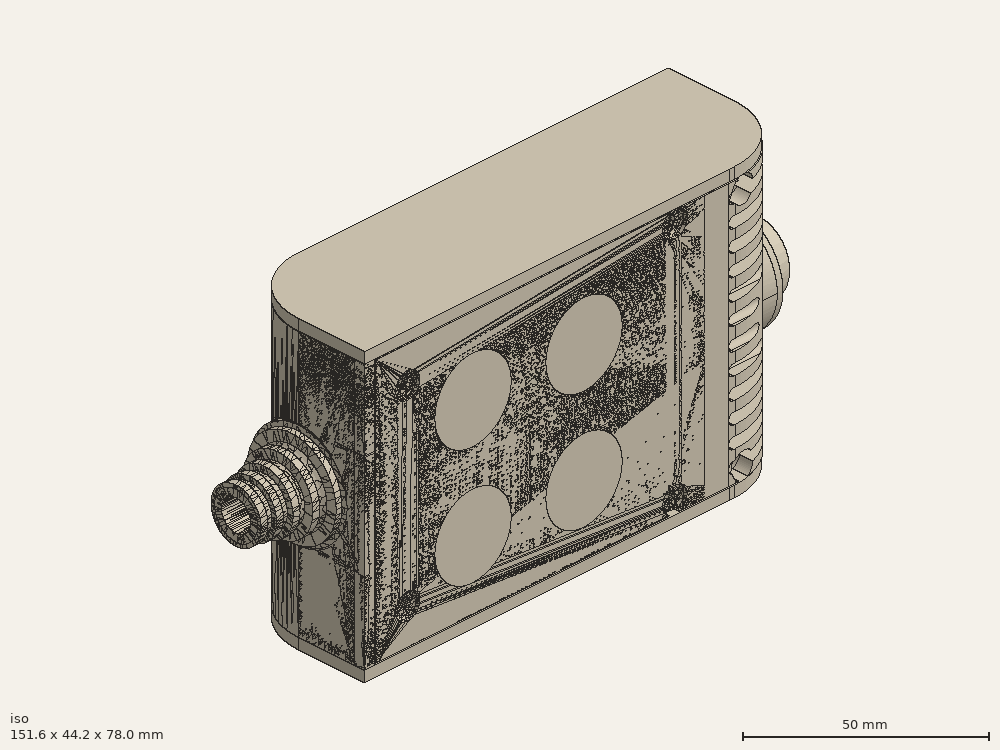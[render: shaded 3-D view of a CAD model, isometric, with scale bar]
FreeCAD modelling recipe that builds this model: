
FCSTD DOCUMENT  (FreeCAD 0.19R0.19.2)
Label: enclosure_181FCStd
License: All rights reserved
LicenseURL: http://en.wikipedia.org/wiki/All_rights_reserved
objects: Part::Revolution×152, Part::MultiFuse×146, Part::Feature×146, Sketcher::SketchObject×84, Part::Cut×70, Part::Cylinder×70, Part::Extrusion×67, Part::Fillet×58, Part::Box×36, App::MeasureDistance×4, PartDesign::Body×2, Image::ImagePlane×1
note: 831 computed .brp shape members not serialized (recipe doc carries the construction recipe); baked Part::Feature solids carry a one-line shape summary decoded from their .brp

FEATURE [Sketcher::SketchObject] Sketch  label="topSketch"
  FullyConstrained = true
  sketch-geometry (20):
    g0: LineSegment StartX=5.21097e-06 StartY=3 StartZ=0 EndX=5.21097e-06 EndY=19 EndZ=0
    g1: ArcOfCircle CenterX=19 CenterY=19 CenterZ=0 NormalX=0 NormalY=0 NormalZ=1 AngleXU=0 Radius=19 StartAngle=1.5708 EndAngle=3.14159
    g2: ArcOfCircle CenterX=19 CenterY=19 CenterZ=0 NormalX=0 NormalY=0 NormalZ=1 AngleXU=0 Radius=16 StartAngle=1.5708 EndAngle=3.14159
    g3: LineSegment StartX=114 StartY=35 StartZ=0 EndX=19 EndY=35 EndZ=0
    g4: LineSegment StartX=5.21097e-06 StartY=3 StartZ=0 EndX=5.21097e-06 EndY=0 EndZ=0
    g5: LineSegment StartX=3 StartY=0 StartZ=0 EndX=5.21097e-06 EndY=0 EndZ=0
    g6: LineSegment StartX=3 StartY=19 StartZ=0 EndX=3 EndY=0 EndZ=0
    g7: LineSegment StartX=19 StartY=38 StartZ=0 EndX=124 EndY=38 EndZ=0
    g8: Circle CenterX=119 CenterY=35 CenterZ=0 NormalX=0 NormalY=0 NormalZ=1 AngleXU=0 Radius=1
    g9: Circle CenterX=121 CenterY=35 CenterZ=0 NormalX=0 NormalY=0 NormalZ=1 AngleXU=0 Radius=1
    g10: Circle CenterX=121 CenterY=33 CenterZ=0 NormalX=0 NormalY=0 NormalZ=1 AngleXU=0 Radius=1
    g11: BSplineCurve PolesCount=3 KnotsCount=2 Degree=2 IsPeriodic=0
    g12: GeomPoint X=119 Y=35 Z=0
    g13: GeomPoint X=121 Y=33 Z=0
    g14: LineSegment StartX=119 StartY=35 StartZ=0 EndX=114 EndY=35 EndZ=0
    g15: ArcOfCircle CenterX=105 CenterY=19 CenterZ=0 NormalX=0 NormalY=0 NormalZ=1 AngleXU=0 Radius=19 StartAngle=5.7297 EndAngle=6.28319
    g16: ArcOfCircle CenterX=105 CenterY=19 CenterZ=0 NormalX=0 NormalY=0 NormalZ=1 AngleXU=0 Radius=16 StartAngle=5.60905 EndAngle=6.28319
    g17: LineSegment StartX=121 StartY=33 StartZ=0 EndX=121 EndY=19 EndZ=0
    g18: LineSegment StartX=124 StartY=38 StartZ=0 EndX=124 EndY=19 EndZ=0
    g19: LineSegment StartX=117.5 StartY=9.01251 StartZ=0 EndX=121.163 EndY=9.0125 EndZ=0
  constraints (46):
    c: Vertical(g0)
    c: Block(g0)
    c: Coincident(g1,g0)
    c: Block(g1)
    c: Coincident(g2,g1)
    c: Block(g2)
    c: Coincident(g3,g2)
    c: Horizontal(g3)
    c: Tangent(g3,g2)
    c: Coincident(g4,g0)
    c: Distance(g4) = 3
    c: Vertical(g4)
    c: Coincident(g5,g4)
    c: Horizontal(g5)
    c: Coincident(g6,g2)
    c: Coincident(g6,g5)
    c: Vertical(g6)
    c: Horizontal(g7)
    c: Distance(g7) = 105
    c: Coincident(g7,g1)
    c: Block(g3)
    c: Weight(g8) = 1
    c: Equal(g8,g9)
    c: Equal(g8,g10)
    c: InternalAlignment(g8,g11)
    c: InternalAlignment(g9,g11)
    c: InternalAlignment(g10,g11)
    c: InternalAlignment(g12,g11)
    c: InternalAlignment(g13,g11)
    c: Block(g11)
    c: Coincident(g14,g11)
    c: Coincident(g14,g3)
    c: Horizontal(g14)
    c: Block(g15)
    c: Coincident(g16,g15)
    c: Block(g16)
    c: Coincident(g17,g11)
    c: Coincident(g17,g16)
    c: Vertical(g17)
    c: Distance(g17) = 14
    c: Coincident(g18,g7)
    c: Coincident(g18,g15)
    c: Vertical(g18)
    c: Distance(g18) = 19
    c: Coincident(g19,g16)
    c: Coincident(g19,g15)
FEATURE [Sketcher::SketchObject] Sketch001  label="bottomSketch"
  FullyConstrained = true
  sketch-geometry (32):
    g0: LineSegment StartX=3.3 StartY=-6.03275e-07 StartZ=0 EndX=98 EndY=-6.03275e-07 EndZ=0
    g1: ArcOfCircle CenterX=98 CenterY=19 CenterZ=0 NormalX=0 NormalY=0 NormalZ=1 AngleXU=0 Radius=19 StartAngle=4.71239 EndAngle=5.71103
    g2: LineSegment StartX=6.3 StartY=8 StartZ=0 EndX=3.3 EndY=8 EndZ=0
    g3: LineSegment StartX=3.3 StartY=8 StartZ=0 EndX=3.3 EndY=-6.03275e-07 EndZ=0
    g4: ArcOfCircle CenterX=8.3 CenterY=5 CenterZ=0 NormalX=0 NormalY=0 NormalZ=1 AngleXU=0 Radius=2 StartAngle=3.14159 EndAngle=4.71239
    g5: LineSegment StartX=6.3 StartY=8 StartZ=0 EndX=6.3 EndY=5 EndZ=0
    g6: ArcOfCircle CenterX=98 CenterY=19 CenterZ=0 NormalX=0 NormalY=0 NormalZ=1 AngleXU=0 Radius=12.7 StartAngle=4.71239 EndAngle=6.28319
    g7: LineSegment StartX=94.7 StartY=3 StartZ=0 EndX=8.3 EndY=3 EndZ=0
    g8-g12: Circle x5 (B-spline internal-alignment scaffolding for g13; pole/knot coordinates omitted)
    g13: BSplineCurve PolesCount=5 KnotsCount=3 Degree=3 IsPeriodic=0
    g14: GeomPoint X=98 Y=6.3 Z=0
    g15: GeomPoint X=96.3938 Y=4.71946 Z=0
    g16: GeomPoint X=94.7 Y=3 Z=0
    g17-g23: Circle x7 (B-spline internal-alignment scaffolding for g24; pole/knot coordinates omitted)
    g24: BSplineCurve PolesCount=7 KnotsCount=5 Degree=3 IsPeriodic=0
    g25-g29: GeomPoint x5 (B-spline internal-alignment scaffolding for g24; pole/knot coordinates omitted)
    g30: ArcOfCircle CenterX=98 CenterY=19 CenterZ=0 NormalX=0 NormalY=0 NormalZ=1 AngleXU=0 Radius=15.7 StartAngle=5.81226 EndAngle=6.28319
    g31: LineSegment StartX=110.7 StartY=19 StartZ=0 EndX=113.7 EndY=19 EndZ=0
  constraints (41):
    c: Horizontal(g0)
    c: Coincident(g1,g0)
    c: Block(g1)
    c: Horizontal(g2)
    c: Distance(g2) = 3
    c: Coincident(g3,g2)
    c: Vertical(g3)
    c: Coincident(g3,g0)
    c: Block(g4)
    c: Block(g2)
    c: Coincident(g5,g2)
    c: Coincident(g5,g4)
    c: Vertical(g5)
    c: Coincident(g6,g1)
    c: Block(g6)
    c: Coincident(g7,g4)
    c: Horizontal(g7)
    c: Block(g0)
    c: Block(g7)
    c: Block(g3)
    c: Coincident(g13,g6)
    c: Weight(g8) = 1
    c: Equal(g8, g9-g12) x4
    c: Coincident(g13,g7)
    c: InternalAlignment(g8-g12 -> g13) x5
    c: InternalAlignment(g14,g13)
    c: InternalAlignment(g15,g13)
    c: InternalAlignment(g16,g13)
    c: Block(g13)
    c: Weight(g17) = 1
    c: Equal(g17, g18-g23) x6
    c: Coincident(g24,g1)
    c: InternalAlignment(g17-g23 -> g24) x7
    c: InternalAlignment(g25-g29 -> g24) x5
    c: Block(g24)
    c: Coincident(g30,g24)
    c: Coincident(g31,g6)
    c: Coincident(g31,g30)
    c: Horizontal(g31)
    c: Block(g31)
    c: Block(g30)
FEATURE [Part::Extrusion] Extrude  label="top"
  Base = -> Sketch
  Dir = (0,0,1)
  DirMode = 2
  FaceMakerClass = Part::FaceMakerBullseye
  LengthFwd = 72
  LengthRev = 0
  Solid = true
  Symmetric = false
FEATURE [Part::Extrusion] Extrude001  label="bottom"
  Base = -> Sketch001
  Dir = (0,0,1)
  DirMode = 2
  FaceMakerClass = Part::FaceMakerBullseye
  LengthFwd = 71.4
  LengthRev = 0
  Placement = pos=(0,0,0.3) rot=(0,0,1;0rad)
  Solid = true
  Symmetric = false
FEATURE [Sketcher::SketchObject] Sketch002  label="topSketch001"
  FullyConstrained = true
  sketch-geometry (8):
    g0: ArcOfCircle CenterX=19 CenterY=19.0975 CenterZ=0 NormalX=0 NormalY=0 NormalZ=1 AngleXU=0 Radius=18.9025 StartAngle=1.5708 EndAngle=3.14674
    g1: LineSegment StartX=0.0977805 StartY=19.0003 StartZ=0 EndX=0.0977805 EndY=0.000251602 EndZ=0
    g2: LineSegment StartX=19 StartY=38 StartZ=0 EndX=124 EndY=38 EndZ=0
    g3: LineSegment StartX=0.0977805 StartY=0.000251602 StartZ=0 EndX=105.098 EndY=0.000251602 EndZ=0
    g4: LineSegment StartX=124 StartY=38 StartZ=0 EndX=125.616 EndY=38 EndZ=0
    g5: LineSegment StartX=105.098 StartY=0.000251602 StartZ=0 EndX=106.713 EndY=0.000251602 EndZ=0
    g6: ArcOfCircle CenterX=106.616 CenterY=19 CenterZ=0 NormalX=0 NormalY=0 NormalZ=1 AngleXU=0 Radius=19 StartAngle=4.71754 EndAngle=6.28319
    g7: LineSegment StartX=125.616 StartY=38 StartZ=0 EndX=125.616 EndY=19 EndZ=0
  constraints (21):
    c: Block(g0)
    c: Coincident(g1,g0)
    c: Vertical(g1)
    c: Horizontal(g2)
    c: Distance(g2) = 105
    c: Coincident(g2,g0)
    c: Distance(g1) = 19
    c: Coincident(g3,g1)
    c: Horizontal(g3)
    c: Distance(g3) = 105
    c: Coincident(g4,g2)
    c: Horizontal(g4)
    c: Distance(g4) = 1.61553
    c: Horizontal(g5)
    c: Equal(g4,g5) = 1.61553
    c: Coincident(g5,g3)
    c: Block(g6)
    c: Coincident(g6,g5)
    c: Coincident(g7,g4)
    c: Coincident(g7,g6)
    c: Vertical(g7)
FEATURE [Part::Extrusion] Extrude002  label="sideA"
  Base = -> Sketch002
  Dir = (0,0,1)
  DirMode = 2
  FaceMakerClass = Part::FaceMakerBullseye
  LengthFwd = 3
  LengthRev = 0
  Placement = pos=(0,0,-3) rot=(0,0,1;0rad)
  Solid = true
  Symmetric = false
FEATURE [Sketcher::SketchObject] Sketch003  label="topSketch002"
  FullyConstrained = true
  sketch-geometry (6):
    g0: LineSegment StartX=19 StartY=38 StartZ=0 EndX=117 EndY=38 EndZ=0
    g1: ArcOfCircle CenterX=19 CenterY=19 CenterZ=0 NormalX=0 NormalY=0 NormalZ=1 AngleXU=0 Radius=19 StartAngle=1.5708 EndAngle=3.14159
    g2: LineSegment StartX=117 StartY=38 StartZ=0 EndX=117 EndY=19 EndZ=0
    g3: LineSegment StartX=98 StartY=1.0161e-12 StartZ=0 EndX=5.22862e-06 EndY=1.0161e-12 EndZ=0
    g4: LineSegment StartX=5.22862e-06 StartY=19 StartZ=0 EndX=5.22862e-06 EndY=1.0161e-12 EndZ=0
    g5: ArcOfCircle CenterX=98 CenterY=19 CenterZ=0 NormalX=0 NormalY=0 NormalZ=1 AngleXU=0 Radius=19 StartAngle=4.71239 EndAngle=6.28319
  constraints (16):
    c: Horizontal(g0)
    c: Distance(g0) = 98
    c: Coincident(g1,g0)
    c: Block(g1)
    c: Coincident(g2,g0)
    c: Vertical(g2)
    c: Distance(g2) = 19
    c: Horizontal(g3)
    c: Coincident(g4,g1)
    c: Vertical(g4)
    c: Coincident(g3,g4)
    c: Block(g3)
    c: Coincident(g5,g2)
    c: Coincident(g5,g3)
    c: Block(g0)
    c: Block(g5)
FEATURE [Sketcher::SketchObject] Sketch004
  FullyConstrained = true
  MapMode = 3
  Placement = pos=(0,0,0) rot=(1,0,0;1.5708rad)
  Support = -> [Extrude]
  sketch-geometry (8):
    g0: Circle CenterX=80.351 CenterY=-67.6202 CenterZ=0 NormalX=0 NormalY=0 NormalZ=1 AngleXU=0 Radius=2
    g1: Circle CenterX=80.351 CenterY=-67.6202 CenterZ=0 NormalX=0 NormalY=0 NormalZ=1 AngleXU=0 Radius=3
    g2: Circle CenterX=80.351 CenterY=-4.92017 CenterZ=0 NormalX=0 NormalY=0 NormalZ=1 AngleXU=0 Radius=2
    g3: Circle CenterX=80.351 CenterY=-4.92017 CenterZ=0 NormalX=0 NormalY=0 NormalZ=1 AngleXU=0 Radius=3
    g4: Circle CenterX=23.851 CenterY=-4.92017 CenterZ=0 NormalX=0 NormalY=0 NormalZ=1 AngleXU=0 Radius=2
    g5: Circle CenterX=23.851 CenterY=-4.92017 CenterZ=0 NormalX=0 NormalY=0 NormalZ=1 AngleXU=0 Radius=3
    g6: Circle CenterX=23.851 CenterY=-67.6202 CenterZ=0 NormalX=0 NormalY=0 NormalZ=1 AngleXU=0 Radius=2
    g7: Circle CenterX=23.851 CenterY=-67.6202 CenterZ=0 NormalX=0 NormalY=0 NormalZ=1 AngleXU=0 Radius=3
  constraints (8):
    c: Block(g3)
    c: Block(g2)
    c: Block(g1)
    c: Block(g0)
    c: Block(g6)
    c: Block(g7)
    c: Block(g4)
    c: Block(g5)
FEATURE [Part::Extrusion] Extrude004
  Base = -> Sketch004
  Dir = (0,-1,2e-16)
  DirMode = 2
  FaceMakerClass = Part::FaceMakerBullseye
  LengthFwd = 6
  LengthRev = 0
  Placement = pos=(0,9,0) rot=(0,0,1;0rad)
  Solid = true
  Symmetric = false
FEATURE [Sketcher::SketchObject] Sketch005
  FullyConstrained = true
  MapMode = 3
  Placement = pos=(0,0,0) rot=(1,0,0;1.5708rad)
  Support = -> [Extrude]
  sketch-geometry (8):
    g0: Circle CenterX=80.351 CenterY=-67.6202 CenterZ=0 NormalX=0 NormalY=0 NormalZ=1 AngleXU=0 Radius=3
    g1: Circle CenterX=80.351 CenterY=-4.92017 CenterZ=0 NormalX=0 NormalY=0 NormalZ=1 AngleXU=0 Radius=3
    g2: Circle CenterX=23.851 CenterY=-4.92017 CenterZ=0 NormalX=0 NormalY=0 NormalZ=1 AngleXU=0 Radius=3
    g3: Circle CenterX=23.851 CenterY=-67.6202 CenterZ=0 NormalX=0 NormalY=0 NormalZ=1 AngleXU=0 Radius=3
    g4: Circle CenterX=23.851 CenterY=-67.6202 CenterZ=0 NormalX=0 NormalY=0 NormalZ=1 AngleXU=0 Radius=5
    g5: Circle CenterX=80.351 CenterY=-67.6202 CenterZ=0 NormalX=0 NormalY=0 NormalZ=1 AngleXU=0 Radius=5
    g6: Circle CenterX=23.851 CenterY=-4.92017 CenterZ=0 NormalX=0 NormalY=0 NormalZ=1 AngleXU=0 Radius=5
    g7: Circle CenterX=80.351 CenterY=-4.92017 CenterZ=0 NormalX=0 NormalY=0 NormalZ=1 AngleXU=0 Radius=5
  constraints (8):
    c: Block(g1)
    c: Block(g0)
    c: Block(g3)
    c: Block(g2)
    c: Block(g5)
    c: Block(g4)
    c: Block(g6)
    c: Block(g7)
FEATURE [Part::Extrusion] Extrude005
  Base = -> Sketch005
  Dir = (0,-1,2e-16)
  DirMode = 2
  FaceMakerClass = Part::FaceMakerBullseye
  LengthFwd = 2
  LengthRev = 0
  Solid = true
  Symmetric = false
FEATURE [Sketcher::SketchObject] Sketch006
  FullyConstrained = true
  MapMode = 3
  Placement = pos=(0,0,0) rot=(1,0,0;1.5708rad)
  sketch-geometry (8):
    g0: Circle CenterX=80.351 CenterY=-67.6202 CenterZ=0 NormalX=0 NormalY=0 NormalZ=1 AngleXU=0 Radius=3
    g1: Circle CenterX=80.351 CenterY=-4.92017 CenterZ=0 NormalX=0 NormalY=0 NormalZ=1 AngleXU=0 Radius=3
    g2: Circle CenterX=23.851 CenterY=-4.92017 CenterZ=0 NormalX=0 NormalY=0 NormalZ=1 AngleXU=0 Radius=3
    g3: Circle CenterX=23.851 CenterY=-67.6202 CenterZ=0 NormalX=0 NormalY=0 NormalZ=1 AngleXU=0 Radius=3
    g4: Circle CenterX=23.851 CenterY=-67.6202 CenterZ=0 NormalX=0 NormalY=0 NormalZ=1 AngleXU=0 Radius=5
    g5: Circle CenterX=80.351 CenterY=-67.6202 CenterZ=0 NormalX=0 NormalY=0 NormalZ=1 AngleXU=0 Radius=5
    g6: Circle CenterX=23.851 CenterY=-4.92017 CenterZ=0 NormalX=0 NormalY=0 NormalZ=1 AngleXU=0 Radius=5
    g7: Circle CenterX=80.351 CenterY=-4.92017 CenterZ=0 NormalX=0 NormalY=0 NormalZ=1 AngleXU=0 Radius=5
  constraints (8):
    c: Block(g1)
    c: Block(g0)
    c: Block(g3)
    c: Block(g2)
    c: Block(g5)
    c: Block(g4)
    c: Block(g6)
    c: Block(g7)
FEATURE [Part::Extrusion] Extrude007
  Base = -> Sketch006
  Dir = (0,-1,2e-16)
  DirMode = 2
  FaceMakerClass = Part::FaceMakerBullseye
  LengthFwd = 2
  LengthRev = 0
  Solid = true
  Symmetric = false
FEATURE [Part::Fillet] Fillet
  Base = -> Extrude007
  Edges = 4 edges r=1.99: [Edge6,Edge12,Edge18,Edge24]
FEATURE [Part::Cut] Cut
  Base = -> Extrude005
  Placement = pos=(0,5,0) rot=(0,0,1;0rad)
  Tool = -> Fillet
FEATURE [Part::MultiFuse] Fusion  label="pCBScrews"
  Placement = pos=(-2.5,0,72.3) rot=(0,0,1;0rad)
  Shapes = -> [Extrude004,Cut]
FEATURE [App::MeasureDistance] Distance  label="Distance: 0.69 mm"
  Distance = 0.685967
  P1 = (24.0138,2.9647,0.3)
  P2 = (23.8901,3,-0.373787)
FEATURE [App::MeasureDistance] Distance001  label="Distance: 0.53 mm"
  Distance = 0.533607
  P1 = (80.2939,3,72.2334)
  P2 = (80.281,2.99661,71.7)
FEATURE [Part::Fillet] Fillet001
  Base = -> Extrude001
  Edges = 1 edges r=2.4: [Edge17]
FEATURE [Part::Fillet] Fillet002  label="bottom001"
  Base = -> Fillet001
  Edges = 1 edges r=2.4: [Edge36]
FEATURE [Part::Fillet] Fillet003  label="top001"
  Base = -> Extrude
  Edges = 1 edges r=2: [Edge1]
FEATURE [Sketcher::SketchObject] Sketch007
  FullyConstrained = true
  sketch-geometry (16):
    g0: LineSegment StartX=4 StartY=0 StartZ=0 EndX=4 EndY=2.4 EndZ=0
    g1: LineSegment StartX=4 StartY=2.4 StartZ=0 EndX=7 EndY=2.4 EndZ=0
    g2: LineSegment StartX=4 StartY=0 StartZ=0 EndX=5.7 EndY=0 EndZ=0
    g3: LineSegment StartX=5.7 StartY=0 StartZ=0 EndX=5.7 EndY=-5.6 EndZ=0
    g4-g8: Circle x5 (B-spline internal-alignment scaffolding for g9; pole/knot coordinates omitted)
    g9: BSplineCurve PolesCount=5 KnotsCount=3 Degree=3 IsPeriodic=0
    g10: GeomPoint X=7 Y=2.4 Z=0
    g11: GeomPoint X=10.4582 Y=-1.55472 Z=0
    g12: GeomPoint X=14 Y=-5.6 Z=0
    g13: LineSegment StartX=14 StartY=-5.6 StartZ=0 EndX=14 EndY=-14.1 EndZ=0
    g14: LineSegment StartX=14 StartY=-14.1 StartZ=0 EndX=6.5 EndY=-14.1 EndZ=0
    g15: LineSegment StartX=5.7 StartY=-5.6 StartZ=0 EndX=6.5 EndY=-14.1 EndZ=0
  constraints (28):
    c: Distance(g0) = 2.4
    c: Vertical(g0)
    c: Block(g0)
    c: Coincident(g1,g0)
    c: Horizontal(g1)
    c: Distance(g1) = 3
    c: Coincident(g2,g0)
    c: Horizontal(g2)
    c: Distance(g2) = 1.7
    c: Coincident(g3,g2)
    c: Vertical(g3)
    c: Distance(g3) = 5.6
    c: Coincident(g9,g1)
    c: Weight(g4) = 1
    c: Equal(g4, g5-g8) x4
    c: InternalAlignment(g4-g8 -> g9) x5
    c: InternalAlignment(g10,g9)
    c: InternalAlignment(g11,g9)
    c: InternalAlignment(g12,g9)
    c: Block(g9)
    c: Coincident(g13,g9)
    c: Vertical(g13)
    c: Distance(g13) = 8.5
    c: Coincident(g14,g13)
    c: Horizontal(g14)
    c: Distance(g14) = 7.5
    c: Coincident(g15,g3)
    c: Coincident(g15,g14)
FEATURE [Part::Feature] Face
  shape: bbox 10 x 16.5 x 2e-07 mm, 1 faces, 0 solids (baked)
FEATURE [Part::Revolution] Revolve  label="plugHousing"
  Angle = 360
  Axis = (0,1,0)
  Base = (0,0,0)
  FaceMakerClass = Part::FaceMakerBullseye
  Placement = pos=(0,0,36.15) rot=(0,0,1;0rad)
  Solid = false
  Source = -> Face
  Symmetric = false
FEATURE [Part::Feature] Face001
  shape: bbox 10 x 16.5 x 2e-07 mm, 1 faces, 0 solids (baked)
FEATURE [Part::Revolution] Revolve001  label="plugHousing001"
  Angle = 360
  Axis = (0,1,0)
  Base = (0,0,0)
  FaceMakerClass = Part::FaceMakerBullseye
  Placement = pos=(0,0,36.15) rot=(0,0,1;0rad)
  Solid = false
  Source = -> Face001
  Symmetric = false
FEATURE [Part::MultiFuse] Fusion001  label="plugHousing002"
  Placement = pos=(0,0,0) rot=(0,0,1;1.5708rad)
  Shapes = -> [Revolve001,Revolve]
FEATURE [Part::Feature] Face002
  shape: bbox 10 x 16.5 x 2e-07 mm, 1 faces, 0 solids (baked)
FEATURE [Part::Revolution] Revolve003  label="plugHousing005"
  Angle = 360
  Axis = (0,1,0)
  Base = (0,0,0)
  FaceMakerClass = Part::FaceMakerBullseye
  Placement = pos=(0,0,36.15) rot=(0,0,1;0rad)
  Solid = false
  Source = -> Face002
  Symmetric = false
FEATURE [Part::Feature] Face003
  shape: bbox 10 x 16.5 x 2e-07 mm, 1 faces, 0 solids (baked)
FEATURE [Part::Revolution] Revolve002  label="plugHousing003"
  Angle = 360
  Axis = (0,1,0)
  Base = (0,0,0)
  FaceMakerClass = Part::FaceMakerBullseye
  Placement = pos=(0,0,36.15) rot=(0,0,1;0rad)
  Solid = false
  Source = -> Face003
  Symmetric = false
FEATURE [Part::MultiFuse] Fusion002  label="plugHousing004"
  Placement = pos=(0,0,0) rot=(0,0,1;1.5708rad)
  Shapes = -> [Revolve002,Revolve003]
FEATURE [Part::MultiFuse] Fusion003  label="plugHousing006"
  Placement = pos=(0,19,0) rot=(0,0,1;3.14159rad)
  Shapes = -> [Fusion002,Fusion001]
FEATURE [Part::Feature] Face004
  shape: bbox 10 x 16.5 x 2e-07 mm, 1 faces, 0 solids (baked)
FEATURE [Part::Revolution] Revolve006  label="plugHousing010"
  Angle = 360
  Axis = (0,1,0)
  Base = (0,0,0)
  FaceMakerClass = Part::FaceMakerBullseye
  Placement = pos=(0,0,36.15) rot=(0,0,1;0rad)
  Solid = false
  Source = -> Face004
  Symmetric = false
FEATURE [Part::Feature] Face005
  shape: bbox 10 x 16.5 x 2e-07 mm, 1 faces, 0 solids (baked)
FEATURE [Part::Revolution] Revolve007  label="plugHousing011"
  Angle = 360
  Axis = (0,1,0)
  Base = (0,0,0)
  FaceMakerClass = Part::FaceMakerBullseye
  Placement = pos=(0,0,36.15) rot=(0,0,1;0rad)
  Solid = false
  Source = -> Face005
  Symmetric = false
FEATURE [Part::Feature] Face006
  shape: bbox 10 x 16.5 x 2e-07 mm, 1 faces, 0 solids (baked)
FEATURE [Part::Revolution] Revolve004  label="plugHousing007"
  Angle = 360
  Axis = (0,1,0)
  Base = (0,0,0)
  FaceMakerClass = Part::FaceMakerBullseye
  Placement = pos=(0,0,36.15) rot=(0,0,1;0rad)
  Solid = false
  Source = -> Face006
  Symmetric = false
FEATURE [Part::MultiFuse] Fusion004  label="plugHousing009"
  Placement = pos=(0,0,0) rot=(0,0,1;1.5708rad)
  Shapes = -> [Revolve004,Revolve007]
FEATURE [Part::Feature] Face007
  shape: bbox 10 x 16.5 x 2e-07 mm, 1 faces, 0 solids (baked)
FEATURE [Part::Revolution] Revolve005  label="plugHousing008"
  Angle = 360
  Axis = (0,1,0)
  Base = (0,0,0)
  FaceMakerClass = Part::FaceMakerBullseye
  Placement = pos=(0,0,36.15) rot=(0,0,1;0rad)
  Solid = false
  Source = -> Face007
  Symmetric = false
FEATURE [Part::MultiFuse] Fusion005  label="plugHousing012"
  Placement = pos=(0,0,0) rot=(0,0,1;1.5708rad)
  Shapes = -> [Revolve006,Revolve005]
FEATURE [Part::MultiFuse] Fusion006  label="plugHousing013"
  Placement = pos=(0,19,0) rot=(0,0,1;3.14159rad)
  Shapes = -> [Fusion005,Fusion004]
FEATURE [Part::MultiFuse] Fusion007  label="plugHousing014"
  Placement = pos=(122.621,0,-0.15) rot=(0,0,1;0rad)
  Shapes = -> [Fusion003,Fusion006]
FEATURE [Part::Cylinder] Cylinder002
  Angle = 360
  AttacherType = Attacher::AttachEngine3D
  Height = 20
  Placement = pos=(0,0,36.15) rot=(0,0,1;0rad)
  Radius = 4
FEATURE [Part::Cylinder] Cylinder003
  Angle = 360
  AttacherType = Attacher::AttachEngine3D
  Height = 10
  Placement = pos=(0,0,36.15) rot=(0,0,1;0rad)
  Radius = 4
FEATURE [Part::MultiFuse] Fusion009  label="removeToCreateHoleForPlugHousing"
  Placement = pos=(70,19,36.15) rot=(0,1,0;1.5708rad)
  Shapes = -> [Cylinder002,Cylinder003]
FEATURE [Part::Cylinder] Cylinder004
  Angle = 360
  AttacherType = Attacher::AttachEngine3D
  Height = 20
  Placement = pos=(0,0,36.15) rot=(0,0,1;0rad)
  Radius = 4
FEATURE [Part::Cylinder] Cylinder005
  Angle = 360
  AttacherType = Attacher::AttachEngine3D
  Height = 10
  Placement = pos=(0,0,36.15) rot=(0,0,1;0rad)
  Radius = 4
FEATURE [Part::MultiFuse] Fusion010  label="removeToCreateHoleForPlugHousing001"
  Placement = pos=(70,19,36.15) rot=(0,1,0;1.5708rad)
  Shapes = -> [Cylinder004,Cylinder005]
FEATURE [Part::Cut] Cut001
  Base = -> Fillet003
  Tool = -> Fusion010
FEATURE [Part::Cut] Cut002  label="Bottom"
  Base = -> Fillet002
  Tool = -> Fusion009
FEATURE [Part::Feature] Face008
  shape: bbox 10 x 16.5 x 2e-07 mm, 1 faces, 0 solids (baked)
FEATURE [Part::Revolution] Revolve011  label="plugHousing021"
  Angle = 360
  Axis = (0,1,0)
  Base = (0,0,0)
  FaceMakerClass = Part::FaceMakerBullseye
  Placement = pos=(0,0,36.15) rot=(0,0,1;0rad)
  Solid = false
  Source = -> Face008
  Symmetric = false
FEATURE [Part::Feature] Face009
  shape: bbox 10 x 16.5 x 2e-07 mm, 1 faces, 0 solids (baked)
FEATURE [Part::Revolution] Revolve012  label="plugHousing022"
  Angle = 360
  Axis = (0,1,0)
  Base = (0,0,0)
  FaceMakerClass = Part::FaceMakerBullseye
  Placement = pos=(0,0,36.15) rot=(0,0,1;0rad)
  Solid = false
  Source = -> Face009
  Symmetric = false
FEATURE [Part::Feature] Face010 .. Face013  x4 (patterned run collapsed; names and placements below)
  shape: bbox 10 x 16.5 x 2e-07 mm, 1 faces, 0 solids (baked)
FEATURE [Part::Revolution] Revolve015  label="plugHousing027"
  Angle = 360
  Axis = (0,1,0)
  Base = (0,0,0)
  FaceMakerClass = Part::FaceMakerBullseye
  Placement = pos=(0,0,36.15) rot=(0,0,1;0rad)
  Solid = false
  Source = -> Face013
  Symmetric = false
FEATURE [Part::Feature] Face014
  shape: bbox 10 x 16.5 x 2e-07 mm, 1 faces, 0 solids (baked)
FEATURE [Part::Feature] Face015
  shape: bbox 10 x 16.5 x 2e-07 mm, 1 faces, 0 solids (baked)
FEATURE [Part::Feature] Face016
  shape: bbox 10 x 16.5 x 2e-07 mm, 1 faces, 0 solids (baked)
FEATURE [Part::Revolution] Revolve019  label="plugHousing033"
  Angle = 360
  Axis = (0,1,0)
  Base = (0,0,0)
  FaceMakerClass = Part::FaceMakerBullseye
  Placement = pos=(0,0,36.15) rot=(0,0,1;0rad)
  Solid = false
  Source = -> Face016
  Symmetric = false
FEATURE [Part::Feature] Face017
  shape: bbox 10 x 16.5 x 2e-07 mm, 1 faces, 0 solids (baked)
FEATURE [Part::Revolution] Revolve020  label="plugHousing034"
  Angle = 360
  Axis = (0,1,0)
  Base = (0,0,0)
  FaceMakerClass = Part::FaceMakerBullseye
  Placement = pos=(0,0,36.15) rot=(0,0,1;0rad)
  Solid = false
  Source = -> Face017
  Symmetric = false
FEATURE [Part::Feature] Face018
  shape: bbox 10 x 16.5 x 2e-07 mm, 1 faces, 0 solids (baked)
FEATURE [Part::Revolution] Revolve016  label="plugHousing030"
  Angle = 360
  Axis = (0,1,0)
  Base = (0,0,0)
  FaceMakerClass = Part::FaceMakerBullseye
  Placement = pos=(0,0,36.15) rot=(0,0,1;0rad)
  Solid = false
  Source = -> Face018
  Symmetric = false
FEATURE [Part::MultiFuse] Fusion020  label="plugHousing038"
  Placement = pos=(0,0,0) rot=(0,0,1;1.5708rad)
  Shapes = -> [Revolve016,Revolve020]
FEATURE [Part::Feature] Face019
  shape: bbox 10 x 16.5 x 2e-07 mm, 1 faces, 0 solids (baked)
FEATURE [Part::Feature] Face020
  shape: bbox 10 x 16.5 x 2e-07 mm, 1 faces, 0 solids (baked)
FEATURE [Part::Revolution] Revolve017  label="plugHousing031"
  Angle = 360
  Axis = (0,1,0)
  Base = (0,0,0)
  FaceMakerClass = Part::FaceMakerBullseye
  Placement = pos=(0,0,36.15) rot=(0,0,1;0rad)
  Solid = false
  Source = -> Face020
  Symmetric = false
FEATURE [Part::MultiFuse] Fusion021  label="plugHousing039"
  Placement = pos=(0,0,0) rot=(0,0,1;1.5708rad)
  Shapes = -> [Revolve019,Revolve017]
FEATURE [Part::MultiFuse] Fusion023  label="plugHousing041"
  Placement = pos=(0,19,0) rot=(0,0,1;3.14159rad)
  Shapes = -> [Fusion021,Fusion020]
FEATURE [Part::Revolution] Revolve022  label="plugHousing043"
  Angle = 360
  Axis = (0,1,0)
  Base = (0,0,0)
  FaceMakerClass = Part::FaceMakerBullseye
  Placement = pos=(0,0,36.15) rot=(0,0,1;0rad)
  Solid = false
  Source = -> Face019
  Symmetric = false
FEATURE [Part::Feature] Face021
  shape: bbox 10 x 16.5 x 2e-07 mm, 1 faces, 0 solids (baked)
FEATURE [Part::Revolution] Revolve023  label="plugHousing044"
  Angle = 360
  Axis = (0,1,0)
  Base = (0,0,0)
  FaceMakerClass = Part::FaceMakerBullseye
  Placement = pos=(0,0,36.15) rot=(0,0,1;0rad)
  Solid = false
  Source = -> Face021
  Symmetric = false
FEATURE [Part::Feature] Face022
  shape: bbox 10 x 16.5 x 2e-07 mm, 1 faces, 0 solids (baked)
FEATURE [Part::Revolution] Revolve018  label="plugHousing032"
  Angle = 360
  Axis = (0,1,0)
  Base = (0,0,0)
  FaceMakerClass = Part::FaceMakerBullseye
  Placement = pos=(0,0,36.15) rot=(0,0,1;0rad)
  Solid = false
  Source = -> Face022
  Symmetric = false
FEATURE [Part::MultiFuse] Fusion022  label="plugHousing040"
  Placement = pos=(0,0,0) rot=(0,0,1;1.5708rad)
  Shapes = -> [Revolve018,Revolve023]
FEATURE [Part::Feature] Face023
  shape: bbox 10 x 16.5 x 2e-07 mm, 1 faces, 0 solids (baked)
FEATURE [Part::Revolution] Revolve021  label="plugHousing035"
  Angle = 360
  Axis = (0,1,0)
  Base = (0,0,0)
  FaceMakerClass = Part::FaceMakerBullseye
  Placement = pos=(0,0,36.15) rot=(0,0,1;0rad)
  Solid = false
  Source = -> Face023
  Symmetric = false
FEATURE [Part::MultiFuse] Fusion018  label="plugHousing036"
  Placement = pos=(0,0,0) rot=(0,0,1;1.5708rad)
  Shapes = -> [Revolve022,Revolve021]
FEATURE [Part::MultiFuse] Fusion019  label="plugHousing037"
  Placement = pos=(0,19,0) rot=(0,0,1;3.14159rad)
  Shapes = -> [Fusion018,Fusion022]
FEATURE [Part::MultiFuse] Fusion024  label="plugHousing042"
  Placement = pos=(122.621,0,-0.15) rot=(0,0,1;0rad)
  Shapes = -> [Fusion023,Fusion019]
FEATURE [Part::Cylinder] Cylinder006
  Angle = 360
  AttacherType = Attacher::AttachEngine3D
  Height = 20
  Placement = pos=(0,0,36.15) rot=(0,0,1;0rad)
  Radius = 14.3
FEATURE [Part::Cylinder] Cylinder007
  Angle = 360
  AttacherType = Attacher::AttachEngine3D
  Height = 10
  Placement = pos=(0,0,36.15) rot=(0,0,1;0rad)
  Radius = 4
FEATURE [Part::MultiFuse] Fusion026  label="removeToCreteHoleForPlugHousing"
  Placement = pos=(70,19,36) rot=(0,1,0;1.5708rad)
  Shapes = -> [Cylinder006,Cylinder007]
FEATURE [Part::Box] Box001  label="Cube001"
  AttacherType = Attacher::AttachEngine3D
  Height = 28
  Length = 3
  Placement = pos=(110.7,19,22) rot=(0,0,1;0rad)
  Width = 15.7
FEATURE [Part::Cut] Cut003  label="top002"
  Base = -> Cut001
  Tool = -> Fusion007
FEATURE [Part::Revolution] Revolve008  label="plugHousing015"
  Angle = 360
  Axis = (0,1,0)
  Base = (0,0,0)
  FaceMakerClass = Part::FaceMakerBullseye
  Placement = pos=(0,0,36.15) rot=(0,0,1;0rad)
  Solid = false
  Source = -> Face010
  Symmetric = false
FEATURE [Part::MultiFuse] Fusion013  label="plugHousing020"
  Placement = pos=(0,0,0) rot=(0,0,1;1.5708rad)
  Shapes = -> [Revolve008,Revolve012]
FEATURE [Part::Cut] Cut004  label="top003"
  Base = -> Cut003
  Placement = pos=(1,0,0) rot=(0,0,1;0rad)
  Tool = -> Fusion026
FEATURE [Part::Cylinder] Cylinder008
  Angle = 360
  AttacherType = Attacher::AttachEngine3D
  Height = 20
  Placement = pos=(0,0,36.15) rot=(0,0,1;0rad)
  Radius = 10.3
FEATURE [Part::Cylinder] Cylinder009
  Angle = 360
  AttacherType = Attacher::AttachEngine3D
  Height = 10
  Placement = pos=(0,0,36.15) rot=(0,0,1;0rad)
  Radius = 4
FEATURE [Part::MultiFuse] Fusion027  label="removeToCreteHoleForPlugHousing001"
  Placement = pos=(70,19,36) rot=(0,1,0;1.5708rad)
  Shapes = -> [Cylinder008,Cylinder009]
FEATURE [Part::Cut] Cut005  label="plugHousingTab"
  Base = -> Box001
  Tool = -> Fusion027
FEATURE [Part::MultiFuse] Fusion028  label="plugHousing045"
  Shapes = -> [Fusion024,Cut005]
FEATURE [Part::Box] Box002  label="Cube002"
  AttacherType = Attacher::AttachEngine3D
  Height = 28.8
  Length = 3
  Placement = pos=(107.3,28,21.6) rot=(0,0,1;0rad)
  Width = 7
FEATURE [Part::Box] Box003  label="Cube003"
  AttacherType = Attacher::AttachEngine3D
  Height = 3
  Length = 6.4
  Placement = pos=(107.3,28,18.6) rot=(0,0,1;0rad)
  Width = 7
FEATURE [Part::Box] Box004  label="Cube004"
  AttacherType = Attacher::AttachEngine3D
  Height = 3
  Length = 6.4
  Placement = pos=(107.3,28,50.4) rot=(0,0,1;0rad)
  Width = 7
FEATURE [Part::MultiFuse] Fusion029  label="plugHousingBracketHolder"
  Shapes = -> [Box004,Box002,Box003]
FEATURE [Part::Cylinder] Cylinder010
  Angle = 360
  AttacherType = Attacher::AttachEngine3D
  Height = 20
  Placement = pos=(0,0,36.15) rot=(0,0,1;0rad)
  Radius = 14.3
FEATURE [Part::Cylinder] Cylinder011
  Angle = 360
  AttacherType = Attacher::AttachEngine3D
  Height = 10
  Placement = pos=(0,0,36.15) rot=(0,0,1;0rad)
  Radius = 4
FEATURE [Part::MultiFuse] Fusion030  label="removeToCreteHoleForPlugHousing002"
  Placement = pos=(70,19,36) rot=(0,1,0;1.5708rad)
  Shapes = -> [Cylinder010,Cylinder011]
FEATURE [Part::Cut] Cut006  label="plugHousingBracketHolder001"
  Base = -> Fusion029
  Tool = -> Fusion030
FEATURE [Part::Cylinder] Cylinder012
  Angle = 360
  AttacherType = Attacher::AttachEngine3D
  Height = 20
  Placement = pos=(0,0,36.15) rot=(0,0,1;0rad)
  Radius = 7
FEATURE [Part::Cylinder] Cylinder013
  Angle = 360
  AttacherType = Attacher::AttachEngine3D
  Height = 10
  Placement = pos=(0,0,36.15) rot=(0,0,1;0rad)
  Radius = 4
FEATURE [Part::MultiFuse] Fusion032  label="removeToCreteHoleForPlugHousing003"
  Placement = pos=(70,19,36) rot=(0,1,0;1.5708rad)
  Shapes = -> [Cylinder012,Cylinder013]
FEATURE [Part::Cut] Cut007  label="bottom002"
  Base = -> Cut002
  Tool = -> Fusion032
FEATURE [Sketcher::SketchObject] Sketch008
  FullyConstrained = true
  sketch-geometry (54):
    g0: LineSegment StartX=-4.2 StartY=0 StartZ=0 EndX=-6.2 EndY=0 EndZ=0
    g1: LineSegment StartX=-14 StartY=-18 StartZ=0 EndX=-14 EndY=-26.5 EndZ=0
    g2: LineSegment StartX=-4.2 StartY=0 StartZ=0 EndX=-4.2 EndY=-13.4877 EndZ=0
    g3: Circle CenterX=-4.2 CenterY=-13.4877 CenterZ=0 NormalX=0 NormalY=0 NormalZ=1 AngleXU=0 Radius=1
    g4: Circle CenterX=-4.2 CenterY=-26.5 CenterZ=0 NormalX=0 NormalY=0 NormalZ=1 AngleXU=0 Radius=1
    g5: Circle CenterX=-8.2 CenterY=-26.5 CenterZ=0 NormalX=0 NormalY=0 NormalZ=1 AngleXU=0 Radius=1
    g6: BSplineCurve PolesCount=3 KnotsCount=2 Degree=2 IsPeriodic=0
    g7: GeomPoint X=-4.2 Y=-13.4877 Z=0
    g8: GeomPoint X=-8.2 Y=-26.5 Z=0
    g9: LineSegment StartX=-14 StartY=-26.5 StartZ=0 EndX=-8.2 EndY=-26.5 EndZ=0
    g10: LineSegment StartX=-10.15 StartY=-12 StartZ=0 EndX=-10.15 EndY=-14 EndZ=0
    g11: LineSegment StartX=-12.8401 StartY=-16 StartZ=0 EndX=-10.1571 EndY=-16 EndZ=0
    g12: LineSegment StartX=-10.15 StartY=-14 StartZ=0 EndX=-8.70761 EndY=-14 EndZ=0
    g13: LineSegment StartX=-12.8401 StartY=-16 StartZ=0 EndX=-12.8401 EndY=-17.6958 EndZ=0
    g14: LineSegment StartX=-10.15 StartY=-12 StartZ=0 EndX=-7.79258 EndY=-12 EndZ=0
    g15: Circle CenterX=-6.2215 CenterY=-2 CenterZ=0 NormalX=0 NormalY=0 NormalZ=1 AngleXU=0 Radius=1
    g16: Circle CenterX=-6.22762 CenterY=-2.58724 CenterZ=0 NormalX=0 NormalY=0 NormalZ=1 AngleXU=0 Radius=1
    g17: Circle CenterX=-6.32538 CenterY=-4 CenterZ=0 NormalX=0 NormalY=0 NormalZ=1 AngleXU=0 Radius=1
    g18: BSplineCurve PolesCount=3 KnotsCount=2 Degree=2 IsPeriodic=0
    g19: GeomPoint X=-6.2215 Y=-2 Z=0
    g20: GeomPoint X=-6.32538 Y=-4 Z=0
    g21: Circle CenterX=-6.48644 CenterY=-5.99526 CenterZ=0 NormalX=0 NormalY=0 NormalZ=1 AngleXU=0 Radius=1
    g22: Circle CenterX=-6.58486 CenterY=-6.99526 CenterZ=0 NormalX=0 NormalY=0 NormalZ=1 AngleXU=0 Radius=1
    g23: Circle CenterX=-6.77343 CenterY=-8 CenterZ=0 NormalX=0 NormalY=0 NormalZ=1 AngleXU=0 Radius=1
    g24: BSplineCurve PolesCount=3 KnotsCount=2 Degree=2 IsPeriodic=0
    g25: GeomPoint X=-6.48644 Y=-5.99526 Z=0
    g26: GeomPoint X=-6.77343 Y=-8 Z=0
    g27: Circle CenterX=-7.19003 CenterY=-10 CenterZ=0 NormalX=0 NormalY=0 NormalZ=1 AngleXU=0 Radius=1
    g28: Circle CenterX=-7.44407 CenterY=-11.0915 CenterZ=0 NormalX=0 NormalY=0 NormalZ=1 AngleXU=0 Radius=1
    g29: Circle CenterX=-7.79258 CenterY=-12 CenterZ=0 NormalX=0 NormalY=0 NormalZ=1 AngleXU=0 Radius=1
    g30: BSplineCurve PolesCount=3 KnotsCount=2 Degree=2 IsPeriodic=0
    g31: GeomPoint X=-7.19003 Y=-10 Z=0
    g32: GeomPoint X=-7.79258 Y=-12 Z=0
    g33: Circle CenterX=-8.70761 CenterY=-14 CenterZ=0 NormalX=0 NormalY=0 NormalZ=1 AngleXU=0 Radius=1
    g34: Circle CenterX=-9.33087 CenterY=-15.1837 CenterZ=0 NormalX=0 NormalY=0 NormalZ=1 AngleXU=0 Radius=1
    g35: Circle CenterX=-10.1571 CenterY=-16 CenterZ=0 NormalX=0 NormalY=0 NormalZ=1 AngleXU=0 Radius=1
    g36: BSplineCurve PolesCount=3 KnotsCount=2 Degree=2 IsPeriodic=0
    g37: GeomPoint X=-8.70761 Y=-14 Z=0
    g38: GeomPoint X=-10.1571 Y=-16 Z=0
    g39: Circle CenterX=-12.8401 CenterY=-17.6958 CenterZ=0 NormalX=0 NormalY=0 NormalZ=1 AngleXU=0 Radius=1
    g40: Circle CenterX=-13.3521 CenterY=-17.9027 CenterZ=0 NormalX=0 NormalY=0 NormalZ=1 AngleXU=0 Radius=1
    g41: Circle CenterX=-14 CenterY=-18 CenterZ=0 NormalX=0 NormalY=0 NormalZ=1 AngleXU=0 Radius=1
    g42: BSplineCurve PolesCount=3 KnotsCount=2 Degree=2 IsPeriodic=0
    g43: GeomPoint X=-12.8401 Y=-17.6958 Z=0
    g44: GeomPoint X=-14 Y=-18 Z=0
    g45: LineSegment StartX=-6.2 StartY=0 StartZ=0 EndX=-7.2 EndY=0 EndZ=0
    g46: LineSegment StartX=-7.2 StartY=0 StartZ=0 EndX=-7.2 EndY=-2 EndZ=0
    g47: LineSegment StartX=-7.2 StartY=-2 StartZ=0 EndX=-6.2215 EndY=-2 EndZ=0
    g48: LineSegment StartX=-6.32538 StartY=-4 StartZ=0 EndX=-7.65538 EndY=-4 EndZ=0
    g49: LineSegment StartX=-7.65538 StartY=-4 StartZ=0 EndX=-7.65538 EndY=-5.99526 EndZ=0
    g50: LineSegment StartX=-7.65538 StartY=-5.99526 StartZ=0 EndX=-6.48644 EndY=-5.99526 EndZ=0
    g51: LineSegment StartX=-6.77343 StartY=-8 StartZ=0 EndX=-8.43343 EndY=-8 EndZ=0
    g52: LineSegment StartX=-8.43343 StartY=-8 StartZ=0 EndX=-8.43343 EndY=-10 EndZ=0
    g53: LineSegment StartX=-8.43343 StartY=-10 StartZ=0 EndX=-7.19003 EndY=-10 EndZ=0
  constraints (112):
    c: Horizontal(g0)
    c: Distance(g0) = 2
    c: Block(g0)
    c: Vertical(g1)
    c: Coincident(g2,g0)
    c: Vertical(g2)
    c: Block(g2)
    c: Coincident(g6,g2)
    c: Weight(g3) = 1
    c: Equal(g3,g4)
    c: Equal(g3,g5)
    c: InternalAlignment(g3,g6)
    c: InternalAlignment(g4,g6)
    c: InternalAlignment(g5,g6)
    c: InternalAlignment(g7,g6)
    c: InternalAlignment(g8,g6)
    c: Block(g6)
    c: Coincident(g9,g1)
    c: Coincident(g9,g6)
    c: Horizontal(g9)
    c: Vertical(g10)
    c: Block(g10)
    c: Horizontal(g11)
    c: Block(g11)
    c: Coincident(g12,g10)
    c: Horizontal(g12)
    c: Block(g12)
    c: Coincident(g13,g11)
    c: Vertical(g13)
    c: Block(g13)
    c: Coincident(g14,g10)
    c: Horizontal(g14)
    c: Block(g14)
    c: Block(g9)
    c: Block(g1)
    c: Weight(g15) = 1
    c: Equal(g15,g16)
    c: Equal(g15,g17)
    c: InternalAlignment(g15,g18)
    c: InternalAlignment(g16,g18)
    c: InternalAlignment(g17,g18)
    c: InternalAlignment(g19,g18)
    c: InternalAlignment(g20,g18)
    c: Weight(g21) = 1
    c: Equal(g21,g22)
    c: Equal(g21,g23)
    c: InternalAlignment(g21,g24)
    c: InternalAlignment(g22,g24)
    c: InternalAlignment(g23,g24)
    c: InternalAlignment(g25,g24)
    c: InternalAlignment(g26,g24)
    c: Weight(g27) = 1
    c: Equal(g27,g28)
    c: Equal(g27,g29)
    c: Coincident(g30,g14)
    c: InternalAlignment(g27,g30)
    c: InternalAlignment(g28,g30)
    c: InternalAlignment(g29,g30)
    c: InternalAlignment(g31,g30)
    c: InternalAlignment(g32,g30)
    c: Coincident(g36,g12)
    c: Weight(g33) = 1
    c: Equal(g33,g34)
    c: Equal(g33,g35)
    c: Coincident(g36,g11)
    c: InternalAlignment(g33,g36)
    c: InternalAlignment(g34,g36)
    c: InternalAlignment(g35,g36)
    c: InternalAlignment(g37,g36)
    c: InternalAlignment(g38,g36)
    c: Coincident(g42,g13)
    c: Weight(g39) = 1
    c: Equal(g39,g40)
    c: Equal(g39,g41)
    c: Coincident(g42,g1)
    c: InternalAlignment(g39,g42)
    c: InternalAlignment(g40,g42)
    c: InternalAlignment(g41,g42)
    c: InternalAlignment(g43,g42)
    c: InternalAlignment(g44,g42)
    c: Block(g18)
    c: Block(g24)
    c: Block(g30)
    c: Block(g36)
    c: Block(g42)
    c: Horizontal(g45)
    c: Coincident(g45,g0)
    c: Vertical(g46)
    c: Coincident(g46,g45)
    c: Coincident(g47,g46)
    c: Coincident(g47,g18)
    c: Horizontal(g47)
    c: Block(g46)
    c: Coincident(g48,g18)
    c: Horizontal(g48)
    c: Distance(g48) = 1.33
    c: Vertical(g49)
    c: Coincident(g49,g48)
    c: Coincident(g50,g49)
    c: Coincident(g50,g24)
    c: Horizontal(g50)
    c: Tangent(g50,g22)
    c: Horizontal(g51)
    c: Coincident(g51,g24)
    c: Block(g51)
    c: Vertical(g52)
    c: Block(g52)
    c: Coincident(g52,g51)
    c: Coincident(g53,g52)
    c: Coincident(g53,g30)
    c: Horizontal(g53)
    c: Distance(g1) = 8.5
FEATURE [Part::Feature] Face024
  shape: bbox 9.8 x 26.5 x 2e-07 mm, 1 faces, 0 solids (baked)
FEATURE [Part::Revolution] Revolve024
  Angle = 360
  Axis = (0,1,0)
  Base = (0,0,0)
  FaceMakerClass = Part::FaceMakerBullseye
  Placement = pos=(0,0,0) rot=(0,0,1;1.5708rad)
  Solid = false
  Source = -> Face024
  Symmetric = false
FEATURE [Part::Feature] Face025
  shape: bbox 9.8 x 26.5 x 2e-07 mm, 1 faces, 0 solids (baked)
FEATURE [Part::Revolution] Revolve025
  Angle = 360
  Axis = (0,1,0)
  Base = (0,0,0)
  FaceMakerClass = Part::FaceMakerBullseye
  Placement = pos=(0,0,0) rot=(0,0,1;1.5708rad)
  Solid = false
  Source = -> Face025
  Symmetric = false
FEATURE [Part::MultiFuse] Fusion033
  Placement = pos=(-18,19,36) rot=(0,0,1;0rad)
  Shapes = -> [Revolve025,Revolve024]
FEATURE [Part::Cylinder] Cylinder014
  Angle = 360
  AttacherType = Attacher::AttachEngine3D
  Height = 20
  Placement = pos=(0,0,36.15) rot=(0,0,1;0rad)
  Radius = 14.3
FEATURE [Part::Cylinder] Cylinder015
  Angle = 360
  AttacherType = Attacher::AttachEngine3D
  Height = 10
  Placement = pos=(0,0,36.15) rot=(0,0,1;0rad)
  Radius = 4
FEATURE [Part::MultiFuse] Fusion034  label="removeToCreteHoleForPlugHousing004"
  Placement = pos=(-42,19,36) rot=(0,1,0;1.5708rad)
  Shapes = -> [Cylinder014,Cylinder015]
FEATURE [Part::Cut] Cut008  label="top004"
  Base = -> Cut004
  Placement = pos=(-1,0,0) rot=(0,0,1;0rad)
  Tool = -> Fusion034
FEATURE [Part::Box] Box005  label="Cube005"
  AttacherType = Attacher::AttachEngine3D
  Height = 28
  Length = 3
  Placement = pos=(110.7,19,22) rot=(0,0,1;0rad)
  Width = 15.7
FEATURE [Part::Cylinder] Cylinder016
  Angle = 360
  AttacherType = Attacher::AttachEngine3D
  Height = 10
  Placement = pos=(0,0,36.15) rot=(0,0,1;0rad)
  Radius = 4
FEATURE [Part::Cylinder] Cylinder017
  Angle = 360
  AttacherType = Attacher::AttachEngine3D
  Height = 20
  Placement = pos=(0,0,36.15) rot=(0,0,1;0rad)
  Radius = 10.3
FEATURE [Part::MultiFuse] Fusion035  label="removeToCreteHoleForPlugHousing005"
  Placement = pos=(70,19,36) rot=(0,1,0;1.5708rad)
  Shapes = -> [Cylinder017,Cylinder016]
FEATURE [Part::Cut] Cut009  label="plugHousingTab001"
  Base = -> Box005
  Placement = pos=(-107.4,-14,0) rot=(0,0,1;0rad)
  Tool = -> Fusion035
FEATURE [Part::Box] Box006  label="Cube006"
  AttacherType = Attacher::AttachEngine3D
  Height = 28
  Length = 3
  Placement = pos=(110.7,19,22) rot=(0,0,1;0rad)
  Width = 15.7
FEATURE [Part::Cylinder] Cylinder018
  Angle = 360
  AttacherType = Attacher::AttachEngine3D
  Height = 10
  Placement = pos=(0,0,36.15) rot=(0,0,1;0rad)
  Radius = 4
FEATURE [Part::Cylinder] Cylinder019
  Angle = 360
  AttacherType = Attacher::AttachEngine3D
  Height = 20
  Placement = pos=(0,0,36.15) rot=(0,0,1;0rad)
  Radius = 10.3
FEATURE [Part::MultiFuse] Fusion036  label="removeToCreteHoleForPlugHousing006"
  Placement = pos=(70,19,36) rot=(0,1,0;1.5708rad)
  Shapes = -> [Cylinder019,Cylinder018]
FEATURE [Part::Cut] Cut010  label="plugHousingTab002"
  Base = -> Box006
  Placement = pos=(-107.4,-14,0) rot=(0,0,1;0rad)
  Tool = -> Fusion036
FEATURE [Part::MultiFuse] Fusion037
  Placement = pos=(9.6,23,0) rot=(0,0,1;3.14159rad)
  Shapes = -> [Cut009,Cut010]
FEATURE [Part::Box] Box  label="Cube"
  AttacherType = Attacher::AttachEngine3D
  Height = 10
  Length = 3
  Placement = pos=(3.3,4,12) rot=(0,0,1;0rad)
  Width = 10
FEATURE [Part::Fillet] Fillet004
  Base = -> Fusion028
  Edges = 1 edges r=2: [Edge25]
FEATURE [Part::Fillet] Fillet005  label="plugHousing046"
  Base = -> Fillet004
  Edges = 1 edges r=2: [Edge8]
FEATURE [Part::Fillet] Fillet006
  Base = -> Box
  Edges = 1 edges r=2: [Edge11]
FEATURE [Part::Box] Box007  label="Cube007"
  AttacherType = Attacher::AttachEngine3D
  Height = 10
  Length = 3
  Placement = pos=(3.3,4,50) rot=(0,0,1;0rad)
  Width = 10
FEATURE [Part::Fillet] Fillet007
  Base = -> Box007
  Edges = 1 edges r=2: [Edge12]
FEATURE [Part::Box] Box008  label="Cube008"
  AttacherType = Attacher::AttachEngine3D
  Height = 28
  Length = 4
  Placement = pos=(5,0,22) rot=(0,0,1;0rad)
  Width = 10
FEATURE [Part::Fillet] Fillet008
  Base = -> Box008
  Edges = 1 edges r=1: [Edge7]
FEATURE [Part::Fillet] Fillet009
  Base = -> Fillet008
  Edges = 1 edges r=2: [Edge5]
FEATURE [Part::Fillet] Fillet010
  Base = -> Fillet009
  Edges = 1 edges r=2: [Edge2]
FEATURE [Sketcher::SketchObject] Sketch009  label="topSketch003"
  FullyConstrained = true
  sketch-geometry (4):
    g0: LineSegment StartX=16.8446 StartY=31.512 StartZ=0 EndX=16.3251 EndY=34.4666 EndZ=0
    g1: ArcOfCircle CenterX=19 CenterY=19.2524 CenterZ=0 NormalX=0 NormalY=0 NormalZ=1 AngleXU=0 Radius=15.4476 StartAngle=1.74483 EndAngle=2.72717
    g2: ArcOfCircle CenterX=19 CenterY=19.2524 CenterZ=0 NormalX=0 NormalY=0 NormalZ=1 AngleXU=0 Radius=12.4476 StartAngle=1.74483 EndAngle=2.73189
    g3: LineSegment StartX=4.86004 StartY=25.4725 StartZ=0 EndX=7.58253 EndY=24.2107 EndZ=0
  constraints (7):
    c: Block(g0)
    c: Coincident(g1,g0)
    c: Coincident(g2,g0)
    c: Coincident(g3,g1)
    c: Coincident(g3,g2)
    c: Block(g1)
    c: Block(g2)
FEATURE [Part::Extrusion] Extrude008
  Base = -> Sketch009
  Dir = (0,0,1)
  DirMode = 2
  FaceMakerClass = Part::FaceMakerBullseye
  LengthFwd = 10
  LengthRev = 0
  Placement = pos=(0,0,31) rot=(0,0,1;0rad)
  Solid = true
  Symmetric = false
FEATURE [Part::Cylinder] Cylinder020
  Angle = 360
  AttacherType = Attacher::AttachEngine3D
  Height = 20
  Placement = pos=(0,0,36.15) rot=(0,0,1;0rad)
  Radius = 8.2
FEATURE [Part::Cylinder] Cylinder021
  Angle = 360
  AttacherType = Attacher::AttachEngine3D
  Height = 10
  Placement = pos=(0,0,36.15) rot=(0,0,1;0rad)
  Radius = 4
FEATURE [Part::MultiFuse] Fusion038  label="removeToCreteHoleForPlugHousing007"
  Placement = pos=(-42,19,36) rot=(0,1,0;1.5708rad)
  Shapes = -> [Cylinder020,Cylinder021]
FEATURE [Part::Cut] Cut011
  Base = -> Extrude008
  Tool = -> Fusion038
FEATURE [Part::Fillet] Fillet011
  Base = -> Cut011
  Edges = 1 edges r=2: [Edge1]
FEATURE [Part::Fillet] Fillet012
  Base = -> Fillet011
  Edges = 1 edges r=2.5: [Edge1]
FEATURE [Part::Fillet] Fillet013
  Base = -> Fillet012
  Edges = 1 edges r=2.5: [Edge2]
FEATURE [Part::Box] Box010  label="Cube010"
  AttacherType = Attacher::AttachEngine3D
  Height = 16
  Length = 8
  Placement = pos=(12.7,31.52,28) rot=(0,0,1;0rad)
  Width = 4
FEATURE [Sketcher::SketchObject] Sketch010  label="topSketch004"
  FullyConstrained = true
  sketch-geometry (4):
    g0: LineSegment StartX=16.8446 StartY=31.512 StartZ=0 EndX=16.3251 EndY=34.4666 EndZ=0
    g1: ArcOfCircle CenterX=19 CenterY=19.2524 CenterZ=0 NormalX=0 NormalY=0 NormalZ=1 AngleXU=0 Radius=15.4476 StartAngle=1.74483 EndAngle=2.72717
    g2: ArcOfCircle CenterX=19 CenterY=19.2524 CenterZ=0 NormalX=0 NormalY=0 NormalZ=1 AngleXU=0 Radius=12.4476 StartAngle=1.74483 EndAngle=2.73189
    g3: LineSegment StartX=4.86004 StartY=25.4725 StartZ=0 EndX=7.58253 EndY=24.2107 EndZ=0
  constraints (7):
    c: Block(g0)
    c: Coincident(g1,g0)
    c: Coincident(g2,g0)
    c: Coincident(g3,g1)
    c: Coincident(g3,g2)
    c: Block(g1)
    c: Block(g2)
FEATURE [Part::Cylinder] Cylinder022
  Angle = 360
  AttacherType = Attacher::AttachEngine3D
  Height = 10
  Placement = pos=(0,0,36.15) rot=(0,0,1;0rad)
  Radius = 4
FEATURE [Sketcher::SketchObject] Sketch011  label="topSketch005"
  FullyConstrained = true
  sketch-geometry (4):
    g0: LineSegment StartX=16.8446 StartY=31.512 StartZ=0 EndX=16.3251 EndY=34.4666 EndZ=0
    g1: ArcOfCircle CenterX=19 CenterY=19.2524 CenterZ=0 NormalX=0 NormalY=0 NormalZ=1 AngleXU=0 Radius=15.4476 StartAngle=1.74483 EndAngle=2.72717
    g2: ArcOfCircle CenterX=19 CenterY=19.2524 CenterZ=0 NormalX=0 NormalY=0 NormalZ=1 AngleXU=0 Radius=12.4476 StartAngle=1.74483 EndAngle=2.73189
    g3: LineSegment StartX=4.86004 StartY=25.4725 StartZ=0 EndX=7.58253 EndY=24.2107 EndZ=0
  constraints (7):
    c: Block(g0)
    c: Coincident(g1,g0)
    c: Coincident(g2,g0)
    c: Coincident(g3,g1)
    c: Coincident(g3,g2)
    c: Block(g1)
    c: Block(g2)
FEATURE [Part::Extrusion] Extrude010
  Base = -> Sketch011
  Dir = (0,0,1)
  DirMode = 2
  FaceMakerClass = Part::FaceMakerBullseye
  LengthFwd = 10.6
  LengthRev = 0
  Placement = pos=(0,0,31) rot=(0,0,1;0rad)
  Solid = true
  Symmetric = false
FEATURE [Part::Cylinder] Cylinder023
  Angle = 360
  AttacherType = Attacher::AttachEngine3D
  Height = 20
  Placement = pos=(0,0,36.15) rot=(0,0,1;0rad)
  Radius = 8.2
FEATURE [Part::MultiFuse] Fusion039  label="removeToCreteHoleForPlugHousing008"
  Placement = pos=(-42,19,36) rot=(0,1,0;1.5708rad)
  Shapes = -> [Cylinder023,Cylinder022]
FEATURE [Part::Cut] Cut012
  Base = -> Extrude010
  Placement = pos=(0,0,-0.3) rot=(0,0,1;0rad)
  Tool = -> Fusion039
FEATURE [Part::Cut] Cut013
  Base = -> Box010
  Tool = -> Cut012
FEATURE [Part::Fillet] Fillet014
  Base = -> Cut013
  Edges = 1 edges r=0.7: [Edge13]
FEATURE [Part::Fillet] Fillet015
  Base = -> Fillet014
  Edges = 1 edges r=0.7: [Edge13]
FEATURE [Part::Fillet] Fillet016
  Base = -> Fillet015
  Edges = 1 edges r=0.7: [Edge16]
FEATURE [Part::Fillet] Fillet017
  Base = -> Fillet016
  Edges = 1 edges r=0.7: [Edge11]
FEATURE [Part::Fillet] Fillet018
  Base = -> Fillet017
  Edges = 1 edges r=0.7: [Edge10]
FEATURE [Part::Fillet] Fillet019
  Base = -> Fillet018
  Edges = 1 edges r=1.2: [Edge5]
FEATURE [Part::Fillet] Fillet020
  Base = -> Fillet019
  Edges = 1 edges r=1.2: [Edge12]
FEATURE [Part::Fillet] Fillet021
  Base = -> Fillet020
  Edges = 1 edges r=2: [Edge1]
  Placement = pos=(0.3,0,0) rot=(0,0,1;0rad)
FEATURE [Part::MultiFuse] Fusion040  label="top005"
  Shapes = -> [Cut008,Fillet021]
FEATURE [Part::MultiFuse] Fusion041  label="wireHolder"
  Shapes = -> [Fusion033,Fillet013]
FEATURE [Part::MultiFuse] Fusion042
  Shapes = -> [Fillet007,Fusion041]
FEATURE [Part::MultiFuse] Fusion043  label="wireHolder001"
  Shapes = -> [Fusion042,Fillet010]
FEATURE [Part::MultiFuse] Fusion044  label="wireHolder002"
  Shapes = -> [Fillet006,Fusion037,Fusion043]
FEATURE [Part::Feature] Face026
  shape: bbox 11 x 6 x 2e-07 mm, 1 faces, 0 solids (baked)
FEATURE [Part::Revolution] Revolve026
  Angle = 360
  Axis = (0,1,0)
  Base = (0,0,0)
  FaceMakerClass = Part::FaceMakerBullseye
  Placement = pos=(30.3,-1,19.7) rot=(0,0,1;0rad)
  Solid = false
  Source = -> Face026
  Symmetric = false
FEATURE [Sketcher::SketchObject] Sketch013  label="topSketch006"
  FullyConstrained = true
  sketch-geometry (13):
    g0: LineSegment StartX=117 StartY=19 StartZ=0 EndX=117 EndY=38 EndZ=0
    g1: ArcOfCircle CenterX=98 CenterY=19 CenterZ=0 NormalX=0 NormalY=0 NormalZ=1 AngleXU=0 Radius=19 StartAngle=5.7297 EndAngle=6.28319
    g2: LineSegment StartX=0 StartY=3 StartZ=0 EndX=0 EndY=19 EndZ=0
    g3: LineSegment StartX=19 StartY=38 StartZ=0 EndX=117 EndY=38 EndZ=0
    g4: ArcOfCircle CenterX=19 CenterY=19 CenterZ=0 NormalX=0 NormalY=0 NormalZ=1 AngleXU=0 Radius=19 StartAngle=1.5708 EndAngle=3.14159
    g5: ArcOfCircle CenterX=19 CenterY=19 CenterZ=0 NormalX=0 NormalY=0 NormalZ=1 AngleXU=0 Radius=16 StartAngle=1.5708 EndAngle=3.14159
    g6: ArcOfCircle CenterX=98 CenterY=19 CenterZ=0 NormalX=0 NormalY=0 NormalZ=1 AngleXU=0 Radius=16 StartAngle=5.60905 EndAngle=6.28319
    g7: LineSegment StartX=114 StartY=19 StartZ=0 EndX=114 EndY=35 EndZ=0
    g8: LineSegment StartX=110.5 StartY=9.01251 StartZ=0 EndX=114.163 EndY=9.01251 EndZ=0
    g9: LineSegment StartX=114 StartY=35 StartZ=0 EndX=19 EndY=35 EndZ=0
    g10: LineSegment StartX=0 StartY=3 StartZ=0 EndX=0 EndY=0 EndZ=0
    g11: LineSegment StartX=3 StartY=0 StartZ=0 EndX=0 EndY=0 EndZ=0
    g12: LineSegment StartX=3 StartY=19 StartZ=0 EndX=3 EndY=0 EndZ=0
  constraints (33):
    c: Vertical(g0)
    c: Distance(g0) = 19
    c: Block(g0)
    c: Coincident(g1,g0)
    c: Block(g1)
    c: Vertical(g2)
    c: Block(g2)
    c: Coincident(g3,g0)
    c: Horizontal(g3)
    c: Distance(g3) = 98
    c: Coincident(g4,g3)
    c: Coincident(g4,g2)
    c: Block(g4)
    c: Coincident(g5,g4)
    c: Coincident(g6,g1)
    c: Block(g6)
    c: Block(g5)
    c: Coincident(g7,g6)
    c: Vertical(g7)
    c: Coincident(g8,g6)
    c: Coincident(g8,g1)
    c: Coincident(g9,g7)
    c: Coincident(g9,g5)
    c: Horizontal(g9)
    c: Tangent(g9,g5)
    c: Coincident(g10,g2)
    c: Distance(g10) = 3
    c: Vertical(g10)
    c: Coincident(g11,g10)
    c: Horizontal(g11)
    c: Coincident(g12,g5)
    c: Coincident(g12,g11)
    c: Vertical(g12)
FEATURE [Part::Extrusion] Extrude011  label="top006"
  Base = -> Sketch013
  Dir = (0,0,1)
  DirMode = 2
  FaceMakerClass = Part::FaceMakerBullseye
  LengthFwd = 72
  LengthRev = 0
  Solid = true
  Symmetric = false
FEATURE [Sketcher::SketchObject] Sketch014
  FullyConstrained = true
  MapMode = 3
  Placement = pos=(0,0,0) rot=(1,0,0;1.5708rad)
  Support = -> [Extrude011]
  sketch-geometry (8):
    g0: Circle CenterX=80.351 CenterY=-67.6202 CenterZ=0 NormalX=0 NormalY=0 NormalZ=1 AngleXU=0 Radius=2
    g1: Circle CenterX=80.351 CenterY=-67.6202 CenterZ=0 NormalX=0 NormalY=0 NormalZ=1 AngleXU=0 Radius=3
    g2: Circle CenterX=80.351 CenterY=-4.92017 CenterZ=0 NormalX=0 NormalY=0 NormalZ=1 AngleXU=0 Radius=2
    g3: Circle CenterX=80.351 CenterY=-4.92017 CenterZ=0 NormalX=0 NormalY=0 NormalZ=1 AngleXU=0 Radius=3
    g4: Circle CenterX=23.851 CenterY=-4.92017 CenterZ=0 NormalX=0 NormalY=0 NormalZ=1 AngleXU=0 Radius=2
    g5: Circle CenterX=23.851 CenterY=-4.92017 CenterZ=0 NormalX=0 NormalY=0 NormalZ=1 AngleXU=0 Radius=3
    g6: Circle CenterX=23.851 CenterY=-67.6202 CenterZ=0 NormalX=0 NormalY=0 NormalZ=1 AngleXU=0 Radius=2
    g7: Circle CenterX=23.851 CenterY=-67.6202 CenterZ=0 NormalX=0 NormalY=0 NormalZ=1 AngleXU=0 Radius=3
  constraints (8):
    c: Block(g3)
    c: Block(g2)
    c: Block(g1)
    c: Block(g0)
    c: Block(g6)
    c: Block(g7)
    c: Block(g4)
    c: Block(g5)
FEATURE [Part::Feature] Face027
  shape: bbox 11 x 6 x 2e-07 mm, 1 faces, 0 solids (baked)
FEATURE [Part::Revolution] Revolve027
  Angle = 360
  Axis = (0,1,0)
  Base = (0,0,0)
  FaceMakerClass = Part::FaceMakerBullseye
  Placement = pos=(30.3,-1,51.7) rot=(0,0,1;0rad)
  Solid = false
  Source = -> Face027
  Symmetric = false
FEATURE [Part::Feature] Face028
  shape: bbox 11 x 6 x 2e-07 mm, 1 faces, 0 solids (baked)
FEATURE [Part::Revolution] Revolve028
  Angle = 360
  Axis = (0,1,0)
  Base = (0,0,0)
  FaceMakerClass = Part::FaceMakerBullseye
  Placement = pos=(62.3,-1,19.7) rot=(0,0,1;0rad)
  Solid = false
  Source = -> Face028
  Symmetric = false
FEATURE [Part::Feature] Face029
  shape: bbox 11 x 6 x 2e-07 mm, 1 faces, 0 solids (baked)
FEATURE [Part::Revolution] Revolve029
  Angle = 360
  Axis = (0,1,0)
  Base = (0,0,0)
  FaceMakerClass = Part::FaceMakerBullseye
  Placement = pos=(62.3,-1,51.7) rot=(0,0,1;0rad)
  Solid = false
  Source = -> Face029
  Symmetric = false
FEATURE [Part::Feature] Wire
  shape: bbox 11 x 5.2 x 2e-07 mm, 0 faces, 0 solids (baked)
FEATURE [Part::Revolution] Revolve030
  Angle = 360
  Axis = (0,1,0)
  Base = (0,0,0)
  FaceMakerClass = Part::FaceMakerBullseye
  Placement = pos=(30.3,38,19.7) rot=(0,0,1;0rad)
  Solid = true
  Source = -> Wire
  Symmetric = false
FEATURE [Part::Feature] Wire001
  shape: bbox 11 x 5.2 x 2e-07 mm, 0 faces, 0 solids (baked)
FEATURE [Part::Revolution] Revolve031
  Angle = 360
  Axis = (0,1,0)
  Base = (0,0,0)
  FaceMakerClass = Part::FaceMakerBullseye
  Placement = pos=(30.3,38,51.7) rot=(0,0,1;0rad)
  Solid = true
  Source = -> Wire001
  Symmetric = false
FEATURE [Part::Feature] Wire002
  shape: bbox 11 x 5.2 x 2e-07 mm, 0 faces, 0 solids (baked)
FEATURE [Part::Revolution] Revolve032
  Angle = 360
  Axis = (0,1,0)
  Base = (0,0,0)
  FaceMakerClass = Part::FaceMakerBullseye
  Placement = pos=(62.3,38,51.7) rot=(0,0,1;0rad)
  Solid = true
  Source = -> Wire002
  Symmetric = false
FEATURE [Part::Feature] Wire003
  shape: bbox 11 x 5.2 x 2e-07 mm, 0 faces, 0 solids (baked)
FEATURE [Part::Revolution] Revolve033
  Angle = 360
  Axis = (0,1,0)
  Base = (0,0,0)
  FaceMakerClass = Part::FaceMakerBullseye
  Placement = pos=(62.3,38,19.7) rot=(0,0,1;0rad)
  Solid = true
  Source = -> Wire003
  Symmetric = false
FEATURE [Part::MultiFuse] Fusion045  label="altRandScrewHousing"
  Shapes = -> [Revolve029,Revolve027,Revolve028,Revolve026]
FEATURE [Part::MultiFuse] Fusion046  label="fanScrewHousing"
  Shapes = -> [Revolve033,Revolve032,Revolve031,Revolve030]
FEATURE [Sketcher::SketchObject] Sketch015
  FullyConstrained = true
  sketch-geometry (17):
    g0: Circle CenterX=-3.5 CenterY=23.5 CenterZ=0 NormalX=0 NormalY=0 NormalZ=1 AngleXU=0 Radius=1
    g1: Circle CenterX=-1 CenterY=15.25 CenterZ=0 NormalX=0 NormalY=0 NormalZ=1 AngleXU=0 Radius=1
    g2: Circle CenterX=-3.5 CenterY=7 CenterZ=0 NormalX=0 NormalY=0 NormalZ=1 AngleXU=0 Radius=1
    g3: BSplineCurve PolesCount=3 KnotsCount=2 Degree=2 IsPeriodic=0
    g4: GeomPoint X=-3.5 Y=23.5 Z=0
    g5: GeomPoint X=-3.5 Y=7 Z=0
    g6: Circle CenterX=-4.8 CenterY=30.5 CenterZ=0 NormalX=0 NormalY=0 NormalZ=1 AngleXU=0 Radius=1
    g7: Circle CenterX=-3.5 CenterY=30.5 CenterZ=0 NormalX=0 NormalY=0 NormalZ=1 AngleXU=0 Radius=1
    g8: Circle CenterX=-3.5 CenterY=29.2 CenterZ=0 NormalX=0 NormalY=0 NormalZ=1 AngleXU=0 Radius=1
    g9: BSplineCurve PolesCount=3 KnotsCount=2 Degree=2 IsPeriodic=0
    g10: GeomPoint X=-4.8 Y=30.5 Z=0
    g11: GeomPoint X=-3.5 Y=29.2 Z=0
    g12: LineSegment StartX=-3.5 StartY=29.2 StartZ=0 EndX=-3.5 EndY=23.5 EndZ=0
    g13: LineSegment StartX=-4.8 StartY=30.5 StartZ=0 EndX=0 EndY=30.5 EndZ=0
    g14: LineSegment StartX=-3.5 StartY=0.3 StartZ=0 EndX=0 EndY=0.3 EndZ=0
    g15: LineSegment StartX=-3.5 StartY=0.3 StartZ=0 EndX=-3.5 EndY=7 EndZ=0
    g16: LineSegment StartX=0 StartY=0.3 StartZ=0 EndX=0 EndY=30.5 EndZ=0
  constraints (33):
    c: Weight(g0) = 1
    c: Equal(g0,g1)
    c: Equal(g0,g2)
    c: InternalAlignment(g0,g3)
    c: InternalAlignment(g1,g3)
    c: InternalAlignment(g2,g3)
    c: InternalAlignment(g4,g3)
    c: InternalAlignment(g5,g3)
    c: Block(g3)
    c: Weight(g6) = 1
    c: Equal(g6,g7)
    c: Equal(g6,g8)
    c: InternalAlignment(g6,g9)
    c: InternalAlignment(g7,g9)
    c: InternalAlignment(g8,g9)
    c: InternalAlignment(g10,g9)
    c: InternalAlignment(g11,g9)
    c: Block(g9)
    c: Coincident(g12,g9)
    c: Coincident(g12,g3)
    c: Vertical(g12)
    c: Coincident(g13,g9)
    c: Horizontal(g13)
    c: Distance(g13) = 4.8
    c: Horizontal(g14)
    c: Block(g14)
    c: Coincident(g15,g14)
    c: Coincident(g15,g3)
    c: Vertical(g15)
    c: Coincident(g16,g14)
    c: Coincident(g16,g13)
    c: Vertical(g16)
    c: Tangent(g16,g1)
FEATURE [Sketcher::SketchObject] Sketch016
  FullyConstrained = true
  sketch-geometry (16):
    g0: Circle CenterX=-3.5 CenterY=23.5 CenterZ=0 NormalX=0 NormalY=0 NormalZ=1 AngleXU=0 Radius=1
    g1: Circle CenterX=-1 CenterY=15.25 CenterZ=0 NormalX=0 NormalY=0 NormalZ=1 AngleXU=0 Radius=1
    g2: Circle CenterX=-3.5 CenterY=7 CenterZ=0 NormalX=0 NormalY=0 NormalZ=1 AngleXU=0 Radius=1
    g3: BSplineCurve PolesCount=3 KnotsCount=2 Degree=2 IsPeriodic=0
    g4: GeomPoint X=-3.5 Y=23.5 Z=0
    g5: GeomPoint X=-3.5 Y=7 Z=0
    g6: LineSegment StartX=-3.5 StartY=28.2 StartZ=0 EndX=-3.5 EndY=23.5 EndZ=0
    g7: LineSegment StartX=0 StartY=29.5 StartZ=0 EndX=0 EndY=30 EndZ=0
    g8: LineSegment StartX=-3.5 StartY=28.2 StartZ=0 EndX=-3.5 EndY=30 EndZ=0
    g9: LineSegment StartX=0 StartY=30 StartZ=0 EndX=0 EndY=30.5 EndZ=0
    g10: LineSegment StartX=0 StartY=30.5 StartZ=0 EndX=-3.5 EndY=30.5 EndZ=0
    g11: LineSegment StartX=-3.5 StartY=30.5 StartZ=0 EndX=-3.5 EndY=30 EndZ=0
    g12: LineSegment StartX=0 StartY=29.5 StartZ=0 EndX=0 EndY=5 EndZ=0
    g13: LineSegment StartX=-3.5 StartY=0.3 StartZ=0 EndX=-3.5 EndY=7 EndZ=0
    g14: LineSegment StartX=-3.5 StartY=0.3 StartZ=0 EndX=0 EndY=0.3 EndZ=0
    g15: LineSegment StartX=0 StartY=5 StartZ=0 EndX=0 EndY=0.3 EndZ=0
  constraints (39):
    c: Weight(g0) = 1
    c: Equal(g0,g1)
    c: Equal(g0,g2)
    c: InternalAlignment(g0,g3)
    c: InternalAlignment(g1,g3)
    c: InternalAlignment(g2,g3)
    c: InternalAlignment(g4,g3)
    c: InternalAlignment(g5,g3)
    c: Block(g3)
    c: Coincident(g6,g3)
    c: Vertical(g6)
    c: Vertical(g7)
    c: Distance(g7) = 0.5
    c: Coincident(g8,g6)
    c: Vertical(g8)
    c: Block(g6)
    c: Block(g7)
    c: Vertical(g9)
    c: Equal(g7,g9) = 0.5
    c: Block(g9)
    c: Coincident(g9,g7)
    c: Horizontal(g10)
    c: Coincident(g10,g9)
    c: Coincident(g11,g10)
    c: Coincident(g11,g8)
    c: Vertical(g11)
    c: Block(g11)
    c: Coincident(g12,g7)
    c: Vertical(g12)
    c: Coincident(g13,g3)
    c: Vertical(g13)
    c: Distance(g13) = 6.7
    c: Coincident(g14,g13)
    c: Horizontal(g14)
    c: Block(g14)
    c: Coincident(g15,g12)
    c: Coincident(g15,g14)
    c: Vertical(g15)
    c: Block(g15)
FEATURE [Sketcher::SketchObject] Sketch017
  FullyConstrained = true
  sketch-geometry (11):
    g0: LineSegment StartX=-3.5 StartY=1e-16 StartZ=0 EndX=-1.6 EndY=1e-16 EndZ=0
    g1: LineSegment StartX=-1.6 StartY=1e-16 StartZ=0 EndX=-1.6 EndY=1.5 EndZ=0
    g2: LineSegment StartX=-3.5 StartY=1.5 StartZ=0 EndX=-1.6 EndY=1.5 EndZ=0
    g3: LineSegment StartX=-3.5 StartY=1e-16 StartZ=0 EndX=-4.8 EndY=1e-16 EndZ=0
    g4: Circle CenterX=-3.5 CenterY=1.3 CenterZ=0 NormalX=0 NormalY=0 NormalZ=1 AngleXU=0 Radius=1
    g5: Circle CenterX=-3.5 CenterY=1e-16 CenterZ=0 NormalX=0 NormalY=0 NormalZ=1 AngleXU=0 Radius=1
    g6: Circle CenterX=-4.8 CenterY=1e-16 CenterZ=0 NormalX=0 NormalY=0 NormalZ=1 AngleXU=0 Radius=1
    g7: BSplineCurve PolesCount=3 KnotsCount=2 Degree=2 IsPeriodic=0
    g8: GeomPoint X=-3.5 Y=1.3 Z=0
    g9: GeomPoint X=-4.8 Y=1e-16 Z=0
    g10: LineSegment StartX=-3.5 StartY=1.3 StartZ=0 EndX=-3.5 EndY=1.5 EndZ=0
  constraints (24):
    c: Horizontal(g0)
    c: Distance(g0) = 1.9
    c: Block(g0)
    c: Coincident(g1,g0)
    c: Vertical(g1)
    c: Coincident(g2,g1)
    c: Horizontal(g2)
    c: Coincident(g3,g0)
    c: Horizontal(g3)
    c: Distance(g3) = 1.3
    c: Weight(g4) = 1
    c: Equal(g4,g5)
    c: Coincident(g5,g0)
    c: Equal(g4,g6)
    c: Coincident(g7,g3)
    c: InternalAlignment(g4,g7)
    c: InternalAlignment(g5,g7)
    c: InternalAlignment(g6,g7)
    c: InternalAlignment(g8,g7)
    c: InternalAlignment(g9,g7)
    c: Coincident(g10,g7)
    c: Coincident(g10,g2)
    c: Vertical(g10)
    c: Block(g10)
FEATURE [Part::Feature] Face035
  shape: bbox 3.2 x 1.5 x 2e-07 mm, 1 faces, 0 solids (baked)
FEATURE [Part::Revolution] Revolve039  label="backCaseScrewRetainer"
  Angle = 360
  Axis = (0,1,0)
  Base = (0,0,0)
  FaceMakerClass = Part::FaceMakerBullseye
  Placement = pos=(12.5,3,62) rot=(0,0,1;0rad)
  Solid = false
  Source = -> Face035
  Symmetric = false
FEATURE [Part::Feature] Face036
  shape: bbox 3.2 x 1.5 x 2e-07 mm, 1 faces, 0 solids (baked)
FEATURE [Part::Feature] Face039
  shape: bbox 4.8 x 30.2 x 2e-07 mm, 1 faces, 0 solids (baked)
FEATURE [Part::Revolution] Revolve043  label="frontCaseScrewPost002"
  Angle = 360
  Axis = (0,1,0)
  Base = (0,0,0)
  FaceMakerClass = Part::FaceMakerBullseye
  Placement = pos=(89.5,4.5,3.5) rot=(0,0,1;0rad)
  Solid = false
  Source = -> Face039
  Symmetric = false
FEATURE [Part::Feature] Face042
  shape: bbox 4.8 x 30.2 x 2e-07 mm, 1 faces, 0 solids (baked)
FEATURE [Part::Revolution] Revolve046  label="frontCaseScrewPost003"
  Angle = 360
  Axis = (0,1,0)
  Base = (0,0,0)
  FaceMakerClass = Part::FaceMakerBullseye
  Placement = pos=(89.5,4.5,68.5) rot=(0,0,1;0rad)
  Solid = false
  Source = -> Face042
  Symmetric = false
FEATURE [Part::Feature] Face043
  shape: bbox 3.2 x 1.5 x 2e-07 mm, 1 faces, 0 solids (baked)
FEATURE [Part::Revolution] Revolve047  label="frontCaseScrewRetainer002"
  Angle = 360
  Axis = (0,1,0)
  Base = (0,0,0)
  FaceMakerClass = Part::FaceMakerBullseye
  Placement = pos=(89.5,3,68.5) rot=(0,0,1;0rad)
  Solid = false
  Source = -> Face043
  Symmetric = false
FEATURE [Part::Feature] Face044
  shape: bbox 3.2 x 1.5 x 2e-07 mm, 1 faces, 0 solids (baked)
FEATURE [Part::Revolution] Revolve048  label="frontCaseScrewRetainer003"
  Angle = 360
  Axis = (0,1,0)
  Base = (0,0,0)
  FaceMakerClass = Part::FaceMakerBullseye
  Placement = pos=(89.5,3,3.5) rot=(0,0,1;0rad)
  Solid = false
  Source = -> Face044
  Symmetric = false
FEATURE [App::MeasureDistance] Distance002  label="Distance: 1.67 mm"
  Distance = 1.66921
  P1 = (99.2361,4.7524,71.7)
  P2 = (99.2347,6.42161,71.7)
FEATURE [Sketcher::SketchObject] Sketch018
  FullyConstrained = true
  sketch-geometry (7):
    g0: LineSegment StartX=0 StartY=0 StartZ=0 EndX=0 EndY=6 EndZ=0
    g1: Circle CenterX=0 CenterY=0 CenterZ=0 NormalX=0 NormalY=0 NormalZ=1 AngleXU=0 Radius=1
    g2: Circle CenterX=8 CenterY=6 CenterZ=0 NormalX=0 NormalY=0 NormalZ=1 AngleXU=0 Radius=1
    g3: BSplineCurve PolesCount=3 KnotsCount=2 Degree=2 IsPeriodic=0
    g4: GeomPoint X=0 Y=0 Z=0
    g5: GeomPoint X=8 Y=6 Z=0
    g6: LineSegment StartX=0 StartY=6 StartZ=0 EndX=8 EndY=6 EndZ=0
  constraints (14):
    c: Coincident(g0,g-1)
    c: Distance(g0) = 6
    c: Vertical(g0)
    c: Coincident(g3,g0)
    c: Weight(g1) = 1
    c: Equal(g1,g2)
    c: InternalAlignment(g1,g3)
    c: InternalAlignment(g2,g3)
    c: InternalAlignment(g4,g3)
    c: InternalAlignment(g5,g3)
    c: Block(g3)
    c: Coincident(g6,g0)
    c: Coincident(g6,g3)
    c: Horizontal(g6)
FEATURE [Part::Extrusion] Extrude012  label="caseScrewPillarBracket"
  Base = -> Sketch018
  Dir = (0,0,1)
  DirMode = 2
  FaceMakerClass = Part::FaceMakerBullseye
  LengthFwd = 2.4
  LengthRev = 0
  Placement = pos=(15.76,29,8.8) rot=(0,1,0;0rad)
  Solid = true
  Symmetric = false
FEATURE [Sketcher::SketchObject] Sketch019
  FullyConstrained = true
  sketch-geometry (7):
    g0: LineSegment StartX=0 StartY=0 StartZ=0 EndX=0 EndY=6 EndZ=0
    g1: Circle CenterX=0 CenterY=0 CenterZ=0 NormalX=0 NormalY=0 NormalZ=1 AngleXU=0 Radius=1
    g2: Circle CenterX=8 CenterY=6 CenterZ=0 NormalX=0 NormalY=0 NormalZ=1 AngleXU=0 Radius=1
    g3: BSplineCurve PolesCount=3 KnotsCount=2 Degree=2 IsPeriodic=0
    g4: GeomPoint X=0 Y=0 Z=0
    g5: GeomPoint X=8 Y=6 Z=0
    g6: LineSegment StartX=0 StartY=6 StartZ=0 EndX=8 EndY=6 EndZ=0
  constraints (14):
    c: Coincident(g0,g-1)
    c: Distance(g0) = 6
    c: Vertical(g0)
    c: Coincident(g3,g0)
    c: Weight(g1) = 1
    c: Equal(g1,g2)
    c: InternalAlignment(g1,g3)
    c: InternalAlignment(g2,g3)
    c: InternalAlignment(g4,g3)
    c: InternalAlignment(g5,g3)
    c: Block(g3)
    c: Coincident(g6,g0)
    c: Coincident(g6,g3)
    c: Horizontal(g6)
FEATURE [Part::Extrusion] Extrude013  label="caseScrewPillarBracket001"
  Base = -> Sketch019
  Dir = (0,0,1)
  DirMode = 2
  FaceMakerClass = Part::FaceMakerBullseye
  LengthFwd = 2.4
  LengthRev = 0
  Placement = pos=(15.76,29,60.8) rot=(0,0,1;0rad)
  Solid = true
  Symmetric = false
FEATURE [Sketcher::SketchObject] Sketch020
  FullyConstrained = true
  sketch-geometry (7):
    g0: LineSegment StartX=0 StartY=0 StartZ=0 EndX=0 EndY=6 EndZ=0
    g1: Circle CenterX=0 CenterY=0 CenterZ=0 NormalX=0 NormalY=0 NormalZ=1 AngleXU=0 Radius=1
    g2: Circle CenterX=8 CenterY=6 CenterZ=0 NormalX=0 NormalY=0 NormalZ=1 AngleXU=0 Radius=1
    g3: BSplineCurve PolesCount=3 KnotsCount=2 Degree=2 IsPeriodic=0
    g4: GeomPoint X=0 Y=0 Z=0
    g5: GeomPoint X=8 Y=6 Z=0
    g6: LineSegment StartX=0 StartY=6 StartZ=0 EndX=8 EndY=6 EndZ=0
  constraints (14):
    c: Coincident(g0,g-1)
    c: Distance(g0) = 6
    c: Vertical(g0)
    c: Coincident(g3,g0)
    c: Weight(g1) = 1
    c: Equal(g1,g2)
    c: InternalAlignment(g1,g3)
    c: InternalAlignment(g2,g3)
    c: InternalAlignment(g4,g3)
    c: InternalAlignment(g5,g3)
    c: Block(g3)
    c: Coincident(g6,g0)
    c: Coincident(g6,g3)
    c: Horizontal(g6)
FEATURE [Part::Extrusion] Extrude014  label="caseScrewPillarBracket002"
  Base = -> Sketch020
  Dir = (0,0,1)
  DirMode = 2
  FaceMakerClass = Part::FaceMakerBullseye
  LengthFwd = 2.4
  LengthRev = 0
  Placement = pos=(13.7,29,13.26) rot=(0,-1,0;1.5708rad)
  Solid = true
  Symmetric = false
FEATURE [Sketcher::SketchObject] Sketch021
  FullyConstrained = true
  sketch-geometry (7):
    g0: LineSegment StartX=0 StartY=0 StartZ=0 EndX=0 EndY=6 EndZ=0
    g1: Circle CenterX=0 CenterY=0 CenterZ=0 NormalX=0 NormalY=0 NormalZ=1 AngleXU=0 Radius=1
    g2: Circle CenterX=8 CenterY=6 CenterZ=0 NormalX=0 NormalY=0 NormalZ=1 AngleXU=0 Radius=1
    g3: BSplineCurve PolesCount=3 KnotsCount=2 Degree=2 IsPeriodic=0
    g4: GeomPoint X=0 Y=0 Z=0
    g5: GeomPoint X=8 Y=6 Z=0
    g6: LineSegment StartX=0 StartY=6 StartZ=0 EndX=8 EndY=6 EndZ=0
  constraints (14):
    c: Coincident(g0,g-1)
    c: Distance(g0) = 6
    c: Vertical(g0)
    c: Coincident(g3,g0)
    c: Weight(g1) = 1
    c: Equal(g1,g2)
    c: InternalAlignment(g1,g3)
    c: InternalAlignment(g2,g3)
    c: InternalAlignment(g4,g3)
    c: InternalAlignment(g5,g3)
    c: Block(g3)
    c: Coincident(g6,g0)
    c: Coincident(g6,g3)
    c: Horizontal(g6)
FEATURE [Part::Extrusion] Extrude015  label="caseScrewPillarBracket003"
  Base = -> Sketch021
  Dir = (0,0,1)
  DirMode = 2
  FaceMakerClass = Part::FaceMakerBullseye
  LengthFwd = 2.4
  LengthRev = 0
  Placement = pos=(11.3,29,58.74) rot=(0,1,0;1.5708rad)
  Solid = true
  Symmetric = false
FEATURE [Sketcher::SketchObject] Sketch022
  FullyConstrained = true
  sketch-geometry (7):
    g0: LineSegment StartX=0 StartY=0 StartZ=0 EndX=0 EndY=6 EndZ=0
    g1: Circle CenterX=0 CenterY=0 CenterZ=0 NormalX=0 NormalY=0 NormalZ=1 AngleXU=0 Radius=1
    g2: Circle CenterX=8 CenterY=6 CenterZ=0 NormalX=0 NormalY=0 NormalZ=1 AngleXU=0 Radius=1
    g3: BSplineCurve PolesCount=3 KnotsCount=2 Degree=2 IsPeriodic=0
    g4: GeomPoint X=0 Y=0 Z=0
    g5: GeomPoint X=8 Y=6 Z=0
    g6: LineSegment StartX=0 StartY=6 StartZ=0 EndX=8 EndY=6 EndZ=0
  constraints (14):
    c: Coincident(g0,g-1)
    c: Distance(g0) = 6
    c: Vertical(g0)
    c: Coincident(g3,g0)
    c: Weight(g1) = 1
    c: Equal(g1,g2)
    c: InternalAlignment(g1,g3)
    c: InternalAlignment(g2,g3)
    c: InternalAlignment(g4,g3)
    c: InternalAlignment(g5,g3)
    c: Block(g3)
    c: Coincident(g6,g0)
    c: Coincident(g6,g3)
    c: Horizontal(g6)
FEATURE [Part::Extrusion] Extrude016  label="caseScrewPillarBracket004"
  Base = -> Sketch022
  Dir = (0,0,1)
  DirMode = 2
  FaceMakerClass = Part::FaceMakerBullseye
  LengthFwd = 2.4
  LengthRev = 0
  Placement = pos=(88.3,29,65.23) rot=(0,1,0;1.5708rad)
  Solid = true
  Symmetric = false
FEATURE [Sketcher::SketchObject] Sketch023
  FullyConstrained = true
  sketch-geometry (7):
    g0: LineSegment StartX=0 StartY=0 StartZ=0 EndX=0 EndY=6 EndZ=0
    g1: Circle CenterX=0 CenterY=0 CenterZ=0 NormalX=0 NormalY=0 NormalZ=1 AngleXU=0 Radius=1
    g2: Circle CenterX=8 CenterY=6 CenterZ=0 NormalX=0 NormalY=0 NormalZ=1 AngleXU=0 Radius=1
    g3: BSplineCurve PolesCount=3 KnotsCount=2 Degree=2 IsPeriodic=0
    g4: GeomPoint X=0 Y=0 Z=0
    g5: GeomPoint X=8 Y=6 Z=0
    g6: LineSegment StartX=0 StartY=6 StartZ=0 EndX=8 EndY=6 EndZ=0
  constraints (14):
    c: Coincident(g0,g-1)
    c: Distance(g0) = 6
    c: Vertical(g0)
    c: Coincident(g3,g0)
    c: Weight(g1) = 1
    c: Equal(g1,g2)
    c: InternalAlignment(g1,g3)
    c: InternalAlignment(g2,g3)
    c: InternalAlignment(g4,g3)
    c: InternalAlignment(g5,g3)
    c: Block(g3)
    c: Coincident(g6,g0)
    c: Coincident(g6,g3)
    c: Horizontal(g6)
FEATURE [Part::Extrusion] Extrude017  label="caseScrewPillarBracket005"
  Base = -> Sketch023
  Dir = (0,0,1)
  DirMode = 2
  FaceMakerClass = Part::FaceMakerBullseye
  LengthFwd = 2.4
  LengthRev = 0
  Placement = pos=(90.7,29,6.77) rot=(0,-1,0;1.5708rad)
  Solid = true
  Symmetric = false
FEATURE [Sketcher::SketchObject] Sketch024
  FullyConstrained = true
  sketch-geometry (7):
    g0: LineSegment StartX=0 StartY=0 StartZ=0 EndX=0 EndY=6 EndZ=0
    g1: Circle CenterX=0 CenterY=0 CenterZ=0 NormalX=0 NormalY=0 NormalZ=1 AngleXU=0 Radius=1
    g2: Circle CenterX=8 CenterY=6 CenterZ=0 NormalX=0 NormalY=0 NormalZ=1 AngleXU=0 Radius=1
    g3: BSplineCurve PolesCount=3 KnotsCount=2 Degree=2 IsPeriodic=0
    g4: GeomPoint X=0 Y=0 Z=0
    g5: GeomPoint X=8 Y=6 Z=0
    g6: LineSegment StartX=0 StartY=6 StartZ=0 EndX=8 EndY=6 EndZ=0
  constraints (14):
    c: Coincident(g0,g-1)
    c: Distance(g0) = 6
    c: Vertical(g0)
    c: Coincident(g3,g0)
    c: Weight(g1) = 1
    c: Equal(g1,g2)
    c: InternalAlignment(g1,g3)
    c: InternalAlignment(g2,g3)
    c: InternalAlignment(g4,g3)
    c: InternalAlignment(g5,g3)
    c: Block(g3)
    c: Coincident(g6,g0)
    c: Coincident(g6,g3)
    c: Horizontal(g6)
FEATURE [Part::Extrusion] Extrude018  label="caseScrewPillarBracket006"
  Base = -> Sketch024
  Dir = (0,0,1)
  DirMode = 2
  FaceMakerClass = Part::FaceMakerBullseye
  LengthFwd = 2.4
  LengthRev = 0
  Placement = pos=(103.7,29,6.77) rot=(0,-1,0;1.5708rad)
  Solid = true
  Symmetric = false
FEATURE [Sketcher::SketchObject] Sketch025
  FullyConstrained = true
  sketch-geometry (7):
    g0: LineSegment StartX=0 StartY=0 StartZ=0 EndX=0 EndY=6 EndZ=0
    g1: Circle CenterX=0 CenterY=0 CenterZ=0 NormalX=0 NormalY=0 NormalZ=1 AngleXU=0 Radius=1
    g2: Circle CenterX=8 CenterY=6 CenterZ=0 NormalX=0 NormalY=0 NormalZ=1 AngleXU=0 Radius=1
    g3: BSplineCurve PolesCount=3 KnotsCount=2 Degree=2 IsPeriodic=0
    g4: GeomPoint X=0 Y=0 Z=0
    g5: GeomPoint X=8 Y=6 Z=0
    g6: LineSegment StartX=0 StartY=6 StartZ=0 EndX=8 EndY=6 EndZ=0
  constraints (14):
    c: Coincident(g0,g-1)
    c: Distance(g0) = 6
    c: Vertical(g0)
    c: Coincident(g3,g0)
    c: Weight(g1) = 1
    c: Equal(g1,g2)
    c: InternalAlignment(g1,g3)
    c: InternalAlignment(g2,g3)
    c: InternalAlignment(g4,g3)
    c: InternalAlignment(g5,g3)
    c: Block(g3)
    c: Coincident(g6,g0)
    c: Coincident(g6,g3)
    c: Horizontal(g6)
FEATURE [Part::Extrusion] Extrude019  label="caseScrewPillarBracket007"
  Base = -> Sketch025
  Dir = (0,0,1)
  DirMode = 2
  FaceMakerClass = Part::FaceMakerBullseye
  LengthFwd = 2.4
  LengthRev = 0
  Placement = pos=(101.3,29,65.23) rot=(0,1,0;1.5708rad)
  Solid = true
  Symmetric = false
FEATURE [Part::Box] Box011  label="frontCaseScrewPillarBracket"
  AttacherType = Attacher::AttachEngine3D
  Height = 2.4
  Length = 16
  Placement = pos=(87,28,2.3) rot=(0,0,1;0rad)
  Width = 7
FEATURE [Part::Box] Box012  label="frontCaseScrewPillarBracket001"
  AttacherType = Attacher::AttachEngine3D
  Height = 2.4
  Length = 16
  Placement = pos=(87,28,67.3) rot=(0,0,1;0rad)
  Width = 7
FEATURE [Sketcher::SketchObject] Sketch026
  FullyConstrained = true
  sketch-geometry (17):
    g0: Circle CenterX=-3.5 CenterY=23.5 CenterZ=0 NormalX=0 NormalY=0 NormalZ=1 AngleXU=0 Radius=1
    g1: Circle CenterX=-1 CenterY=15.25 CenterZ=0 NormalX=0 NormalY=0 NormalZ=1 AngleXU=0 Radius=1
    g2: Circle CenterX=-3.5 CenterY=7 CenterZ=0 NormalX=0 NormalY=0 NormalZ=1 AngleXU=0 Radius=1
    g3: BSplineCurve PolesCount=3 KnotsCount=2 Degree=2 IsPeriodic=0
    g4: GeomPoint X=-3.5 Y=23.5 Z=0
    g5: GeomPoint X=-3.5 Y=7 Z=0
    g6: Circle CenterX=-4.8 CenterY=30.5 CenterZ=0 NormalX=0 NormalY=0 NormalZ=1 AngleXU=0 Radius=1
    g7: Circle CenterX=-3.5 CenterY=30.5 CenterZ=0 NormalX=0 NormalY=0 NormalZ=1 AngleXU=0 Radius=1
    g8: Circle CenterX=-3.5 CenterY=29.2 CenterZ=0 NormalX=0 NormalY=0 NormalZ=1 AngleXU=0 Radius=1
    g9: BSplineCurve PolesCount=3 KnotsCount=2 Degree=2 IsPeriodic=0
    g10: GeomPoint X=-4.8 Y=30.5 Z=0
    g11: GeomPoint X=-3.5 Y=29.2 Z=0
    g12: LineSegment StartX=-3.5 StartY=29.2 StartZ=0 EndX=-3.5 EndY=23.5 EndZ=0
    g13: LineSegment StartX=-4.8 StartY=30.5 StartZ=0 EndX=0 EndY=30.5 EndZ=0
    g14: LineSegment StartX=-3.5 StartY=5 StartZ=0 EndX=-3.5 EndY=7 EndZ=0
    g15: LineSegment StartX=0 StartY=5 StartZ=0 EndX=0 EndY=30.5 EndZ=0
    g16: LineSegment StartX=-3.5 StartY=5 StartZ=0 EndX=0 EndY=5 EndZ=0
  constraints (33):
    c: Weight(g0) = 1
    c: Equal(g0,g1)
    c: Equal(g0,g2)
    c: InternalAlignment(g0,g3)
    c: InternalAlignment(g1,g3)
    c: InternalAlignment(g2,g3)
    c: InternalAlignment(g4,g3)
    c: InternalAlignment(g5,g3)
    c: Block(g3)
    c: Weight(g6) = 1
    c: Equal(g6,g7)
    c: Equal(g6,g8)
    c: InternalAlignment(g6,g9)
    c: InternalAlignment(g7,g9)
    c: InternalAlignment(g8,g9)
    c: InternalAlignment(g10,g9)
    c: InternalAlignment(g11,g9)
    c: Block(g9)
    c: Coincident(g12,g9)
    c: Coincident(g12,g3)
    c: Vertical(g12)
    c: Coincident(g13,g9)
    c: Horizontal(g13)
    c: Distance(g13) = 4.8
    c: Coincident(g14,g3)
    c: Vertical(g14)
    c: Coincident(g15,g13)
    c: Vertical(g15)
    c: Tangent(g15,g1)
    c: Distance(g14) = 2
    c: Coincident(g16,g14)
    c: Horizontal(g16)
    c: Coincident(g15,g16)
FEATURE [Part::Feature] Face050
  shape: bbox 4.8 x 25.5 x 2e-07 mm, 1 faces, 0 solids (baked)
FEATURE [Part::Revolution] Revolve054  label="moreFrontCaseScrewPost001"
  Angle = 360
  Axis = (0,1,0)
  Base = (0,0,0)
  FaceMakerClass = Part::FaceMakerBullseye
  Placement = pos=(102.5,4.5,3.5) rot=(0,0,1;0rad)
  Solid = false
  Source = -> Face050
  Symmetric = false
FEATURE [Part::Feature] Face051
  shape: bbox 4.8 x 25.5 x 2e-07 mm, 1 faces, 0 solids (baked)
FEATURE [Part::Revolution] Revolve055  label="moreFrontCaseScrewPost002"
  Angle = 360
  Axis = (0,1,0)
  Base = (0,0,0)
  FaceMakerClass = Part::FaceMakerBullseye
  Placement = pos=(102.5,4.5,68.5) rot=(0,0,1;0rad)
  Solid = false
  Source = -> Face051
  Symmetric = false
FEATURE [Sketcher::SketchObject] Sketch027
  FullyConstrained = true
  sketch-geometry (10):
    g0: LineSegment StartX=-1.6 StartY=4.7 StartZ=0 EndX=-1.6 EndY=1.7 EndZ=0
    g1: LineSegment StartX=-3.5 StartY=4.7 StartZ=0 EndX=-1.6 EndY=4.7 EndZ=0
    g2: LineSegment StartX=-1.6 StartY=1.7 StartZ=0 EndX=-1.6 EndY=1.5 EndZ=0
    g3: LineSegment StartX=-1.6 StartY=1.5 StartZ=0 EndX=-5.2 EndY=1.5 EndZ=0
    g4: Circle CenterX=-3.5 CenterY=4.7 CenterZ=0 NormalX=0 NormalY=0 NormalZ=1 AngleXU=0 Radius=1
    g5: Circle CenterX=-3.59627 CenterY=2.99743 CenterZ=0 NormalX=0 NormalY=0 NormalZ=1 AngleXU=0 Radius=1
    g6: Circle CenterX=-5.2 CenterY=1.5 CenterZ=0 NormalX=0 NormalY=0 NormalZ=1 AngleXU=0 Radius=1
    g7: BSplineCurve PolesCount=3 KnotsCount=2 Degree=2 IsPeriodic=0
    g8: GeomPoint X=-3.5 Y=4.7 Z=0
    g9: GeomPoint X=-5.2 Y=1.5 Z=0
  constraints (23):
    c: Vertical(g0)
    c: Distance(g0) = 3
    c: Coincident(g1,g0)
    c: Horizontal(g1)
    c: Block(g0)
    c: Block(g1)
    c: Coincident(g2,g0)
    c: Vertical(g2)
    c: Distance(g2) = 0.2
    c: Coincident(g3,g2)
    c: Horizontal(g3)
    c: Block(g3)
    c: Coincident(g7,g1)
    c: Weight(g4) = 1
    c: Equal(g4,g5)
    c: Equal(g4,g6)
    c: Coincident(g7,g3)
    c: InternalAlignment(g4,g7)
    c: InternalAlignment(g5,g7)
    c: InternalAlignment(g6,g7)
    c: InternalAlignment(g8,g7)
    c: InternalAlignment(g9,g7)
    c: Block(g7)
FEATURE [Sketcher::SketchObject] Sketch028
  FullyConstrained = true
  sketch-geometry (18):
    g0: LineSegment StartX=0 StartY=3e-16 StartZ=0 EndX=0 EndY=1.7 EndZ=0
    g1: LineSegment StartX=-3.5 StartY=0 StartZ=0 EndX=-3.5 EndY=0.9 EndZ=0
    g2: Circle CenterX=-2.7 CenterY=1.7 CenterZ=0 NormalX=0 NormalY=0 NormalZ=1 AngleXU=0 Radius=1
    g3: Circle CenterX=-3.5 CenterY=1.7 CenterZ=0 NormalX=0 NormalY=0 NormalZ=1 AngleXU=0 Radius=1
    g4: Circle CenterX=-3.5 CenterY=0.9 CenterZ=0 NormalX=0 NormalY=0 NormalZ=1 AngleXU=0 Radius=1
    g5: BSplineCurve PolesCount=3 KnotsCount=2 Degree=2 IsPeriodic=0
    g6: GeomPoint X=-2.7 Y=1.7 Z=0
    g7: GeomPoint X=-3.5 Y=0.9 Z=0
    g8: LineSegment StartX=-3.5 StartY=0 StartZ=0 EndX=-3.5 EndY=-7 EndZ=0
    g9: LineSegment StartX=0 StartY=3e-16 StartZ=0 EndX=0 EndY=-7 EndZ=0
    g10: LineSegment StartX=-3.5 StartY=-7 StartZ=0 EndX=0 EndY=-7 EndZ=0
    g11: LineSegment StartX=-2.7 StartY=1.7 StartZ=0 EndX=-1.6 EndY=1.7 EndZ=0
    g12: LineSegment StartX=0 StartY=1.7 StartZ=0 EndX=0 EndY=4.5 EndZ=0
    g13: LineSegment StartX=0 StartY=4.5 StartZ=0 EndX=0 EndY=10.8 EndZ=0
    g14: LineSegment StartX=0 StartY=10.8 StartZ=0 EndX=-2 EndY=10.8 EndZ=0
    g15: LineSegment StartX=-1.6 StartY=4.7 StartZ=0 EndX=-1.6 EndY=1.7 EndZ=0
    g16: LineSegment StartX=-1.6 StartY=4.7 StartZ=0 EndX=-2 EndY=4.7 EndZ=0
    g17: LineSegment StartX=-2 StartY=4.7 StartZ=0 EndX=-2 EndY=10.8 EndZ=0
  constraints (44):
    c: Vertical(g0)
    c: Vertical(g1)
    c: Distance(g1) = 0.9
    c: Block(g0)
    c: Distance(g0) = 1.7
    c: Weight(g2) = 1
    c: Equal(g2,g3)
    c: Equal(g2,g4)
    c: Coincident(g5,g1)
    c: InternalAlignment(g2,g5)
    c: InternalAlignment(g3,g5)
    c: InternalAlignment(g4,g5)
    c: InternalAlignment(g6,g5)
    c: InternalAlignment(g7,g5)
    c: Block(g5)
    c: Coincident(g8,g1)
    c: Vertical(g8)
    c: Distance(g8) = 7
    c: Vertical(g9)
    c: Equal(g8,g9) = 7
    c: Coincident(g9,g0)
    c: Coincident(g10,g8)
    c: Coincident(g10,g9)
    c: Horizontal(g10)
    c: Coincident(g11,g5)
    c: Horizontal(g11)
    c: Coincident(g12,g0)
    c: Vertical(g12)
    c: Distance(g12) = 2.8
    c: Coincident(g13,g12)
    c: Vertical(g13)
    c: Distance(g13) = 6.3
    c: Coincident(g14,g13)
    c: Horizontal(g14)
    c: Distance(g14) = 2
    c: Vertical(g15)
    c: Distance(g15) = 3
    c: Block(g11)
    c: Coincident(g15,g11)
    c: Coincident(g16,g15)
    c: Horizontal(g16)
    c: Coincident(g17,g16)
    c: Coincident(g17,g14)
    c: Vertical(g17)
FEATURE [Part::Revolution] Revolve040  label="backCaseScrewRetainer001"
  Angle = 360
  Axis = (0,1,0)
  Base = (0,0,0)
  FaceMakerClass = Part::FaceMakerBullseye
  Placement = pos=(12.5,3,10) rot=(0,0,1;0rad)
  Solid = false
  Source = -> Face036
  Symmetric = false
FEATURE [Part::Feature] Face055
  shape: bbox 3.5 x 30.2 x 2e-07 mm, 1 faces, 0 solids (baked)
FEATURE [Part::Revolution] Revolve059  label="backCaseScrewPost"
  Angle = 360
  Axis = (0,1,0)
  Base = (0,0,0)
  FaceMakerClass = Part::FaceMakerBullseye
  Placement = pos=(12.5,4.5,10) rot=(0,0,1;0rad)
  Solid = false
  Source = -> Face055
  Symmetric = false
FEATURE [Part::Feature] Face056
  shape: bbox 3.5 x 30.2 x 2e-07 mm, 1 faces, 0 solids (baked)
FEATURE [Part::Revolution] Revolve060  label="backCaseScrewPost001"
  Angle = 360
  Axis = (0,1,0)
  Base = (0,0,0)
  FaceMakerClass = Part::FaceMakerBullseye
  Placement = pos=(12.5,4.5,62) rot=(0,0,1;0rad)
  Solid = false
  Source = -> Face056
  Symmetric = false
FEATURE [Part::Feature] Face057
  shape: bbox 3.5 x 17.8 x 2e-07 mm, 1 faces, 0 solids (baked)
FEATURE [Part::Revolution] Revolve061  label="removeToCreateScrewAndThreadedInsertHole"
  Angle = 360
  Axis = (0,1,0)
  Base = (0,0,0)
  FaceMakerClass = Part::FaceMakerBullseye
  Placement = pos=(12.5,0,10) rot=(0,0,1;0rad)
  Solid = false
  Source = -> Face057
  Symmetric = false
FEATURE [Part::Feature] Face058
  shape: bbox 3.5 x 17.8 x 2e-07 mm, 1 faces, 0 solids (baked)
FEATURE [Part::Revolution] Revolve062  label="removeToCreateScrewAndThreadedInsertHole001"
  Angle = 360
  Axis = (0,1,0)
  Base = (0,0,0)
  FaceMakerClass = Part::FaceMakerBullseye
  Placement = pos=(12.5,0,62) rot=(0,0,1;0rad)
  Solid = false
  Source = -> Face058
  Symmetric = false
FEATURE [Part::Feature] Face059
  shape: bbox 3.5 x 17.8 x 2e-07 mm, 1 faces, 0 solids (baked)
FEATURE [Part::Revolution] Revolve063  label="removeToCreateScrewAndThreadedInsertHole002"
  Angle = 360
  Axis = (0,1,0)
  Base = (0,0,0)
  FaceMakerClass = Part::FaceMakerBullseye
  Placement = pos=(89.5,0,68.5) rot=(0,0,1;0rad)
  Solid = false
  Source = -> Face059
  Symmetric = false
FEATURE [Part::Feature] Face060
  shape: bbox 3.5 x 17.8 x 2e-07 mm, 1 faces, 0 solids (baked)
FEATURE [Part::Revolution] Revolve064  label="removeToCreateScrewAndThreadedInsertHole003"
  Angle = 360
  Axis = (0,1,0)
  Base = (0,0,0)
  FaceMakerClass = Part::FaceMakerBullseye
  Placement = pos=(89.5,0,3.5) rot=(0,0,1;0rad)
  Solid = false
  Source = -> Face060
  Symmetric = false
FEATURE [Part::Feature] Face061
  shape: bbox 3.5 x 17.8 x 2e-07 mm, 1 faces, 0 solids (baked)
FEATURE [Part::Revolution] Revolve065  label="removeToCreateScrewAndThreadedInsertHole004"
  Angle = 360
  Axis = (0,1,0)
  Base = (0,0,0)
  FaceMakerClass = Part::FaceMakerBullseye
  Placement = pos=(102.5,4.7,3.5) rot=(0,0,1;0rad)
  Solid = false
  Source = -> Face061
  Symmetric = false
FEATURE [Part::Feature] Face062
  shape: bbox 3.5 x 17.8 x 2e-07 mm, 1 faces, 0 solids (baked)
FEATURE [Part::Revolution] Revolve066  label="removeToCreateScrewAndThreadedInsertHole005"
  Angle = 360
  Axis = (0,1,0)
  Base = (0,0,0)
  FaceMakerClass = Part::FaceMakerBullseye
  Placement = pos=(102.5,4.7,68.5) rot=(0,0,1;0rad)
  Solid = false
  Source = -> Face062
  Symmetric = false
FEATURE [Part::MultiFuse] Fusion047  label="makeHoles"
  Shapes = -> [Revolve066,Revolve065,Revolve064,Revolve063,Revolve062,Revolve061]
FEATURE [Part::Feature] Face063
  shape: bbox 3.6 x 3.2 x 2e-07 mm, 1 faces, 0 solids (baked)
FEATURE [Part::Revolution] Revolve067  label="moreFrontCaseScrewRetainer002"
  Angle = 360
  Axis = (0,1,0)
  Base = (0,0,0)
  FaceMakerClass = Part::FaceMakerBullseye
  Placement = pos=(102.5,4.5,68.5) rot=(0,0,1;0rad)
  Solid = false
  Source = -> Face063
  Symmetric = false
FEATURE [Part::Feature] Face064
  shape: bbox 3.6 x 3.2 x 2e-07 mm, 1 faces, 0 solids (baked)
FEATURE [Part::Revolution] Revolve068  label="moreFrontCaseScrewRetainer003"
  Angle = 360
  Axis = (0,1,0)
  Base = (0,0,0)
  FaceMakerClass = Part::FaceMakerBullseye
  Placement = pos=(102.5,4.5,3.5) rot=(0,0,1;0rad)
  Solid = false
  Source = -> Face064
  Symmetric = false
FEATURE [Part::Feature] Face065
  shape: bbox 3.5 x 17.8 x 2e-07 mm, 1 faces, 0 solids (baked)
FEATURE [Part::Revolution] Revolve069  label="removeToCreateScrewAndThreadedInsertHole006"
  Angle = 360
  Axis = (0,1,0)
  Base = (0,0,0)
  FaceMakerClass = Part::FaceMakerBullseye
  Placement = pos=(12.5,0,10) rot=(0,0,1;0rad)
  Solid = false
  Source = -> Face065
  Symmetric = false
FEATURE [Part::Feature] Face066
  shape: bbox 3.5 x 17.8 x 2e-07 mm, 1 faces, 0 solids (baked)
FEATURE [Part::Revolution] Revolve070  label="removeToCreateScrewAndThreadedInsertHole007"
  Angle = 360
  Axis = (0,1,0)
  Base = (0,0,0)
  FaceMakerClass = Part::FaceMakerBullseye
  Placement = pos=(12.5,0,62) rot=(0,0,1;0rad)
  Solid = false
  Source = -> Face066
  Symmetric = false
FEATURE [Part::Feature] Face067
  shape: bbox 3.5 x 17.8 x 2e-07 mm, 1 faces, 0 solids (baked)
FEATURE [Part::Revolution] Revolve071  label="removeToCreateScrewAndThreadedInsertHole008"
  Angle = 360
  Axis = (0,1,0)
  Base = (0,0,0)
  FaceMakerClass = Part::FaceMakerBullseye
  Placement = pos=(89.5,0,68.5) rot=(0,0,1;0rad)
  Solid = false
  Source = -> Face067
  Symmetric = false
FEATURE [Part::Feature] Face068
  shape: bbox 3.5 x 17.8 x 2e-07 mm, 1 faces, 0 solids (baked)
FEATURE [Part::Revolution] Revolve072  label="removeToCreateScrewAndThreadedInsertHole009"
  Angle = 360
  Axis = (0,1,0)
  Base = (0,0,0)
  FaceMakerClass = Part::FaceMakerBullseye
  Placement = pos=(89.5,0,3.5) rot=(0,0,1;0rad)
  Solid = false
  Source = -> Face068
  Symmetric = false
FEATURE [Part::Feature] Face069
  shape: bbox 3.5 x 17.8 x 2e-07 mm, 1 faces, 0 solids (baked)
FEATURE [Part::Feature] Face070
  shape: bbox 3.5 x 17.8 x 2e-07 mm, 1 faces, 0 solids (baked)
FEATURE [Part::Revolution] Revolve073  label="removeToCreateScrewAndThreadedInsertHole010"
  Angle = 360
  Axis = (0,1,0)
  Base = (0,0,0)
  FaceMakerClass = Part::FaceMakerBullseye
  Placement = pos=(102.5,4.7,3.5) rot=(0,0,1;0rad)
  Solid = false
  Source = -> Face069
  Symmetric = false
FEATURE [Part::Revolution] Revolve074  label="removeToCreateScrewAndThreadedInsertHole011"
  Angle = 360
  Axis = (0,1,0)
  Base = (0,0,0)
  FaceMakerClass = Part::FaceMakerBullseye
  Placement = pos=(102.5,4.7,68.5) rot=(0,0,1;0rad)
  Solid = false
  Source = -> Face070
  Symmetric = false
FEATURE [Part::MultiFuse] Fusion048  label="makeHoles001"
  Shapes = -> [Revolve074,Revolve073,Revolve072,Revolve071,Revolve070,Revolve069]
FEATURE [Part::MultiFuse] Fusion049  label="caseScrewRetainers"
  Shapes = -> [Revolve067,Revolve068,Revolve048,Revolve047,Revolve039,Revolve040]
FEATURE [Part::Cut] Cut015  label="caseScrewRetainers001"
  Base = -> Fusion049
  Tool = -> Fusion048
FEATURE [Part::MultiFuse] Fusion050  label="casePillars"
  Shapes = -> [Revolve055,Revolve054,Revolve043,Revolve046,Revolve059,Revolve060]
FEATURE [Part::Feature] Face071 .. Face076  x6 (patterned run collapsed; names and placements below)
  shape: bbox 3.5 x 17.8 x 2e-07 mm, 1 faces, 0 solids (baked)
FEATURE [Part::Revolution] Revolve075  label="removeToCreateScrewAndThreadedInsertHole012"
  Angle = 360
  Axis = (0,1,0)
  Base = (0,0,0)
  FaceMakerClass = Part::FaceMakerBullseye
  Placement = pos=(12.5,0,10) rot=(0,0,1;0rad)
  Solid = false
  Source = -> Face071
  Symmetric = false
FEATURE [Part::Revolution] Revolve076  label="removeToCreateScrewAndThreadedInsertHole013"
  Angle = 360
  Axis = (0,1,0)
  Base = (0,0,0)
  FaceMakerClass = Part::FaceMakerBullseye
  Placement = pos=(12.5,0,62) rot=(0,0,1;0rad)
  Solid = false
  Source = -> Face072
  Symmetric = false
FEATURE [Part::Revolution] Revolve077  label="removeToCreateScrewAndThreadedInsertHole014"
  Angle = 360
  Axis = (0,1,0)
  Base = (0,0,0)
  FaceMakerClass = Part::FaceMakerBullseye
  Placement = pos=(89.5,0,68.5) rot=(0,0,1;0rad)
  Solid = false
  Source = -> Face073
  Symmetric = false
FEATURE [Part::Revolution] Revolve078  label="removeToCreateScrewAndThreadedInsertHole015"
  Angle = 360
  Axis = (0,1,0)
  Base = (0,0,0)
  FaceMakerClass = Part::FaceMakerBullseye
  Placement = pos=(89.5,0,3.5) rot=(0,0,1;0rad)
  Solid = false
  Source = -> Face074
  Symmetric = false
FEATURE [Part::Revolution] Revolve079  label="removeToCreateScrewAndThreadedInsertHole016"
  Angle = 360
  Axis = (0,1,0)
  Base = (0,0,0)
  FaceMakerClass = Part::FaceMakerBullseye
  Placement = pos=(102.5,4.7,3.5) rot=(0,0,1;0rad)
  Solid = false
  Source = -> Face075
  Symmetric = false
FEATURE [Part::Revolution] Revolve080  label="removeToCreateScrewAndThreadedInsertHole017"
  Angle = 360
  Axis = (0,1,0)
  Base = (0,0,0)
  FaceMakerClass = Part::FaceMakerBullseye
  Placement = pos=(102.5,4.7,68.5) rot=(0,0,1;0rad)
  Solid = false
  Source = -> Face076
  Symmetric = false
FEATURE [Part::MultiFuse] Fusion051  label="makeHoles002"
  Shapes = -> [Revolve080,Revolve079,Revolve078,Revolve077,Revolve076,Revolve075]
FEATURE [Part::Cut] Cut016  label="caesPillars"
  Base = -> Fusion050
  Tool = -> Fusion051
FEATURE [Part::Revolution] Revolve009  label="plugHousing016"
  Angle = 360
  Axis = (0,1,0)
  Base = (0,0,0)
  FaceMakerClass = Part::FaceMakerBullseye
  Placement = pos=(0,0,36.15) rot=(0,0,1;0rad)
  Solid = false
  Source = -> Face012
  Symmetric = false
FEATURE [Part::MultiFuse] Fusion014  label="plugHousing023"
  Placement = pos=(0,0,0) rot=(0,0,1;1.5708rad)
  Shapes = -> [Revolve011,Revolve009]
FEATURE [Part::Revolution] Revolve010  label="plugHousing017"
  Angle = 360
  Axis = (0,1,0)
  Base = (0,0,0)
  FaceMakerClass = Part::FaceMakerBullseye
  Placement = pos=(0,0,36.15) rot=(0,0,1;0rad)
  Solid = false
  Source = -> Face014
  Symmetric = false
FEATURE [Part::MultiFuse] Fusion015  label="plugHousing024"
  Placement = pos=(0,0,0) rot=(0,0,1;1.5708rad)
  Shapes = -> [Revolve010,Revolve015]
FEATURE [Part::Revolution] Revolve014  label="plugHousing026"
  Angle = 360
  Axis = (0,1,0)
  Base = (0,0,0)
  FaceMakerClass = Part::FaceMakerBullseye
  Placement = pos=(0,0,36.15) rot=(0,0,1;0rad)
  Solid = false
  Source = -> Face011
  Symmetric = false
FEATURE [Part::Revolution] Revolve013  label="plugHousing025"
  Angle = 360
  Axis = (0,1,0)
  Base = (0,0,0)
  FaceMakerClass = Part::FaceMakerBullseye
  Placement = pos=(0,0,36.15) rot=(0,0,1;0rad)
  Solid = false
  Source = -> Face015
  Symmetric = false
FEATURE [Part::MultiFuse] Fusion016  label="plugHousing028"
  Placement = pos=(0,19,0) rot=(0,0,1;3.14159rad)
  Shapes = -> [Fusion014,Fusion013]
FEATURE [Part::MultiFuse] Fusion011  label="plugHousing018"
  Placement = pos=(0,0,0) rot=(0,0,1;1.5708rad)
  Shapes = -> [Revolve014,Revolve013]
FEATURE [Part::MultiFuse] Fusion012  label="plugHousing019"
  Placement = pos=(0,19,0) rot=(0,0,1;3.14159rad)
  Shapes = -> [Fusion011,Fusion015]
FEATURE [Part::MultiFuse] Fusion017  label="plugHousing029"
  Placement = pos=(122.621,0,-0.15) rot=(0,0,1;0rad)
  Shapes = -> [Fusion016,Fusion012]
FEATURE [Part::MultiFuse] Fusion052  label="casePillarRetainers"
  Shapes = -> [Extrude012,Extrude013,Extrude014,Extrude015,Extrude016,Extrude017,Extrude018,Extrude019,Box011,Box012]
FEATURE [Part::Feature] Face077
  shape: bbox 3.5 x 17.8 x 2e-07 mm, 1 faces, 0 solids (baked)
FEATURE [Part::Revolution] Revolve081  label="removeToCreateScrewAndThreadedInsertHole018"
  Angle = 360
  Axis = (0,1,0)
  Base = (0,0,0)
  FaceMakerClass = Part::FaceMakerBullseye
  Placement = pos=(62.3,30.3,19.7) rot=(0,0,1;0rad)
  Solid = false
  Source = -> Face077
  Symmetric = false
FEATURE [Part::Feature] Face078
  shape: bbox 3.5 x 17.8 x 2e-07 mm, 1 faces, 0 solids (baked)
FEATURE [Part::Revolution] Revolve082  label="removeToCreateScrewAndThreadedInsertHole019"
  Angle = 360
  Axis = (0,1,0)
  Base = (0,0,0)
  FaceMakerClass = Part::FaceMakerBullseye
  Placement = pos=(62.3,30.3,51.7) rot=(0,0,1;0rad)
  Solid = false
  Source = -> Face078
  Symmetric = false
FEATURE [Part::Feature] Face079
  shape: bbox 3.5 x 17.8 x 2e-07 mm, 1 faces, 0 solids (baked)
FEATURE [Part::Revolution] Revolve083  label="removeToCreateScrewAndThreadedInsertHole020"
  Angle = 360
  Axis = (0,1,0)
  Base = (0,0,0)
  FaceMakerClass = Part::FaceMakerBullseye
  Placement = pos=(30.3,30.3,19.7) rot=(0,0,1;0rad)
  Solid = false
  Source = -> Face079
  Symmetric = false
FEATURE [Part::Feature] Face080
  shape: bbox 3.5 x 17.8 x 2e-07 mm, 1 faces, 0 solids (baked)
FEATURE [Part::Revolution] Revolve084  label="removeToCreateScrewAndThreadedInsertHole021"
  Angle = 360
  Axis = (0,1,0)
  Base = (0,0,0)
  FaceMakerClass = Part::FaceMakerBullseye
  Placement = pos=(30.3,30.3,51.7) rot=(0,0,1;0rad)
  Solid = false
  Source = -> Face080
  Symmetric = false
FEATURE [Part::MultiFuse] Fusion053  label="createThreadedInsertHolesForFan"
  Shapes = -> [Revolve081,Revolve082,Revolve083,Revolve084]
FEATURE [Part::Cut] Cut017  label="fanScrewHousing001"
  Base = -> Fusion046
  Tool = -> Fusion053
FEATURE [Part::Feature] Face081
  shape: bbox 3.5 x 17.8 x 2e-07 mm, 1 faces, 0 solids (baked)
FEATURE [Part::Revolution] Revolve085  label="removeToCreateScrewAndThreadedInsertHole022"
  Angle = 360
  Axis = (0,1,0)
  Base = (0,0,0)
  FaceMakerClass = Part::FaceMakerBullseye
  Placement = pos=(62.3,30.3,19.7) rot=(0,0,1;0rad)
  Solid = false
  Source = -> Face081
  Symmetric = false
FEATURE [Part::Feature] Face082
  shape: bbox 3.5 x 17.8 x 2e-07 mm, 1 faces, 0 solids (baked)
FEATURE [Part::Revolution] Revolve086  label="removeToCreateScrewAndThreadedInsertHole023"
  Angle = 360
  Axis = (0,1,0)
  Base = (0,0,0)
  FaceMakerClass = Part::FaceMakerBullseye
  Placement = pos=(62.3,30.3,51.7) rot=(0,0,1;0rad)
  Solid = false
  Source = -> Face082
  Symmetric = false
FEATURE [Part::Feature] Face083
  shape: bbox 3.5 x 17.8 x 2e-07 mm, 1 faces, 0 solids (baked)
FEATURE [Part::Revolution] Revolve087  label="removeToCreateScrewAndThreadedInsertHole024"
  Angle = 360
  Axis = (0,1,0)
  Base = (0,0,0)
  FaceMakerClass = Part::FaceMakerBullseye
  Placement = pos=(30.3,30.3,19.7) rot=(0,0,1;0rad)
  Solid = false
  Source = -> Face083
  Symmetric = false
FEATURE [Part::Feature] Face084
  shape: bbox 3.5 x 17.8 x 2e-07 mm, 1 faces, 0 solids (baked)
FEATURE [Part::Revolution] Revolve088  label="removeToCreateScrewAndThreadedInsertHole025"
  Angle = 360
  Axis = (0,1,0)
  Base = (0,0,0)
  FaceMakerClass = Part::FaceMakerBullseye
  Placement = pos=(30.3,30.3,51.7) rot=(0,0,1;0rad)
  Solid = false
  Source = -> Face084
  Symmetric = false
FEATURE [Part::MultiFuse] Fusion054  label="createThreadedInsertHolesForFan001"
  Shapes = -> [Revolve085,Revolve086,Revolve087,Revolve088]
FEATURE [Part::Cut] Cut018  label="top007"
  Base = -> Fusion040
  Tool = -> Fusion054
FEATURE [Sketcher::SketchObject] Sketch029
  FullyConstrained = false
  Placement = pos=(0,0,0) rot=(1,0,0;1.5708rad)
  sketch-geometry (24):
    g0: ArcOfCircle CenterX=-4 CenterY=-10.5 CenterZ=0 NormalX=0 NormalY=0 NormalZ=1 AngleXU=0 Radius=1.5 StartAngle=6e-16 EndAngle=3.14159
    g1: ArcOfCircle CenterX=-34.2 CenterY=-10.5 CenterZ=0 NormalX=0 NormalY=0 NormalZ=1 AngleXU=0 Radius=1.5 StartAngle=0 EndAngle=3.14159
    g2: ArcOfCircle CenterX=-34.2 CenterY=-27.7 CenterZ=0 NormalX=0 NormalY=0 NormalZ=1 AngleXU=0 Radius=1.5 StartAngle=3.14159 EndAngle=6.28319
    g3: ArcOfCircle CenterX=-4 CenterY=-27.7 CenterZ=0 NormalX=0 NormalY=0 NormalZ=1 AngleXU=0 Radius=1.5 StartAngle=3.1416 EndAngle=6.28319
    g4: ArcOfCircle CenterX=-10 CenterY=-4.3 CenterZ=0 NormalX=0 NormalY=0 NormalZ=1 AngleXU=0 Radius=1.5 StartAngle=2e-16 EndAngle=3.14159
    g5: ArcOfCircle CenterX=-16.1 CenterY=-1.8 CenterZ=0 NormalX=0 NormalY=0 NormalZ=1 AngleXU=0 Radius=1.5 StartAngle=5e-16 EndAngle=3.14159
    g6: ArcOfCircle CenterX=-22.1 CenterY=-1.8 CenterZ=0 NormalX=0 NormalY=0 NormalZ=1 AngleXU=0 Radius=1.5 StartAngle=5e-16 EndAngle=3.14159
    g7: ArcOfCircle CenterX=-28.2 CenterY=-4.3 CenterZ=0 NormalX=0 NormalY=0 NormalZ=1 AngleXU=0 Radius=1.5 StartAngle=2e-16 EndAngle=3.14159
    g8: ArcOfCircle CenterX=-10 CenterY=-33.9 CenterZ=0 NormalX=0 NormalY=0 NormalZ=1 AngleXU=0 Radius=1.5 StartAngle=3.14159 EndAngle=6.28319
    g9: ArcOfCircle CenterX=-16.1 CenterY=-36.4 CenterZ=0 NormalX=0 NormalY=0 NormalZ=1 AngleXU=0 Radius=1.5 StartAngle=3.14159 EndAngle=6.28319
    g10: ArcOfCircle CenterX=-22.1 CenterY=-36.4 CenterZ=0 NormalX=0 NormalY=0 NormalZ=1 AngleXU=0 Radius=1.5 StartAngle=3.14159 EndAngle=6.28319
    g11: ArcOfCircle CenterX=-28.2 CenterY=-33.9 CenterZ=0 NormalX=0 NormalY=0 NormalZ=1 AngleXU=0 Radius=1.5 StartAngle=3.14159 EndAngle=6.28319
    g12: LineSegment StartX=-35.7 StartY=-10.5 StartZ=0 EndX=-35.7 EndY=-27.7 EndZ=0
    g13: LineSegment StartX=-32.7 StartY=-10.5 StartZ=0 EndX=-32.7 EndY=-27.7 EndZ=0
    g14: LineSegment StartX=-29.7 StartY=-33.9 StartZ=0 EndX=-29.7 EndY=-4.3 EndZ=0
    g15: LineSegment StartX=-26.7 StartY=-33.9 StartZ=0 EndX=-26.7 EndY=-4.3 EndZ=0
    g16: LineSegment StartX=-2.5 StartY=-10.5 StartZ=0 EndX=-2.5 EndY=-27.7 EndZ=0
    g17: LineSegment StartX=-8.5 StartY=-4.3 StartZ=0 EndX=-8.5 EndY=-33.9 EndZ=0
    g18: LineSegment StartX=-5.5 StartY=-10.5 StartZ=0 EndX=-5.5 EndY=-27.7 EndZ=0
    g19: LineSegment StartX=-11.5 StartY=-4.3 StartZ=0 EndX=-11.5 EndY=-33.9 EndZ=0
    g20: LineSegment StartX=-14.6 StartY=-1.8 StartZ=0 EndX=-14.6 EndY=-36.4 EndZ=0
    g21: LineSegment StartX=-17.6 StartY=-1.8 StartZ=0 EndX=-17.6 EndY=-36.4 EndZ=0
    g22: LineSegment StartX=-20.6 StartY=-36.4 StartZ=0 EndX=-20.6 EndY=-1.8 EndZ=0
    g23: LineSegment StartX=-23.6 StartY=-1.8 StartZ=0 EndX=-23.6 EndY=-36.4 EndZ=0
  constraints (48):
    c: Block(g0)
    c: Block(g1)
    c: Block(g2)
    c: Block(g3)
    c: Block(g4)
    c: Block(g5)
    c: Block(g6)
    c: Block(g7)
    c: Block(g8)
    c: Block(g9)
    c: Block(g10)
    c: Block(g11)
    c: Coincident(g12,g1)
    c: Coincident(g12,g2)
    c: Vertical(g12)
    c: Coincident(g13,g1)
    c: Coincident(g13,g2)
    c: Vertical(g13)
    c: Coincident(g14,g11)
    c: Coincident(g14,g7)
    c: Vertical(g14)
    c: Coincident(g15,g11)
    c: Coincident(g15,g7)
    c: Vertical(g15)
    c: Coincident(g16,g0)
    c: Coincident(g16,g3)
    c: Vertical(g16)
    c: Coincident(g17,g4)
    c: Coincident(g17,g8)
    c: Vertical(g17)
    c: Coincident(g18,g0)
    c: Coincident(g18,g3)
    c: Vertical(g18)
    c: Coincident(g19,g4)
    c: Coincident(g19,g8)
    c: Vertical(g19)
    c: Coincident(g20,g5)
    c: Coincident(g20,g9)
    c: Vertical(g20)
    c: Coincident(g21,g5)
    c: Coincident(g21,g9)
    c: Vertical(g21)
    c: Coincident(g22,g10)
    c: Coincident(g22,g6)
    c: Vertical(g22)
    c: Coincident(g23,g6)
    c: Coincident(g23,g10)
    c: Vertical(g23)
FEATURE [Part::Extrusion] Extrude020  label="removeToCreateFanGrillHoles"
  Base = -> Sketch029
  Dir = (0,-1,6e-16)
  DirMode = 2
  FaceMakerClass = Part::FaceMakerBullseye
  LengthFwd = 10
  LengthRev = 0
  Placement = pos=(65.4,44,54.82) rot=(0,0,1;0rad)
  Solid = true
  Symmetric = false
FEATURE [Part::MultiFuse] Fusion055  label="top008"
  Shapes = -> [Cut017,Cut018]
FEATURE [Part::Cut] Cut019  label="top009"
  Base = -> Fusion055
  Tool = -> Extrude020
FEATURE [App::MeasureDistance] Distance003  label="Distance: 71.95 mm"
  Distance = 71.9513
  P1 = (117,38,72)
  P2 = (117,38,0.0487319)
FEATURE [Sketcher::SketchObject] Sketch030
  FullyConstrained = true
  Placement = pos=(117,19,0) rot=(0.57735,0.57735,0.57735;2.0944rad)
  sketch-geometry (48):
    g0: LineSegment StartX=-49.19 StartY=69.25 StartZ=0 EndX=-49.19 EndY=66.25 EndZ=0
    g1: LineSegment StartX=-49.19 StartY=63.5 StartZ=0 EndX=-49.19 EndY=60.5 EndZ=0
    g2: LineSegment StartX=-49.19 StartY=57.75 StartZ=0 EndX=-49.19 EndY=54.75 EndZ=0
    g3: LineSegment StartX=-49.19 StartY=52 StartZ=0 EndX=-49.19 EndY=49 EndZ=0
    g4: LineSegment StartX=-49.19 StartY=46.25 StartZ=0 EndX=-49.19 EndY=43.25 EndZ=0
    g5: LineSegment StartX=-49.19 StartY=40.5 StartZ=0 EndX=-49.19 EndY=37.5 EndZ=0
    g6: LineSegment StartX=-49.19 StartY=34.5 StartZ=0 EndX=-49.19 EndY=31.5 EndZ=0
    g7: LineSegment StartX=-49.19 StartY=28.75 StartZ=0 EndX=-49.19 EndY=25.75 EndZ=0
    g8: LineSegment StartX=-49.19 StartY=23 StartZ=0 EndX=-49.19 EndY=20 EndZ=0
    g9: LineSegment StartX=-49.19 StartY=17.25 StartZ=0 EndX=-49.19 EndY=14.25 EndZ=0
    g10: LineSegment StartX=-49.19 StartY=11.5 StartZ=0 EndX=-49.19 EndY=8.5 EndZ=0
    g11: LineSegment StartX=-49.19 StartY=5.75 StartZ=0 EndX=-49.19 EndY=2.75 EndZ=0
    g12: ArcOfCircle CenterX=-1.5 CenterY=67.75 CenterZ=0 NormalX=0 NormalY=0 NormalZ=1 AngleXU=0 Radius=1.5 StartAngle=4.71239 EndAngle=7.85398
    g13: ArcOfCircle CenterX=-1.5 CenterY=62 CenterZ=0 NormalX=0 NormalY=0 NormalZ=1 AngleXU=0 Radius=1.5 StartAngle=4.71239 EndAngle=7.85398
    g14: ArcOfCircle CenterX=-1.5 CenterY=56.25 CenterZ=0 NormalX=0 NormalY=0 NormalZ=1 AngleXU=0 Radius=1.5 StartAngle=4.71239 EndAngle=7.85398
    g15: ArcOfCircle CenterX=-11.49 CenterY=50.5 CenterZ=0 NormalX=0 NormalY=0 NormalZ=1 AngleXU=0 Radius=1.5 StartAngle=4.71239 EndAngle=7.85398
    g16: ArcOfCircle CenterX=-16.28 CenterY=44.75 CenterZ=0 NormalX=0 NormalY=0 NormalZ=1 AngleXU=0 Radius=1.5 StartAngle=4.71239 EndAngle=7.85398
    g17: ArcOfCircle CenterX=-18.2337 CenterY=39 CenterZ=0 NormalX=0 NormalY=0 NormalZ=1 AngleXU=0 Radius=1.5 StartAngle=4.71485 EndAngle=7.85398
    g18: ArcOfCircle CenterX=-16.2837 CenterY=27.25 CenterZ=0 NormalX=0 NormalY=0 NormalZ=1 AngleXU=0 Radius=1.5 StartAngle=4.71485 EndAngle=7.85398
    g19: ArcOfCircle CenterX=-18.2337 CenterY=33 CenterZ=0 NormalX=0 NormalY=0 NormalZ=1 AngleXU=0 Radius=1.5 StartAngle=4.71485 EndAngle=7.85398
    g20: ArcOfCircle CenterX=-11.49 CenterY=21.5 CenterZ=0 NormalX=0 NormalY=0 NormalZ=1 AngleXU=0 Radius=1.5 StartAngle=4.71239 EndAngle=7.85398
    g21: ArcOfCircle CenterX=-1.5 CenterY=4.25 CenterZ=0 NormalX=0 NormalY=0 NormalZ=1 AngleXU=0 Radius=1.5 StartAngle=4.71239 EndAngle=7.85398
    g22: ArcOfCircle CenterX=-1.5 CenterY=10 CenterZ=0 NormalX=0 NormalY=0 NormalZ=1 AngleXU=0 Radius=1.5 StartAngle=4.71239 EndAngle=7.85398
    g23: ArcOfCircle CenterX=-1.5 CenterY=15.75 CenterZ=0 NormalX=0 NormalY=0 NormalZ=1 AngleXU=0 Radius=1.5 StartAngle=4.71239 EndAngle=7.85398
    g24: LineSegment StartX=-49.19 StartY=69.25 StartZ=0 EndX=-1.5 EndY=69.25 EndZ=0
    g25: LineSegment StartX=-49.19 StartY=66.25 StartZ=0 EndX=-1.5 EndY=66.25 EndZ=0
    g26: LineSegment StartX=-49.19 StartY=63.5 StartZ=0 EndX=-1.5 EndY=63.5 EndZ=0
    g27: LineSegment StartX=-49.19 StartY=60.5 StartZ=0 EndX=-1.5 EndY=60.5 EndZ=0
    g28: LineSegment StartX=-49.19 StartY=57.75 StartZ=0 EndX=-1.5 EndY=57.75 EndZ=0
    g29: LineSegment StartX=-49.19 StartY=54.75 StartZ=0 EndX=-1.5 EndY=54.75 EndZ=0
    g30: LineSegment StartX=-49.19 StartY=52 StartZ=0 EndX=-11.49 EndY=52 EndZ=0
    g31: LineSegment StartX=-49.19 StartY=49 StartZ=0 EndX=-11.49 EndY=49 EndZ=0
    g32: LineSegment StartX=-49.19 StartY=46.25 StartZ=0 EndX=-16.28 EndY=46.25 EndZ=0
    g33: LineSegment StartX=-49.19 StartY=43.25 StartZ=0 EndX=-16.28 EndY=43.25 EndZ=0
    g34: LineSegment StartX=-49.19 StartY=40.5 StartZ=0 EndX=-18.2337 EndY=40.5 EndZ=0
    g35: LineSegment StartX=-49.19 StartY=37.5 StartZ=0 EndX=-18.23 EndY=37.5 EndZ=0
    g36: LineSegment StartX=-49.19 StartY=34.5 StartZ=0 EndX=-18.2337 EndY=34.5 EndZ=0
    g37: LineSegment StartX=-49.19 StartY=31.5 StartZ=0 EndX=-18.23 EndY=31.5 EndZ=0
    g38: LineSegment StartX=-49.19 StartY=28.75 StartZ=0 EndX=-16.2837 EndY=28.75 EndZ=0
    g39: LineSegment StartX=-49.19 StartY=25.75 StartZ=0 EndX=-16.28 EndY=25.75 EndZ=0
    g40: LineSegment StartX=-49.19 StartY=23 StartZ=0 EndX=-11.49 EndY=23 EndZ=0
    g41: LineSegment StartX=-49.19 StartY=20 StartZ=0 EndX=-11.49 EndY=20 EndZ=0
    g42: LineSegment StartX=-49.19 StartY=17.25 StartZ=0 EndX=-1.5 EndY=17.25 EndZ=0
    g43: LineSegment StartX=-49.19 StartY=14.25 StartZ=0 EndX=-1.5 EndY=14.25 EndZ=0
    g44: LineSegment StartX=-49.19 StartY=11.5 StartZ=0 EndX=-1.5 EndY=11.5 EndZ=0
    g45: LineSegment StartX=-49.19 StartY=8.5 StartZ=0 EndX=-1.5 EndY=8.5 EndZ=0
    g46: LineSegment StartX=-49.19 StartY=5.75 StartZ=0 EndX=-1.5 EndY=5.75 EndZ=0
    g47: LineSegment StartX=-49.19 StartY=2.75 StartZ=0 EndX=-1.5 EndY=2.75 EndZ=0
  constraints (120):
    c: Vertical(g0)
    c: Distance(g0) = 3
    c: Block(g0)
    c: Vertical(g1)
    c: Distance(g1) = 3
    c: Vertical(g2)
    c: Equal(g0,g2) = 3
    c: Block(g2)
    c: Vertical(g3)
    c: Equal(g1,g3) = 3
    c: Vertical(g4)
    c: Equal(g0,g4) = 3
    c: Block(g4)
    c: Vertical(g5)
    c: Equal(g1,g5) = 3
    c: Vertical(g6)
    c: Equal(g0,g6) = 3
    c: Block(g6)
    c: Vertical(g7)
    c: Equal(g1,g7) = 3
    c: Vertical(g8)
    c: Equal(g0,g8) = 3
    c: Block(g8)
    c: Vertical(g9)
    c: Equal(g1,g9) = 3
    c: Vertical(g10)
    c: Equal(g0,g10) = 3
    c: Block(g10)
    c: Vertical(g11)
    c: Equal(g1,g11) = 3
    c: Block(g12)
    c: Block(g13)
    c: Block(g14)
    c: Block(g15)
    c: Block(g16)
    c: Block(g17)
    c: Block(g18)
    c: Block(g19)
    c: Block(g20)
    c: Block(g21)
    c: Block(g22)
    c: Block(g23)
    c: Block(g11)
    c: Block(g9)
    c: Block(g7)
    c: Block(g5)
    c: Block(g3)
    c: Block(g1)
    c: Coincident(g24,g0)
    c: Coincident(g24,g12)
    c: Horizontal(g24)
    c: Coincident(g25,g0)
    c: Coincident(g25,g12)
    c: Horizontal(g25)
    c: Coincident(g26,g1)
    c: Coincident(g26,g13)
    c: Horizontal(g26)
    c: Coincident(g27,g1)
    c: Coincident(g27,g13)
    c: Horizontal(g27)
    c: Coincident(g28,g2)
    c: Coincident(g28,g14)
    c: Horizontal(g28)
    c: Coincident(g29,g2)
    c: Coincident(g29,g14)
    c: Horizontal(g29)
    c: Coincident(g30,g3)
    c: Coincident(g30,g15)
    c: Horizontal(g30)
    c: Coincident(g31,g3)
    c: Coincident(g31,g15)
    c: Horizontal(g31)
    c: Coincident(g32,g4)
    c: Coincident(g32,g16)
    c: Horizontal(g32)
    c: Coincident(g33,g4)
    c: Coincident(g33,g16)
    c: Horizontal(g33)
    c: Coincident(g34,g5)
    c: Coincident(g34,g17)
    c: Horizontal(g34)
    c: Coincident(g35,g5)
    c: Coincident(g35,g17)
    c: Horizontal(g35)
    c: Coincident(g36,g6)
    c: Coincident(g36,g19)
    c: Horizontal(g36)
    c: Coincident(g37,g6)
    c: Coincident(g37,g19)
    c: Horizontal(g37)
    c: Coincident(g38,g7)
    c: Coincident(g38,g18)
    c: Horizontal(g38)
    c: Coincident(g39,g7)
    c: Coincident(g39,g18)
    c: Horizontal(g39)
    c: Coincident(g40,g8)
    c: Coincident(g40,g20)
    c: Horizontal(g40)
    c: Coincident(g41,g8)
    c: Coincident(g41,g20)
    c: Horizontal(g41)
    c: Coincident(g42,g9)
    c: Coincident(g42,g23)
    c: Horizontal(g42)
    c: Coincident(g43,g9)
    c: Coincident(g43,g23)
    c: Horizontal(g43)
    c: Coincident(g44,g10)
    c: Coincident(g44,g22)
    c: Horizontal(g44)
    c: Coincident(g45,g10)
    c: Coincident(g45,g22)
    c: Horizontal(g45)
    c: Coincident(g46,g11)
    c: Coincident(g46,g21)
    c: Horizontal(g46)
    c: Coincident(g47,g11)
    c: Coincident(g47,g21)
    c: Horizontal(g47)
FEATURE [Sketcher::SketchObject] Sketch031
  FullyConstrained = true
  Placement = pos=(117,19,0) rot=(0.57735,0.57735,0.57735;2.0944rad)
  sketch-geometry (24):
    g0: ArcOfCircle CenterX=-49.19 CenterY=67.75 CenterZ=0 NormalX=0 NormalY=0 NormalZ=1 AngleXU=0 Radius=1.5 StartAngle=1.5708 EndAngle=4.71239
    g1: ArcOfCircle CenterX=-49.19 CenterY=62 CenterZ=0 NormalX=0 NormalY=0 NormalZ=1 AngleXU=0 Radius=1.5 StartAngle=1.5708 EndAngle=4.71239
    g2: ArcOfCircle CenterX=-49.19 CenterY=56.25 CenterZ=0 NormalX=0 NormalY=0 NormalZ=1 AngleXU=0 Radius=1.5 StartAngle=1.5708 EndAngle=4.71239
    g3: ArcOfCircle CenterX=-49.19 CenterY=50.5 CenterZ=0 NormalX=0 NormalY=0 NormalZ=1 AngleXU=0 Radius=1.5 StartAngle=1.5708 EndAngle=4.71239
    g4: ArcOfCircle CenterX=-49.19 CenterY=44.75 CenterZ=0 NormalX=0 NormalY=0 NormalZ=1 AngleXU=0 Radius=1.5 StartAngle=1.5708 EndAngle=4.71239
    g5: ArcOfCircle CenterX=-49.19 CenterY=39 CenterZ=0 NormalX=0 NormalY=0 NormalZ=1 AngleXU=0 Radius=1.5 StartAngle=1.5708 EndAngle=4.71239
    g6: ArcOfCircle CenterX=-49.19 CenterY=33 CenterZ=0 NormalX=0 NormalY=0 NormalZ=1 AngleXU=0 Radius=1.5 StartAngle=1.5708 EndAngle=4.71239
    g7: ArcOfCircle CenterX=-49.19 CenterY=27.25 CenterZ=0 NormalX=0 NormalY=0 NormalZ=1 AngleXU=0 Radius=1.5 StartAngle=1.5708 EndAngle=4.71239
    g8: ArcOfCircle CenterX=-49.19 CenterY=21.5 CenterZ=0 NormalX=0 NormalY=0 NormalZ=1 AngleXU=0 Radius=1.5 StartAngle=1.5708 EndAngle=4.71239
    g9: ArcOfCircle CenterX=-49.19 CenterY=15.75 CenterZ=0 NormalX=0 NormalY=0 NormalZ=1 AngleXU=0 Radius=1.5 StartAngle=1.5708 EndAngle=4.71239
    g10: ArcOfCircle CenterX=-49.19 CenterY=10 CenterZ=0 NormalX=0 NormalY=0 NormalZ=1 AngleXU=0 Radius=1.5 StartAngle=1.5708 EndAngle=4.71239
    g11: ArcOfCircle CenterX=-49.19 CenterY=4.25 CenterZ=0 NormalX=0 NormalY=0 NormalZ=1 AngleXU=0 Radius=1.5 StartAngle=1.5708 EndAngle=4.71239
    g12: LineSegment StartX=-49.19 StartY=69.25 StartZ=0 EndX=-49.19 EndY=66.25 EndZ=0
    g13: LineSegment StartX=-49.19 StartY=63.5 StartZ=0 EndX=-49.19 EndY=60.5 EndZ=0
    g14: LineSegment StartX=-49.19 StartY=57.75 StartZ=0 EndX=-49.19 EndY=54.75 EndZ=0
    g15: LineSegment StartX=-49.19 StartY=52 StartZ=0 EndX=-49.19 EndY=49 EndZ=0
    g16: LineSegment StartX=-49.19 StartY=46.25 StartZ=0 EndX=-49.19 EndY=43.25 EndZ=0
    g17: LineSegment StartX=-49.19 StartY=40.5 StartZ=0 EndX=-49.19 EndY=37.5 EndZ=0
    g18: LineSegment StartX=-49.19 StartY=34.5 StartZ=0 EndX=-49.19 EndY=31.5 EndZ=0
    g19: LineSegment StartX=-49.19 StartY=28.75 StartZ=0 EndX=-49.19 EndY=25.75 EndZ=0
    g20: LineSegment StartX=-49.19 StartY=23 StartZ=0 EndX=-49.19 EndY=20 EndZ=0
    g21: LineSegment StartX=-49.19 StartY=17.25 StartZ=0 EndX=-49.19 EndY=14.25 EndZ=0
    g22: LineSegment StartX=-49.19 StartY=11.5 StartZ=0 EndX=-49.19 EndY=8.5 EndZ=0
    g23: LineSegment StartX=-49.19 StartY=5.75 StartZ=0 EndX=-49.19 EndY=2.75 EndZ=0
  constraints (48):
    c: Block(g0)
    c: Block(g1)
    c: Block(g2)
    c: Block(g3)
    c: Block(g4)
    c: Block(g5)
    c: Block(g6)
    c: Block(g7)
    c: Block(g8)
    c: Block(g9)
    c: Block(g10)
    c: Block(g11)
    c: Coincident(g12,g0)
    c: Coincident(g12,g0)
    c: Vertical(g12)
    c: Vertical(g13)
    c: Coincident(g13,g1)
    c: Vertical(g14)
    c: Coincident(g14,g2)
    c: Vertical(g15)
    c: Coincident(g15,g3)
    c: Vertical(g16)
    c: Coincident(g16,g4)
    c: Vertical(g17)
    c: Coincident(g17,g5)
    c: Vertical(g18)
    c: Coincident(g18,g6)
    c: Vertical(g19)
    c: Coincident(g19,g7)
    c: Vertical(g20)
    c: Coincident(g20,g8)
    c: Vertical(g21)
    c: Coincident(g21,g9)
    c: Vertical(g22)
    c: Coincident(g22,g10)
    c: Vertical(g23)
    c: Coincident(g23,g11)
    c: Block(g23)
    c: Block(g22)
    c: Block(g21)
    c: Block(g20)
    c: Block(g13)
    c: Block(g14)
    c: Block(g15)
    c: Block(g16)
    c: Block(g17)
    c: Block(g18)
    c: Block(g19)
FEATURE [Part::Extrusion] Extrude022
  Base = -> Sketch030
  Dir = (1,-2e-16,2e-16)
  DirMode = 2
  FaceMakerClass = Part::FaceMakerBullseye
  LengthFwd = 19
  LengthRev = 0
  Placement = pos=(-19,0,0) rot=(0,0,1;0rad)
  Solid = true
  Symmetric = false
FEATURE [Part::Fillet] Fillet022
  Base = -> Extrude022
  Edges = 24 edges r=1.49: [Edge6,Edge11,Edge18,Edge23,Edge30,Edge35,Edge42,Edge47,Edge54,Edge59,Edge66,Edge71,Edge78,Edge83,Edge90,Edge95,Edge102,Edge107,Edge114,Edge119,Edge126,Edge131,Edge138,Edge143]
FEATURE [Part::Cut] Cut020  label="top010"
  Base = -> Cut019
  Tool = -> Fillet022
FEATURE [Sketcher::SketchObject] Sketch032
  FullyConstrained = true
  Placement = pos=(117,19,0) rot=(0.57735,0.57735,0.57735;2.0944rad)
  sketch-geometry (48):
    g0: LineSegment StartX=-49.19 StartY=69.25 StartZ=0 EndX=-49.19 EndY=66.25 EndZ=0
    g1: LineSegment StartX=-49.19 StartY=63.5 StartZ=0 EndX=-49.19 EndY=60.5 EndZ=0
    g2: LineSegment StartX=-49.19 StartY=57.75 StartZ=0 EndX=-49.19 EndY=54.75 EndZ=0
    g3: LineSegment StartX=-49.19 StartY=52 StartZ=0 EndX=-49.19 EndY=49 EndZ=0
    g4: LineSegment StartX=-49.19 StartY=46.25 StartZ=0 EndX=-49.19 EndY=43.25 EndZ=0
    g5: LineSegment StartX=-49.19 StartY=40.5 StartZ=0 EndX=-49.19 EndY=37.5 EndZ=0
    g6: LineSegment StartX=-49.19 StartY=34.5 StartZ=0 EndX=-49.19 EndY=31.5 EndZ=0
    g7: LineSegment StartX=-49.19 StartY=28.75 StartZ=0 EndX=-49.19 EndY=25.75 EndZ=0
    g8: LineSegment StartX=-49.19 StartY=23 StartZ=0 EndX=-49.19 EndY=20 EndZ=0
    g9: LineSegment StartX=-49.19 StartY=17.25 StartZ=0 EndX=-49.19 EndY=14.25 EndZ=0
    g10: LineSegment StartX=-49.19 StartY=11.5 StartZ=0 EndX=-49.19 EndY=8.5 EndZ=0
    g11: LineSegment StartX=-49.19 StartY=5.75 StartZ=0 EndX=-49.19 EndY=2.75 EndZ=0
    g12: ArcOfCircle CenterX=-1.5 CenterY=67.75 CenterZ=0 NormalX=0 NormalY=0 NormalZ=1 AngleXU=0 Radius=1.5 StartAngle=4.71239 EndAngle=7.85398
    g13: ArcOfCircle CenterX=-1.5 CenterY=62 CenterZ=0 NormalX=0 NormalY=0 NormalZ=1 AngleXU=0 Radius=1.5 StartAngle=4.71239 EndAngle=7.85398
    g14: ArcOfCircle CenterX=-1.5 CenterY=56.25 CenterZ=0 NormalX=0 NormalY=0 NormalZ=1 AngleXU=0 Radius=1.5 StartAngle=4.71239 EndAngle=7.85398
    g15: ArcOfCircle CenterX=-11.49 CenterY=50.5 CenterZ=0 NormalX=0 NormalY=0 NormalZ=1 AngleXU=0 Radius=1.5 StartAngle=4.71239 EndAngle=7.85398
    g16: ArcOfCircle CenterX=-16.28 CenterY=44.75 CenterZ=0 NormalX=0 NormalY=0 NormalZ=1 AngleXU=0 Radius=1.5 StartAngle=4.71239 EndAngle=7.85398
    g17: ArcOfCircle CenterX=-18.2337 CenterY=39 CenterZ=0 NormalX=0 NormalY=0 NormalZ=1 AngleXU=0 Radius=1.5 StartAngle=4.71485 EndAngle=7.85398
    g18: ArcOfCircle CenterX=-16.2837 CenterY=27.25 CenterZ=0 NormalX=0 NormalY=0 NormalZ=1 AngleXU=0 Radius=1.5 StartAngle=4.71485 EndAngle=7.85398
    g19: ArcOfCircle CenterX=-18.2337 CenterY=33 CenterZ=0 NormalX=0 NormalY=0 NormalZ=1 AngleXU=0 Radius=1.5 StartAngle=4.71485 EndAngle=7.85398
    g20: ArcOfCircle CenterX=-11.49 CenterY=21.5 CenterZ=0 NormalX=0 NormalY=0 NormalZ=1 AngleXU=0 Radius=1.5 StartAngle=4.71239 EndAngle=7.85398
    g21: ArcOfCircle CenterX=-1.5 CenterY=4.25 CenterZ=0 NormalX=0 NormalY=0 NormalZ=1 AngleXU=0 Radius=1.5 StartAngle=4.71239 EndAngle=7.85398
    g22: ArcOfCircle CenterX=-1.5 CenterY=10 CenterZ=0 NormalX=0 NormalY=0 NormalZ=1 AngleXU=0 Radius=1.5 StartAngle=4.71239 EndAngle=7.85398
    g23: ArcOfCircle CenterX=-1.5 CenterY=15.75 CenterZ=0 NormalX=0 NormalY=0 NormalZ=1 AngleXU=0 Radius=1.5 StartAngle=4.71239 EndAngle=7.85398
    g24: LineSegment StartX=-49.19 StartY=69.25 StartZ=0 EndX=-1.5 EndY=69.25 EndZ=0
    g25: LineSegment StartX=-49.19 StartY=66.25 StartZ=0 EndX=-1.5 EndY=66.25 EndZ=0
    g26: LineSegment StartX=-49.19 StartY=63.5 StartZ=0 EndX=-1.5 EndY=63.5 EndZ=0
    g27: LineSegment StartX=-49.19 StartY=60.5 StartZ=0 EndX=-1.5 EndY=60.5 EndZ=0
    g28: LineSegment StartX=-49.19 StartY=57.75 StartZ=0 EndX=-1.5 EndY=57.75 EndZ=0
    g29: LineSegment StartX=-49.19 StartY=54.75 StartZ=0 EndX=-1.5 EndY=54.75 EndZ=0
    g30: LineSegment StartX=-49.19 StartY=52 StartZ=0 EndX=-11.49 EndY=52 EndZ=0
    g31: LineSegment StartX=-49.19 StartY=49 StartZ=0 EndX=-11.49 EndY=49 EndZ=0
    g32: LineSegment StartX=-49.19 StartY=46.25 StartZ=0 EndX=-16.28 EndY=46.25 EndZ=0
    g33: LineSegment StartX=-49.19 StartY=43.25 StartZ=0 EndX=-16.28 EndY=43.25 EndZ=0
    g34: LineSegment StartX=-49.19 StartY=40.5 StartZ=0 EndX=-18.2337 EndY=40.5 EndZ=0
    g35: LineSegment StartX=-49.19 StartY=37.5 StartZ=0 EndX=-18.23 EndY=37.5 EndZ=0
    g36: LineSegment StartX=-49.19 StartY=34.5 StartZ=0 EndX=-18.2337 EndY=34.5 EndZ=0
    g37: LineSegment StartX=-49.19 StartY=31.5 StartZ=0 EndX=-18.23 EndY=31.5 EndZ=0
    g38: LineSegment StartX=-49.19 StartY=28.75 StartZ=0 EndX=-16.2837 EndY=28.75 EndZ=0
    g39: LineSegment StartX=-49.19 StartY=25.75 StartZ=0 EndX=-16.28 EndY=25.75 EndZ=0
    g40: LineSegment StartX=-49.19 StartY=23 StartZ=0 EndX=-11.49 EndY=23 EndZ=0
    g41: LineSegment StartX=-49.19 StartY=20 StartZ=0 EndX=-11.49 EndY=20 EndZ=0
    g42: LineSegment StartX=-49.19 StartY=17.25 StartZ=0 EndX=-1.5 EndY=17.25 EndZ=0
    g43: LineSegment StartX=-49.19 StartY=14.25 StartZ=0 EndX=-1.5 EndY=14.25 EndZ=0
    g44: LineSegment StartX=-49.19 StartY=11.5 StartZ=0 EndX=-1.5 EndY=11.5 EndZ=0
    g45: LineSegment StartX=-49.19 StartY=8.5 StartZ=0 EndX=-1.5 EndY=8.5 EndZ=0
    g46: LineSegment StartX=-49.19 StartY=5.75 StartZ=0 EndX=-1.5 EndY=5.75 EndZ=0
    g47: LineSegment StartX=-49.19 StartY=2.75 StartZ=0 EndX=-1.5 EndY=2.75 EndZ=0
  constraints (120):
    c: Vertical(g0)
    c: Distance(g0) = 3
    c: Block(g0)
    c: Vertical(g1)
    c: Distance(g1) = 3
    c: Vertical(g2)
    c: Equal(g0,g2) = 3
    c: Block(g2)
    c: Vertical(g3)
    c: Equal(g1,g3) = 3
    c: Vertical(g4)
    c: Equal(g0,g4) = 3
    c: Block(g4)
    c: Vertical(g5)
    c: Equal(g1,g5) = 3
    c: Vertical(g6)
    c: Equal(g0,g6) = 3
    c: Block(g6)
    c: Vertical(g7)
    c: Equal(g1,g7) = 3
    c: Vertical(g8)
    c: Equal(g0,g8) = 3
    c: Block(g8)
    c: Vertical(g9)
    c: Equal(g1,g9) = 3
    c: Vertical(g10)
    c: Equal(g0,g10) = 3
    c: Block(g10)
    c: Vertical(g11)
    c: Equal(g1,g11) = 3
    c: Block(g12)
    c: Block(g13)
    c: Block(g14)
    c: Block(g15)
    c: Block(g16)
    c: Block(g17)
    c: Block(g18)
    c: Block(g19)
    c: Block(g20)
    c: Block(g21)
    c: Block(g22)
    c: Block(g23)
    c: Block(g11)
    c: Block(g9)
    c: Block(g7)
    c: Block(g5)
    c: Block(g3)
    c: Block(g1)
    c: Coincident(g24,g0)
    c: Coincident(g24,g12)
    c: Horizontal(g24)
    c: Coincident(g25,g0)
    c: Coincident(g25,g12)
    c: Horizontal(g25)
    c: Coincident(g26,g1)
    c: Coincident(g26,g13)
    c: Horizontal(g26)
    c: Coincident(g27,g1)
    c: Coincident(g27,g13)
    c: Horizontal(g27)
    c: Coincident(g28,g2)
    c: Coincident(g28,g14)
    c: Horizontal(g28)
    c: Coincident(g29,g2)
    c: Coincident(g29,g14)
    c: Horizontal(g29)
    c: Coincident(g30,g3)
    c: Coincident(g30,g15)
    c: Horizontal(g30)
    c: Coincident(g31,g3)
    c: Coincident(g31,g15)
    c: Horizontal(g31)
    c: Coincident(g32,g4)
    c: Coincident(g32,g16)
    c: Horizontal(g32)
    c: Coincident(g33,g4)
    c: Coincident(g33,g16)
    c: Horizontal(g33)
    c: Coincident(g34,g5)
    c: Coincident(g34,g17)
    c: Horizontal(g34)
    c: Coincident(g35,g5)
    c: Coincident(g35,g17)
    c: Horizontal(g35)
    c: Coincident(g36,g6)
    c: Coincident(g36,g19)
    c: Horizontal(g36)
    c: Coincident(g37,g6)
    c: Coincident(g37,g19)
    c: Horizontal(g37)
    c: Coincident(g38,g7)
    c: Coincident(g38,g18)
    c: Horizontal(g38)
    c: Coincident(g39,g7)
    c: Coincident(g39,g18)
    c: Horizontal(g39)
    c: Coincident(g40,g8)
    c: Coincident(g40,g20)
    c: Horizontal(g40)
    c: Coincident(g41,g8)
    c: Coincident(g41,g20)
    c: Horizontal(g41)
    c: Coincident(g42,g9)
    c: Coincident(g42,g23)
    c: Horizontal(g42)
    c: Coincident(g43,g9)
    c: Coincident(g43,g23)
    c: Horizontal(g43)
    c: Coincident(g44,g10)
    c: Coincident(g44,g22)
    c: Horizontal(g44)
    c: Coincident(g45,g10)
    c: Coincident(g45,g22)
    c: Horizontal(g45)
    c: Coincident(g46,g11)
    c: Coincident(g46,g21)
    c: Horizontal(g46)
    c: Coincident(g47,g11)
    c: Coincident(g47,g21)
    c: Horizontal(g47)
FEATURE [Part::Extrusion] Extrude023
  Base = -> Sketch032
  Dir = (1,-2e-16,2e-16)
  DirMode = 2
  FaceMakerClass = Part::FaceMakerBullseye
  LengthFwd = 19
  LengthRev = 0
  Placement = pos=(-19,0,0) rot=(0,0,1;0rad)
  Solid = true
  Symmetric = false
FEATURE [Part::Fillet] Fillet023
  Base = -> Extrude023
  Edges = <same value as first occurrence — deduplicated (x6 in doc)>
  Placement = pos=(0,0.05,0) rot=(0,0,1;0rad)
FEATURE [Part::Cut] Cut014  label="bottom003"
  Base = -> Cut007
  Tool = -> Fusion047
FEATURE [Part::Cut] Cut021  label="bottom004"
  Base = -> Cut014
  Tool = -> Fillet023
FEATURE [Sketcher::SketchObject] Sketch033
  FullyConstrained = true
  Placement = pos=(117,19,0) rot=(0.57735,0.57735,0.57735;2.0944rad)
  sketch-geometry (8):
    g0: LineSegment StartX=-49.19 StartY=69.25 StartZ=0 EndX=-49.19 EndY=66.25 EndZ=0
    g1: LineSegment StartX=-49.19 StartY=5.75 StartZ=0 EndX=-49.19 EndY=2.75 EndZ=0
    g2: ArcOfCircle CenterX=-1.5 CenterY=67.75 CenterZ=0 NormalX=0 NormalY=0 NormalZ=1 AngleXU=0 Radius=1.5 StartAngle=4.71239 EndAngle=7.85398
    g3: ArcOfCircle CenterX=-1.5 CenterY=4.25 CenterZ=0 NormalX=0 NormalY=0 NormalZ=1 AngleXU=0 Radius=1.5 StartAngle=4.71239 EndAngle=7.85398
    g4: LineSegment StartX=-49.19 StartY=69.25 StartZ=0 EndX=-1.5 EndY=69.25 EndZ=0
    g5: LineSegment StartX=-49.19 StartY=66.25 StartZ=0 EndX=-1.5 EndY=66.25 EndZ=0
    g6: LineSegment StartX=-49.19 StartY=5.75 StartZ=0 EndX=-1.5 EndY=5.75 EndZ=0
    g7: LineSegment StartX=-49.19 StartY=2.75 StartZ=0 EndX=-1.5 EndY=2.75 EndZ=0
  constraints (19):
    c: Vertical(g0)
    c: Distance(g0) = 3
    c: Block(g0)
    c: Vertical(g1)
    c: Block(g2)
    c: Block(g3)
    c: Block(g1)
    c: Coincident(g4,g0)
    c: Coincident(g4,g2)
    c: Horizontal(g4)
    c: Coincident(g5,g0)
    c: Coincident(g5,g2)
    c: Horizontal(g5)
    c: Coincident(g6,g1)
    c: Coincident(g6,g3)
    c: Horizontal(g6)
    c: Coincident(g7,g1)
    c: Coincident(g7,g3)
    c: Horizontal(g7)
FEATURE [Sketcher::SketchObject] Sketch034
  FullyConstrained = true
  Placement = pos=(117,19,0) rot=(0.57735,0.57735,0.57735;2.0944rad)
  sketch-geometry (8):
    g0: LineSegment StartX=-49.19 StartY=63.5 StartZ=0 EndX=-49.19 EndY=60.5 EndZ=0
    g1: LineSegment StartX=-49.19 StartY=11.5 StartZ=0 EndX=-49.19 EndY=8.5 EndZ=0
    g2: ArcOfCircle CenterX=-1.5 CenterY=62 CenterZ=0 NormalX=0 NormalY=0 NormalZ=1 AngleXU=0 Radius=1.5 StartAngle=4.71239 EndAngle=7.85398
    g3: ArcOfCircle CenterX=-1.5 CenterY=10 CenterZ=0 NormalX=0 NormalY=0 NormalZ=1 AngleXU=0 Radius=1.5 StartAngle=4.71239 EndAngle=7.85398
    g4: LineSegment StartX=-49.19 StartY=63.5 StartZ=0 EndX=-1.5 EndY=63.5 EndZ=0
    g5: LineSegment StartX=-49.19 StartY=60.5 StartZ=0 EndX=-1.5 EndY=60.5 EndZ=0
    g6: LineSegment StartX=-49.19 StartY=11.5 StartZ=0 EndX=-1.5 EndY=11.5 EndZ=0
    g7: LineSegment StartX=-49.19 StartY=8.5 StartZ=0 EndX=-1.5 EndY=8.5 EndZ=0
  constraints (19):
    c: Vertical(g0)
    c: Distance(g0) = 3
    c: Vertical(g1)
    c: Block(g1)
    c: Block(g2)
    c: Block(g3)
    c: Block(g0)
    c: Coincident(g4,g0)
    c: Coincident(g4,g2)
    c: Horizontal(g4)
    c: Coincident(g5,g0)
    c: Coincident(g5,g2)
    c: Horizontal(g5)
    c: Coincident(g6,g1)
    c: Coincident(g6,g3)
    c: Horizontal(g6)
    c: Coincident(g7,g1)
    c: Coincident(g7,g3)
    c: Horizontal(g7)
FEATURE [Part::Extrusion] Extrude024
  Base = -> Sketch033
  Dir = (1,0,0)
  DirMode = 2
  FaceMakerClass = Part::FaceMakerBullseye
  LengthFwd = 10
  LengthRev = 0
  Solid = true
  Symmetric = false
FEATURE [Part::Extrusion] Extrude025
  Base = -> Sketch034
  Dir = (1,0,0)
  DirMode = 2
  FaceMakerClass = Part::FaceMakerBullseye
  LengthFwd = 10
  LengthRev = 0
  Solid = true
  Symmetric = false
FEATURE [Part::Fillet] Fillet024  label="removeFromtMoreFrontCaseScrewRetainers"
  Base = -> Extrude024
  Edges = 4 edges r=1.49: [Edge6,Edge11,Edge18,Edge23]
  Placement = pos=(-11,0,0) rot=(0,0,1;0rad)
FEATURE [Part::Fillet] Fillet025  label="removeFromtMoreFrontCaseScrewRetainers001"
  Base = -> Extrude025
  Edges = 4 edges r=1.49: [Edge6,Edge11,Edge18,Edge23]
  Placement = pos=(-19,0,0) rot=(0,0,1;0rad)
FEATURE [Part::Cut] Cut022
  Base = -> Cut015
  Tool = -> Fillet025
FEATURE [Part::Cut] Cut023  label="screwRetainers"
  Base = -> Cut022
  Tool = -> Fillet024
FEATURE [Part::MultiFuse] Fusion056  label="bottom005"
  Shapes = -> [Fusion044,Cut021]
FEATURE [Part::MultiFuse] Fusion057  label="casePillars001"
  Shapes = -> [Cut016,Fusion052]
FEATURE [Part::MultiFuse] Fusion058  label="bottom006"
  Shapes = -> [Fusion056,Cut023]
FEATURE [Part::MultiFuse] Fusion059  label="bottom007"
  Shapes = -> [Fusion058,Fillet005]
FEATURE [Part::MultiFuse] Fusion060  label="bottom008"
  Shapes = -> [Fusion059,Fusion]
FEATURE [Part::MultiFuse] Fusion061  label="top011"
  Shapes = -> [Cut006,Cut020]
FEATURE [Part::MultiFuse] Fusion062  label="top012"
  Shapes = -> [Fusion057,Fusion061]
FEATURE [Sketcher::SketchObject] Sketch035  label="topSketch007"
  FullyConstrained = true
  sketch-geometry (6):
    g0: LineSegment StartX=19 StartY=38 StartZ=0 EndX=117 EndY=38 EndZ=0
    g1: ArcOfCircle CenterX=19 CenterY=19 CenterZ=0 NormalX=0 NormalY=0 NormalZ=1 AngleXU=0 Radius=19 StartAngle=1.5708 EndAngle=3.14159
    g2: LineSegment StartX=117 StartY=38 StartZ=0 EndX=117 EndY=19 EndZ=0
    g3: LineSegment StartX=98 StartY=1.0161e-12 StartZ=0 EndX=5.22862e-06 EndY=1.0161e-12 EndZ=0
    g4: LineSegment StartX=5.22862e-06 StartY=19 StartZ=0 EndX=5.22862e-06 EndY=1.0161e-12 EndZ=0
    g5: ArcOfCircle CenterX=98 CenterY=19 CenterZ=0 NormalX=0 NormalY=0 NormalZ=1 AngleXU=0 Radius=19 StartAngle=4.71239 EndAngle=6.28319
  constraints (16):
    c: Horizontal(g0)
    c: Distance(g0) = 98
    c: Coincident(g1,g0)
    c: Block(g1)
    c: Coincident(g2,g0)
    c: Vertical(g2)
    c: Distance(g2) = 19
    c: Horizontal(g3)
    c: Coincident(g4,g1)
    c: Vertical(g4)
    c: Coincident(g3,g4)
    c: Block(g3)
    c: Coincident(g5,g2)
    c: Coincident(g5,g3)
    c: Block(g0)
    c: Block(g5)
FEATURE [Part::Extrusion] Extrude026  label="sideA001"
  Base = -> Sketch035
  Dir = (0,0,1)
  DirMode = 2
  FaceMakerClass = Part::FaceMakerBullseye
  LengthFwd = 3
  LengthRev = 0
  Placement = pos=(0,0,-2.7) rot=(0,0,1;0rad)
  Solid = true
  Symmetric = false
FEATURE [Sketcher::SketchObject] Sketch036  label="topSketch008"
  FullyConstrained = true
  sketch-geometry (6):
    g0: LineSegment StartX=19 StartY=38 StartZ=0 EndX=117 EndY=38 EndZ=0
    g1: ArcOfCircle CenterX=19 CenterY=19 CenterZ=0 NormalX=0 NormalY=0 NormalZ=1 AngleXU=0 Radius=19 StartAngle=1.5708 EndAngle=3.14159
    g2: LineSegment StartX=117 StartY=38 StartZ=0 EndX=117 EndY=19 EndZ=0
    g3: LineSegment StartX=98 StartY=1.0161e-12 StartZ=0 EndX=5.22862e-06 EndY=1.0161e-12 EndZ=0
    g4: LineSegment StartX=5.22862e-06 StartY=19 StartZ=0 EndX=5.22862e-06 EndY=1.0161e-12 EndZ=0
    g5: ArcOfCircle CenterX=98 CenterY=19 CenterZ=0 NormalX=0 NormalY=0 NormalZ=1 AngleXU=0 Radius=19 StartAngle=4.71239 EndAngle=6.28319
  constraints (16):
    c: Horizontal(g0)
    c: Distance(g0) = 98
    c: Coincident(g1,g0)
    c: Block(g1)
    c: Coincident(g2,g0)
    c: Vertical(g2)
    c: Distance(g2) = 19
    c: Horizontal(g3)
    c: Coincident(g4,g1)
    c: Vertical(g4)
    c: Coincident(g3,g4)
    c: Block(g3)
    c: Coincident(g5,g2)
    c: Coincident(g5,g3)
    c: Block(g0)
    c: Block(g5)
FEATURE [Part::Extrusion] Extrude027  label="sideB001"
  Base = -> Sketch036
  Dir = (0,0,1)
  DirMode = 2
  FaceMakerClass = Part::FaceMakerBullseye
  LengthFwd = 3
  LengthRev = 0
  Placement = pos=(0,0,71.7) rot=(0,0,1;0rad)
  Solid = true
  Symmetric = false
FEATURE [Part::MultiFuse] Fusion064  label="removeFromBottom"
  Shapes = -> [Extrude026,Extrude027]
FEATURE [Part::Cut] Cut024  label="bottom009"
  Base = -> Fusion060
  Tool = -> Fusion064
FEATURE [Sketcher::SketchObject] Sketch037  label="topSketch009"
  FullyConstrained = true
  sketch-geometry (8):
    g0: ArcOfCircle CenterX=19 CenterY=19.1201 CenterZ=0 NormalX=0 NormalY=0 NormalZ=1 AngleXU=0 Radius=18.8799 StartAngle=1.5708 EndAngle=3.14793
    g1: LineSegment StartX=0.120501 StartY=19.0004 StartZ=0 EndX=0.120501 EndY=0.000382114 EndZ=0
    g2: LineSegment StartX=19 StartY=38 StartZ=0 EndX=124 EndY=38 EndZ=0
    g3: LineSegment StartX=0.120501 StartY=0.000382114 StartZ=0 EndX=105.121 EndY=0.000382114 EndZ=0
    g4: LineSegment StartX=124 StartY=38 StartZ=0 EndX=125.616 EndY=38 EndZ=0
    g5: LineSegment StartX=105.121 StartY=0.000382114 StartZ=0 EndX=106.736 EndY=0.000382114 EndZ=0
    g6: ArcOfCircle CenterX=106.616 CenterY=19 CenterZ=0 NormalX=0 NormalY=0 NormalZ=1 AngleXU=0 Radius=19 StartAngle=4.71873 EndAngle=6.28319
    g7: LineSegment StartX=125.616 StartY=38 StartZ=0 EndX=125.616 EndY=19 EndZ=0
  constraints (21):
    c: Block(g0)
    c: Coincident(g1,g0)
    c: Vertical(g1)
    c: Horizontal(g2)
    c: Distance(g2) = 105
    c: Coincident(g2,g0)
    c: Distance(g1) = 19
    c: Coincident(g3,g1)
    c: Horizontal(g3)
    c: Distance(g3) = 105
    c: Coincident(g4,g2)
    c: Horizontal(g4)
    c: Distance(g4) = 1.61553
    c: Horizontal(g5)
    c: Equal(g4,g5) = 1.61553
    c: Coincident(g5,g3)
    c: Block(g6)
    c: Coincident(g6,g5)
    c: Coincident(g7,g4)
    c: Coincident(g7,g6)
    c: Vertical(g7)
FEATURE [Part::Extrusion] Extrude028  label="sideB"
  Base = -> Sketch037
  Dir = (0,0,1)
  DirMode = 2
  FaceMakerClass = Part::FaceMakerBullseye
  LengthFwd = 3
  LengthRev = 0
  Placement = pos=(0,0,72) rot=(0,0,1;0rad)
  Solid = true
  Symmetric = false
FEATURE [Sketcher::SketchObject] Sketch038  label="topSketch010"
  FullyConstrained = true
  sketch-geometry (22):
    g0: LineSegment StartX=5.21097e-06 StartY=3 StartZ=0 EndX=5.21097e-06 EndY=19 EndZ=0
    g1: ArcOfCircle CenterX=19 CenterY=19 CenterZ=0 NormalX=0 NormalY=0 NormalZ=1 AngleXU=0 Radius=19 StartAngle=1.5708 EndAngle=3.14159
    g2: ArcOfCircle CenterX=19 CenterY=19 CenterZ=0 NormalX=0 NormalY=0 NormalZ=1 AngleXU=0 Radius=16 StartAngle=1.5708 EndAngle=3.14159
    g3: LineSegment StartX=114 StartY=35 StartZ=0 EndX=19 EndY=35 EndZ=0
    g4: LineSegment StartX=5.21097e-06 StartY=3 StartZ=0 EndX=5.21097e-06 EndY=0 EndZ=0
    g5: LineSegment StartX=3 StartY=0 StartZ=0 EndX=5.21097e-06 EndY=0 EndZ=0
    g6: LineSegment StartX=3 StartY=19 StartZ=0 EndX=3 EndY=0 EndZ=0
    g7: LineSegment StartX=19 StartY=38 StartZ=0 EndX=124 EndY=38 EndZ=0
    g8: Circle CenterX=119 CenterY=35 CenterZ=0 NormalX=0 NormalY=0 NormalZ=1 AngleXU=0 Radius=1
    g9: Circle CenterX=121 CenterY=35 CenterZ=0 NormalX=0 NormalY=0 NormalZ=1 AngleXU=0 Radius=1
    g10: Circle CenterX=121 CenterY=33 CenterZ=0 NormalX=0 NormalY=0 NormalZ=1 AngleXU=0 Radius=1
    g11: BSplineCurve PolesCount=3 KnotsCount=2 Degree=2 IsPeriodic=0
    g12: GeomPoint X=119 Y=35 Z=0
    g13: GeomPoint X=121 Y=33 Z=0
    g14: LineSegment StartX=119 StartY=35 StartZ=0 EndX=114 EndY=35 EndZ=0
    g15: ArcOfCircle CenterX=105 CenterY=19 CenterZ=0 NormalX=0 NormalY=0 NormalZ=1 AngleXU=0 Radius=16 StartAngle=5.60905 EndAngle=6.28319
    g16: LineSegment StartX=121 StartY=33 StartZ=0 EndX=121 EndY=19 EndZ=0
    g17: LineSegment StartX=117.5 StartY=9.01251 StartZ=0 EndX=121.163 EndY=9.0125 EndZ=0
    g18: ArcOfCircle CenterX=105 CenterY=19 CenterZ=0 NormalX=0 NormalY=0 NormalZ=1 AngleXU=0 Radius=20.6155 StartAngle=5.7297 EndAngle=6.28319
    g19: LineSegment StartX=121.163 StartY=9.0125 StartZ=0 EndX=122.538 EndY=8.16329 EndZ=0
    g20: LineSegment StartX=124 StartY=38 StartZ=0 EndX=125.616 EndY=38 EndZ=0
    g21: LineSegment StartX=125.616 StartY=19 StartZ=0 EndX=125.616 EndY=38 EndZ=0
  constraints (49):
    c: Vertical(g0)
    c: Block(g0)
    c: Coincident(g1,g0)
    c: Block(g1)
    c: Coincident(g2,g1)
    c: Block(g2)
    c: Coincident(g3,g2)
    c: Horizontal(g3)
    c: Tangent(g3,g2)
    c: Coincident(g4,g0)
    c: Distance(g4) = 3
    c: Vertical(g4)
    c: Coincident(g5,g4)
    c: Horizontal(g5)
    c: Coincident(g6,g2)
    c: Coincident(g6,g5)
    c: Vertical(g6)
    c: Horizontal(g7)
    c: Distance(g7) = 105
    c: Coincident(g7,g1)
    c: Block(g3)
    c: Weight(g8) = 1
    c: Equal(g8,g9)
    c: Equal(g8,g10)
    c: InternalAlignment(g8,g11)
    c: InternalAlignment(g9,g11)
    c: InternalAlignment(g10,g11)
    c: InternalAlignment(g12,g11)
    c: InternalAlignment(g13,g11)
    c: Block(g11)
    c: Coincident(g14,g11)
    c: Coincident(g14,g3)
    c: Horizontal(g14)
    c: Block(g15)
    c: Coincident(g16,g11)
    c: Coincident(g16,g15)
    c: Vertical(g16)
    c: Distance(g16) = 14
    c: Coincident(g17,g15)
    c: Block(g18)
    c: Coincident(g19,g18)
    c: Coincident(g20,g7)
    c: Horizontal(g20)
    c: Vertical(g21)
    c: Coincident(g20,g21)
    c: Block(g20)
    c: Block(g21)
    c: Block(g19)
    c: Block(g17)
FEATURE [Part::Extrusion] Extrude029
  Base = -> Sketch038
  Dir = (0,0,1)
  DirMode = 2
  FaceMakerClass = Part::FaceMakerBullseye
  LengthFwd = 72
  LengthRev = 0
  Solid = true
  Symmetric = false
FEATURE [Part::Feature] Face085
  shape: bbox 4.8 x 25.5 x 2e-07 mm, 1 faces, 0 solids (baked)
FEATURE [Part::Revolution] Revolve089  label="moreFrontCaseScrewPost003"
  Angle = 360
  Axis = (0,1,0)
  Base = (0,0,0)
  FaceMakerClass = Part::FaceMakerBullseye
  Placement = pos=(109.5,4.5,3.5) rot=(0,0,1;0rad)
  Solid = false
  Source = -> Face085
  Symmetric = false
FEATURE [Part::Feature] Face086
  shape: bbox 4.8 x 25.5 x 2e-07 mm, 1 faces, 0 solids (baked)
FEATURE [Part::Revolution] Revolve090  label="moreFrontCaseScrewPost004"
  Angle = 360
  Axis = (0,1,0)
  Base = (0,0,0)
  FaceMakerClass = Part::FaceMakerBullseye
  Placement = pos=(109.5,4.5,68.5) rot=(0,0,1;0rad)
  Solid = false
  Source = -> Face086
  Symmetric = false
FEATURE [Part::Fillet] Fillet026  label="top013"
  Base = -> Extrude029
  Edges = 1 edges r=2: [Edge35]
FEATURE [Sketcher::SketchObject] Sketch039
  FullyConstrained = true
  sketch-geometry (7):
    g0: LineSegment StartX=0 StartY=0 StartZ=0 EndX=0 EndY=6 EndZ=0
    g1: Circle CenterX=0 CenterY=0 CenterZ=0 NormalX=0 NormalY=0 NormalZ=1 AngleXU=0 Radius=1
    g2: Circle CenterX=8 CenterY=6 CenterZ=0 NormalX=0 NormalY=0 NormalZ=1 AngleXU=0 Radius=1
    g3: BSplineCurve PolesCount=3 KnotsCount=2 Degree=2 IsPeriodic=0
    g4: GeomPoint X=0 Y=0 Z=0
    g5: GeomPoint X=8 Y=6 Z=0
    g6: LineSegment StartX=0 StartY=6 StartZ=0 EndX=8 EndY=6 EndZ=0
  constraints (14):
    c: Coincident(g0,g-1)
    c: Distance(g0) = 6
    c: Vertical(g0)
    c: Coincident(g3,g0)
    c: Weight(g1) = 1
    c: Equal(g1,g2)
    c: InternalAlignment(g1,g3)
    c: InternalAlignment(g2,g3)
    c: InternalAlignment(g4,g3)
    c: InternalAlignment(g5,g3)
    c: Block(g3)
    c: Coincident(g6,g0)
    c: Coincident(g6,g3)
    c: Horizontal(g6)
FEATURE [Sketcher::SketchObject] Sketch040
  FullyConstrained = true
  sketch-geometry (7):
    g0: LineSegment StartX=0 StartY=0 StartZ=0 EndX=0 EndY=6 EndZ=0
    g1: Circle CenterX=0 CenterY=0 CenterZ=0 NormalX=0 NormalY=0 NormalZ=1 AngleXU=0 Radius=1
    g2: Circle CenterX=8 CenterY=6 CenterZ=0 NormalX=0 NormalY=0 NormalZ=1 AngleXU=0 Radius=1
    g3: BSplineCurve PolesCount=3 KnotsCount=2 Degree=2 IsPeriodic=0
    g4: GeomPoint X=0 Y=0 Z=0
    g5: GeomPoint X=8 Y=6 Z=0
    g6: LineSegment StartX=0 StartY=6 StartZ=0 EndX=8 EndY=6 EndZ=0
  constraints (14):
    c: Coincident(g0,g-1)
    c: Distance(g0) = 6
    c: Vertical(g0)
    c: Coincident(g3,g0)
    c: Weight(g1) = 1
    c: Equal(g1,g2)
    c: InternalAlignment(g1,g3)
    c: InternalAlignment(g2,g3)
    c: InternalAlignment(g4,g3)
    c: InternalAlignment(g5,g3)
    c: Block(g3)
    c: Coincident(g6,g0)
    c: Coincident(g6,g3)
    c: Horizontal(g6)
FEATURE [Sketcher::SketchObject] Sketch041
  FullyConstrained = true
  sketch-geometry (7):
    g0: LineSegment StartX=0 StartY=0 StartZ=0 EndX=0 EndY=6 EndZ=0
    g1: Circle CenterX=0 CenterY=0 CenterZ=0 NormalX=0 NormalY=0 NormalZ=1 AngleXU=0 Radius=1
    g2: Circle CenterX=8 CenterY=6 CenterZ=0 NormalX=0 NormalY=0 NormalZ=1 AngleXU=0 Radius=1
    g3: BSplineCurve PolesCount=3 KnotsCount=2 Degree=2 IsPeriodic=0
    g4: GeomPoint X=0 Y=0 Z=0
    g5: GeomPoint X=8 Y=6 Z=0
    g6: LineSegment StartX=0 StartY=6 StartZ=0 EndX=8 EndY=6 EndZ=0
  constraints (14):
    c: Coincident(g0,g-1)
    c: Distance(g0) = 6
    c: Vertical(g0)
    c: Coincident(g3,g0)
    c: Weight(g1) = 1
    c: Equal(g1,g2)
    c: InternalAlignment(g1,g3)
    c: InternalAlignment(g2,g3)
    c: InternalAlignment(g4,g3)
    c: InternalAlignment(g5,g3)
    c: Block(g3)
    c: Coincident(g6,g0)
    c: Coincident(g6,g3)
    c: Horizontal(g6)
FEATURE [Sketcher::SketchObject] Sketch042
  FullyConstrained = true
  sketch-geometry (7):
    g0: LineSegment StartX=0 StartY=0 StartZ=0 EndX=0 EndY=6 EndZ=0
    g1: Circle CenterX=0 CenterY=0 CenterZ=0 NormalX=0 NormalY=0 NormalZ=1 AngleXU=0 Radius=1
    g2: Circle CenterX=8 CenterY=6 CenterZ=0 NormalX=0 NormalY=0 NormalZ=1 AngleXU=0 Radius=1
    g3: BSplineCurve PolesCount=3 KnotsCount=2 Degree=2 IsPeriodic=0
    g4: GeomPoint X=0 Y=0 Z=0
    g5: GeomPoint X=8 Y=6 Z=0
    g6: LineSegment StartX=0 StartY=6 StartZ=0 EndX=8 EndY=6 EndZ=0
  constraints (14):
    c: Coincident(g0,g-1)
    c: Distance(g0) = 6
    c: Vertical(g0)
    c: Coincident(g3,g0)
    c: Weight(g1) = 1
    c: Equal(g1,g2)
    c: InternalAlignment(g1,g3)
    c: InternalAlignment(g2,g3)
    c: InternalAlignment(g4,g3)
    c: InternalAlignment(g5,g3)
    c: Block(g3)
    c: Coincident(g6,g0)
    c: Coincident(g6,g3)
    c: Horizontal(g6)
FEATURE [Part::Extrusion] Extrude030  label="caseScrewPillarBracket008"
  Base = -> Sketch039
  Dir = (0,0,1)
  DirMode = 2
  FaceMakerClass = Part::FaceMakerBullseye
  LengthFwd = 2.4
  LengthRev = 0
  Placement = pos=(15.76,29,8.8) rot=(0,1,0;0rad)
  Solid = true
  Symmetric = false
FEATURE [Part::Extrusion] Extrude031  label="caseScrewPillarBracket009"
  Base = -> Sketch040
  Dir = (0,0,1)
  DirMode = 2
  FaceMakerClass = Part::FaceMakerBullseye
  LengthFwd = 2.4
  LengthRev = 0
  Placement = pos=(15.76,29,60.8) rot=(0,0,1;0rad)
  Solid = true
  Symmetric = false
FEATURE [Part::Extrusion] Extrude032  label="caseScrewPillarBracket010"
  Base = -> Sketch041
  Dir = (0,0,1)
  DirMode = 2
  FaceMakerClass = Part::FaceMakerBullseye
  LengthFwd = 2.4
  LengthRev = 0
  Placement = pos=(13.7,29,13.26) rot=(0,-1,0;1.5708rad)
  Solid = true
  Symmetric = false
FEATURE [Part::Extrusion] Extrude033  label="caseScrewPillarBracket011"
  Base = -> Sketch042
  Dir = (0,0,1)
  DirMode = 2
  FaceMakerClass = Part::FaceMakerBullseye
  LengthFwd = 2.4
  LengthRev = 0
  Placement = pos=(11.3,29,58.74) rot=(0,1,0;1.5708rad)
  Solid = true
  Symmetric = false
FEATURE [Sketcher::SketchObject] Sketch043
  FullyConstrained = true
  sketch-geometry (7):
    g0: LineSegment StartX=0 StartY=0 StartZ=0 EndX=0 EndY=6 EndZ=0
    g1: Circle CenterX=0 CenterY=0 CenterZ=0 NormalX=0 NormalY=0 NormalZ=1 AngleXU=0 Radius=1
    g2: Circle CenterX=8 CenterY=6 CenterZ=0 NormalX=0 NormalY=0 NormalZ=1 AngleXU=0 Radius=1
    g3: BSplineCurve PolesCount=3 KnotsCount=2 Degree=2 IsPeriodic=0
    g4: GeomPoint X=0 Y=0 Z=0
    g5: GeomPoint X=8 Y=6 Z=0
    g6: LineSegment StartX=0 StartY=6 StartZ=0 EndX=8 EndY=6 EndZ=0
  constraints (14):
    c: Coincident(g0,g-1)
    c: Distance(g0) = 6
    c: Vertical(g0)
    c: Coincident(g3,g0)
    c: Weight(g1) = 1
    c: Equal(g1,g2)
    c: InternalAlignment(g1,g3)
    c: InternalAlignment(g2,g3)
    c: InternalAlignment(g4,g3)
    c: InternalAlignment(g5,g3)
    c: Block(g3)
    c: Coincident(g6,g0)
    c: Coincident(g6,g3)
    c: Horizontal(g6)
FEATURE [Part::Extrusion] Extrude034  label="caseScrewPillarBracket012"
  Base = -> Sketch043
  Dir = (0,0,1)
  DirMode = 2
  FaceMakerClass = Part::FaceMakerBullseye
  LengthFwd = 2.4
  LengthRev = 0
  Placement = pos=(88.3,29,65.23) rot=(0,1,0;1.5708rad)
  Solid = true
  Symmetric = false
FEATURE [Sketcher::SketchObject] Sketch044
  FullyConstrained = true
  sketch-geometry (7):
    g0: LineSegment StartX=0 StartY=0 StartZ=0 EndX=0 EndY=6 EndZ=0
    g1: Circle CenterX=0 CenterY=0 CenterZ=0 NormalX=0 NormalY=0 NormalZ=1 AngleXU=0 Radius=1
    g2: Circle CenterX=8 CenterY=6 CenterZ=0 NormalX=0 NormalY=0 NormalZ=1 AngleXU=0 Radius=1
    g3: BSplineCurve PolesCount=3 KnotsCount=2 Degree=2 IsPeriodic=0
    g4: GeomPoint X=0 Y=0 Z=0
    g5: GeomPoint X=8 Y=6 Z=0
    g6: LineSegment StartX=0 StartY=6 StartZ=0 EndX=8 EndY=6 EndZ=0
  constraints (14):
    c: Coincident(g0,g-1)
    c: Distance(g0) = 6
    c: Vertical(g0)
    c: Coincident(g3,g0)
    c: Weight(g1) = 1
    c: Equal(g1,g2)
    c: InternalAlignment(g1,g3)
    c: InternalAlignment(g2,g3)
    c: InternalAlignment(g4,g3)
    c: InternalAlignment(g5,g3)
    c: Block(g3)
    c: Coincident(g6,g0)
    c: Coincident(g6,g3)
    c: Horizontal(g6)
FEATURE [Part::Extrusion] Extrude035  label="caseScrewPillarBracket013"
  Base = -> Sketch044
  Dir = (0,0,1)
  DirMode = 2
  FaceMakerClass = Part::FaceMakerBullseye
  LengthFwd = 2.4
  LengthRev = 0
  Placement = pos=(90.7,29,6.77) rot=(0,-1,0;1.5708rad)
  Solid = true
  Symmetric = false
FEATURE [Sketcher::SketchObject] Sketch045
  FullyConstrained = true
  sketch-geometry (7):
    g0: LineSegment StartX=0 StartY=0 StartZ=0 EndX=0 EndY=6 EndZ=0
    g1: Circle CenterX=0 CenterY=0 CenterZ=0 NormalX=0 NormalY=0 NormalZ=1 AngleXU=0 Radius=1
    g2: Circle CenterX=8 CenterY=6 CenterZ=0 NormalX=0 NormalY=0 NormalZ=1 AngleXU=0 Radius=1
    g3: BSplineCurve PolesCount=3 KnotsCount=2 Degree=2 IsPeriodic=0
    g4: GeomPoint X=0 Y=0 Z=0
    g5: GeomPoint X=8 Y=6 Z=0
    g6: LineSegment StartX=0 StartY=6 StartZ=0 EndX=8 EndY=6 EndZ=0
  constraints (14):
    c: Coincident(g0,g-1)
    c: Distance(g0) = 6
    c: Vertical(g0)
    c: Coincident(g3,g0)
    c: Weight(g1) = 1
    c: Equal(g1,g2)
    c: InternalAlignment(g1,g3)
    c: InternalAlignment(g2,g3)
    c: InternalAlignment(g4,g3)
    c: InternalAlignment(g5,g3)
    c: Block(g3)
    c: Coincident(g6,g0)
    c: Coincident(g6,g3)
    c: Horizontal(g6)
FEATURE [Sketcher::SketchObject] Sketch046
  FullyConstrained = true
  sketch-geometry (7):
    g0: LineSegment StartX=0 StartY=0 StartZ=0 EndX=0 EndY=6 EndZ=0
    g1: Circle CenterX=0 CenterY=0 CenterZ=0 NormalX=0 NormalY=0 NormalZ=1 AngleXU=0 Radius=1
    g2: Circle CenterX=8 CenterY=6 CenterZ=0 NormalX=0 NormalY=0 NormalZ=1 AngleXU=0 Radius=1
    g3: BSplineCurve PolesCount=3 KnotsCount=2 Degree=2 IsPeriodic=0
    g4: GeomPoint X=0 Y=0 Z=0
    g5: GeomPoint X=8 Y=6 Z=0
    g6: LineSegment StartX=0 StartY=6 StartZ=0 EndX=8 EndY=6 EndZ=0
  constraints (14):
    c: Coincident(g0,g-1)
    c: Distance(g0) = 6
    c: Vertical(g0)
    c: Coincident(g3,g0)
    c: Weight(g1) = 1
    c: Equal(g1,g2)
    c: InternalAlignment(g1,g3)
    c: InternalAlignment(g2,g3)
    c: InternalAlignment(g4,g3)
    c: InternalAlignment(g5,g3)
    c: Block(g3)
    c: Coincident(g6,g0)
    c: Coincident(g6,g3)
    c: Horizontal(g6)
FEATURE [Part::Extrusion] Extrude036  label="caseScrewPillarBracket014"
  Base = -> Sketch045
  Dir = (0,0,1)
  DirMode = 2
  FaceMakerClass = Part::FaceMakerBullseye
  LengthFwd = 2.4
  LengthRev = 0
  Placement = pos=(110.7,29,6.77) rot=(0,-1,0;1.5708rad)
  Solid = true
  Symmetric = false
FEATURE [Part::Extrusion] Extrude037  label="caseScrewPillarBracket015"
  Base = -> Sketch046
  Dir = (0,0,1)
  DirMode = 2
  FaceMakerClass = Part::FaceMakerBullseye
  LengthFwd = 2.4
  LengthRev = 0
  Placement = pos=(108.3,29,65.23) rot=(0,1,0;1.5708rad)
  Solid = true
  Symmetric = false
FEATURE [Part::Box] Box013  label="frontCaseScrewPillarBracket002"
  AttacherType = Attacher::AttachEngine3D
  Height = 2.4
  Length = 22
  Placement = pos=(87,28,2.3) rot=(0,0,1;0rad)
  Width = 7
FEATURE [Part::Box] Box014  label="frontCaseScrewPillarBracket003"
  AttacherType = Attacher::AttachEngine3D
  Height = 2.4
  Length = 22
  Placement = pos=(87,28,67.3) rot=(0,0,1;0rad)
  Width = 7
FEATURE [Part::Feature] Face087
  shape: bbox 4.8 x 30.2 x 2e-07 mm, 1 faces, 0 solids (baked)
FEATURE [Part::Revolution] Revolve091  label="frontCaseScrewPost004"
  Angle = 360
  Axis = (0,1,0)
  Base = (0,0,0)
  FaceMakerClass = Part::FaceMakerBullseye
  Placement = pos=(89.5,4.5,3.5) rot=(0,0,1;0rad)
  Solid = false
  Source = -> Face087
  Symmetric = false
FEATURE [Part::Feature] Face088
  shape: bbox 4.8 x 30.2 x 2e-07 mm, 1 faces, 0 solids (baked)
FEATURE [Part::Revolution] Revolve092  label="frontCaseScrewPost005"
  Angle = 360
  Axis = (0,1,0)
  Base = (0,0,0)
  FaceMakerClass = Part::FaceMakerBullseye
  Placement = pos=(89.5,4.5,68.5) rot=(0,0,1;0rad)
  Solid = false
  Source = -> Face088
  Symmetric = false
FEATURE [Part::Feature] Face089
  shape: bbox 3.5 x 30.2 x 2e-07 mm, 1 faces, 0 solids (baked)
FEATURE [Part::Revolution] Revolve093  label="backCaseScrewPost002"
  Angle = 360
  Axis = (0,1,0)
  Base = (0,0,0)
  FaceMakerClass = Part::FaceMakerBullseye
  Placement = pos=(12.5,4.5,10) rot=(0,0,1;0rad)
  Solid = false
  Source = -> Face089
  Symmetric = false
FEATURE [Part::Feature] Face090
  shape: bbox 3.5 x 30.2 x 2e-07 mm, 1 faces, 0 solids (baked)
FEATURE [Part::Revolution] Revolve094  label="backCaseScrewPost003"
  Angle = 360
  Axis = (0,1,0)
  Base = (0,0,0)
  FaceMakerClass = Part::FaceMakerBullseye
  Placement = pos=(12.5,4.5,62) rot=(0,0,1;0rad)
  Solid = false
  Source = -> Face090
  Symmetric = false
FEATURE [Part::Box] Box015  label="Cube011"
  AttacherType = Attacher::AttachEngine3D
  Height = 28.8
  Length = 3
  Placement = pos=(107.3,28,21.6) rot=(0,0,1;0rad)
  Width = 7
FEATURE [Part::Box] Box016  label="Cube012"
  AttacherType = Attacher::AttachEngine3D
  Height = 3
  Length = 7.4
  Placement = pos=(107.3,28,18.6) rot=(0,0,1;0rad)
  Width = 7
FEATURE [Part::Box] Box017  label="Cube013"
  AttacherType = Attacher::AttachEngine3D
  Height = 3
  Length = 7.4
  Placement = pos=(107.3,28,50.4) rot=(0,0,1;0rad)
  Width = 7
FEATURE [Part::Cylinder] Cylinder024
  Angle = 360
  AttacherType = Attacher::AttachEngine3D
  Height = 20
  Placement = pos=(0,0,36.15) rot=(0,0,1;0rad)
  Radius = 14.3
FEATURE [Part::Cylinder] Cylinder025
  Angle = 360
  AttacherType = Attacher::AttachEngine3D
  Height = 10
  Placement = pos=(0,0,36.15) rot=(0,0,1;0rad)
  Radius = 4
FEATURE [Part::MultiFuse] Fusion066  label="removeToCreteHoleForPlugHousing009"
  Placement = pos=(70,19,36) rot=(0,1,0;1.5708rad)
  Shapes = -> [Cylinder024,Cylinder025]
FEATURE [Part::MultiFuse] Fusion065  label="plugHousingBracketHolder002"
  Shapes = -> [Box017,Box015,Box016]
FEATURE [Part::Cut] Cut025  label="plugHousingBracketHolder003"
  Base = -> Fusion065
  Placement = pos=(7,0,0) rot=(0,0,1;0rad)
  Tool = -> Fusion066
FEATURE [Sketcher::SketchObject] Sketch047
  FullyConstrained = false
  Placement = pos=(0,0,0) rot=(1,0,0;1.5708rad)
  sketch-geometry (24):
    g0: ArcOfCircle CenterX=-4 CenterY=-10.5 CenterZ=0 NormalX=0 NormalY=0 NormalZ=1 AngleXU=0 Radius=1.5 StartAngle=6e-16 EndAngle=3.14159
    g1: ArcOfCircle CenterX=-34.2 CenterY=-10.5 CenterZ=0 NormalX=0 NormalY=0 NormalZ=1 AngleXU=0 Radius=1.5 StartAngle=0 EndAngle=3.14159
    g2: ArcOfCircle CenterX=-34.2 CenterY=-27.7 CenterZ=0 NormalX=0 NormalY=0 NormalZ=1 AngleXU=0 Radius=1.5 StartAngle=3.14159 EndAngle=6.28319
    g3: ArcOfCircle CenterX=-4 CenterY=-27.7 CenterZ=0 NormalX=0 NormalY=0 NormalZ=1 AngleXU=0 Radius=1.5 StartAngle=3.1416 EndAngle=6.28319
    g4: ArcOfCircle CenterX=-10 CenterY=-4.3 CenterZ=0 NormalX=0 NormalY=0 NormalZ=1 AngleXU=0 Radius=1.5 StartAngle=2e-16 EndAngle=3.14159
    g5: ArcOfCircle CenterX=-16.1 CenterY=-1.8 CenterZ=0 NormalX=0 NormalY=0 NormalZ=1 AngleXU=0 Radius=1.5 StartAngle=5e-16 EndAngle=3.14159
    g6: ArcOfCircle CenterX=-22.1 CenterY=-1.8 CenterZ=0 NormalX=0 NormalY=0 NormalZ=1 AngleXU=0 Radius=1.5 StartAngle=5e-16 EndAngle=3.14159
    g7: ArcOfCircle CenterX=-28.2 CenterY=-4.3 CenterZ=0 NormalX=0 NormalY=0 NormalZ=1 AngleXU=0 Radius=1.5 StartAngle=2e-16 EndAngle=3.14159
    g8: ArcOfCircle CenterX=-10 CenterY=-33.9 CenterZ=0 NormalX=0 NormalY=0 NormalZ=1 AngleXU=0 Radius=1.5 StartAngle=3.14159 EndAngle=6.28319
    g9: ArcOfCircle CenterX=-16.1 CenterY=-36.4 CenterZ=0 NormalX=0 NormalY=0 NormalZ=1 AngleXU=0 Radius=1.5 StartAngle=3.14159 EndAngle=6.28319
    g10: ArcOfCircle CenterX=-22.1 CenterY=-36.4 CenterZ=0 NormalX=0 NormalY=0 NormalZ=1 AngleXU=0 Radius=1.5 StartAngle=3.14159 EndAngle=6.28319
    g11: ArcOfCircle CenterX=-28.2 CenterY=-33.9 CenterZ=0 NormalX=0 NormalY=0 NormalZ=1 AngleXU=0 Radius=1.5 StartAngle=3.14159 EndAngle=6.28319
    g12: LineSegment StartX=-35.7 StartY=-10.5 StartZ=0 EndX=-35.7 EndY=-27.7 EndZ=0
    g13: LineSegment StartX=-32.7 StartY=-10.5 StartZ=0 EndX=-32.7 EndY=-27.7 EndZ=0
    g14: LineSegment StartX=-29.7 StartY=-33.9 StartZ=0 EndX=-29.7 EndY=-4.3 EndZ=0
    g15: LineSegment StartX=-26.7 StartY=-33.9 StartZ=0 EndX=-26.7 EndY=-4.3 EndZ=0
    g16: LineSegment StartX=-2.5 StartY=-10.5 StartZ=0 EndX=-2.5 EndY=-27.7 EndZ=0
    g17: LineSegment StartX=-8.5 StartY=-4.3 StartZ=0 EndX=-8.5 EndY=-33.9 EndZ=0
    g18: LineSegment StartX=-5.5 StartY=-10.5 StartZ=0 EndX=-5.5 EndY=-27.7 EndZ=0
    g19: LineSegment StartX=-11.5 StartY=-4.3 StartZ=0 EndX=-11.5 EndY=-33.9 EndZ=0
    g20: LineSegment StartX=-14.6 StartY=-1.8 StartZ=0 EndX=-14.6 EndY=-36.4 EndZ=0
    g21: LineSegment StartX=-17.6 StartY=-1.8 StartZ=0 EndX=-17.6 EndY=-36.4 EndZ=0
    g22: LineSegment StartX=-20.6 StartY=-36.4 StartZ=0 EndX=-20.6 EndY=-1.8 EndZ=0
    g23: LineSegment StartX=-23.6 StartY=-1.8 StartZ=0 EndX=-23.6 EndY=-36.4 EndZ=0
  constraints (48):
    c: Block(g0)
    c: Block(g1)
    c: Block(g2)
    c: Block(g3)
    c: Block(g4)
    c: Block(g5)
    c: Block(g6)
    c: Block(g7)
    c: Block(g8)
    c: Block(g9)
    c: Block(g10)
    c: Block(g11)
    c: Coincident(g12,g1)
    c: Coincident(g12,g2)
    c: Vertical(g12)
    c: Coincident(g13,g1)
    c: Coincident(g13,g2)
    c: Vertical(g13)
    c: Coincident(g14,g11)
    c: Coincident(g14,g7)
    c: Vertical(g14)
    c: Coincident(g15,g11)
    c: Coincident(g15,g7)
    c: Vertical(g15)
    c: Coincident(g16,g0)
    c: Coincident(g16,g3)
    c: Vertical(g16)
    c: Coincident(g17,g4)
    c: Coincident(g17,g8)
    c: Vertical(g17)
    c: Coincident(g18,g0)
    c: Coincident(g18,g3)
    c: Vertical(g18)
    c: Coincident(g19,g4)
    c: Coincident(g19,g8)
    c: Vertical(g19)
    c: Coincident(g20,g5)
    c: Coincident(g20,g9)
    c: Vertical(g20)
    c: Coincident(g21,g5)
    c: Coincident(g21,g9)
    c: Vertical(g21)
    c: Coincident(g22,g10)
    c: Coincident(g22,g6)
    c: Vertical(g22)
    c: Coincident(g23,g6)
    c: Coincident(g23,g10)
    c: Vertical(g23)
FEATURE [Part::Extrusion] Extrude038  label="removeToCreateFanGrillHoles001"
  Base = -> Sketch047
  Dir = (0,-1,6e-16)
  DirMode = 2
  FaceMakerClass = Part::FaceMakerBullseye
  LengthFwd = 10
  LengthRev = 0
  Placement = pos=(65.4,44,54.82) rot=(0,0,1;0rad)
  Solid = true
  Symmetric = false
FEATURE [Part::Feature] Wire004
  shape: bbox 11 x 5.2 x 2e-07 mm, 0 faces, 0 solids (baked)
FEATURE [Part::Revolution] Revolve095
  Angle = 360
  Axis = (0,1,0)
  Base = (0,0,0)
  FaceMakerClass = Part::FaceMakerBullseye
  Placement = pos=(30.3,38,19.7) rot=(0,0,1;0rad)
  Solid = true
  Source = -> Wire004
  Symmetric = false
FEATURE [Part::Feature] Wire005
  shape: bbox 11 x 5.2 x 2e-07 mm, 0 faces, 0 solids (baked)
FEATURE [Part::Revolution] Revolve096
  Angle = 360
  Axis = (0,1,0)
  Base = (0,0,0)
  FaceMakerClass = Part::FaceMakerBullseye
  Placement = pos=(30.3,38,51.7) rot=(0,0,1;0rad)
  Solid = true
  Source = -> Wire005
  Symmetric = false
FEATURE [Part::Feature] Wire006
  shape: bbox 11 x 5.2 x 2e-07 mm, 0 faces, 0 solids (baked)
FEATURE [Part::Revolution] Revolve097
  Angle = 360
  Axis = (0,1,0)
  Base = (0,0,0)
  FaceMakerClass = Part::FaceMakerBullseye
  Placement = pos=(62.3,38,51.7) rot=(0,0,1;0rad)
  Solid = true
  Source = -> Wire006
  Symmetric = false
FEATURE [Part::Feature] Wire007
  shape: bbox 11 x 5.2 x 2e-07 mm, 0 faces, 0 solids (baked)
FEATURE [Part::Revolution] Revolve098
  Angle = 360
  Axis = (0,1,0)
  Base = (0,0,0)
  FaceMakerClass = Part::FaceMakerBullseye
  Placement = pos=(62.3,38,19.7) rot=(0,0,1;0rad)
  Solid = true
  Source = -> Wire007
  Symmetric = false
FEATURE [Part::MultiFuse] Fusion067  label="fanScrewHousing002"
  Shapes = -> [Revolve098,Revolve097,Revolve096,Revolve095]
FEATURE [Part::Feature] Face091 .. Face094  x4 (patterned run collapsed; names and placements below)
  shape: bbox 3.5 x 17.8 x 2e-07 mm, 1 faces, 0 solids (baked)
FEATURE [Part::Revolution] Revolve099  label="removeToCreateScrewAndThreadedInsertHole026"
  Angle = 360
  Axis = (0,1,0)
  Base = (0,0,0)
  FaceMakerClass = Part::FaceMakerBullseye
  Placement = pos=(62.3,30.3,19.7) rot=(0,0,1;0rad)
  Solid = false
  Source = -> Face091
  Symmetric = false
FEATURE [Part::Revolution] Revolve100  label="removeToCreateScrewAndThreadedInsertHole027"
  Angle = 360
  Axis = (0,1,0)
  Base = (0,0,0)
  FaceMakerClass = Part::FaceMakerBullseye
  Placement = pos=(62.3,30.3,51.7) rot=(0,0,1;0rad)
  Solid = false
  Source = -> Face092
  Symmetric = false
FEATURE [Part::Revolution] Revolve101  label="removeToCreateScrewAndThreadedInsertHole028"
  Angle = 360
  Axis = (0,1,0)
  Base = (0,0,0)
  FaceMakerClass = Part::FaceMakerBullseye
  Placement = pos=(30.3,30.3,19.7) rot=(0,0,1;0rad)
  Solid = false
  Source = -> Face093
  Symmetric = false
FEATURE [Part::Revolution] Revolve102  label="removeToCreateScrewAndThreadedInsertHole029"
  Angle = 360
  Axis = (0,1,0)
  Base = (0,0,0)
  FaceMakerClass = Part::FaceMakerBullseye
  Placement = pos=(30.3,30.3,51.7) rot=(0,0,1;0rad)
  Solid = false
  Source = -> Face094
  Symmetric = false
FEATURE [Part::MultiFuse] Fusion068  label="createThreadedInsertHolesForFan002"
  Shapes = -> [Revolve099,Revolve100,Revolve101,Revolve102]
FEATURE [Part::Cut] Cut026  label="fanScrewHousing003"
  Base = -> Fusion067
  Tool = -> Fusion068
FEATURE [Sketcher::SketchObject] Sketch048
  FullyConstrained = false
  Placement = pos=(0,0,0) rot=(1,0,0;1.5708rad)
  sketch-geometry (24):
    g0: ArcOfCircle CenterX=-4 CenterY=-10.5 CenterZ=0 NormalX=0 NormalY=0 NormalZ=1 AngleXU=0 Radius=1.5 StartAngle=6e-16 EndAngle=3.14159
    g1: ArcOfCircle CenterX=-34.2 CenterY=-10.5 CenterZ=0 NormalX=0 NormalY=0 NormalZ=1 AngleXU=0 Radius=1.5 StartAngle=0 EndAngle=3.14159
    g2: ArcOfCircle CenterX=-34.2 CenterY=-27.7 CenterZ=0 NormalX=0 NormalY=0 NormalZ=1 AngleXU=0 Radius=1.5 StartAngle=3.14159 EndAngle=6.28319
    g3: ArcOfCircle CenterX=-4 CenterY=-27.7 CenterZ=0 NormalX=0 NormalY=0 NormalZ=1 AngleXU=0 Radius=1.5 StartAngle=3.1416 EndAngle=6.28319
    g4: ArcOfCircle CenterX=-10 CenterY=-4.3 CenterZ=0 NormalX=0 NormalY=0 NormalZ=1 AngleXU=0 Radius=1.5 StartAngle=2e-16 EndAngle=3.14159
    g5: ArcOfCircle CenterX=-16.1 CenterY=-1.8 CenterZ=0 NormalX=0 NormalY=0 NormalZ=1 AngleXU=0 Radius=1.5 StartAngle=5e-16 EndAngle=3.14159
    g6: ArcOfCircle CenterX=-22.1 CenterY=-1.8 CenterZ=0 NormalX=0 NormalY=0 NormalZ=1 AngleXU=0 Radius=1.5 StartAngle=5e-16 EndAngle=3.14159
    g7: ArcOfCircle CenterX=-28.2 CenterY=-4.3 CenterZ=0 NormalX=0 NormalY=0 NormalZ=1 AngleXU=0 Radius=1.5 StartAngle=2e-16 EndAngle=3.14159
    g8: ArcOfCircle CenterX=-10 CenterY=-33.9 CenterZ=0 NormalX=0 NormalY=0 NormalZ=1 AngleXU=0 Radius=1.5 StartAngle=3.14159 EndAngle=6.28319
    g9: ArcOfCircle CenterX=-16.1 CenterY=-36.4 CenterZ=0 NormalX=0 NormalY=0 NormalZ=1 AngleXU=0 Radius=1.5 StartAngle=3.14159 EndAngle=6.28319
    g10: ArcOfCircle CenterX=-22.1 CenterY=-36.4 CenterZ=0 NormalX=0 NormalY=0 NormalZ=1 AngleXU=0 Radius=1.5 StartAngle=3.14159 EndAngle=6.28319
    g11: ArcOfCircle CenterX=-28.2 CenterY=-33.9 CenterZ=0 NormalX=0 NormalY=0 NormalZ=1 AngleXU=0 Radius=1.5 StartAngle=3.14159 EndAngle=6.28319
    g12: LineSegment StartX=-35.7 StartY=-10.5 StartZ=0 EndX=-35.7 EndY=-27.7 EndZ=0
    g13: LineSegment StartX=-32.7 StartY=-10.5 StartZ=0 EndX=-32.7 EndY=-27.7 EndZ=0
    g14: LineSegment StartX=-29.7 StartY=-33.9 StartZ=0 EndX=-29.7 EndY=-4.3 EndZ=0
    g15: LineSegment StartX=-26.7 StartY=-33.9 StartZ=0 EndX=-26.7 EndY=-4.3 EndZ=0
    g16: LineSegment StartX=-2.5 StartY=-10.5 StartZ=0 EndX=-2.5 EndY=-27.7 EndZ=0
    g17: LineSegment StartX=-8.5 StartY=-4.3 StartZ=0 EndX=-8.5 EndY=-33.9 EndZ=0
    g18: LineSegment StartX=-5.5 StartY=-10.5 StartZ=0 EndX=-5.5 EndY=-27.7 EndZ=0
    g19: LineSegment StartX=-11.5 StartY=-4.3 StartZ=0 EndX=-11.5 EndY=-33.9 EndZ=0
    g20: LineSegment StartX=-14.6 StartY=-1.8 StartZ=0 EndX=-14.6 EndY=-36.4 EndZ=0
    g21: LineSegment StartX=-17.6 StartY=-1.8 StartZ=0 EndX=-17.6 EndY=-36.4 EndZ=0
    g22: LineSegment StartX=-20.6 StartY=-36.4 StartZ=0 EndX=-20.6 EndY=-1.8 EndZ=0
    g23: LineSegment StartX=-23.6 StartY=-1.8 StartZ=0 EndX=-23.6 EndY=-36.4 EndZ=0
  constraints (48):
    c: Block(g0)
    c: Block(g1)
    c: Block(g2)
    c: Block(g3)
    c: Block(g4)
    c: Block(g5)
    c: Block(g6)
    c: Block(g7)
    c: Block(g8)
    c: Block(g9)
    c: Block(g10)
    c: Block(g11)
    c: Coincident(g12,g1)
    c: Coincident(g12,g2)
    c: Vertical(g12)
    c: Coincident(g13,g1)
    c: Coincident(g13,g2)
    c: Vertical(g13)
    c: Coincident(g14,g11)
    c: Coincident(g14,g7)
    c: Vertical(g14)
    c: Coincident(g15,g11)
    c: Coincident(g15,g7)
    c: Vertical(g15)
    c: Coincident(g16,g0)
    c: Coincident(g16,g3)
    c: Vertical(g16)
    c: Coincident(g17,g4)
    c: Coincident(g17,g8)
    c: Vertical(g17)
    c: Coincident(g18,g0)
    c: Coincident(g18,g3)
    c: Vertical(g18)
    c: Coincident(g19,g4)
    c: Coincident(g19,g8)
    c: Vertical(g19)
    c: Coincident(g20,g5)
    c: Coincident(g20,g9)
    c: Vertical(g20)
    c: Coincident(g21,g5)
    c: Coincident(g21,g9)
    c: Vertical(g21)
    c: Coincident(g22,g10)
    c: Coincident(g22,g6)
    c: Vertical(g22)
    c: Coincident(g23,g6)
    c: Coincident(g23,g10)
    c: Vertical(g23)
FEATURE [Part::Extrusion] Extrude039  label="removeToCreateFanGrillHoles002"
  Base = -> Sketch048
  Dir = (0,-1,6e-16)
  DirMode = 2
  FaceMakerClass = Part::FaceMakerBullseye
  LengthFwd = 10
  LengthRev = 0
  Placement = pos=(65.4,44,54.82) rot=(0,0,1;0rad)
  Solid = true
  Symmetric = false
FEATURE [Part::Cut] Cut027  label="fanScrewHousing004"
  Base = -> Cut026
  Tool = -> Extrude038
FEATURE [Part::Cut] Cut028  label="top014"
  Base = -> Fillet026
  Tool = -> Extrude039
FEATURE [Part::Feature] Face095 .. Face098  x4 (patterned run collapsed; names and placements below)
  shape: bbox 3.5 x 17.8 x 2e-07 mm, 1 faces, 0 solids (baked)
FEATURE [Part::Revolution] Revolve103  label="removeToCreateScrewAndThreadedInsertHole030"
  Angle = 360
  Axis = (0,1,0)
  Base = (0,0,0)
  FaceMakerClass = Part::FaceMakerBullseye
  Placement = pos=(62.3,30.3,19.7) rot=(0,0,1;0rad)
  Solid = false
  Source = -> Face095
  Symmetric = false
FEATURE [Part::Revolution] Revolve104  label="removeToCreateScrewAndThreadedInsertHole031"
  Angle = 360
  Axis = (0,1,0)
  Base = (0,0,0)
  FaceMakerClass = Part::FaceMakerBullseye
  Placement = pos=(62.3,30.3,51.7) rot=(0,0,1;0rad)
  Solid = false
  Source = -> Face096
  Symmetric = false
FEATURE [Part::Revolution] Revolve105  label="removeToCreateScrewAndThreadedInsertHole032"
  Angle = 360
  Axis = (0,1,0)
  Base = (0,0,0)
  FaceMakerClass = Part::FaceMakerBullseye
  Placement = pos=(30.3,30.3,19.7) rot=(0,0,1;0rad)
  Solid = false
  Source = -> Face097
  Symmetric = false
FEATURE [Part::Revolution] Revolve106  label="removeToCreateScrewAndThreadedInsertHole033"
  Angle = 360
  Axis = (0,1,0)
  Base = (0,0,0)
  FaceMakerClass = Part::FaceMakerBullseye
  Placement = pos=(30.3,30.3,51.7) rot=(0,0,1;0rad)
  Solid = false
  Source = -> Face098
  Symmetric = false
FEATURE [Part::MultiFuse] Fusion069  label="createThreadedInsertHolesForFan003"
  Shapes = -> [Revolve103,Revolve104,Revolve105,Revolve106]
FEATURE [Part::Cut] Cut029  label="top015"
  Base = -> Cut028
  Tool = -> Fusion054
FEATURE [Part::Cut] Cut030  label="fanScrewHousing005"
  Base = -> Cut027
  Tool = -> Fusion069
FEATURE [Part::Cylinder] Cylinder026  label="removeToCreteHoleForPlugHousing010"
  Angle = 360
  AttacherType = Attacher::AttachEngine3D
  Height = 20
  Placement = pos=(-2,19,36) rot=(0,1,0;1.5708rad)
  Radius = 14.3
FEATURE [Part::Box] Box018  label="removeToCreteHoleForPlugHousing011"
  AttacherType = Attacher::AttachEngine3D
  Height = 28.6
  Length = 10
  Placement = pos=(-2,0,21.7) rot=(0,0,1;0rad)
  Width = 19
FEATURE [Part::Box] Box019  label="wireHolderBottomCaseBit"
  AttacherType = Attacher::AttachEngine3D
  Height = 28
  Length = 3
  Placement = pos=(0,0,22) rot=(0,0,1;0rad)
  Width = 21
FEATURE [Part::Cylinder] Cylinder027  label="removeToCreteHoleForPlugHousing012"
  Angle = 360
  AttacherType = Attacher::AttachEngine3D
  Height = 20
  Placement = pos=(-2,19,36) rot=(0,1,0;1.5708rad)
  Radius = 14.3
FEATURE [Part::Cut] Cut031  label="wireHolderBottomCaseBit001"
  Base = -> Box019
  Tool = -> Cylinder027
FEATURE [Part::MultiFuse] Fusion070  label="removeToCreteHoleForPlugHousing013"
  Shapes = -> [Box018,Cylinder026]
FEATURE [Part::Cut] Cut032  label="top016"
  Base = -> Cut029
  Tool = -> Fusion070
FEATURE [Part::Cylinder] Cylinder028
  Angle = 360
  AttacherType = Attacher::AttachEngine3D
  Height = 20
  Placement = pos=(0,0,36.15) rot=(0,0,1;0rad)
  Radius = 14.3
FEATURE [Part::Cylinder] Cylinder029
  Angle = 360
  AttacherType = Attacher::AttachEngine3D
  Height = 10
  Placement = pos=(0,0,36.15) rot=(0,0,1;0rad)
  Radius = 4
FEATURE [Part::MultiFuse] Fusion071  label="removeToCreteHoleForPlugHousing014"
  Placement = pos=(70,19,36) rot=(0,1,0;1.5708rad)
  Shapes = -> [Cylinder028,Cylinder029]
FEATURE [Sketcher::SketchObject] Sketch049  label="topSketch011"
  FullyConstrained = true
  sketch-geometry (4):
    g0: ArcOfCircle CenterX=105 CenterY=19 CenterZ=0 NormalX=0 NormalY=0 NormalZ=1 AngleXU=0 Radius=20.6155 StartAngle=5.54125 EndAngle=6.28319
    g1: ArcOfCircle CenterX=105 CenterY=19 CenterZ=0 NormalX=0 NormalY=0 NormalZ=1 AngleXU=0 Radius=13 StartAngle=5.54125 EndAngle=6.28319
    g2: LineSegment StartX=118 StartY=19 StartZ=0 EndX=125.616 EndY=19 EndZ=0
    g3: LineSegment StartX=114.583 StartY=10.2157 StartZ=0 EndX=120.197 EndY=5.06982 EndZ=0
  constraints (7):
    c: Block(g0)
    c: Block(g1)
    c: Coincident(g2,g1)
    c: Coincident(g2,g0)
    c: Horizontal(g2)
    c: Coincident(g3,g1)
    c: Coincident(g3,g0)
FEATURE [Part::Box] Box020  label="removeToCreteHoleForPlugHousing015"
  AttacherType = Attacher::AttachEngine3D
  Height = 28.6
  Length = 20
  Placement = pos=(106.15,0,21.7) rot=(0,0,1;0rad)
  Width = 19
FEATURE [Part::MultiFuse] Fusion072  label="removeToCreteHoleForPlugHousing016"
  Shapes = -> [Box020,Fusion071]
FEATURE [Part::Cut] Cut033  label="removeToCreteHoleForPlugHousing017"
  Base = -> Cut032
  Tool = -> Fusion072
FEATURE [Part::Cylinder] Cylinder030
  Angle = 360
  AttacherType = Attacher::AttachEngine3D
  Height = 20
  Placement = pos=(0,0,36.15) rot=(0,0,1;0rad)
  Radius = 14.3
FEATURE [Part::Cylinder] Cylinder031
  Angle = 360
  AttacherType = Attacher::AttachEngine3D
  Height = 10
  Placement = pos=(0,0,36.15) rot=(0,0,1;0rad)
  Radius = 4
FEATURE [Part::Box] Box021  label="removeToCreteHoleForPlugHousing019"
  AttacherType = Attacher::AttachEngine3D
  Height = 28.6
  Length = 20
  Placement = pos=(106.15,0,21.7) rot=(0,0,1;0rad)
  Width = 19
FEATURE [Part::MultiFuse] Fusion074  label="removeToCreteHoleForPlugHousing020"
  Placement = pos=(70,19,36) rot=(0,1,0;1.5708rad)
  Shapes = -> [Cylinder030,Cylinder031]
FEATURE [Part::MultiFuse] Fusion073  label="removeToCreteHoleForPlugHousing018"
  Placement = pos=(0,0,28.3) rot=(0,0,1;0rad)
  Shapes = -> [Box021,Fusion074]
FEATURE [Part::Cylinder] Cylinder032
  Angle = 360
  AttacherType = Attacher::AttachEngine3D
  Height = 20
  Placement = pos=(0,0,36.15) rot=(0,0,1;0rad)
  Radius = 14.3
FEATURE [Part::Cylinder] Cylinder033
  Angle = 360
  AttacherType = Attacher::AttachEngine3D
  Height = 10
  Placement = pos=(0,0,36.15) rot=(0,0,1;0rad)
  Radius = 4
FEATURE [Part::Box] Box022  label="removeToCreteHoleForPlugHousing021"
  AttacherType = Attacher::AttachEngine3D
  Height = 28.6
  Length = 20
  Placement = pos=(106.15,0,21.7) rot=(0,0,1;0rad)
  Width = 19
FEATURE [Part::MultiFuse] Fusion076  label="removeToCreteHoleForPlugHousing023"
  Placement = pos=(70,19,36) rot=(0,1,0;1.5708rad)
  Shapes = -> [Cylinder032,Cylinder033]
FEATURE [Part::MultiFuse] Fusion075  label="removeToCreteHoleForPlugHousing022"
  Placement = pos=(0,0,-28.3) rot=(0,0,1;0rad)
  Shapes = -> [Box022,Fusion076]
FEATURE [Part::MultiFuse] Fusion077  label="removeToCreatePlugHousingBottomBit"
  Shapes = -> [Fusion075,Fusion073]
FEATURE [Part::Cylinder] Cylinder034
  Angle = 360
  AttacherType = Attacher::AttachEngine3D
  Height = 20
  Placement = pos=(0,0,36.15) rot=(0,0,1;0rad)
  Radius = 14
FEATURE [Part::Cylinder] Cylinder035
  Angle = 360
  AttacherType = Attacher::AttachEngine3D
  Height = 10
  Placement = pos=(0,0,36.15) rot=(0,0,1;0rad)
  Radius = 4
FEATURE [Part::MultiFuse] Fusion078  label="removeToCreteHoleForPlugHousing024"
  Placement = pos=(70,19,36) rot=(0,1,0;1.5708rad)
  Shapes = -> [Cylinder034,Cylinder035]
FEATURE [Part::MultiFuse] Fusion079  label="removeToCreatePlugHousingBottomBit001"
  Shapes = -> [Fusion078,Fusion077]
FEATURE [Part::Extrusion] Extrude040  label="bottomPlugHousingBit"
  Base = -> Sketch049
  Dir = (0,0,1)
  DirMode = 2
  FaceMakerClass = Part::FaceMakerBullseye
  LengthFwd = 72
  LengthRev = 0
  Solid = true
  Symmetric = false
FEATURE [Part::Cut] Cut034  label="bottomPlugHousingBit001"
  Base = -> Extrude040
  Placement = pos=(-0.09,0,0) rot=(0,0,1;0rad)
  Tool = -> Fusion079
FEATURE [Part::Box] Box023  label="Cube014"
  AttacherType = Attacher::AttachEngine3D
  Height = 16
  Length = 8
  Placement = pos=(12.7,31.52,28) rot=(0,0,1;0rad)
  Width = 4
FEATURE [Part::Cylinder] Cylinder036
  Angle = 360
  AttacherType = Attacher::AttachEngine3D
  Height = 10
  Placement = pos=(0,0,36.15) rot=(0,0,1;0rad)
  Radius = 4
FEATURE [Part::Cylinder] Cylinder037
  Angle = 360
  AttacherType = Attacher::AttachEngine3D
  Height = 20
  Placement = pos=(0,0,36.15) rot=(0,0,1;0rad)
  Radius = 8.2
FEATURE [Part::MultiFuse] Fusion080  label="removeToCreteHoleForPlugHousing025"
  Placement = pos=(-42,19,36) rot=(0,1,0;1.5708rad)
  Shapes = -> [Cylinder037,Cylinder036]
FEATURE [Sketcher::SketchObject] Sketch050  label="topSketch012"
  FullyConstrained = true
  sketch-geometry (4):
    g0: LineSegment StartX=16.8446 StartY=31.512 StartZ=0 EndX=16.3251 EndY=34.4666 EndZ=0
    g1: ArcOfCircle CenterX=19 CenterY=19.2524 CenterZ=0 NormalX=0 NormalY=0 NormalZ=1 AngleXU=0 Radius=15.4476 StartAngle=1.74483 EndAngle=2.72717
    g2: ArcOfCircle CenterX=19 CenterY=19.2524 CenterZ=0 NormalX=0 NormalY=0 NormalZ=1 AngleXU=0 Radius=12.4476 StartAngle=1.74483 EndAngle=2.73189
    g3: LineSegment StartX=4.86004 StartY=25.4725 StartZ=0 EndX=7.58253 EndY=24.2107 EndZ=0
  constraints (7):
    c: Block(g0)
    c: Coincident(g1,g0)
    c: Coincident(g2,g0)
    c: Coincident(g3,g1)
    c: Coincident(g3,g2)
    c: Block(g1)
    c: Block(g2)
FEATURE [Part::Extrusion] Extrude041
  Base = -> Sketch050
  Dir = (0,0,1)
  DirMode = 2
  FaceMakerClass = Part::FaceMakerBullseye
  LengthFwd = 10.6
  LengthRev = 0
  Placement = pos=(0,0,31) rot=(0,0,1;0rad)
  Solid = true
  Symmetric = false
FEATURE [Part::Cut] Cut035
  Base = -> Extrude041
  Placement = pos=(0,0,-0.3) rot=(0,0,1;0rad)
  Tool = -> Fusion080
FEATURE [Part::Cut] Cut036
  Base = -> Box023
  Tool = -> Cut035
FEATURE [Part::Fillet] Fillet027
  Base = -> Cut036
  Edges = 1 edges r=0.7: [Edge13]
FEATURE [Part::Fillet] Fillet028
  Base = -> Fillet027
  Edges = 1 edges r=0.7: [Edge13]
FEATURE [Part::Fillet] Fillet029
  Base = -> Fillet028
  Edges = 1 edges r=0.7: [Edge16]
FEATURE [Part::Fillet] Fillet030
  Base = -> Fillet029
  Edges = 1 edges r=0.7: [Edge11]
FEATURE [Part::Fillet] Fillet031
  Base = -> Fillet030
  Edges = 1 edges r=0.7: [Edge10]
FEATURE [Part::Fillet] Fillet032
  Base = -> Fillet031
  Edges = 1 edges r=1.2: [Edge5]
FEATURE [Part::Fillet] Fillet033
  Base = -> Fillet032
  Edges = 1 edges r=1.2: [Edge12]
FEATURE [Part::Fillet] Fillet034  label="wireHousingRetainer"
  Base = -> Fillet033
  Edges = 1 edges r=2: [Edge1]
  Placement = pos=(0.3,0,0) rot=(0,0,1;0rad)
FEATURE [Part::Feature] Face099
  shape: bbox 3.5 x 17.8 x 2e-07 mm, 1 faces, 0 solids (baked)
FEATURE [Part::Revolution] Revolve107  label="removeToCreateScrewAndThreadedInsertHole034"
  Angle = 360
  Axis = (0,1,0)
  Base = (0,0,0)
  FaceMakerClass = Part::FaceMakerBullseye
  Placement = pos=(12.5,0,10) rot=(0,0,1;0rad)
  Solid = false
  Source = -> Face099
  Symmetric = false
FEATURE [Part::Feature] Face100
  shape: bbox 3.5 x 17.8 x 2e-07 mm, 1 faces, 0 solids (baked)
FEATURE [Part::Revolution] Revolve108  label="removeToCreateScrewAndThreadedInsertHole035"
  Angle = 360
  Axis = (0,1,0)
  Base = (0,0,0)
  FaceMakerClass = Part::FaceMakerBullseye
  Placement = pos=(12.5,0,62) rot=(0,0,1;0rad)
  Solid = false
  Source = -> Face100
  Symmetric = false
FEATURE [Part::Feature] Face101
  shape: bbox 3.5 x 17.8 x 2e-07 mm, 1 faces, 0 solids (baked)
FEATURE [Part::Revolution] Revolve109  label="removeToCreateScrewAndThreadedInsertHole036"
  Angle = 360
  Axis = (0,1,0)
  Base = (0,0,0)
  FaceMakerClass = Part::FaceMakerBullseye
  Placement = pos=(89.5,0,68.5) rot=(0,0,1;0rad)
  Solid = false
  Source = -> Face101
  Symmetric = false
FEATURE [Part::Feature] Face102
  shape: bbox 3.5 x 17.8 x 2e-07 mm, 1 faces, 0 solids (baked)
FEATURE [Part::Revolution] Revolve110  label="removeToCreateScrewAndThreadedInsertHole037"
  Angle = 360
  Axis = (0,1,0)
  Base = (0,0,0)
  FaceMakerClass = Part::FaceMakerBullseye
  Placement = pos=(89.5,0,3.5) rot=(0,0,1;0rad)
  Solid = false
  Source = -> Face102
  Symmetric = false
FEATURE [Part::Feature] Face103
  shape: bbox 3.5 x 17.8 x 2e-07 mm, 1 faces, 0 solids (baked)
FEATURE [Part::Revolution] Revolve111  label="removeToCreateScrewAndThreadedInsertHole038"
  Angle = 360
  Axis = (0,1,0)
  Base = (0,0,0)
  FaceMakerClass = Part::FaceMakerBullseye
  Placement = pos=(109.5,4.7,3.5) rot=(0,0,1;0rad)
  Solid = false
  Source = -> Face103
  Symmetric = false
FEATURE [Part::Feature] Face104
  shape: bbox 3.5 x 17.8 x 2e-07 mm, 1 faces, 0 solids (baked)
FEATURE [Part::Revolution] Revolve112  label="removeToCreateScrewAndThreadedInsertHole039"
  Angle = 360
  Axis = (0,1,0)
  Base = (0,0,0)
  FaceMakerClass = Part::FaceMakerBullseye
  Placement = pos=(109.5,4.7,68.5) rot=(0,0,1;0rad)
  Solid = false
  Source = -> Face104
  Symmetric = false
FEATURE [Part::MultiFuse] Fusion081  label="removeToCreateScrewAndThreadedInsertHole040"
  Shapes = -> [Revolve107,Revolve108,Revolve109,Revolve110,Revolve111,Revolve112]
FEATURE [Part::MultiFuse] Fusion082  label="casePillars002"
  Shapes = -> [Revolve094,Revolve092,Revolve090,Revolve089,Revolve091,Revolve093]
FEATURE [Part::Cut] Cut037  label="casePillars003"
  Base = -> Fusion082
  Tool = -> Fusion081
FEATURE [Sketcher::SketchObject] Sketch051
  FullyConstrained = true
  Placement = pos=(117,19,0) rot=(0.57735,0.57735,0.57735;2.0944rad)
  sketch-geometry (48):
    g0: LineSegment StartX=-49.19 StartY=69.25 StartZ=0 EndX=-49.19 EndY=66.25 EndZ=0
    g1: LineSegment StartX=-49.19 StartY=63.5 StartZ=0 EndX=-49.19 EndY=60.5 EndZ=0
    g2: LineSegment StartX=-49.19 StartY=57.75 StartZ=0 EndX=-49.19 EndY=54.75 EndZ=0
    g3: LineSegment StartX=-49.19 StartY=52 StartZ=0 EndX=-49.19 EndY=49 EndZ=0
    g4: LineSegment StartX=-49.19 StartY=46.25 StartZ=0 EndX=-49.19 EndY=43.25 EndZ=0
    g5: LineSegment StartX=-49.19 StartY=40.5 StartZ=0 EndX=-49.19 EndY=37.5 EndZ=0
    g6: LineSegment StartX=-49.19 StartY=34.5 StartZ=0 EndX=-49.19 EndY=31.5 EndZ=0
    g7: LineSegment StartX=-49.19 StartY=28.75 StartZ=0 EndX=-49.19 EndY=25.75 EndZ=0
    g8: LineSegment StartX=-49.19 StartY=23 StartZ=0 EndX=-49.19 EndY=20 EndZ=0
    g9: LineSegment StartX=-49.19 StartY=17.25 StartZ=0 EndX=-49.19 EndY=14.25 EndZ=0
    g10: LineSegment StartX=-49.19 StartY=11.5 StartZ=0 EndX=-49.19 EndY=8.5 EndZ=0
    g11: LineSegment StartX=-49.19 StartY=5.75 StartZ=0 EndX=-49.19 EndY=2.75 EndZ=0
    g12: ArcOfCircle CenterX=-1.5 CenterY=67.75 CenterZ=0 NormalX=0 NormalY=0 NormalZ=1 AngleXU=0 Radius=1.5 StartAngle=4.71239 EndAngle=7.85398
    g13: ArcOfCircle CenterX=-1.5 CenterY=62 CenterZ=0 NormalX=0 NormalY=0 NormalZ=1 AngleXU=0 Radius=1.5 StartAngle=4.71239 EndAngle=7.85398
    g14: ArcOfCircle CenterX=-1.5 CenterY=56.25 CenterZ=0 NormalX=0 NormalY=0 NormalZ=1 AngleXU=0 Radius=1.5 StartAngle=4.71239 EndAngle=7.85398
    g15: ArcOfCircle CenterX=-11.49 CenterY=50.5 CenterZ=0 NormalX=0 NormalY=0 NormalZ=1 AngleXU=0 Radius=1.5 StartAngle=4.71239 EndAngle=7.85398
    g16: ArcOfCircle CenterX=-16.28 CenterY=44.75 CenterZ=0 NormalX=0 NormalY=0 NormalZ=1 AngleXU=0 Radius=1.5 StartAngle=4.71239 EndAngle=7.85398
    g17: ArcOfCircle CenterX=-18.2337 CenterY=39 CenterZ=0 NormalX=0 NormalY=0 NormalZ=1 AngleXU=0 Radius=1.5 StartAngle=4.71485 EndAngle=7.85398
    g18: ArcOfCircle CenterX=-16.2837 CenterY=27.25 CenterZ=0 NormalX=0 NormalY=0 NormalZ=1 AngleXU=0 Radius=1.5 StartAngle=4.71485 EndAngle=7.85398
    g19: ArcOfCircle CenterX=-18.2337 CenterY=33 CenterZ=0 NormalX=0 NormalY=0 NormalZ=1 AngleXU=0 Radius=1.5 StartAngle=4.71485 EndAngle=7.85398
    g20: ArcOfCircle CenterX=-11.49 CenterY=21.5 CenterZ=0 NormalX=0 NormalY=0 NormalZ=1 AngleXU=0 Radius=1.5 StartAngle=4.71239 EndAngle=7.85398
    g21: ArcOfCircle CenterX=-1.5 CenterY=4.25 CenterZ=0 NormalX=0 NormalY=0 NormalZ=1 AngleXU=0 Radius=1.5 StartAngle=4.71239 EndAngle=7.85398
    g22: ArcOfCircle CenterX=-1.5 CenterY=10 CenterZ=0 NormalX=0 NormalY=0 NormalZ=1 AngleXU=0 Radius=1.5 StartAngle=4.71239 EndAngle=7.85398
    g23: ArcOfCircle CenterX=-1.5 CenterY=15.75 CenterZ=0 NormalX=0 NormalY=0 NormalZ=1 AngleXU=0 Radius=1.5 StartAngle=4.71239 EndAngle=7.85398
    g24: LineSegment StartX=-49.19 StartY=69.25 StartZ=0 EndX=-1.5 EndY=69.25 EndZ=0
    g25: LineSegment StartX=-49.19 StartY=66.25 StartZ=0 EndX=-1.5 EndY=66.25 EndZ=0
    g26: LineSegment StartX=-49.19 StartY=63.5 StartZ=0 EndX=-1.5 EndY=63.5 EndZ=0
    g27: LineSegment StartX=-49.19 StartY=60.5 StartZ=0 EndX=-1.5 EndY=60.5 EndZ=0
    g28: LineSegment StartX=-49.19 StartY=57.75 StartZ=0 EndX=-1.5 EndY=57.75 EndZ=0
    g29: LineSegment StartX=-49.19 StartY=54.75 StartZ=0 EndX=-1.5 EndY=54.75 EndZ=0
    g30: LineSegment StartX=-49.19 StartY=52 StartZ=0 EndX=-11.49 EndY=52 EndZ=0
    g31: LineSegment StartX=-49.19 StartY=49 StartZ=0 EndX=-11.49 EndY=49 EndZ=0
    g32: LineSegment StartX=-49.19 StartY=46.25 StartZ=0 EndX=-16.28 EndY=46.25 EndZ=0
    g33: LineSegment StartX=-49.19 StartY=43.25 StartZ=0 EndX=-16.28 EndY=43.25 EndZ=0
    g34: LineSegment StartX=-49.19 StartY=40.5 StartZ=0 EndX=-18.2337 EndY=40.5 EndZ=0
    g35: LineSegment StartX=-49.19 StartY=37.5 StartZ=0 EndX=-18.23 EndY=37.5 EndZ=0
    g36: LineSegment StartX=-49.19 StartY=34.5 StartZ=0 EndX=-18.2337 EndY=34.5 EndZ=0
    g37: LineSegment StartX=-49.19 StartY=31.5 StartZ=0 EndX=-18.23 EndY=31.5 EndZ=0
    g38: LineSegment StartX=-49.19 StartY=28.75 StartZ=0 EndX=-16.2837 EndY=28.75 EndZ=0
    g39: LineSegment StartX=-49.19 StartY=25.75 StartZ=0 EndX=-16.28 EndY=25.75 EndZ=0
    g40: LineSegment StartX=-49.19 StartY=23 StartZ=0 EndX=-11.49 EndY=23 EndZ=0
    g41: LineSegment StartX=-49.19 StartY=20 StartZ=0 EndX=-11.49 EndY=20 EndZ=0
    g42: LineSegment StartX=-49.19 StartY=17.25 StartZ=0 EndX=-1.5 EndY=17.25 EndZ=0
    g43: LineSegment StartX=-49.19 StartY=14.25 StartZ=0 EndX=-1.5 EndY=14.25 EndZ=0
    g44: LineSegment StartX=-49.19 StartY=11.5 StartZ=0 EndX=-1.5 EndY=11.5 EndZ=0
    g45: LineSegment StartX=-49.19 StartY=8.5 StartZ=0 EndX=-1.5 EndY=8.5 EndZ=0
    g46: LineSegment StartX=-49.19 StartY=5.75 StartZ=0 EndX=-1.5 EndY=5.75 EndZ=0
    g47: LineSegment StartX=-49.19 StartY=2.75 StartZ=0 EndX=-1.5 EndY=2.75 EndZ=0
  constraints (120):
    c: Vertical(g0)
    c: Distance(g0) = 3
    c: Block(g0)
    c: Vertical(g1)
    c: Distance(g1) = 3
    c: Vertical(g2)
    c: Equal(g0,g2) = 3
    c: Block(g2)
    c: Vertical(g3)
    c: Equal(g1,g3) = 3
    c: Vertical(g4)
    c: Equal(g0,g4) = 3
    c: Block(g4)
    c: Vertical(g5)
    c: Equal(g1,g5) = 3
    c: Vertical(g6)
    c: Equal(g0,g6) = 3
    c: Block(g6)
    c: Vertical(g7)
    c: Equal(g1,g7) = 3
    c: Vertical(g8)
    c: Equal(g0,g8) = 3
    c: Block(g8)
    c: Vertical(g9)
    c: Equal(g1,g9) = 3
    c: Vertical(g10)
    c: Equal(g0,g10) = 3
    c: Block(g10)
    c: Vertical(g11)
    c: Equal(g1,g11) = 3
    c: Block(g12)
    c: Block(g13)
    c: Block(g14)
    c: Block(g15)
    c: Block(g16)
    c: Block(g17)
    c: Block(g18)
    c: Block(g19)
    c: Block(g20)
    c: Block(g21)
    c: Block(g22)
    c: Block(g23)
    c: Block(g11)
    c: Block(g9)
    c: Block(g7)
    c: Block(g5)
    c: Block(g3)
    c: Block(g1)
    c: Coincident(g24,g0)
    c: Coincident(g24,g12)
    c: Horizontal(g24)
    c: Coincident(g25,g0)
    c: Coincident(g25,g12)
    c: Horizontal(g25)
    c: Coincident(g26,g1)
    c: Coincident(g26,g13)
    c: Horizontal(g26)
    c: Coincident(g27,g1)
    c: Coincident(g27,g13)
    c: Horizontal(g27)
    c: Coincident(g28,g2)
    c: Coincident(g28,g14)
    c: Horizontal(g28)
    c: Coincident(g29,g2)
    c: Coincident(g29,g14)
    c: Horizontal(g29)
    c: Coincident(g30,g3)
    c: Coincident(g30,g15)
    c: Horizontal(g30)
    c: Coincident(g31,g3)
    c: Coincident(g31,g15)
    c: Horizontal(g31)
    c: Coincident(g32,g4)
    c: Coincident(g32,g16)
    c: Horizontal(g32)
    c: Coincident(g33,g4)
    c: Coincident(g33,g16)
    c: Horizontal(g33)
    c: Coincident(g34,g5)
    c: Coincident(g34,g17)
    c: Horizontal(g34)
    c: Coincident(g35,g5)
    c: Coincident(g35,g17)
    c: Horizontal(g35)
    c: Coincident(g36,g6)
    c: Coincident(g36,g19)
    c: Horizontal(g36)
    c: Coincident(g37,g6)
    c: Coincident(g37,g19)
    c: Horizontal(g37)
    c: Coincident(g38,g7)
    c: Coincident(g38,g18)
    c: Horizontal(g38)
    c: Coincident(g39,g7)
    c: Coincident(g39,g18)
    c: Horizontal(g39)
    c: Coincident(g40,g8)
    c: Coincident(g40,g20)
    c: Horizontal(g40)
    c: Coincident(g41,g8)
    c: Coincident(g41,g20)
    c: Horizontal(g41)
    c: Coincident(g42,g9)
    c: Coincident(g42,g23)
    c: Horizontal(g42)
    c: Coincident(g43,g9)
    c: Coincident(g43,g23)
    c: Horizontal(g43)
    c: Coincident(g44,g10)
    c: Coincident(g44,g22)
    c: Horizontal(g44)
    c: Coincident(g45,g10)
    c: Coincident(g45,g22)
    c: Horizontal(g45)
    c: Coincident(g46,g11)
    c: Coincident(g46,g21)
    c: Horizontal(g46)
    c: Coincident(g47,g11)
    c: Coincident(g47,g21)
    c: Horizontal(g47)
FEATURE [Part::Extrusion] Extrude042
  Base = -> Sketch051
  Dir = (1,-2e-16,2e-16)
  DirMode = 2
  FaceMakerClass = Part::FaceMakerBullseye
  LengthFwd = 19
  LengthRev = 0
  Placement = pos=(-19,0,0) rot=(0,0,1;0rad)
  Solid = true
  Symmetric = false
FEATURE [Part::Fillet] Fillet035  label="removeToCreateVentalationHoles"
  Base = -> Extrude042
  Edges = <same value as first occurrence — deduplicated (x6 in doc)>
  Placement = pos=(7,0,0) rot=(0,0,1;0rad)
FEATURE [Part::Cut] Cut038  label="top017"
  Base = -> Cut033
  Tool = -> Fillet035
FEATURE [Sketcher::SketchObject] Sketch052  label="bottomSketch001"
  FullyConstrained = true
  sketch-geometry (45):
    g0: LineSegment StartX=6.29999 StartY=8 StartZ=0 EndX=3.29999 EndY=8 EndZ=0
    g1: LineSegment StartX=3.29999 StartY=8 StartZ=0 EndX=3.29999 EndY=-6.03275e-07 EndZ=0
    g2: ArcOfCircle CenterX=8.29999 CenterY=5 CenterZ=0 NormalX=0 NormalY=0 NormalZ=1 AngleXU=0 Radius=2 StartAngle=3.14159 EndAngle=4.71239
    g3: LineSegment StartX=6.29999 StartY=8 StartZ=0 EndX=6.29999 EndY=5 EndZ=0
    g4: ArcOfCircle CenterX=105 CenterY=19 CenterZ=0 NormalX=0 NormalY=0 NormalZ=1 AngleXU=0 Radius=12.7 StartAngle=4.71239 EndAngle=5.94289
    g5-g11: Circle x7 (B-spline internal-alignment scaffolding for g12; pole/knot coordinates omitted)
    g12: BSplineCurve PolesCount=7 KnotsCount=5 Degree=3 IsPeriodic=0
    g13-g17: GeomPoint x5 (B-spline internal-alignment scaffolding for g12; pole/knot coordinates omitted)
    g18: ArcOfCircle CenterX=105 CenterY=19 CenterZ=0 NormalX=0 NormalY=0 NormalZ=1 AngleXU=0 Radius=15.7 StartAngle=5.81226 EndAngle=6.28319
    g19: BSplineCurve PolesCount=5 KnotsCount=3 Degree=3 IsPeriodic=0
    g20: LineSegment StartX=8.29999 StartY=3 StartZ=0 EndX=101.7 EndY=3 EndZ=0
    g21: LineSegment StartX=3.29999 StartY=-6.03275e-07 StartZ=0 EndX=105 EndY=-6.03275e-07 EndZ=0
    g22: LineSegment StartX=120.974 StartY=8.71251 StartZ=0 EndX=122.332 EndY=7.83778 EndZ=0
    g23: LineSegment StartX=105 StartY=-6.03274e-07 StartZ=0 EndX=113 EndY=-6.03274e-07 EndZ=0
    g24: ArcOfCircle CenterX=105 CenterY=19 CenterZ=0 NormalX=0 NormalY=0 NormalZ=1 AngleXU=0 Radius=20.6155 StartAngle=5.11091 EndAngle=5.71103
    g25: ArcOfCircle CenterX=117.7 CenterY=19 CenterZ=0 NormalX=0 NormalY=0 NormalZ=1 AngleXU=0 Radius=3 StartAngle=1.2e-15 EndAngle=2.10468
    g26: Circle CenterX=116.345 CenterY=16.3232 CenterZ=0 NormalX=0 NormalY=0 NormalZ=1 AngleXU=0 Radius=1
    g27: Circle CenterX=117.24 CenterY=15.7584 CenterZ=0 NormalX=0 NormalY=0 NormalZ=1 AngleXU=0 Radius=1
    g28: Circle CenterX=116.972 CenterY=14.7612 CenterZ=0 NormalX=0 NormalY=0 NormalZ=1 AngleXU=0 Radius=1
    g29: BSplineCurve PolesCount=3 KnotsCount=2 Degree=2 IsPeriodic=0
    g30: GeomPoint X=116.345 Y=16.3232 Z=0
    g31: GeomPoint X=116.972 Y=14.7612 Z=0
    g32: Circle CenterX=115.828 CenterY=17.157 CenterZ=0 NormalX=0 NormalY=0 NormalZ=1 AngleXU=0 Radius=1
    g33: Circle CenterX=115.841 CenterY=16.639 CenterZ=0 NormalX=0 NormalY=0 NormalZ=1 AngleXU=0 Radius=1
    g34: Circle CenterX=116.345 CenterY=16.3232 CenterZ=0 NormalX=0 NormalY=0 NormalZ=1 AngleXU=0 Radius=1
    g35: BSplineCurve PolesCount=3 KnotsCount=2 Degree=2 IsPeriodic=0
    g36: GeomPoint X=115.828 Y=17.157 Z=0
    g37: GeomPoint X=116.345 Y=16.3232 Z=0
    g38: LineSegment StartX=115.828 StartY=17.157 StartZ=0 EndX=115.828 EndY=20.8307 EndZ=0
    g39: Circle CenterX=115.828 CenterY=20.8307 CenterZ=0 NormalX=0 NormalY=0 NormalZ=1 AngleXU=0 Radius=1
    g40: Circle CenterX=115.831 CenterY=21.3396 CenterZ=0 NormalX=0 NormalY=0 NormalZ=1 AngleXU=0 Radius=1
    g41: Circle CenterX=116.173 CenterY=21.5825 CenterZ=0 NormalX=0 NormalY=0 NormalZ=1 AngleXU=0 Radius=1
    g42: BSplineCurve PolesCount=3 KnotsCount=2 Degree=2 IsPeriodic=0
    g43: GeomPoint X=115.828 Y=20.8307 Z=0
    g44: GeomPoint X=116.173 Y=21.5825 Z=0
  constraints (70):
    c: Horizontal(g0)
    c: Distance(g0) = 3
    c: Coincident(g1,g0)
    c: Vertical(g1)
    c: Block(g2)
    c: Block(g0)
    c: Coincident(g3,g0)
    c: Coincident(g3,g2)
    c: Vertical(g3)
    c: Block(g1)
    c: Block(g4)
    c: Coincident(g19,g4)
    c: Block(g19)
    c: Equal(g5, g6-g11) x6
    c: InternalAlignment(g5-g11 -> g12) x7
    c: InternalAlignment(g13-g17 -> g12) x5
    c: Block(g12)
    c: Coincident(g18,g12)
    c: Block(g18)
    c: Coincident(g20,g2)
    c: Coincident(g20,g19)
    c: Horizontal(g20)
    c: Distance(g20) = 93.4
    c: Coincident(g21,g1)
    c: Horizontal(g21)
    c: Distance(g21) = 101.7
    c: Horizontal(g23)
    c: Distance(g23) = 8
    c: Coincident(g24,g23)
    c: Block(g23)
    c: Coincident(g22,g24)
    c: Block(g24)
    c: Block(g22)
    c: Distance(g22) = 1.61553
    c: Coincident(g25,g18)
    c: Block(g25)
    c: Weight(g26) = 1
    c: Equal(g26,g27)
    c: Equal(g26,g28)
    c: Coincident(g29,g4)
    c: InternalAlignment(g26,g29)
    c: InternalAlignment(g27,g29)
    c: InternalAlignment(g28,g29)
    c: InternalAlignment(g30,g29)
    c: InternalAlignment(g31,g29)
    c: Block(g29)
    c: Weight(g32) = 1
    c: Equal(g32,g33)
    c: Equal(g32,g34)
    c: Coincident(g35,g29)
    c: InternalAlignment(g32,g35)
    c: InternalAlignment(g33,g35)
    c: InternalAlignment(g34,g35)
    c: InternalAlignment(g36,g35)
    c: InternalAlignment(g37,g35)
    c: Block(g35)
    c: Coincident(g38,g35)
    c: Vertical(g38)
    c: Block(g38)
    c: Coincident(g42,g38)
    c: Weight(g39) = 1
    c: Equal(g39,g40)
    c: Equal(g39,g41)
    c: Coincident(g42,g25)
    c: InternalAlignment(g39,g42)
    c: InternalAlignment(g40,g42)
    c: InternalAlignment(g41,g42)
    c: InternalAlignment(g43,g42)
    c: InternalAlignment(g44,g42)
    c: Block(g42)
FEATURE [Part::Extrusion] Extrude043  label="bottom010"
  Base = -> Sketch052
  Dir = (0,0,1)
  DirMode = 2
  FaceMakerClass = Part::FaceMakerBullseye
  LengthFwd = 71.4
  LengthRev = 0
  Placement = pos=(0,0,0.3) rot=(0,0,1;0rad)
  Solid = true
  Symmetric = false
FEATURE [Sketcher::SketchObject] Sketch053  label="topSketch013"
  FullyConstrained = true
  sketch-geometry (22):
    g0: LineSegment StartX=5.21097e-06 StartY=3 StartZ=0 EndX=5.21097e-06 EndY=19 EndZ=0
    g1: ArcOfCircle CenterX=19 CenterY=19 CenterZ=0 NormalX=0 NormalY=0 NormalZ=1 AngleXU=0 Radius=19 StartAngle=1.5708 EndAngle=3.14159
    g2: ArcOfCircle CenterX=19 CenterY=19 CenterZ=0 NormalX=0 NormalY=0 NormalZ=1 AngleXU=0 Radius=16 StartAngle=1.5708 EndAngle=3.14159
    g3: LineSegment StartX=114 StartY=35 StartZ=0 EndX=19 EndY=35 EndZ=0
    g4: LineSegment StartX=5.21097e-06 StartY=3 StartZ=0 EndX=5.21097e-06 EndY=0 EndZ=0
    g5: LineSegment StartX=3 StartY=0 StartZ=0 EndX=5.21097e-06 EndY=0 EndZ=0
    g6: LineSegment StartX=3 StartY=19 StartZ=0 EndX=3 EndY=0 EndZ=0
    g7: LineSegment StartX=19 StartY=38 StartZ=0 EndX=124 EndY=38 EndZ=0
    g8: Circle CenterX=119 CenterY=35 CenterZ=0 NormalX=0 NormalY=0 NormalZ=1 AngleXU=0 Radius=1
    g9: Circle CenterX=121 CenterY=35 CenterZ=0 NormalX=0 NormalY=0 NormalZ=1 AngleXU=0 Radius=1
    g10: Circle CenterX=121 CenterY=33 CenterZ=0 NormalX=0 NormalY=0 NormalZ=1 AngleXU=0 Radius=1
    g11: BSplineCurve PolesCount=3 KnotsCount=2 Degree=2 IsPeriodic=0
    g12: GeomPoint X=119 Y=35 Z=0
    g13: GeomPoint X=121 Y=33 Z=0
    g14: LineSegment StartX=119 StartY=35 StartZ=0 EndX=114 EndY=35 EndZ=0
    g15: ArcOfCircle CenterX=105 CenterY=19 CenterZ=0 NormalX=0 NormalY=0 NormalZ=1 AngleXU=0 Radius=16 StartAngle=5.60905 EndAngle=6.28319
    g16: LineSegment StartX=121 StartY=33 StartZ=0 EndX=121 EndY=19 EndZ=0
    g17: LineSegment StartX=117.5 StartY=9.01251 StartZ=0 EndX=121.163 EndY=9.0125 EndZ=0
    g18: ArcOfCircle CenterX=105 CenterY=19 CenterZ=0 NormalX=0 NormalY=0 NormalZ=1 AngleXU=0 Radius=20.6155 StartAngle=5.7297 EndAngle=6.28319
    g19: LineSegment StartX=121.163 StartY=9.0125 StartZ=0 EndX=122.538 EndY=8.16329 EndZ=0
    g20: LineSegment StartX=124 StartY=38 StartZ=0 EndX=125.616 EndY=38 EndZ=0
    g21: LineSegment StartX=125.616 StartY=19 StartZ=0 EndX=125.616 EndY=38 EndZ=0
  constraints (50):
    c: Vertical(g0)
    c: Block(g0)
    c: Coincident(g1,g0)
    c: Block(g1)
    c: Coincident(g2,g1)
    c: Block(g2)
    c: Coincident(g3,g2)
    c: Horizontal(g3)
    c: Tangent(g3,g2)
    c: Coincident(g4,g0)
    c: Distance(g4) = 3
    c: Vertical(g4)
    c: Coincident(g5,g4)
    c: Horizontal(g5)
    c: Coincident(g6,g2)
    c: Coincident(g6,g5)
    c: Vertical(g6)
    c: Horizontal(g7)
    c: Distance(g7) = 105
    c: Coincident(g7,g1)
    c: Block(g3)
    c: Weight(g8) = 1
    c: Equal(g8,g9)
    c: Equal(g8,g10)
    c: InternalAlignment(g8,g11)
    c: InternalAlignment(g9,g11)
    c: InternalAlignment(g10,g11)
    c: InternalAlignment(g12,g11)
    c: InternalAlignment(g13,g11)
    c: Block(g11)
    c: Coincident(g14,g11)
    c: Coincident(g14,g3)
    c: Horizontal(g14)
    c: Block(g15)
    c: Coincident(g16,g11)
    c: Coincident(g16,g15)
    c: Vertical(g16)
    c: Distance(g16) = 14
    c: Coincident(g17,g15)
    c: Block(g18)
    c: Coincident(g19,g18)
    c: Coincident(g20,g7)
    c: Horizontal(g20)
    c: Vertical(g21)
    c: Coincident(g20,g21)
    c: Block(g20)
    c: Block(g21)
    c: Block(g19)
    c: Block(g17)
    c: Distance(g20) = 1.61553
FEATURE [Part::Extrusion] Extrude044
  Base = -> Sketch053
  Dir = (0,0,1)
  DirMode = 2
  FaceMakerClass = Part::FaceMakerBullseye
  LengthFwd = 72
  LengthRev = 0
  Solid = true
  Symmetric = false
FEATURE [Part::Fillet] Fillet036  label="top018"
  Base = -> Extrude044
  Edges = 1 edges r=2: [Edge41]
FEATURE [Sketcher::SketchObject] Sketch054
  FullyConstrained = false
  Placement = pos=(0,0,0) rot=(1,0,0;1.5708rad)
  sketch-geometry (24):
    g0: ArcOfCircle CenterX=-4 CenterY=-10.5 CenterZ=0 NormalX=0 NormalY=0 NormalZ=1 AngleXU=0 Radius=1.5 StartAngle=6e-16 EndAngle=3.14159
    g1: ArcOfCircle CenterX=-34.2 CenterY=-10.5 CenterZ=0 NormalX=0 NormalY=0 NormalZ=1 AngleXU=0 Radius=1.5 StartAngle=0 EndAngle=3.14159
    g2: ArcOfCircle CenterX=-34.2 CenterY=-27.7 CenterZ=0 NormalX=0 NormalY=0 NormalZ=1 AngleXU=0 Radius=1.5 StartAngle=3.14159 EndAngle=6.28319
    g3: ArcOfCircle CenterX=-4 CenterY=-27.7 CenterZ=0 NormalX=0 NormalY=0 NormalZ=1 AngleXU=0 Radius=1.5 StartAngle=3.1416 EndAngle=6.28319
    g4: ArcOfCircle CenterX=-10 CenterY=-4.3 CenterZ=0 NormalX=0 NormalY=0 NormalZ=1 AngleXU=0 Radius=1.5 StartAngle=2e-16 EndAngle=3.14159
    g5: ArcOfCircle CenterX=-16.1 CenterY=-1.8 CenterZ=0 NormalX=0 NormalY=0 NormalZ=1 AngleXU=0 Radius=1.5 StartAngle=5e-16 EndAngle=3.14159
    g6: ArcOfCircle CenterX=-22.1 CenterY=-1.8 CenterZ=0 NormalX=0 NormalY=0 NormalZ=1 AngleXU=0 Radius=1.5 StartAngle=5e-16 EndAngle=3.14159
    g7: ArcOfCircle CenterX=-28.2 CenterY=-4.3 CenterZ=0 NormalX=0 NormalY=0 NormalZ=1 AngleXU=0 Radius=1.5 StartAngle=2e-16 EndAngle=3.14159
    g8: ArcOfCircle CenterX=-10 CenterY=-33.9 CenterZ=0 NormalX=0 NormalY=0 NormalZ=1 AngleXU=0 Radius=1.5 StartAngle=3.14159 EndAngle=6.28319
    g9: ArcOfCircle CenterX=-16.1 CenterY=-36.4 CenterZ=0 NormalX=0 NormalY=0 NormalZ=1 AngleXU=0 Radius=1.5 StartAngle=3.14159 EndAngle=6.28319
    g10: ArcOfCircle CenterX=-22.1 CenterY=-36.4 CenterZ=0 NormalX=0 NormalY=0 NormalZ=1 AngleXU=0 Radius=1.5 StartAngle=3.14159 EndAngle=6.28319
    g11: ArcOfCircle CenterX=-28.2 CenterY=-33.9 CenterZ=0 NormalX=0 NormalY=0 NormalZ=1 AngleXU=0 Radius=1.5 StartAngle=3.14159 EndAngle=6.28319
    g12: LineSegment StartX=-35.7 StartY=-10.5 StartZ=0 EndX=-35.7 EndY=-27.7 EndZ=0
    g13: LineSegment StartX=-32.7 StartY=-10.5 StartZ=0 EndX=-32.7 EndY=-27.7 EndZ=0
    g14: LineSegment StartX=-29.7 StartY=-33.9 StartZ=0 EndX=-29.7 EndY=-4.3 EndZ=0
    g15: LineSegment StartX=-26.7 StartY=-33.9 StartZ=0 EndX=-26.7 EndY=-4.3 EndZ=0
    g16: LineSegment StartX=-2.5 StartY=-10.5 StartZ=0 EndX=-2.5 EndY=-27.7 EndZ=0
    g17: LineSegment StartX=-8.5 StartY=-4.3 StartZ=0 EndX=-8.5 EndY=-33.9 EndZ=0
    g18: LineSegment StartX=-5.5 StartY=-10.5 StartZ=0 EndX=-5.5 EndY=-27.7 EndZ=0
    g19: LineSegment StartX=-11.5 StartY=-4.3 StartZ=0 EndX=-11.5 EndY=-33.9 EndZ=0
    g20: LineSegment StartX=-14.6 StartY=-1.8 StartZ=0 EndX=-14.6 EndY=-36.4 EndZ=0
    g21: LineSegment StartX=-17.6 StartY=-1.8 StartZ=0 EndX=-17.6 EndY=-36.4 EndZ=0
    g22: LineSegment StartX=-20.6 StartY=-36.4 StartZ=0 EndX=-20.6 EndY=-1.8 EndZ=0
    g23: LineSegment StartX=-23.6 StartY=-1.8 StartZ=0 EndX=-23.6 EndY=-36.4 EndZ=0
  constraints (48):
    c: Block(g0)
    c: Block(g1)
    c: Block(g2)
    c: Block(g3)
    c: Block(g4)
    c: Block(g5)
    c: Block(g6)
    c: Block(g7)
    c: Block(g8)
    c: Block(g9)
    c: Block(g10)
    c: Block(g11)
    c: Coincident(g12,g1)
    c: Coincident(g12,g2)
    c: Vertical(g12)
    c: Coincident(g13,g1)
    c: Coincident(g13,g2)
    c: Vertical(g13)
    c: Coincident(g14,g11)
    c: Coincident(g14,g7)
    c: Vertical(g14)
    c: Coincident(g15,g11)
    c: Coincident(g15,g7)
    c: Vertical(g15)
    c: Coincident(g16,g0)
    c: Coincident(g16,g3)
    c: Vertical(g16)
    c: Coincident(g17,g4)
    c: Coincident(g17,g8)
    c: Vertical(g17)
    c: Coincident(g18,g0)
    c: Coincident(g18,g3)
    c: Vertical(g18)
    c: Coincident(g19,g4)
    c: Coincident(g19,g8)
    c: Vertical(g19)
    c: Coincident(g20,g5)
    c: Coincident(g20,g9)
    c: Vertical(g20)
    c: Coincident(g21,g5)
    c: Coincident(g21,g9)
    c: Vertical(g21)
    c: Coincident(g22,g10)
    c: Coincident(g22,g6)
    c: Vertical(g22)
    c: Coincident(g23,g6)
    c: Coincident(g23,g10)
    c: Vertical(g23)
FEATURE [Part::Extrusion] Extrude045  label="removeToCreateFanGrillHoles003"
  Base = -> Sketch054
  Dir = (0,-1,6e-16)
  DirMode = 2
  FaceMakerClass = Part::FaceMakerBullseye
  LengthFwd = 10
  LengthRev = 0
  Placement = pos=(65.4,44,54.82) rot=(0,0,1;0rad)
  Solid = true
  Symmetric = false
FEATURE [Part::Feature] Face105 .. Face108  x4 (patterned run collapsed; names and placements below)
  shape: bbox 3.5 x 17.8 x 2e-07 mm, 1 faces, 0 solids (baked)
FEATURE [Part::Revolution] Revolve113  label="removeToCreateScrewAndThreadedInsertHole041"
  Angle = 360
  Axis = (0,1,0)
  Base = (0,0,0)
  FaceMakerClass = Part::FaceMakerBullseye
  Placement = pos=(62.3,30.3,19.7) rot=(0,0,1;0rad)
  Solid = false
  Source = -> Face105
  Symmetric = false
FEATURE [Part::Revolution] Revolve114  label="removeToCreateScrewAndThreadedInsertHole042"
  Angle = 360
  Axis = (0,1,0)
  Base = (0,0,0)
  FaceMakerClass = Part::FaceMakerBullseye
  Placement = pos=(62.3,30.3,51.7) rot=(0,0,1;0rad)
  Solid = false
  Source = -> Face106
  Symmetric = false
FEATURE [Part::Revolution] Revolve115  label="removeToCreateScrewAndThreadedInsertHole043"
  Angle = 360
  Axis = (0,1,0)
  Base = (0,0,0)
  FaceMakerClass = Part::FaceMakerBullseye
  Placement = pos=(30.3,30.3,19.7) rot=(0,0,1;0rad)
  Solid = false
  Source = -> Face107
  Symmetric = false
FEATURE [Part::Revolution] Revolve116  label="removeToCreateScrewAndThreadedInsertHole044"
  Angle = 360
  Axis = (0,1,0)
  Base = (0,0,0)
  FaceMakerClass = Part::FaceMakerBullseye
  Placement = pos=(30.3,30.3,51.7) rot=(0,0,1;0rad)
  Solid = false
  Source = -> Face108
  Symmetric = false
FEATURE [Part::MultiFuse] Fusion083  label="createThreadedInsertHolesForFan004"
  Shapes = -> [Revolve113,Revolve114,Revolve115,Revolve116]
FEATURE [Part::Box] Box024  label="removeToCreteHoleForPlugHousing026"
  AttacherType = Attacher::AttachEngine3D
  Height = 28.6
  Length = 10
  Placement = pos=(-2,0,21.7) rot=(0,0,1;0rad)
  Width = 19
FEATURE [Part::Cylinder] Cylinder038  label="removeToCreteHoleForPlugHousing027"
  Angle = 360
  AttacherType = Attacher::AttachEngine3D
  Height = 20
  Placement = pos=(-2,19,36) rot=(0,1,0;1.5708rad)
  Radius = 14.3
FEATURE [Part::MultiFuse] Fusion084  label="removeToCreteHoleForPlugHousing028"
  Shapes = -> [Box024,Cylinder038]
FEATURE [Part::Cylinder] Cylinder039
  Angle = 360
  AttacherType = Attacher::AttachEngine3D
  Height = 20
  Placement = pos=(0,0,36.15) rot=(0,0,1;0rad)
  Radius = 14.3
FEATURE [Part::Cylinder] Cylinder040
  Angle = 360
  AttacherType = Attacher::AttachEngine3D
  Height = 10
  Placement = pos=(0,0,36.15) rot=(0,0,1;0rad)
  Radius = 4
FEATURE [Part::Box] Box025  label="removeToCreteHoleForPlugHousing030"
  AttacherType = Attacher::AttachEngine3D
  Height = 28.6
  Length = 20
  Placement = pos=(106.15,0,21.7) rot=(0,0,1;0rad)
  Width = 19
FEATURE [Part::MultiFuse] Fusion086  label="removeToCreteHoleForPlugHousing031"
  Placement = pos=(70,19,36) rot=(0,1,0;1.5708rad)
  Shapes = -> [Cylinder039,Cylinder040]
FEATURE [Part::MultiFuse] Fusion085  label="removeToCreteHoleForPlugHousing029"
  Shapes = -> [Box025,Fusion086]
FEATURE [Sketcher::SketchObject] Sketch055
  FullyConstrained = true
  Placement = pos=(117,19,0) rot=(0.57735,0.57735,0.57735;2.0944rad)
  sketch-geometry (48):
    g0: LineSegment StartX=-49.19 StartY=69.25 StartZ=0 EndX=-49.19 EndY=66.25 EndZ=0
    g1: LineSegment StartX=-49.19 StartY=63.5 StartZ=0 EndX=-49.19 EndY=60.5 EndZ=0
    g2: LineSegment StartX=-49.19 StartY=57.75 StartZ=0 EndX=-49.19 EndY=54.75 EndZ=0
    g3: LineSegment StartX=-49.19 StartY=52 StartZ=0 EndX=-49.19 EndY=49 EndZ=0
    g4: LineSegment StartX=-49.19 StartY=46.25 StartZ=0 EndX=-49.19 EndY=43.25 EndZ=0
    g5: LineSegment StartX=-49.19 StartY=40.5 StartZ=0 EndX=-49.19 EndY=37.5 EndZ=0
    g6: LineSegment StartX=-49.19 StartY=34.5 StartZ=0 EndX=-49.19 EndY=31.5 EndZ=0
    g7: LineSegment StartX=-49.19 StartY=28.75 StartZ=0 EndX=-49.19 EndY=25.75 EndZ=0
    g8: LineSegment StartX=-49.19 StartY=23 StartZ=0 EndX=-49.19 EndY=20 EndZ=0
    g9: LineSegment StartX=-49.19 StartY=17.25 StartZ=0 EndX=-49.19 EndY=14.25 EndZ=0
    g10: LineSegment StartX=-49.19 StartY=11.5 StartZ=0 EndX=-49.19 EndY=8.5 EndZ=0
    g11: LineSegment StartX=-49.19 StartY=5.75 StartZ=0 EndX=-49.19 EndY=2.75 EndZ=0
    g12: ArcOfCircle CenterX=-1.5 CenterY=67.75 CenterZ=0 NormalX=0 NormalY=0 NormalZ=1 AngleXU=0 Radius=1.5 StartAngle=4.71239 EndAngle=7.85398
    g13: ArcOfCircle CenterX=-1.5 CenterY=62 CenterZ=0 NormalX=0 NormalY=0 NormalZ=1 AngleXU=0 Radius=1.5 StartAngle=4.71239 EndAngle=7.85398
    g14: ArcOfCircle CenterX=-1.5 CenterY=56.25 CenterZ=0 NormalX=0 NormalY=0 NormalZ=1 AngleXU=0 Radius=1.5 StartAngle=4.71239 EndAngle=7.85398
    g15: ArcOfCircle CenterX=-11.49 CenterY=50.5 CenterZ=0 NormalX=0 NormalY=0 NormalZ=1 AngleXU=0 Radius=1.5 StartAngle=4.71239 EndAngle=7.85398
    g16: ArcOfCircle CenterX=-16.28 CenterY=44.75 CenterZ=0 NormalX=0 NormalY=0 NormalZ=1 AngleXU=0 Radius=1.5 StartAngle=4.71239 EndAngle=7.85398
    g17: ArcOfCircle CenterX=-18.2337 CenterY=39 CenterZ=0 NormalX=0 NormalY=0 NormalZ=1 AngleXU=0 Radius=1.5 StartAngle=4.71485 EndAngle=7.85398
    g18: ArcOfCircle CenterX=-16.2837 CenterY=27.25 CenterZ=0 NormalX=0 NormalY=0 NormalZ=1 AngleXU=0 Radius=1.5 StartAngle=4.71485 EndAngle=7.85398
    g19: ArcOfCircle CenterX=-18.2337 CenterY=33 CenterZ=0 NormalX=0 NormalY=0 NormalZ=1 AngleXU=0 Radius=1.5 StartAngle=4.71485 EndAngle=7.85398
    g20: ArcOfCircle CenterX=-11.49 CenterY=21.5 CenterZ=0 NormalX=0 NormalY=0 NormalZ=1 AngleXU=0 Radius=1.5 StartAngle=4.71239 EndAngle=7.85398
    g21: ArcOfCircle CenterX=-1.5 CenterY=4.25 CenterZ=0 NormalX=0 NormalY=0 NormalZ=1 AngleXU=0 Radius=1.5 StartAngle=4.71239 EndAngle=7.85398
    g22: ArcOfCircle CenterX=-1.5 CenterY=10 CenterZ=0 NormalX=0 NormalY=0 NormalZ=1 AngleXU=0 Radius=1.5 StartAngle=4.71239 EndAngle=7.85398
    g23: ArcOfCircle CenterX=-1.5 CenterY=15.75 CenterZ=0 NormalX=0 NormalY=0 NormalZ=1 AngleXU=0 Radius=1.5 StartAngle=4.71239 EndAngle=7.85398
    g24: LineSegment StartX=-49.19 StartY=69.25 StartZ=0 EndX=-1.5 EndY=69.25 EndZ=0
    g25: LineSegment StartX=-49.19 StartY=66.25 StartZ=0 EndX=-1.5 EndY=66.25 EndZ=0
    g26: LineSegment StartX=-49.19 StartY=63.5 StartZ=0 EndX=-1.5 EndY=63.5 EndZ=0
    g27: LineSegment StartX=-49.19 StartY=60.5 StartZ=0 EndX=-1.5 EndY=60.5 EndZ=0
    g28: LineSegment StartX=-49.19 StartY=57.75 StartZ=0 EndX=-1.5 EndY=57.75 EndZ=0
    g29: LineSegment StartX=-49.19 StartY=54.75 StartZ=0 EndX=-1.5 EndY=54.75 EndZ=0
    g30: LineSegment StartX=-49.19 StartY=52 StartZ=0 EndX=-11.49 EndY=52 EndZ=0
    g31: LineSegment StartX=-49.19 StartY=49 StartZ=0 EndX=-11.49 EndY=49 EndZ=0
    g32: LineSegment StartX=-49.19 StartY=46.25 StartZ=0 EndX=-16.28 EndY=46.25 EndZ=0
    g33: LineSegment StartX=-49.19 StartY=43.25 StartZ=0 EndX=-16.28 EndY=43.25 EndZ=0
    g34: LineSegment StartX=-49.19 StartY=40.5 StartZ=0 EndX=-18.2337 EndY=40.5 EndZ=0
    g35: LineSegment StartX=-49.19 StartY=37.5 StartZ=0 EndX=-18.23 EndY=37.5 EndZ=0
    g36: LineSegment StartX=-49.19 StartY=34.5 StartZ=0 EndX=-18.2337 EndY=34.5 EndZ=0
    g37: LineSegment StartX=-49.19 StartY=31.5 StartZ=0 EndX=-18.23 EndY=31.5 EndZ=0
    g38: LineSegment StartX=-49.19 StartY=28.75 StartZ=0 EndX=-16.2837 EndY=28.75 EndZ=0
    g39: LineSegment StartX=-49.19 StartY=25.75 StartZ=0 EndX=-16.28 EndY=25.75 EndZ=0
    g40: LineSegment StartX=-49.19 StartY=23 StartZ=0 EndX=-11.49 EndY=23 EndZ=0
    g41: LineSegment StartX=-49.19 StartY=20 StartZ=0 EndX=-11.49 EndY=20 EndZ=0
    g42: LineSegment StartX=-49.19 StartY=17.25 StartZ=0 EndX=-1.5 EndY=17.25 EndZ=0
    g43: LineSegment StartX=-49.19 StartY=14.25 StartZ=0 EndX=-1.5 EndY=14.25 EndZ=0
    g44: LineSegment StartX=-49.19 StartY=11.5 StartZ=0 EndX=-1.5 EndY=11.5 EndZ=0
    g45: LineSegment StartX=-49.19 StartY=8.5 StartZ=0 EndX=-1.5 EndY=8.5 EndZ=0
    g46: LineSegment StartX=-49.19 StartY=5.75 StartZ=0 EndX=-1.5 EndY=5.75 EndZ=0
    g47: LineSegment StartX=-49.19 StartY=2.75 StartZ=0 EndX=-1.5 EndY=2.75 EndZ=0
  constraints (120):
    c: Vertical(g0)
    c: Distance(g0) = 3
    c: Block(g0)
    c: Vertical(g1)
    c: Distance(g1) = 3
    c: Vertical(g2)
    c: Equal(g0,g2) = 3
    c: Block(g2)
    c: Vertical(g3)
    c: Equal(g1,g3) = 3
    c: Vertical(g4)
    c: Equal(g0,g4) = 3
    c: Block(g4)
    c: Vertical(g5)
    c: Equal(g1,g5) = 3
    c: Vertical(g6)
    c: Equal(g0,g6) = 3
    c: Block(g6)
    c: Vertical(g7)
    c: Equal(g1,g7) = 3
    c: Vertical(g8)
    c: Equal(g0,g8) = 3
    c: Block(g8)
    c: Vertical(g9)
    c: Equal(g1,g9) = 3
    c: Vertical(g10)
    c: Equal(g0,g10) = 3
    c: Block(g10)
    c: Vertical(g11)
    c: Equal(g1,g11) = 3
    c: Block(g12)
    c: Block(g13)
    c: Block(g14)
    c: Block(g15)
    c: Block(g16)
    c: Block(g17)
    c: Block(g18)
    c: Block(g19)
    c: Block(g20)
    c: Block(g21)
    c: Block(g22)
    c: Block(g23)
    c: Block(g11)
    c: Block(g9)
    c: Block(g7)
    c: Block(g5)
    c: Block(g3)
    c: Block(g1)
    c: Coincident(g24,g0)
    c: Coincident(g24,g12)
    c: Horizontal(g24)
    c: Coincident(g25,g0)
    c: Coincident(g25,g12)
    c: Horizontal(g25)
    c: Coincident(g26,g1)
    c: Coincident(g26,g13)
    c: Horizontal(g26)
    c: Coincident(g27,g1)
    c: Coincident(g27,g13)
    c: Horizontal(g27)
    c: Coincident(g28,g2)
    c: Coincident(g28,g14)
    c: Horizontal(g28)
    c: Coincident(g29,g2)
    c: Coincident(g29,g14)
    c: Horizontal(g29)
    c: Coincident(g30,g3)
    c: Coincident(g30,g15)
    c: Horizontal(g30)
    c: Coincident(g31,g3)
    c: Coincident(g31,g15)
    c: Horizontal(g31)
    c: Coincident(g32,g4)
    c: Coincident(g32,g16)
    c: Horizontal(g32)
    c: Coincident(g33,g4)
    c: Coincident(g33,g16)
    c: Horizontal(g33)
    c: Coincident(g34,g5)
    c: Coincident(g34,g17)
    c: Horizontal(g34)
    c: Coincident(g35,g5)
    c: Coincident(g35,g17)
    c: Horizontal(g35)
    c: Coincident(g36,g6)
    c: Coincident(g36,g19)
    c: Horizontal(g36)
    c: Coincident(g37,g6)
    c: Coincident(g37,g19)
    c: Horizontal(g37)
    c: Coincident(g38,g7)
    c: Coincident(g38,g18)
    c: Horizontal(g38)
    c: Coincident(g39,g7)
    c: Coincident(g39,g18)
    c: Horizontal(g39)
    c: Coincident(g40,g8)
    c: Coincident(g40,g20)
    c: Horizontal(g40)
    c: Coincident(g41,g8)
    c: Coincident(g41,g20)
    c: Horizontal(g41)
    c: Coincident(g42,g9)
    c: Coincident(g42,g23)
    c: Horizontal(g42)
    c: Coincident(g43,g9)
    c: Coincident(g43,g23)
    c: Horizontal(g43)
    c: Coincident(g44,g10)
    c: Coincident(g44,g22)
    c: Horizontal(g44)
    c: Coincident(g45,g10)
    c: Coincident(g45,g22)
    c: Horizontal(g45)
    c: Coincident(g46,g11)
    c: Coincident(g46,g21)
    c: Horizontal(g46)
    c: Coincident(g47,g11)
    c: Coincident(g47,g21)
    c: Horizontal(g47)
FEATURE [Part::Extrusion] Extrude046
  Base = -> Sketch055
  Dir = (1,0,0)
  DirMode = 2
  FaceMakerClass = Part::FaceMakerBullseye
  LengthFwd = 23
  LengthRev = 0
  Placement = pos=(-19,0,0) rot=(0,0,1;0rad)
  Solid = true
  Symmetric = false
FEATURE [Part::Fillet] Fillet038  label="removeToCreateVentalationHoles001"
  Base = -> Extrude046
  Edges = <same value as first occurrence — deduplicated (x6 in doc)>
  Placement = pos=(7,0,0) rot=(0,0,1;0rad)
FEATURE [Sketcher::SketchObject] Sketch056  label="topSketch014"
  FullyConstrained = true
  sketch-geometry (22):
    g0: LineSegment StartX=5.21097e-06 StartY=3 StartZ=0 EndX=5.21097e-06 EndY=19 EndZ=0
    g1: ArcOfCircle CenterX=19 CenterY=19 CenterZ=0 NormalX=0 NormalY=0 NormalZ=1 AngleXU=0 Radius=19 StartAngle=1.5708 EndAngle=3.14159
    g2: ArcOfCircle CenterX=19 CenterY=19 CenterZ=0 NormalX=0 NormalY=0 NormalZ=1 AngleXU=0 Radius=16 StartAngle=1.5708 EndAngle=3.14159
    g3: LineSegment StartX=114 StartY=35 StartZ=0 EndX=19 EndY=35 EndZ=0
    g4: LineSegment StartX=5.21097e-06 StartY=3 StartZ=0 EndX=5.21097e-06 EndY=0 EndZ=0
    g5: LineSegment StartX=3 StartY=0 StartZ=0 EndX=5.21097e-06 EndY=0 EndZ=0
    g6: LineSegment StartX=3 StartY=19 StartZ=0 EndX=3 EndY=0 EndZ=0
    g7: LineSegment StartX=19 StartY=38 StartZ=0 EndX=124 EndY=38 EndZ=0
    g8: Circle CenterX=119 CenterY=35 CenterZ=0 NormalX=0 NormalY=0 NormalZ=1 AngleXU=0 Radius=1
    g9: Circle CenterX=121 CenterY=35 CenterZ=0 NormalX=0 NormalY=0 NormalZ=1 AngleXU=0 Radius=1
    g10: Circle CenterX=121 CenterY=33 CenterZ=0 NormalX=0 NormalY=0 NormalZ=1 AngleXU=0 Radius=1
    g11: BSplineCurve PolesCount=3 KnotsCount=2 Degree=2 IsPeriodic=0
    g12: GeomPoint X=119 Y=35 Z=0
    g13: GeomPoint X=121 Y=33 Z=0
    g14: LineSegment StartX=119 StartY=35 StartZ=0 EndX=114 EndY=35 EndZ=0
    g15: ArcOfCircle CenterX=105 CenterY=19 CenterZ=0 NormalX=0 NormalY=0 NormalZ=1 AngleXU=0 Radius=16 StartAngle=5.60905 EndAngle=6.28319
    g16: LineSegment StartX=121 StartY=33 StartZ=0 EndX=121 EndY=19 EndZ=0
    g17: LineSegment StartX=117.5 StartY=9.01251 StartZ=0 EndX=121.163 EndY=9.0125 EndZ=0
    g18: ArcOfCircle CenterX=105 CenterY=19 CenterZ=0 NormalX=0 NormalY=0 NormalZ=1 AngleXU=0 Radius=20.6155 StartAngle=5.7297 EndAngle=6.28319
    g19: LineSegment StartX=121.163 StartY=9.0125 StartZ=0 EndX=122.538 EndY=8.16329 EndZ=0
    g20: LineSegment StartX=124 StartY=38 StartZ=0 EndX=125.616 EndY=38 EndZ=0
    g21: LineSegment StartX=125.616 StartY=19 StartZ=0 EndX=125.616 EndY=38 EndZ=0
  constraints (49):
    c: Vertical(g0)
    c: Block(g0)
    c: Coincident(g1,g0)
    c: Block(g1)
    c: Coincident(g2,g1)
    c: Block(g2)
    c: Coincident(g3,g2)
    c: Horizontal(g3)
    c: Tangent(g3,g2)
    c: Coincident(g4,g0)
    c: Distance(g4) = 3
    c: Vertical(g4)
    c: Coincident(g5,g4)
    c: Horizontal(g5)
    c: Coincident(g6,g2)
    c: Coincident(g6,g5)
    c: Vertical(g6)
    c: Horizontal(g7)
    c: Distance(g7) = 105
    c: Coincident(g7,g1)
    c: Block(g3)
    c: Weight(g8) = 1
    c: Equal(g8,g9)
    c: Equal(g8,g10)
    c: InternalAlignment(g8,g11)
    c: InternalAlignment(g9,g11)
    c: InternalAlignment(g10,g11)
    c: InternalAlignment(g12,g11)
    c: InternalAlignment(g13,g11)
    c: Block(g11)
    c: Coincident(g14,g11)
    c: Coincident(g14,g3)
    c: Horizontal(g14)
    c: Block(g15)
    c: Coincident(g16,g11)
    c: Coincident(g16,g15)
    c: Vertical(g16)
    c: Distance(g16) = 14
    c: Coincident(g17,g15)
    c: Block(g18)
    c: Coincident(g19,g18)
    c: Coincident(g20,g7)
    c: Horizontal(g20)
    c: Vertical(g21)
    c: Coincident(g20,g21)
    c: Block(g20)
    c: Block(g21)
    c: Block(g19)
    c: Block(g17)
FEATURE [Part::Box] Box026  label="removeToCreteHoleForPlugHousing032"
  AttacherType = Attacher::AttachEngine3D
  Height = 28.6
  Length = 10
  Placement = pos=(-2,0,21.7) rot=(0,0,1;0rad)
  Width = 19
FEATURE [Part::Feature] Face109 .. Face112  x4 (patterned run collapsed; names and placements below)
  shape: bbox 3.5 x 17.8 x 2e-07 mm, 1 faces, 0 solids (baked)
FEATURE [Part::Revolution] Revolve117  label="removeToCreateScrewAndThreadedInsertHole045"
  Angle = 360
  Axis = (0,1,0)
  Base = (0,0,0)
  FaceMakerClass = Part::FaceMakerBullseye
  Placement = pos=(62.3,30.3,19.7) rot=(0,0,1;0rad)
  Solid = false
  Source = -> Face109
  Symmetric = false
FEATURE [Part::Revolution] Revolve118  label="removeToCreateScrewAndThreadedInsertHole046"
  Angle = 360
  Axis = (0,1,0)
  Base = (0,0,0)
  FaceMakerClass = Part::FaceMakerBullseye
  Placement = pos=(62.3,30.3,51.7) rot=(0,0,1;0rad)
  Solid = false
  Source = -> Face110
  Symmetric = false
FEATURE [Part::Revolution] Revolve119  label="removeToCreateScrewAndThreadedInsertHole047"
  Angle = 360
  Axis = (0,1,0)
  Base = (0,0,0)
  FaceMakerClass = Part::FaceMakerBullseye
  Placement = pos=(30.3,30.3,19.7) rot=(0,0,1;0rad)
  Solid = false
  Source = -> Face111
  Symmetric = false
FEATURE [Part::Revolution] Revolve120  label="removeToCreateScrewAndThreadedInsertHole048"
  Angle = 360
  Axis = (0,1,0)
  Base = (0,0,0)
  FaceMakerClass = Part::FaceMakerBullseye
  Placement = pos=(30.3,30.3,51.7) rot=(0,0,1;0rad)
  Solid = false
  Source = -> Face112
  Symmetric = false
FEATURE [Part::MultiFuse] Fusion087  label="createThreadedInsertHolesForFan005"
  Shapes = -> [Revolve117,Revolve118,Revolve119,Revolve120]
FEATURE [Part::Extrusion] Extrude047
  Base = -> Sketch056
  Dir = (0,0,1)
  DirMode = 2
  FaceMakerClass = Part::FaceMakerBullseye
  LengthFwd = 72
  LengthRev = 0
  Solid = true
  Symmetric = false
FEATURE [Part::Fillet] Fillet039  label="top019"
  Base = -> Extrude047
  Edges = 1 edges r=2: [Edge35]
FEATURE [Sketcher::SketchObject] Sketch057
  FullyConstrained = false
  Placement = pos=(0,0,0) rot=(1,0,0;1.5708rad)
  sketch-geometry (24):
    g0: ArcOfCircle CenterX=-4 CenterY=-10.5 CenterZ=0 NormalX=0 NormalY=0 NormalZ=1 AngleXU=0 Radius=1.5 StartAngle=6e-16 EndAngle=3.14159
    g1: ArcOfCircle CenterX=-34.2 CenterY=-10.5 CenterZ=0 NormalX=0 NormalY=0 NormalZ=1 AngleXU=0 Radius=1.5 StartAngle=0 EndAngle=3.14159
    g2: ArcOfCircle CenterX=-34.2 CenterY=-27.7 CenterZ=0 NormalX=0 NormalY=0 NormalZ=1 AngleXU=0 Radius=1.5 StartAngle=3.14159 EndAngle=6.28319
    g3: ArcOfCircle CenterX=-4 CenterY=-27.7 CenterZ=0 NormalX=0 NormalY=0 NormalZ=1 AngleXU=0 Radius=1.5 StartAngle=3.1416 EndAngle=6.28319
    g4: ArcOfCircle CenterX=-10 CenterY=-4.3 CenterZ=0 NormalX=0 NormalY=0 NormalZ=1 AngleXU=0 Radius=1.5 StartAngle=2e-16 EndAngle=3.14159
    g5: ArcOfCircle CenterX=-16.1 CenterY=-1.8 CenterZ=0 NormalX=0 NormalY=0 NormalZ=1 AngleXU=0 Radius=1.5 StartAngle=5e-16 EndAngle=3.14159
    g6: ArcOfCircle CenterX=-22.1 CenterY=-1.8 CenterZ=0 NormalX=0 NormalY=0 NormalZ=1 AngleXU=0 Radius=1.5 StartAngle=5e-16 EndAngle=3.14159
    g7: ArcOfCircle CenterX=-28.2 CenterY=-4.3 CenterZ=0 NormalX=0 NormalY=0 NormalZ=1 AngleXU=0 Radius=1.5 StartAngle=2e-16 EndAngle=3.14159
    g8: ArcOfCircle CenterX=-10 CenterY=-33.9 CenterZ=0 NormalX=0 NormalY=0 NormalZ=1 AngleXU=0 Radius=1.5 StartAngle=3.14159 EndAngle=6.28319
    g9: ArcOfCircle CenterX=-16.1 CenterY=-36.4 CenterZ=0 NormalX=0 NormalY=0 NormalZ=1 AngleXU=0 Radius=1.5 StartAngle=3.14159 EndAngle=6.28319
    g10: ArcOfCircle CenterX=-22.1 CenterY=-36.4 CenterZ=0 NormalX=0 NormalY=0 NormalZ=1 AngleXU=0 Radius=1.5 StartAngle=3.14159 EndAngle=6.28319
    g11: ArcOfCircle CenterX=-28.2 CenterY=-33.9 CenterZ=0 NormalX=0 NormalY=0 NormalZ=1 AngleXU=0 Radius=1.5 StartAngle=3.14159 EndAngle=6.28319
    g12: LineSegment StartX=-35.7 StartY=-10.5 StartZ=0 EndX=-35.7 EndY=-27.7 EndZ=0
    g13: LineSegment StartX=-32.7 StartY=-10.5 StartZ=0 EndX=-32.7 EndY=-27.7 EndZ=0
    g14: LineSegment StartX=-29.7 StartY=-33.9 StartZ=0 EndX=-29.7 EndY=-4.3 EndZ=0
    g15: LineSegment StartX=-26.7 StartY=-33.9 StartZ=0 EndX=-26.7 EndY=-4.3 EndZ=0
    g16: LineSegment StartX=-2.5 StartY=-10.5 StartZ=0 EndX=-2.5 EndY=-27.7 EndZ=0
    g17: LineSegment StartX=-8.5 StartY=-4.3 StartZ=0 EndX=-8.5 EndY=-33.9 EndZ=0
    g18: LineSegment StartX=-5.5 StartY=-10.5 StartZ=0 EndX=-5.5 EndY=-27.7 EndZ=0
    g19: LineSegment StartX=-11.5 StartY=-4.3 StartZ=0 EndX=-11.5 EndY=-33.9 EndZ=0
    g20: LineSegment StartX=-14.6 StartY=-1.8 StartZ=0 EndX=-14.6 EndY=-36.4 EndZ=0
    g21: LineSegment StartX=-17.6 StartY=-1.8 StartZ=0 EndX=-17.6 EndY=-36.4 EndZ=0
    g22: LineSegment StartX=-20.6 StartY=-36.4 StartZ=0 EndX=-20.6 EndY=-1.8 EndZ=0
    g23: LineSegment StartX=-23.6 StartY=-1.8 StartZ=0 EndX=-23.6 EndY=-36.4 EndZ=0
  constraints (48):
    c: Block(g0)
    c: Block(g1)
    c: Block(g2)
    c: Block(g3)
    c: Block(g4)
    c: Block(g5)
    c: Block(g6)
    c: Block(g7)
    c: Block(g8)
    c: Block(g9)
    c: Block(g10)
    c: Block(g11)
    c: Coincident(g12,g1)
    c: Coincident(g12,g2)
    c: Vertical(g12)
    c: Coincident(g13,g1)
    c: Coincident(g13,g2)
    c: Vertical(g13)
    c: Coincident(g14,g11)
    c: Coincident(g14,g7)
    c: Vertical(g14)
    c: Coincident(g15,g11)
    c: Coincident(g15,g7)
    c: Vertical(g15)
    c: Coincident(g16,g0)
    c: Coincident(g16,g3)
    c: Vertical(g16)
    c: Coincident(g17,g4)
    c: Coincident(g17,g8)
    c: Vertical(g17)
    c: Coincident(g18,g0)
    c: Coincident(g18,g3)
    c: Vertical(g18)
    c: Coincident(g19,g4)
    c: Coincident(g19,g8)
    c: Vertical(g19)
    c: Coincident(g20,g5)
    c: Coincident(g20,g9)
    c: Vertical(g20)
    c: Coincident(g21,g5)
    c: Coincident(g21,g9)
    c: Vertical(g21)
    c: Coincident(g22,g10)
    c: Coincident(g22,g6)
    c: Vertical(g22)
    c: Coincident(g23,g6)
    c: Coincident(g23,g10)
    c: Vertical(g23)
FEATURE [Part::Extrusion] Extrude048  label="removeToCreateFanGrillHoles004"
  Base = -> Sketch057
  Dir = (0,-1,6e-16)
  DirMode = 2
  FaceMakerClass = Part::FaceMakerBullseye
  LengthFwd = 10
  LengthRev = 0
  Placement = pos=(65.4,44,54.82) rot=(0,0,1;0rad)
  Solid = true
  Symmetric = false
FEATURE [Part::Cut] Cut040  label="top021"
  Base = -> Fillet039
  Tool = -> Extrude048
FEATURE [Part::Cylinder] Cylinder041  label="removeToCreteHoleForPlugHousing034"
  Angle = 360
  AttacherType = Attacher::AttachEngine3D
  Height = 20
  Placement = pos=(-2,19,36) rot=(0,1,0;1.5708rad)
  Radius = 14.3
FEATURE [Part::MultiFuse] Fusion089  label="removeToCreteHoleForPlugHousing035"
  Shapes = -> [Box026,Cylinder041]
FEATURE [Part::Cylinder] Cylinder042
  Angle = 360
  AttacherType = Attacher::AttachEngine3D
  Height = 20
  Placement = pos=(0,0,36.15) rot=(0,0,1;0rad)
  Radius = 14.3
FEATURE [Part::Cylinder] Cylinder043
  Angle = 360
  AttacherType = Attacher::AttachEngine3D
  Height = 10
  Placement = pos=(0,0,36.15) rot=(0,0,1;0rad)
  Radius = 4
FEATURE [Part::Box] Box027  label="removeToCreteHoleForPlugHousing036"
  AttacherType = Attacher::AttachEngine3D
  Height = 28.6
  Length = 20
  Placement = pos=(106.15,0,21.7) rot=(0,0,1;0rad)
  Width = 19
FEATURE [Part::Cut] Cut041  label="top022"
  Base = -> Cut040
  Tool = -> Fusion087
FEATURE [Part::Cut] Cut039  label="top020"
  Base = -> Cut041
  Tool = -> Fusion089
FEATURE [Part::MultiFuse] Fusion090  label="removeToCreteHoleForPlugHousing037"
  Placement = pos=(70,19,36) rot=(0,1,0;1.5708rad)
  Shapes = -> [Cylinder042,Cylinder043]
FEATURE [Part::MultiFuse] Fusion088  label="removeToCreteHoleForPlugHousing033"
  Shapes = -> [Box027,Fusion090]
FEATURE [Part::Cut] Cut042  label="removeToCreteHoleForPlugHousing038"
  Base = -> Cut039
  Tool = -> Fusion088
FEATURE [Part::MultiFuse] Fusion091  label="removeFromTop"
  Shapes = -> [Fillet038,Fusion085,Fusion084,Fusion083,Extrude045]
FEATURE [Part::Cut] Cut043  label="REAL TOP ====="
  Base = -> Fillet036
  Tool = -> Fusion091
FEATURE [Part::MultiFuse] Fusion092  label="caseScrewPillarBracket016"
  Shapes = -> [Extrude030,Extrude031,Extrude032,Extrude033,Extrude034,Extrude035,Extrude036,Extrude037,Box013,Box014]
FEATURE [Sketcher::SketchObject] Sketch058  label="topSketch015"
  FullyConstrained = true
  sketch-geometry (20):
    g0: LineSegment StartX=5.21097e-06 StartY=3 StartZ=0 EndX=5.21097e-06 EndY=19 EndZ=0
    g1: ArcOfCircle CenterX=19 CenterY=19 CenterZ=0 NormalX=0 NormalY=0 NormalZ=1 AngleXU=0 Radius=19 StartAngle=1.5708 EndAngle=3.14159
    g2: ArcOfCircle CenterX=19 CenterY=19 CenterZ=0 NormalX=0 NormalY=0 NormalZ=1 AngleXU=0 Radius=16 StartAngle=1.5708 EndAngle=3.14159
    g3: LineSegment StartX=114 StartY=35 StartZ=0 EndX=19 EndY=35 EndZ=0
    g4: LineSegment StartX=5.21097e-06 StartY=3 StartZ=0 EndX=5.21097e-06 EndY=0 EndZ=0
    g5: LineSegment StartX=3 StartY=0 StartZ=0 EndX=5.21097e-06 EndY=0 EndZ=0
    g6: LineSegment StartX=3 StartY=19 StartZ=0 EndX=3 EndY=0 EndZ=0
    g7: LineSegment StartX=19 StartY=38 StartZ=0 EndX=124 EndY=38 EndZ=0
    g8: Circle CenterX=119 CenterY=35 CenterZ=0 NormalX=0 NormalY=0 NormalZ=1 AngleXU=0 Radius=1
    g9: Circle CenterX=121 CenterY=35 CenterZ=0 NormalX=0 NormalY=0 NormalZ=1 AngleXU=0 Radius=1
    g10: Circle CenterX=121 CenterY=33 CenterZ=0 NormalX=0 NormalY=0 NormalZ=1 AngleXU=0 Radius=1
    g11: BSplineCurve PolesCount=3 KnotsCount=2 Degree=2 IsPeriodic=0
    g12: GeomPoint X=119 Y=35 Z=0
    g13: GeomPoint X=121 Y=33 Z=0
    g14: LineSegment StartX=119 StartY=35 StartZ=0 EndX=114 EndY=35 EndZ=0
    g15: ArcOfCircle CenterX=105 CenterY=19 CenterZ=0 NormalX=0 NormalY=0 NormalZ=1 AngleXU=0 Radius=19 StartAngle=5.7297 EndAngle=6.28319
    g16: ArcOfCircle CenterX=105 CenterY=19 CenterZ=0 NormalX=0 NormalY=0 NormalZ=1 AngleXU=0 Radius=16 StartAngle=5.60905 EndAngle=6.28319
    g17: LineSegment StartX=121 StartY=33 StartZ=0 EndX=121 EndY=19 EndZ=0
    g18: LineSegment StartX=124 StartY=38 StartZ=0 EndX=124 EndY=19 EndZ=0
    g19: LineSegment StartX=117.5 StartY=9.01251 StartZ=0 EndX=121.163 EndY=9.0125 EndZ=0
  constraints (46):
    c: Vertical(g0)
    c: Block(g0)
    c: Coincident(g1,g0)
    c: Block(g1)
    c: Coincident(g2,g1)
    c: Block(g2)
    c: Coincident(g3,g2)
    c: Horizontal(g3)
    c: Tangent(g3,g2)
    c: Coincident(g4,g0)
    c: Distance(g4) = 3
    c: Vertical(g4)
    c: Coincident(g5,g4)
    c: Horizontal(g5)
    c: Coincident(g6,g2)
    c: Coincident(g6,g5)
    c: Vertical(g6)
    c: Horizontal(g7)
    c: Distance(g7) = 105
    c: Coincident(g7,g1)
    c: Block(g3)
    c: Weight(g8) = 1
    c: Equal(g8,g9)
    c: Equal(g8,g10)
    c: InternalAlignment(g8,g11)
    c: InternalAlignment(g9,g11)
    c: InternalAlignment(g10,g11)
    c: InternalAlignment(g12,g11)
    c: InternalAlignment(g13,g11)
    c: Block(g11)
    c: Coincident(g14,g11)
    c: Coincident(g14,g3)
    c: Horizontal(g14)
    c: Block(g15)
    c: Coincident(g16,g15)
    c: Block(g16)
    c: Coincident(g17,g11)
    c: Coincident(g17,g16)
    c: Vertical(g17)
    c: Distance(g17) = 14
    c: Coincident(g18,g7)
    c: Coincident(g18,g15)
    c: Vertical(g18)
    c: Distance(g18) = 19
    c: Coincident(g19,g16)
    c: Coincident(g19,g15)
FEATURE [Part::Extrusion] Extrude049  label="top023"
  Base = -> Sketch058
  Dir = (0,0,1)
  DirMode = 2
  FaceMakerClass = Part::FaceMakerBullseye
  LengthFwd = 72
  LengthRev = 0
  Solid = true
  Symmetric = false
FEATURE [Sketcher::SketchObject] Sketch059
  FullyConstrained = true
  MapMode = 3
  Placement = pos=(0,0,0) rot=(1,0,0;1.5708rad)
  Support = -> [Extrude049]
  sketch-geometry (8):
    g0: Circle CenterX=80.351 CenterY=-67.6202 CenterZ=0 NormalX=0 NormalY=0 NormalZ=1 AngleXU=0 Radius=2
    g1: Circle CenterX=80.351 CenterY=-67.6202 CenterZ=0 NormalX=0 NormalY=0 NormalZ=1 AngleXU=0 Radius=3
    g2: Circle CenterX=80.351 CenterY=-4.92017 CenterZ=0 NormalX=0 NormalY=0 NormalZ=1 AngleXU=0 Radius=2
    g3: Circle CenterX=80.351 CenterY=-4.92017 CenterZ=0 NormalX=0 NormalY=0 NormalZ=1 AngleXU=0 Radius=3
    g4: Circle CenterX=23.851 CenterY=-4.92017 CenterZ=0 NormalX=0 NormalY=0 NormalZ=1 AngleXU=0 Radius=2
    g5: Circle CenterX=23.851 CenterY=-4.92017 CenterZ=0 NormalX=0 NormalY=0 NormalZ=1 AngleXU=0 Radius=3
    g6: Circle CenterX=23.851 CenterY=-67.6202 CenterZ=0 NormalX=0 NormalY=0 NormalZ=1 AngleXU=0 Radius=2
    g7: Circle CenterX=23.851 CenterY=-67.6202 CenterZ=0 NormalX=0 NormalY=0 NormalZ=1 AngleXU=0 Radius=3
  constraints (8):
    c: Block(g3)
    c: Block(g2)
    c: Block(g1)
    c: Block(g0)
    c: Block(g6)
    c: Block(g7)
    c: Block(g4)
    c: Block(g5)
FEATURE [Sketcher::SketchObject] Sketch060
  FullyConstrained = true
  MapMode = 3
  Placement = pos=(0,0,0) rot=(1,0,0;1.5708rad)
  Support = -> [Extrude049]
  sketch-geometry (8):
    g0: Circle CenterX=80.351 CenterY=-67.6202 CenterZ=0 NormalX=0 NormalY=0 NormalZ=1 AngleXU=0 Radius=3
    g1: Circle CenterX=80.351 CenterY=-4.92017 CenterZ=0 NormalX=0 NormalY=0 NormalZ=1 AngleXU=0 Radius=3
    g2: Circle CenterX=23.851 CenterY=-4.92017 CenterZ=0 NormalX=0 NormalY=0 NormalZ=1 AngleXU=0 Radius=3
    g3: Circle CenterX=23.851 CenterY=-67.6202 CenterZ=0 NormalX=0 NormalY=0 NormalZ=1 AngleXU=0 Radius=3
    g4: Circle CenterX=23.851 CenterY=-67.6202 CenterZ=0 NormalX=0 NormalY=0 NormalZ=1 AngleXU=0 Radius=5
    g5: Circle CenterX=80.351 CenterY=-67.6202 CenterZ=0 NormalX=0 NormalY=0 NormalZ=1 AngleXU=0 Radius=5
    g6: Circle CenterX=23.851 CenterY=-4.92017 CenterZ=0 NormalX=0 NormalY=0 NormalZ=1 AngleXU=0 Radius=5
    g7: Circle CenterX=80.351 CenterY=-4.92017 CenterZ=0 NormalX=0 NormalY=0 NormalZ=1 AngleXU=0 Radius=5
  constraints (8):
    c: Block(g1)
    c: Block(g0)
    c: Block(g3)
    c: Block(g2)
    c: Block(g5)
    c: Block(g4)
    c: Block(g6)
    c: Block(g7)
FEATURE [Sketcher::SketchObject] Sketch061
  FullyConstrained = true
  MapMode = 3
  Placement = pos=(0,0,0) rot=(1,0,0;1.5708rad)
  sketch-geometry (8):
    g0: Circle CenterX=80.351 CenterY=-67.6202 CenterZ=0 NormalX=0 NormalY=0 NormalZ=1 AngleXU=0 Radius=3
    g1: Circle CenterX=80.351 CenterY=-4.92017 CenterZ=0 NormalX=0 NormalY=0 NormalZ=1 AngleXU=0 Radius=3
    g2: Circle CenterX=23.851 CenterY=-4.92017 CenterZ=0 NormalX=0 NormalY=0 NormalZ=1 AngleXU=0 Radius=3
    g3: Circle CenterX=23.851 CenterY=-67.6202 CenterZ=0 NormalX=0 NormalY=0 NormalZ=1 AngleXU=0 Radius=3
    g4: Circle CenterX=23.851 CenterY=-67.6202 CenterZ=0 NormalX=0 NormalY=0 NormalZ=1 AngleXU=0 Radius=5
    g5: Circle CenterX=80.351 CenterY=-67.6202 CenterZ=0 NormalX=0 NormalY=0 NormalZ=1 AngleXU=0 Radius=5
    g6: Circle CenterX=23.851 CenterY=-4.92017 CenterZ=0 NormalX=0 NormalY=0 NormalZ=1 AngleXU=0 Radius=5
    g7: Circle CenterX=80.351 CenterY=-4.92017 CenterZ=0 NormalX=0 NormalY=0 NormalZ=1 AngleXU=0 Radius=5
  constraints (8):
    c: Block(g1)
    c: Block(g0)
    c: Block(g3)
    c: Block(g2)
    c: Block(g5)
    c: Block(g4)
    c: Block(g6)
    c: Block(g7)
FEATURE [Sketcher::SketchObject] Sketch062  label="topSketch016"
  FullyConstrained = true
  sketch-geometry (20):
    g0: LineSegment StartX=5.21097e-06 StartY=3 StartZ=0 EndX=5.21097e-06 EndY=19 EndZ=0
    g1: ArcOfCircle CenterX=19 CenterY=19 CenterZ=0 NormalX=0 NormalY=0 NormalZ=1 AngleXU=0 Radius=19 StartAngle=1.5708 EndAngle=3.14159
    g2: ArcOfCircle CenterX=19 CenterY=19 CenterZ=0 NormalX=0 NormalY=0 NormalZ=1 AngleXU=0 Radius=16 StartAngle=1.5708 EndAngle=3.14159
    g3: LineSegment StartX=114 StartY=35 StartZ=0 EndX=19 EndY=35 EndZ=0
    g4: LineSegment StartX=5.21097e-06 StartY=3 StartZ=0 EndX=5.21097e-06 EndY=0 EndZ=0
    g5: LineSegment StartX=3 StartY=0 StartZ=0 EndX=5.21097e-06 EndY=0 EndZ=0
    g6: LineSegment StartX=3 StartY=19 StartZ=0 EndX=3 EndY=0 EndZ=0
    g7: LineSegment StartX=19 StartY=38 StartZ=0 EndX=124 EndY=38 EndZ=0
    g8: Circle CenterX=119 CenterY=35 CenterZ=0 NormalX=0 NormalY=0 NormalZ=1 AngleXU=0 Radius=1
    g9: Circle CenterX=121 CenterY=35 CenterZ=0 NormalX=0 NormalY=0 NormalZ=1 AngleXU=0 Radius=1
    g10: Circle CenterX=121 CenterY=33 CenterZ=0 NormalX=0 NormalY=0 NormalZ=1 AngleXU=0 Radius=1
    g11: BSplineCurve PolesCount=3 KnotsCount=2 Degree=2 IsPeriodic=0
    g12: GeomPoint X=119 Y=35 Z=0
    g13: GeomPoint X=121 Y=33 Z=0
    g14: LineSegment StartX=119 StartY=35 StartZ=0 EndX=114 EndY=35 EndZ=0
    g15: ArcOfCircle CenterX=105 CenterY=19 CenterZ=0 NormalX=0 NormalY=0 NormalZ=1 AngleXU=0 Radius=19 StartAngle=5.7297 EndAngle=6.28319
    g16: ArcOfCircle CenterX=105 CenterY=19 CenterZ=0 NormalX=0 NormalY=0 NormalZ=1 AngleXU=0 Radius=16 StartAngle=5.60905 EndAngle=6.28319
    g17: LineSegment StartX=121 StartY=33 StartZ=0 EndX=121 EndY=19 EndZ=0
    g18: LineSegment StartX=124 StartY=38 StartZ=0 EndX=124 EndY=19 EndZ=0
    g19: LineSegment StartX=117.5 StartY=9.01251 StartZ=0 EndX=121.163 EndY=9.0125 EndZ=0
  constraints (46):
    c: Vertical(g0)
    c: Block(g0)
    c: Coincident(g1,g0)
    c: Block(g1)
    c: Coincident(g2,g1)
    c: Block(g2)
    c: Coincident(g3,g2)
    c: Horizontal(g3)
    c: Tangent(g3,g2)
    c: Coincident(g4,g0)
    c: Distance(g4) = 3
    c: Vertical(g4)
    c: Coincident(g5,g4)
    c: Horizontal(g5)
    c: Coincident(g6,g2)
    c: Coincident(g6,g5)
    c: Vertical(g6)
    c: Horizontal(g7)
    c: Distance(g7) = 105
    c: Coincident(g7,g1)
    c: Block(g3)
    c: Weight(g8) = 1
    c: Equal(g8,g9)
    c: Equal(g8,g10)
    c: InternalAlignment(g8,g11)
    c: InternalAlignment(g9,g11)
    c: InternalAlignment(g10,g11)
    c: InternalAlignment(g12,g11)
    c: InternalAlignment(g13,g11)
    c: Block(g11)
    c: Coincident(g14,g11)
    c: Coincident(g14,g3)
    c: Horizontal(g14)
    c: Block(g15)
    c: Coincident(g16,g15)
    c: Block(g16)
    c: Coincident(g17,g11)
    c: Coincident(g17,g16)
    c: Vertical(g17)
    c: Distance(g17) = 14
    c: Coincident(g18,g7)
    c: Coincident(g18,g15)
    c: Vertical(g18)
    c: Distance(g18) = 19
    c: Coincident(g19,g16)
    c: Coincident(g19,g15)
FEATURE [Part::Extrusion] Extrude053  label="top024"
  Base = -> Sketch062
  Dir = (0,0,1)
  DirMode = 2
  FaceMakerClass = Part::FaceMakerBullseye
  LengthFwd = 72
  LengthRev = 0
  Solid = true
  Symmetric = false
FEATURE [Sketcher::SketchObject] Sketch063
  FullyConstrained = true
  MapMode = 3
  Placement = pos=(0,0,0) rot=(1,0,0;1.5708rad)
  Support = -> [Extrude053]
  sketch-geometry (8):
    g0: Circle CenterX=80.351 CenterY=-67.6202 CenterZ=0 NormalX=0 NormalY=0 NormalZ=1 AngleXU=0 Radius=2
    g1: Circle CenterX=80.351 CenterY=-67.6202 CenterZ=0 NormalX=0 NormalY=0 NormalZ=1 AngleXU=0 Radius=3
    g2: Circle CenterX=80.351 CenterY=-4.92017 CenterZ=0 NormalX=0 NormalY=0 NormalZ=1 AngleXU=0 Radius=2
    g3: Circle CenterX=80.351 CenterY=-4.92017 CenterZ=0 NormalX=0 NormalY=0 NormalZ=1 AngleXU=0 Radius=3
    g4: Circle CenterX=23.851 CenterY=-4.92017 CenterZ=0 NormalX=0 NormalY=0 NormalZ=1 AngleXU=0 Radius=2
    g5: Circle CenterX=23.851 CenterY=-4.92017 CenterZ=0 NormalX=0 NormalY=0 NormalZ=1 AngleXU=0 Radius=3
    g6: Circle CenterX=23.851 CenterY=-67.6202 CenterZ=0 NormalX=0 NormalY=0 NormalZ=1 AngleXU=0 Radius=2
    g7: Circle CenterX=23.851 CenterY=-67.6202 CenterZ=0 NormalX=0 NormalY=0 NormalZ=1 AngleXU=0 Radius=3
  constraints (8):
    c: Block(g3)
    c: Block(g2)
    c: Block(g1)
    c: Block(g0)
    c: Block(g6)
    c: Block(g7)
    c: Block(g4)
    c: Block(g5)
FEATURE [Part::Extrusion] Extrude054
  Base = -> Sketch063
  Dir = (0,-1,2e-16)
  DirMode = 2
  FaceMakerClass = Part::FaceMakerBullseye
  LengthFwd = 6
  LengthRev = 0
  Placement = pos=(0,9,0) rot=(0,0,1;0rad)
  Solid = true
  Symmetric = false
FEATURE [Sketcher::SketchObject] Sketch064  label="topSketch017"
  FullyConstrained = true
  sketch-geometry (20):
    g0: LineSegment StartX=5.21097e-06 StartY=3 StartZ=0 EndX=5.21097e-06 EndY=19 EndZ=0
    g1: ArcOfCircle CenterX=19 CenterY=19 CenterZ=0 NormalX=0 NormalY=0 NormalZ=1 AngleXU=0 Radius=19 StartAngle=1.5708 EndAngle=3.14159
    g2: ArcOfCircle CenterX=19 CenterY=19 CenterZ=0 NormalX=0 NormalY=0 NormalZ=1 AngleXU=0 Radius=16 StartAngle=1.5708 EndAngle=3.14159
    g3: LineSegment StartX=114 StartY=35 StartZ=0 EndX=19 EndY=35 EndZ=0
    g4: LineSegment StartX=5.21097e-06 StartY=3 StartZ=0 EndX=5.21097e-06 EndY=0 EndZ=0
    g5: LineSegment StartX=3 StartY=0 StartZ=0 EndX=5.21097e-06 EndY=0 EndZ=0
    g6: LineSegment StartX=3 StartY=19 StartZ=0 EndX=3 EndY=0 EndZ=0
    g7: LineSegment StartX=19 StartY=38 StartZ=0 EndX=124 EndY=38 EndZ=0
    g8: Circle CenterX=119 CenterY=35 CenterZ=0 NormalX=0 NormalY=0 NormalZ=1 AngleXU=0 Radius=1
    g9: Circle CenterX=121 CenterY=35 CenterZ=0 NormalX=0 NormalY=0 NormalZ=1 AngleXU=0 Radius=1
    g10: Circle CenterX=121 CenterY=33 CenterZ=0 NormalX=0 NormalY=0 NormalZ=1 AngleXU=0 Radius=1
    g11: BSplineCurve PolesCount=3 KnotsCount=2 Degree=2 IsPeriodic=0
    g12: GeomPoint X=119 Y=35 Z=0
    g13: GeomPoint X=121 Y=33 Z=0
    g14: LineSegment StartX=119 StartY=35 StartZ=0 EndX=114 EndY=35 EndZ=0
    g15: ArcOfCircle CenterX=105 CenterY=19 CenterZ=0 NormalX=0 NormalY=0 NormalZ=1 AngleXU=0 Radius=19 StartAngle=5.7297 EndAngle=6.28319
    g16: ArcOfCircle CenterX=105 CenterY=19 CenterZ=0 NormalX=0 NormalY=0 NormalZ=1 AngleXU=0 Radius=16 StartAngle=5.60905 EndAngle=6.28319
    g17: LineSegment StartX=121 StartY=33 StartZ=0 EndX=121 EndY=19 EndZ=0
    g18: LineSegment StartX=124 StartY=38 StartZ=0 EndX=124 EndY=19 EndZ=0
    g19: LineSegment StartX=117.5 StartY=9.01251 StartZ=0 EndX=121.163 EndY=9.0125 EndZ=0
  constraints (46):
    c: Vertical(g0)
    c: Block(g0)
    c: Coincident(g1,g0)
    c: Block(g1)
    c: Coincident(g2,g1)
    c: Block(g2)
    c: Coincident(g3,g2)
    c: Horizontal(g3)
    c: Tangent(g3,g2)
    c: Coincident(g4,g0)
    c: Distance(g4) = 3
    c: Vertical(g4)
    c: Coincident(g5,g4)
    c: Horizontal(g5)
    c: Coincident(g6,g2)
    c: Coincident(g6,g5)
    c: Vertical(g6)
    c: Horizontal(g7)
    c: Distance(g7) = 105
    c: Coincident(g7,g1)
    c: Block(g3)
    c: Weight(g8) = 1
    c: Equal(g8,g9)
    c: Equal(g8,g10)
    c: InternalAlignment(g8,g11)
    c: InternalAlignment(g9,g11)
    c: InternalAlignment(g10,g11)
    c: InternalAlignment(g12,g11)
    c: InternalAlignment(g13,g11)
    c: Block(g11)
    c: Coincident(g14,g11)
    c: Coincident(g14,g3)
    c: Horizontal(g14)
    c: Block(g15)
    c: Coincident(g16,g15)
    c: Block(g16)
    c: Coincident(g17,g11)
    c: Coincident(g17,g16)
    c: Vertical(g17)
    c: Distance(g17) = 14
    c: Coincident(g18,g7)
    c: Coincident(g18,g15)
    c: Vertical(g18)
    c: Distance(g18) = 19
    c: Coincident(g19,g16)
    c: Coincident(g19,g15)
FEATURE [Sketcher::SketchObject] Sketch065
  FullyConstrained = true
  MapMode = 3
  Placement = pos=(0,0,0) rot=(1,0,0;1.5708rad)
  sketch-geometry (8):
    g0: Circle CenterX=80.351 CenterY=-67.6202 CenterZ=0 NormalX=0 NormalY=0 NormalZ=1 AngleXU=0 Radius=3
    g1: Circle CenterX=80.351 CenterY=-4.92017 CenterZ=0 NormalX=0 NormalY=0 NormalZ=1 AngleXU=0 Radius=3
    g2: Circle CenterX=23.851 CenterY=-4.92017 CenterZ=0 NormalX=0 NormalY=0 NormalZ=1 AngleXU=0 Radius=3
    g3: Circle CenterX=23.851 CenterY=-67.6202 CenterZ=0 NormalX=0 NormalY=0 NormalZ=1 AngleXU=0 Radius=3
    g4: Circle CenterX=23.851 CenterY=-67.6202 CenterZ=0 NormalX=0 NormalY=0 NormalZ=1 AngleXU=0 Radius=5
    g5: Circle CenterX=80.351 CenterY=-67.6202 CenterZ=0 NormalX=0 NormalY=0 NormalZ=1 AngleXU=0 Radius=5
    g6: Circle CenterX=23.851 CenterY=-4.92017 CenterZ=0 NormalX=0 NormalY=0 NormalZ=1 AngleXU=0 Radius=5
    g7: Circle CenterX=80.351 CenterY=-4.92017 CenterZ=0 NormalX=0 NormalY=0 NormalZ=1 AngleXU=0 Radius=5
  constraints (8):
    c: Block(g1)
    c: Block(g0)
    c: Block(g3)
    c: Block(g2)
    c: Block(g5)
    c: Block(g4)
    c: Block(g6)
    c: Block(g7)
FEATURE [Part::Extrusion] Extrude056
  Base = -> Sketch065
  Dir = (0,-1,2e-16)
  DirMode = 2
  FaceMakerClass = Part::FaceMakerBullseye
  LengthFwd = 2
  LengthRev = 0
  Solid = true
  Symmetric = false
FEATURE [Part::Extrusion] Extrude057  label="top025"
  Base = -> Sketch064
  Dir = (0,0,1)
  DirMode = 2
  FaceMakerClass = Part::FaceMakerBullseye
  LengthFwd = 72
  LengthRev = 0
  Solid = true
  Symmetric = false
FEATURE [Sketcher::SketchObject] Sketch066
  FullyConstrained = true
  MapMode = 3
  Placement = pos=(0,0,0) rot=(1,0,0;1.5708rad)
  Support = -> [Extrude057]
  sketch-geometry (8):
    g0: Circle CenterX=80.351 CenterY=-67.6202 CenterZ=0 NormalX=0 NormalY=0 NormalZ=1 AngleXU=0 Radius=3
    g1: Circle CenterX=80.351 CenterY=-4.92017 CenterZ=0 NormalX=0 NormalY=0 NormalZ=1 AngleXU=0 Radius=3
    g2: Circle CenterX=23.851 CenterY=-4.92017 CenterZ=0 NormalX=0 NormalY=0 NormalZ=1 AngleXU=0 Radius=3
    g3: Circle CenterX=23.851 CenterY=-67.6202 CenterZ=0 NormalX=0 NormalY=0 NormalZ=1 AngleXU=0 Radius=3
    g4: Circle CenterX=23.851 CenterY=-67.6202 CenterZ=0 NormalX=0 NormalY=0 NormalZ=1 AngleXU=0 Radius=5
    g5: Circle CenterX=80.351 CenterY=-67.6202 CenterZ=0 NormalX=0 NormalY=0 NormalZ=1 AngleXU=0 Radius=5
    g6: Circle CenterX=23.851 CenterY=-4.92017 CenterZ=0 NormalX=0 NormalY=0 NormalZ=1 AngleXU=0 Radius=5
    g7: Circle CenterX=80.351 CenterY=-4.92017 CenterZ=0 NormalX=0 NormalY=0 NormalZ=1 AngleXU=0 Radius=5
  constraints (8):
    c: Block(g1)
    c: Block(g0)
    c: Block(g3)
    c: Block(g2)
    c: Block(g5)
    c: Block(g4)
    c: Block(g6)
    c: Block(g7)
FEATURE [Part::Extrusion] Extrude055
  Base = -> Sketch066
  Dir = (0,-1,2e-16)
  DirMode = 2
  FaceMakerClass = Part::FaceMakerBullseye
  LengthFwd = 2
  LengthRev = 0
  Solid = true
  Symmetric = false
FEATURE [Part::Fillet] Fillet041
  Base = -> Extrude056
  Edges = 4 edges r=1.99: [Edge6,Edge12,Edge18,Edge24]
FEATURE [Part::Cut] Cut045
  Base = -> Extrude055
  Placement = pos=(0,6,0) rot=(0,0,1;0rad)
  Tool = -> Fillet041
FEATURE [Part::MultiFuse] Fusion095  label="pcbScrewPillars"
  Placement = pos=(-3.2,-1,72.3) rot=(0,0,1;0rad)
  Shapes = -> [Cut045,Extrude054]
FEATURE [Part::Feature] Face113
  shape: bbox 3.2 x 1.5 x 2e-07 mm, 1 faces, 0 solids (baked)
FEATURE [Part::Revolution] Revolve121  label="backCaseScrewRetainer002"
  Angle = 360
  Axis = (0,1,0)
  Base = (0,0,0)
  FaceMakerClass = Part::FaceMakerBullseye
  Placement = pos=(12.5,3,62) rot=(0,0,1;0rad)
  Solid = false
  Source = -> Face113
  Symmetric = false
FEATURE [Part::Feature] Face114
  shape: bbox 3.2 x 1.5 x 2e-07 mm, 1 faces, 0 solids (baked)
FEATURE [Part::Feature] Face115
  shape: bbox 3.2 x 1.5 x 2e-07 mm, 1 faces, 0 solids (baked)
FEATURE [Part::Feature] Face116
  shape: bbox 3.2 x 1.5 x 2e-07 mm, 1 faces, 0 solids (baked)
FEATURE [Part::Revolution] Revolve122  label="frontCaseScrewRetainer004"
  Angle = 360
  Axis = (0,1,0)
  Base = (0,0,0)
  FaceMakerClass = Part::FaceMakerBullseye
  Placement = pos=(89.5,3,68.5) rot=(0,0,1;0rad)
  Solid = false
  Source = -> Face115
  Symmetric = false
FEATURE [Part::Revolution] Revolve123  label="frontCaseScrewRetainer005"
  Angle = 360
  Axis = (0,1,0)
  Base = (0,0,0)
  FaceMakerClass = Part::FaceMakerBullseye
  Placement = pos=(89.5,3,3.5) rot=(0,0,1;0rad)
  Solid = false
  Source = -> Face116
  Symmetric = false
FEATURE [Part::Revolution] Revolve124  label="backCaseScrewRetainer003"
  Angle = 360
  Axis = (0,1,0)
  Base = (0,0,0)
  FaceMakerClass = Part::FaceMakerBullseye
  Placement = pos=(12.5,3,10) rot=(0,0,1;0rad)
  Solid = false
  Source = -> Face114
  Symmetric = false
FEATURE [Part::Feature] Face117
  shape: bbox 3.6 x 3.2 x 2e-07 mm, 1 faces, 0 solids (baked)
FEATURE [Part::Revolution] Revolve125  label="moreFrontCaseScrewRetainer004"
  Angle = 360
  Axis = (0,1,0)
  Base = (0,0,0)
  FaceMakerClass = Part::FaceMakerBullseye
  Placement = pos=(109.5,4.5,68.5) rot=(0,0,1;0rad)
  Solid = false
  Source = -> Face117
  Symmetric = false
FEATURE [Part::Feature] Face118
  shape: bbox 3.6 x 3.2 x 2e-07 mm, 1 faces, 0 solids (baked)
FEATURE [Part::Revolution] Revolve126  label="moreFrontCaseScrewRetainer005"
  Angle = 360
  Axis = (0,1,0)
  Base = (0,0,0)
  FaceMakerClass = Part::FaceMakerBullseye
  Placement = pos=(109.5,4.5,3.5) rot=(0,0,1;0rad)
  Solid = false
  Source = -> Face118
  Symmetric = false
FEATURE [Part::MultiFuse] Fusion096  label="screwRetainers001"
  Shapes = -> [Revolve126,Revolve125,Revolve124,Revolve123,Revolve122,Revolve121]
FEATURE [Part::Feature] Face119
  shape: bbox 10 x 16.5 x 2e-07 mm, 1 faces, 0 solids (baked)
FEATURE [Part::Revolution] Revolve130  label="plugHousing050"
  Angle = 360
  Axis = (0,1,0)
  Base = (0,0,0)
  FaceMakerClass = Part::FaceMakerBullseye
  Placement = pos=(0,0,36.15) rot=(0,0,1;0rad)
  Solid = false
  Source = -> Face119
  Symmetric = false
FEATURE [Part::Feature] Face120
  shape: bbox 10 x 16.5 x 2e-07 mm, 1 faces, 0 solids (baked)
FEATURE [Part::Feature] Face121
  shape: bbox 10 x 16.5 x 2e-07 mm, 1 faces, 0 solids (baked)
FEATURE [Part::Revolution] Revolve127  label="plugHousing047"
  Angle = 360
  Axis = (0,1,0)
  Base = (0,0,0)
  FaceMakerClass = Part::FaceMakerBullseye
  Placement = pos=(0,0,36.15) rot=(0,0,1;0rad)
  Solid = false
  Source = -> Face121
  Symmetric = false
FEATURE [Part::Feature] Face122
  shape: bbox 10 x 16.5 x 2e-07 mm, 1 faces, 0 solids (baked)
FEATURE [Part::Feature] Face123
  shape: bbox 10 x 16.5 x 2e-07 mm, 1 faces, 0 solids (baked)
FEATURE [Part::Revolution] Revolve128  label="plugHousing048"
  Angle = 360
  Axis = (0,1,0)
  Base = (0,0,0)
  FaceMakerClass = Part::FaceMakerBullseye
  Placement = pos=(0,0,36.15) rot=(0,0,1;0rad)
  Solid = false
  Source = -> Face123
  Symmetric = false
FEATURE [Part::MultiFuse] Fusion100  label="plugHousing054"
  Placement = pos=(0,0,0) rot=(0,0,1;1.5708rad)
  Shapes = -> [Revolve130,Revolve128]
FEATURE [Part::Feature] Face124
  shape: bbox 10 x 16.5 x 2e-07 mm, 1 faces, 0 solids (baked)
FEATURE [Part::Feature] Face125
  shape: bbox 10 x 16.5 x 2e-07 mm, 1 faces, 0 solids (baked)
FEATURE [Part::Revolution] Revolve129  label="plugHousing049"
  Angle = 360
  Axis = (0,1,0)
  Base = (0,0,0)
  FaceMakerClass = Part::FaceMakerBullseye
  Placement = pos=(0,0,36.15) rot=(0,0,1;0rad)
  Solid = false
  Source = -> Face125
  Symmetric = false
FEATURE [Part::Feature] Face126
  shape: bbox 10 x 16.5 x 2e-07 mm, 1 faces, 0 solids (baked)
FEATURE [Part::Revolution] Revolve131  label="plugHousing058"
  Angle = 360
  Axis = (0,1,0)
  Base = (0,0,0)
  FaceMakerClass = Part::FaceMakerBullseye
  Placement = pos=(0,0,36.15) rot=(0,0,1;0rad)
  Solid = false
  Source = -> Face120
  Symmetric = false
FEATURE [Part::MultiFuse] Fusion099  label="plugHousing053"
  Placement = pos=(0,0,0) rot=(0,0,1;1.5708rad)
  Shapes = -> [Revolve127,Revolve131]
FEATURE [Part::MultiFuse] Fusion102  label="plugHousing056"
  Placement = pos=(0,19,0) rot=(0,0,1;3.14159rad)
  Shapes = -> [Fusion100,Fusion099]
FEATURE [Part::Revolution] Revolve132  label="plugHousing059"
  Angle = 360
  Axis = (0,1,0)
  Base = (0,0,0)
  FaceMakerClass = Part::FaceMakerBullseye
  Placement = pos=(0,0,36.15) rot=(0,0,1;0rad)
  Solid = false
  Source = -> Face126
  Symmetric = false
FEATURE [Part::Revolution] Revolve133  label="plugHousing060"
  Angle = 360
  Axis = (0,1,0)
  Base = (0,0,0)
  FaceMakerClass = Part::FaceMakerBullseye
  Placement = pos=(0,0,36.15) rot=(0,0,1;0rad)
  Solid = false
  Source = -> Face122
  Symmetric = false
FEATURE [Part::MultiFuse] Fusion097  label="plugHousing051"
  Placement = pos=(0,0,0) rot=(0,0,1;1.5708rad)
  Shapes = -> [Revolve133,Revolve132]
FEATURE [Part::Revolution] Revolve134  label="plugHousing061"
  Angle = 360
  Axis = (0,1,0)
  Base = (0,0,0)
  FaceMakerClass = Part::FaceMakerBullseye
  Placement = pos=(0,0,36.15) rot=(0,0,1;0rad)
  Solid = false
  Source = -> Face124
  Symmetric = false
FEATURE [Part::MultiFuse] Fusion101  label="plugHousing055"
  Placement = pos=(0,0,0) rot=(0,0,1;1.5708rad)
  Shapes = -> [Revolve129,Revolve134]
FEATURE [Part::MultiFuse] Fusion098  label="plugHousing052"
  Placement = pos=(0,19,0) rot=(0,0,1;3.14159rad)
  Shapes = -> [Fusion097,Fusion101]
FEATURE [Part::MultiFuse] Fusion103  label="plugHousing057"
  Placement = pos=(122.621,0,-0.15) rot=(0,0,1;0rad)
  Shapes = -> [Fusion102,Fusion098]
FEATURE [Part::Box] Box028  label="Cube015"
  AttacherType = Attacher::AttachEngine3D
  Height = 28
  Length = 3
  Placement = pos=(110.7,19,22) rot=(0,0,1;0rad)
  Width = 15.7
FEATURE [Part::Cylinder] Cylinder044
  Angle = 360
  AttacherType = Attacher::AttachEngine3D
  Height = 20
  Placement = pos=(0,0,36.15) rot=(0,0,1;0rad)
  Radius = 10.3
FEATURE [Part::Cylinder] Cylinder045
  Angle = 360
  AttacherType = Attacher::AttachEngine3D
  Height = 10
  Placement = pos=(0,0,36.15) rot=(0,0,1;0rad)
  Radius = 4
FEATURE [Part::MultiFuse] Fusion104  label="removeToCreteHoleForPlugHousing040"
  Placement = pos=(70,19,36) rot=(0,1,0;1.5708rad)
  Shapes = -> [Cylinder044,Cylinder045]
FEATURE [Part::Cut] Cut046  label="plugHousingTab003"
  Base = -> Box028
  Tool = -> Fusion104
FEATURE [Part::MultiFuse] Fusion105  label="plugHousing062"
  Shapes = -> [Fusion103,Cut046]
FEATURE [Part::Fillet] Fillet042
  Base = -> Fusion105
  Edges = 1 edges r=2: [Edge25]
FEATURE [Part::Fillet] Fillet043  label="plugHousing063"
  Base = -> Fillet042
  Edges = 1 edges r=2: [Edge8]
  Placement = pos=(7,0,0) rot=(0,0,1;0rad)
FEATURE [Part::Feature] Face127
  shape: bbox 10 x 16.5 x 2e-07 mm, 1 faces, 0 solids (baked)
FEATURE [Part::Feature] Face128
  shape: bbox 10 x 16.5 x 2e-07 mm, 1 faces, 0 solids (baked)
FEATURE [Part::Revolution] Revolve137  label="plugHousing070"
  Angle = 360
  Axis = (0,1,0)
  Base = (0,0,0)
  FaceMakerClass = Part::FaceMakerBullseye
  Placement = pos=(0,0,36.15) rot=(0,0,1;0rad)
  Solid = false
  Source = -> Face127
  Symmetric = false
FEATURE [Part::Revolution] Revolve140  label="plugHousing073"
  Angle = 360
  Axis = (0,1,0)
  Base = (0,0,0)
  FaceMakerClass = Part::FaceMakerBullseye
  Placement = pos=(0,0,36.15) rot=(0,0,1;0rad)
  Solid = false
  Source = -> Face128
  Symmetric = false
FEATURE [Part::Feature] Face129
  shape: bbox 10 x 16.5 x 2e-07 mm, 1 faces, 0 solids (baked)
FEATURE [Part::Revolution] Revolve138  label="plugHousing071"
  Angle = 360
  Axis = (0,1,0)
  Base = (0,0,0)
  FaceMakerClass = Part::FaceMakerBullseye
  Placement = pos=(0,0,36.15) rot=(0,0,1;0rad)
  Solid = false
  Source = -> Face129
  Symmetric = false
FEATURE [Part::Feature] Face130
  shape: bbox 10 x 16.5 x 2e-07 mm, 1 faces, 0 solids (baked)
FEATURE [Part::Revolution] Revolve139  label="plugHousing072"
  Angle = 360
  Axis = (0,1,0)
  Base = (0,0,0)
  FaceMakerClass = Part::FaceMakerBullseye
  Placement = pos=(0,0,36.15) rot=(0,0,1;0rad)
  Solid = false
  Source = -> Face130
  Symmetric = false
FEATURE [Part::Feature] Face131
  shape: bbox 10 x 16.5 x 2e-07 mm, 1 faces, 0 solids (baked)
FEATURE [Part::Revolution] Revolve135  label="plugHousing068"
  Angle = 360
  Axis = (0,1,0)
  Base = (0,0,0)
  FaceMakerClass = Part::FaceMakerBullseye
  Placement = pos=(0,0,36.15) rot=(0,0,1;0rad)
  Solid = false
  Source = -> Face131
  Symmetric = false
FEATURE [Part::MultiFuse] Fusion112  label="plugHousing078"
  Placement = pos=(0,0,0) rot=(0,0,1;1.5708rad)
  Shapes = -> [Revolve135,Revolve139]
FEATURE [Part::Feature] Face132
  shape: bbox 10 x 16.5 x 2e-07 mm, 1 faces, 0 solids (baked)
FEATURE [Part::Revolution] Revolve141  label="plugHousing074"
  Angle = 360
  Axis = (0,1,0)
  Base = (0,0,0)
  FaceMakerClass = Part::FaceMakerBullseye
  Placement = pos=(0,0,36.15) rot=(0,0,1;0rad)
  Solid = false
  Source = -> Face132
  Symmetric = false
FEATURE [Part::MultiFuse] Fusion110  label="plugHousing076"
  Placement = pos=(0,0,0) rot=(0,0,1;1.5708rad)
  Shapes = -> [Revolve141,Revolve140]
FEATURE [Part::Feature] Face133
  shape: bbox 10 x 16.5 x 2e-07 mm, 1 faces, 0 solids (baked)
FEATURE [Part::Revolution] Revolve136  label="plugHousing069"
  Angle = 360
  Axis = (0,1,0)
  Base = (0,0,0)
  FaceMakerClass = Part::FaceMakerBullseye
  Placement = pos=(0,0,36.15) rot=(0,0,1;0rad)
  Solid = false
  Source = -> Face133
  Symmetric = false
FEATURE [Part::MultiFuse] Fusion106  label="plugHousing064"
  Placement = pos=(0,0,0) rot=(0,0,1;1.5708rad)
  Shapes = -> [Revolve138,Revolve136]
FEATURE [Part::MultiFuse] Fusion108  label="plugHousing066"
  Placement = pos=(0,19,0) rot=(0,0,1;3.14159rad)
  Shapes = -> [Fusion106,Fusion112]
FEATURE [Part::Feature] Face134
  shape: bbox 10 x 16.5 x 2e-07 mm, 1 faces, 0 solids (baked)
FEATURE [Part::Revolution] Revolve142  label="plugHousing075"
  Angle = 360
  Axis = (0,1,0)
  Base = (0,0,0)
  FaceMakerClass = Part::FaceMakerBullseye
  Placement = pos=(0,0,36.15) rot=(0,0,1;0rad)
  Solid = false
  Source = -> Face134
  Symmetric = false
FEATURE [Part::MultiFuse] Fusion107  label="plugHousing065"
  Placement = pos=(0,0,0) rot=(0,0,1;1.5708rad)
  Shapes = -> [Revolve137,Revolve142]
FEATURE [Part::MultiFuse] Fusion111  label="plugHousing077"
  Placement = pos=(0,19,0) rot=(0,0,1;3.14159rad)
  Shapes = -> [Fusion110,Fusion107]
FEATURE [Part::MultiFuse] Fusion109  label="plugHousing067"
  Placement = pos=(131.236,0,-0.15) rot=(0,0,1;0rad)
  Shapes = -> [Fusion108,Fusion111]
FEATURE [Part::MultiFuse] Fusion113  label="plugHousing079"
  Shapes = -> [Fillet043,Fusion109]
FEATURE [Part::Feature] Face135
  shape: bbox 3.5 x 17.8 x 2e-07 mm, 1 faces, 0 solids (baked)
FEATURE [Part::Revolution] Revolve143  label="removeToCreateScrewAndThreadedInsertHole049"
  Angle = 360
  Axis = (0,1,0)
  Base = (0,0,0)
  FaceMakerClass = Part::FaceMakerBullseye
  Placement = pos=(12.5,0,10) rot=(0,0,1;0rad)
  Solid = false
  Source = -> Face135
  Symmetric = false
FEATURE [Part::Feature] Face136
  shape: bbox 3.5 x 17.8 x 2e-07 mm, 1 faces, 0 solids (baked)
FEATURE [Part::Revolution] Revolve144  label="removeToCreateScrewAndThreadedInsertHole050"
  Angle = 360
  Axis = (0,1,0)
  Base = (0,0,0)
  FaceMakerClass = Part::FaceMakerBullseye
  Placement = pos=(12.5,0,62) rot=(0,0,1;0rad)
  Solid = false
  Source = -> Face136
  Symmetric = false
FEATURE [Part::Feature] Face137
  shape: bbox 3.5 x 17.8 x 2e-07 mm, 1 faces, 0 solids (baked)
FEATURE [Part::Revolution] Revolve145  label="removeToCreateScrewAndThreadedInsertHole051"
  Angle = 360
  Axis = (0,1,0)
  Base = (0,0,0)
  FaceMakerClass = Part::FaceMakerBullseye
  Placement = pos=(89.5,0,68.5) rot=(0,0,1;0rad)
  Solid = false
  Source = -> Face137
  Symmetric = false
FEATURE [Part::Feature] Face138
  shape: bbox 3.5 x 17.8 x 2e-07 mm, 1 faces, 0 solids (baked)
FEATURE [Part::Revolution] Revolve146  label="removeToCreateScrewAndThreadedInsertHole052"
  Angle = 360
  Axis = (0,1,0)
  Base = (0,0,0)
  FaceMakerClass = Part::FaceMakerBullseye
  Placement = pos=(89.5,0,3.5) rot=(0,0,1;0rad)
  Solid = false
  Source = -> Face138
  Symmetric = false
FEATURE [Part::Feature] Face139
  shape: bbox 3.5 x 17.8 x 2e-07 mm, 1 faces, 0 solids (baked)
FEATURE [Part::Revolution] Revolve147  label="removeToCreateScrewAndThreadedInsertHole053"
  Angle = 360
  Axis = (0,1,0)
  Base = (0,0,0)
  FaceMakerClass = Part::FaceMakerBullseye
  Placement = pos=(109.5,4.7,3.5) rot=(0,0,1;0rad)
  Solid = false
  Source = -> Face139
  Symmetric = false
FEATURE [Part::Feature] Face140
  shape: bbox 3.5 x 17.8 x 2e-07 mm, 1 faces, 0 solids (baked)
FEATURE [Part::Revolution] Revolve148  label="removeToCreateScrewAndThreadedInsertHole054"
  Angle = 360
  Axis = (0,1,0)
  Base = (0,0,0)
  FaceMakerClass = Part::FaceMakerBullseye
  Placement = pos=(109.5,4.7,68.5) rot=(0,0,1;0rad)
  Solid = false
  Source = -> Face140
  Symmetric = false
FEATURE [Part::MultiFuse] Fusion114  label="removeToCreateScrewAndThreadedInsertHole055"
  Shapes = -> [Revolve148,Revolve147,Revolve146,Revolve145,Revolve144,Revolve143]
FEATURE [Part::Cut] Cut047  label="casePillars004"
  Base = -> Cut037
  Tool = -> Fusion114
FEATURE [Part::Feature] Face141
  shape: bbox 3.5 x 17.8 x 2e-07 mm, 1 faces, 0 solids (baked)
FEATURE [Part::Feature] Face142
  shape: bbox 3.5 x 17.8 x 2e-07 mm, 1 faces, 0 solids (baked)
FEATURE [Part::Feature] Face143
  shape: bbox 3.5 x 17.8 x 2e-07 mm, 1 faces, 0 solids (baked)
FEATURE [Part::Revolution] Revolve149  label="removeToCreateScrewAndThreadedInsertHole057"
  Angle = 360
  Axis = (0,1,0)
  Base = (0,0,0)
  FaceMakerClass = Part::FaceMakerBullseye
  Placement = pos=(12.5,0,10) rot=(0,0,1;0rad)
  Solid = false
  Source = -> Face141
  Symmetric = false
FEATURE [Part::Feature] Face144
  shape: bbox 3.5 x 17.8 x 2e-07 mm, 1 faces, 0 solids (baked)
FEATURE [Part::Feature] Face145
  shape: bbox 3.5 x 17.8 x 2e-07 mm, 1 faces, 0 solids (baked)
FEATURE [Part::Feature] Face146
  shape: bbox 3.5 x 17.8 x 2e-07 mm, 1 faces, 0 solids (baked)
FEATURE [Part::Revolution] Revolve150  label="removeToCreateScrewAndThreadedInsertHole058"
  Angle = 360
  Axis = (0,1,0)
  Base = (0,0,0)
  FaceMakerClass = Part::FaceMakerBullseye
  Placement = pos=(12.5,0,62) rot=(0,0,1;0rad)
  Solid = false
  Source = -> Face146
  Symmetric = false
FEATURE [Part::Revolution] Revolve151  label="removeToCreateScrewAndThreadedInsertHole059"
  Angle = 360
  Axis = (0,1,0)
  Base = (0,0,0)
  FaceMakerClass = Part::FaceMakerBullseye
  Placement = pos=(89.5,0,68.5) rot=(0,0,1;0rad)
  Solid = false
  Source = -> Face143
  Symmetric = false
FEATURE [Part::Revolution] Revolve152  label="removeToCreateScrewAndThreadedInsertHole060"
  Angle = 360
  Axis = (0,1,0)
  Base = (0,0,0)
  FaceMakerClass = Part::FaceMakerBullseye
  Placement = pos=(89.5,0,3.5) rot=(0,0,1;0rad)
  Solid = false
  Source = -> Face142
  Symmetric = false
FEATURE [Part::Revolution] Revolve153  label="removeToCreateScrewAndThreadedInsertHole061"
  Angle = 360
  Axis = (0,1,0)
  Base = (0,0,0)
  FaceMakerClass = Part::FaceMakerBullseye
  Placement = pos=(109.5,4.7,3.5) rot=(0,0,1;0rad)
  Solid = false
  Source = -> Face145
  Symmetric = false
FEATURE [Part::Revolution] Revolve154  label="removeToCreateScrewAndThreadedInsertHole062"
  Angle = 360
  Axis = (0,1,0)
  Base = (0,0,0)
  FaceMakerClass = Part::FaceMakerBullseye
  Placement = pos=(109.5,4.7,68.5) rot=(0,0,1;0rad)
  Solid = false
  Source = -> Face144
  Symmetric = false
FEATURE [Part::MultiFuse] Fusion115  label="removeToCreateScrewAndThreadedInsertHole056"
  Shapes = -> [Revolve154,Revolve153,Revolve152,Revolve151,Revolve150,Revolve149]
FEATURE [Part::Feature] Face147
  shape: bbox 9.8 x 26.5 x 2e-07 mm, 1 faces, 0 solids (baked)
FEATURE [Part::Revolution] Revolve155
  Angle = 360
  Axis = (0,1,0)
  Base = (0,0,0)
  FaceMakerClass = Part::FaceMakerBullseye
  Placement = pos=(0,0,0) rot=(0,0,1;1.5708rad)
  Solid = false
  Source = -> Face147
  Symmetric = false
FEATURE [Part::Feature] Face148
  shape: bbox 9.8 x 26.5 x 2e-07 mm, 1 faces, 0 solids (baked)
FEATURE [Part::Revolution] Revolve156
  Angle = 360
  Axis = (0,1,0)
  Base = (0,0,0)
  FaceMakerClass = Part::FaceMakerBullseye
  Placement = pos=(0,0,0) rot=(0,0,1;1.5708rad)
  Solid = false
  Source = -> Face148
  Symmetric = false
FEATURE [Part::MultiFuse] Fusion116
  Placement = pos=(-18,19,36) rot=(0,0,1;0rad)
  Shapes = -> [Revolve156,Revolve155]
FEATURE [Part::Box] Box029  label="Cube016"
  AttacherType = Attacher::AttachEngine3D
  Height = 28
  Length = 3
  Placement = pos=(110.7,19,22) rot=(0,0,1;0rad)
  Width = 15.7
FEATURE [Part::Cylinder] Cylinder046
  Angle = 360
  AttacherType = Attacher::AttachEngine3D
  Height = 10
  Placement = pos=(0,0,36.15) rot=(0,0,1;0rad)
  Radius = 4
FEATURE [Part::Cylinder] Cylinder047
  Angle = 360
  AttacherType = Attacher::AttachEngine3D
  Height = 20
  Placement = pos=(0,0,36.15) rot=(0,0,1;0rad)
  Radius = 10.3
FEATURE [Part::MultiFuse] Fusion117  label="removeToCreteHoleForPlugHousing041"
  Placement = pos=(70,19,36) rot=(0,1,0;1.5708rad)
  Shapes = -> [Cylinder047,Cylinder046]
FEATURE [Part::Cut] Cut049  label="plugHousingTab004"
  Base = -> Box029
  Placement = pos=(-107.4,-14,0) rot=(0,0,1;0rad)
  Tool = -> Fusion117
FEATURE [Part::Box] Box030  label="Cube017"
  AttacherType = Attacher::AttachEngine3D
  Height = 28
  Length = 3
  Placement = pos=(110.7,19,22) rot=(0,0,1;0rad)
  Width = 15.7
FEATURE [Part::Cylinder] Cylinder048
  Angle = 360
  AttacherType = Attacher::AttachEngine3D
  Height = 10
  Placement = pos=(0,0,36.15) rot=(0,0,1;0rad)
  Radius = 4
FEATURE [Part::Cylinder] Cylinder049
  Angle = 360
  AttacherType = Attacher::AttachEngine3D
  Height = 20
  Placement = pos=(0,0,36.15) rot=(0,0,1;0rad)
  Radius = 10.3
FEATURE [Part::MultiFuse] Fusion118  label="removeToCreteHoleForPlugHousing042"
  Placement = pos=(70,19,36) rot=(0,1,0;1.5708rad)
  Shapes = -> [Cylinder049,Cylinder048]
FEATURE [Part::Cut] Cut050  label="plugHousingTab005"
  Base = -> Box030
  Placement = pos=(-107.4,-14,0) rot=(0,0,1;0rad)
  Tool = -> Fusion118
FEATURE [Part::MultiFuse] Fusion119
  Placement = pos=(9.6,23,0) rot=(0,0,1;3.14159rad)
  Shapes = -> [Cut049,Cut050]
FEATURE [Part::Box] Box031  label="Cube018"
  AttacherType = Attacher::AttachEngine3D
  Height = 10
  Length = 3
  Placement = pos=(3.3,4,12) rot=(0,0,1;0rad)
  Width = 10
FEATURE [Part::Fillet] Fillet044
  Base = -> Box031
  Edges = 1 edges r=2: [Edge11]
FEATURE [Part::Box] Box032  label="Cube019"
  AttacherType = Attacher::AttachEngine3D
  Height = 10
  Length = 3
  Placement = pos=(3.3,4,50) rot=(0,0,1;0rad)
  Width = 10
FEATURE [Part::Fillet] Fillet045
  Base = -> Box032
  Edges = 1 edges r=2: [Edge12]
FEATURE [Part::Box] Box033  label="Cube020"
  AttacherType = Attacher::AttachEngine3D
  Height = 28
  Length = 4
  Placement = pos=(5,0,22) rot=(0,0,1;0rad)
  Width = 10
FEATURE [Part::Fillet] Fillet046
  Base = -> Box033
  Edges = 1 edges r=1: [Edge7]
FEATURE [Part::Fillet] Fillet047
  Base = -> Fillet046
  Edges = 1 edges r=2: [Edge5]
FEATURE [Part::Fillet] Fillet048
  Base = -> Fillet047
  Edges = 1 edges r=2: [Edge2]
FEATURE [Part::Cylinder] Cylinder050
  Angle = 360
  AttacherType = Attacher::AttachEngine3D
  Height = 20
  Placement = pos=(0,0,36.15) rot=(0,0,1;0rad)
  Radius = 8.2
FEATURE [Part::Cylinder] Cylinder051
  Angle = 360
  AttacherType = Attacher::AttachEngine3D
  Height = 10
  Placement = pos=(0,0,36.15) rot=(0,0,1;0rad)
  Radius = 4
FEATURE [Part::MultiFuse] Fusion120  label="removeToCreteHoleForPlugHousing043"
  Placement = pos=(-42,19,36) rot=(0,1,0;1.5708rad)
  Shapes = -> [Cylinder050,Cylinder051]
FEATURE [Sketcher::SketchObject] Sketch067  label="topSketch018"
  FullyConstrained = true
  sketch-geometry (4):
    g0: LineSegment StartX=16.8446 StartY=31.512 StartZ=0 EndX=16.3251 EndY=34.4666 EndZ=0
    g1: ArcOfCircle CenterX=19 CenterY=19.2524 CenterZ=0 NormalX=0 NormalY=0 NormalZ=1 AngleXU=0 Radius=15.4476 StartAngle=1.74483 EndAngle=2.72717
    g2: ArcOfCircle CenterX=19 CenterY=19.2524 CenterZ=0 NormalX=0 NormalY=0 NormalZ=1 AngleXU=0 Radius=12.4476 StartAngle=1.74483 EndAngle=2.73189
    g3: LineSegment StartX=4.86004 StartY=25.4725 StartZ=0 EndX=7.58253 EndY=24.2107 EndZ=0
  constraints (7):
    c: Block(g0)
    c: Coincident(g1,g0)
    c: Coincident(g2,g0)
    c: Coincident(g3,g1)
    c: Coincident(g3,g2)
    c: Block(g1)
    c: Block(g2)
FEATURE [Part::Extrusion] Extrude058
  Base = -> Sketch067
  Dir = (0,0,1)
  DirMode = 2
  FaceMakerClass = Part::FaceMakerBullseye
  LengthFwd = 10
  LengthRev = 0
  Placement = pos=(0,0,31) rot=(0,0,1;0rad)
  Solid = true
  Symmetric = false
FEATURE [Part::Cut] Cut051
  Base = -> Extrude058
  Tool = -> Fusion120
FEATURE [Part::Fillet] Fillet049
  Base = -> Cut051
  Edges = 1 edges r=2: [Edge1]
FEATURE [Part::Fillet] Fillet050
  Base = -> Fillet049
  Edges = 1 edges r=2.5: [Edge1]
FEATURE [Part::Fillet] Fillet051
  Base = -> Fillet050
  Edges = 1 edges r=2.5: [Edge2]
FEATURE [Part::MultiFuse] Fusion121  label="wireHolder003"
  Shapes = -> [Fusion116,Fillet051]
FEATURE [Part::MultiFuse] Fusion122
  Shapes = -> [Fillet045,Fusion121]
FEATURE [Part::MultiFuse] Fusion123  label="wireHolder004"
  Shapes = -> [Fusion122,Fillet048]
FEATURE [Part::MultiFuse] Fusion124  label="wireHolder005"
  Shapes = -> [Fillet044,Fusion119,Fusion123]
FEATURE [Sketcher::SketchObject] Sketch068  label="topSketch019"
  FullyConstrained = true
  sketch-geometry (6):
    g0: LineSegment StartX=19 StartY=38 StartZ=0 EndX=117 EndY=38 EndZ=0
    g1: ArcOfCircle CenterX=19 CenterY=19 CenterZ=0 NormalX=0 NormalY=0 NormalZ=1 AngleXU=0 Radius=19 StartAngle=1.5708 EndAngle=3.14159
    g2: LineSegment StartX=117 StartY=38 StartZ=0 EndX=117 EndY=19 EndZ=0
    g3: LineSegment StartX=98 StartY=1.0161e-12 StartZ=0 EndX=5.22862e-06 EndY=1.0161e-12 EndZ=0
    g4: LineSegment StartX=5.22862e-06 StartY=19 StartZ=0 EndX=5.22862e-06 EndY=1.0161e-12 EndZ=0
    g5: ArcOfCircle CenterX=98 CenterY=19 CenterZ=0 NormalX=0 NormalY=0 NormalZ=1 AngleXU=0 Radius=19 StartAngle=4.71239 EndAngle=6.28319
  constraints (16):
    c: Horizontal(g0)
    c: Distance(g0) = 98
    c: Coincident(g1,g0)
    c: Block(g1)
    c: Coincident(g2,g0)
    c: Vertical(g2)
    c: Distance(g2) = 19
    c: Horizontal(g3)
    c: Coincident(g4,g1)
    c: Vertical(g4)
    c: Coincident(g3,g4)
    c: Block(g3)
    c: Coincident(g5,g2)
    c: Coincident(g5,g3)
    c: Block(g0)
    c: Block(g5)
FEATURE [Part::Extrusion] Extrude059  label="sideA002"
  Base = -> Sketch068
  Dir = (0,0,1)
  DirMode = 2
  FaceMakerClass = Part::FaceMakerBullseye
  LengthFwd = 3
  LengthRev = 0
  Placement = pos=(0,0,-2.7) rot=(0,0,1;0rad)
  Solid = true
  Symmetric = false
FEATURE [Sketcher::SketchObject] Sketch069  label="topSketch020"
  FullyConstrained = true
  sketch-geometry (6):
    g0: LineSegment StartX=19 StartY=38 StartZ=0 EndX=117 EndY=38 EndZ=0
    g1: ArcOfCircle CenterX=19 CenterY=19 CenterZ=0 NormalX=0 NormalY=0 NormalZ=1 AngleXU=0 Radius=19 StartAngle=1.5708 EndAngle=3.14159
    g2: LineSegment StartX=117 StartY=38 StartZ=0 EndX=117 EndY=19 EndZ=0
    g3: LineSegment StartX=98 StartY=1.0161e-12 StartZ=0 EndX=5.22862e-06 EndY=1.0161e-12 EndZ=0
    g4: LineSegment StartX=5.22862e-06 StartY=19 StartZ=0 EndX=5.22862e-06 EndY=1.0161e-12 EndZ=0
    g5: ArcOfCircle CenterX=98 CenterY=19 CenterZ=0 NormalX=0 NormalY=0 NormalZ=1 AngleXU=0 Radius=19 StartAngle=4.71239 EndAngle=6.28319
  constraints (16):
    c: Horizontal(g0)
    c: Distance(g0) = 98
    c: Coincident(g1,g0)
    c: Block(g1)
    c: Coincident(g2,g0)
    c: Vertical(g2)
    c: Distance(g2) = 19
    c: Horizontal(g3)
    c: Coincident(g4,g1)
    c: Vertical(g4)
    c: Coincident(g3,g4)
    c: Block(g3)
    c: Coincident(g5,g2)
    c: Coincident(g5,g3)
    c: Block(g0)
    c: Block(g5)
FEATURE [Part::Extrusion] Extrude060  label="sideB002"
  Base = -> Sketch069
  Dir = (0,0,1)
  DirMode = 2
  FaceMakerClass = Part::FaceMakerBullseye
  LengthFwd = 3
  LengthRev = 0
  Placement = pos=(0,0,71.7) rot=(0,0,1;0rad)
  Solid = true
  Symmetric = false
FEATURE [Part::MultiFuse] Fusion127  label="removeFromBottom001"
  Placement = pos=(2,0,0) rot=(0,0,1;0rad)
  Shapes = -> [Extrude059,Extrude060]
FEATURE [Part::Cylinder] Cylinder052
  Angle = 360
  AttacherType = Attacher::AttachEngine3D
  Height = 20
  Placement = pos=(0,0,36.15) rot=(0,0,1;0rad)
  Radius = 14
FEATURE [Part::Cylinder] Cylinder053
  Angle = 360
  AttacherType = Attacher::AttachEngine3D
  Height = 10
  Placement = pos=(0,0,36.15) rot=(0,0,1;0rad)
  Radius = 4
FEATURE [Part::MultiFuse] Fusion128  label="removeToCreteHoleForPlugHousing044"
  Placement = pos=(70,19,36) rot=(0,1,0;1.5708rad)
  Shapes = -> [Cylinder052,Cylinder053]
FEATURE [Part::Cut] Cut052  label="bottom011"
  Base = -> Extrude043
  Tool = -> Fusion128
FEATURE [Part::Cut] Cut054  label="bottom012"
  Base = -> Cut052
  Tool = -> Fusion115
FEATURE [Sketcher::SketchObject] Sketch070
  FullyConstrained = true
  Placement = pos=(117,19,0) rot=(0.57735,0.57735,0.57735;2.0944rad)
  sketch-geometry (48):
    g0: LineSegment StartX=-49.19 StartY=69.25 StartZ=0 EndX=-49.19 EndY=66.25 EndZ=0
    g1: LineSegment StartX=-49.19 StartY=63.5 StartZ=0 EndX=-49.19 EndY=60.5 EndZ=0
    g2: LineSegment StartX=-49.19 StartY=57.75 StartZ=0 EndX=-49.19 EndY=54.75 EndZ=0
    g3: LineSegment StartX=-49.19 StartY=52 StartZ=0 EndX=-49.19 EndY=49 EndZ=0
    g4: LineSegment StartX=-49.19 StartY=46.25 StartZ=0 EndX=-49.19 EndY=43.25 EndZ=0
    g5: LineSegment StartX=-49.19 StartY=40.5 StartZ=0 EndX=-49.19 EndY=37.5 EndZ=0
    g6: LineSegment StartX=-49.19 StartY=34.5 StartZ=0 EndX=-49.19 EndY=31.5 EndZ=0
    g7: LineSegment StartX=-49.19 StartY=28.75 StartZ=0 EndX=-49.19 EndY=25.75 EndZ=0
    g8: LineSegment StartX=-49.19 StartY=23 StartZ=0 EndX=-49.19 EndY=20 EndZ=0
    g9: LineSegment StartX=-49.19 StartY=17.25 StartZ=0 EndX=-49.19 EndY=14.25 EndZ=0
    g10: LineSegment StartX=-49.19 StartY=11.5 StartZ=0 EndX=-49.19 EndY=8.5 EndZ=0
    g11: LineSegment StartX=-49.19 StartY=5.75 StartZ=0 EndX=-49.19 EndY=2.75 EndZ=0
    g12: ArcOfCircle CenterX=-1.5 CenterY=67.75 CenterZ=0 NormalX=0 NormalY=0 NormalZ=1 AngleXU=0 Radius=1.5 StartAngle=4.71239 EndAngle=7.85398
    g13: ArcOfCircle CenterX=-1.5 CenterY=62 CenterZ=0 NormalX=0 NormalY=0 NormalZ=1 AngleXU=0 Radius=1.5 StartAngle=4.71239 EndAngle=7.85398
    g14: ArcOfCircle CenterX=-1.5 CenterY=56.25 CenterZ=0 NormalX=0 NormalY=0 NormalZ=1 AngleXU=0 Radius=1.5 StartAngle=4.71239 EndAngle=7.85398
    g15: ArcOfCircle CenterX=-11.49 CenterY=50.5 CenterZ=0 NormalX=0 NormalY=0 NormalZ=1 AngleXU=0 Radius=1.5 StartAngle=4.71239 EndAngle=7.85398
    g16: ArcOfCircle CenterX=-16.28 CenterY=44.75 CenterZ=0 NormalX=0 NormalY=0 NormalZ=1 AngleXU=0 Radius=1.5 StartAngle=4.71239 EndAngle=7.85398
    g17: ArcOfCircle CenterX=-18.2337 CenterY=39 CenterZ=0 NormalX=0 NormalY=0 NormalZ=1 AngleXU=0 Radius=1.5 StartAngle=4.71485 EndAngle=7.85398
    g18: ArcOfCircle CenterX=-16.2837 CenterY=27.25 CenterZ=0 NormalX=0 NormalY=0 NormalZ=1 AngleXU=0 Radius=1.5 StartAngle=4.71485 EndAngle=7.85398
    g19: ArcOfCircle CenterX=-18.2337 CenterY=33 CenterZ=0 NormalX=0 NormalY=0 NormalZ=1 AngleXU=0 Radius=1.5 StartAngle=4.71485 EndAngle=7.85398
    g20: ArcOfCircle CenterX=-11.49 CenterY=21.5 CenterZ=0 NormalX=0 NormalY=0 NormalZ=1 AngleXU=0 Radius=1.5 StartAngle=4.71239 EndAngle=7.85398
    g21: ArcOfCircle CenterX=-1.5 CenterY=4.25 CenterZ=0 NormalX=0 NormalY=0 NormalZ=1 AngleXU=0 Radius=1.5 StartAngle=4.71239 EndAngle=7.85398
    g22: ArcOfCircle CenterX=-1.5 CenterY=10 CenterZ=0 NormalX=0 NormalY=0 NormalZ=1 AngleXU=0 Radius=1.5 StartAngle=4.71239 EndAngle=7.85398
    g23: ArcOfCircle CenterX=-1.5 CenterY=15.75 CenterZ=0 NormalX=0 NormalY=0 NormalZ=1 AngleXU=0 Radius=1.5 StartAngle=4.71239 EndAngle=7.85398
    g24: LineSegment StartX=-49.19 StartY=69.25 StartZ=0 EndX=-1.5 EndY=69.25 EndZ=0
    g25: LineSegment StartX=-49.19 StartY=66.25 StartZ=0 EndX=-1.5 EndY=66.25 EndZ=0
    g26: LineSegment StartX=-49.19 StartY=63.5 StartZ=0 EndX=-1.5 EndY=63.5 EndZ=0
    g27: LineSegment StartX=-49.19 StartY=60.5 StartZ=0 EndX=-1.5 EndY=60.5 EndZ=0
    g28: LineSegment StartX=-49.19 StartY=57.75 StartZ=0 EndX=-1.5 EndY=57.75 EndZ=0
    g29: LineSegment StartX=-49.19 StartY=54.75 StartZ=0 EndX=-1.5 EndY=54.75 EndZ=0
    g30: LineSegment StartX=-49.19 StartY=52 StartZ=0 EndX=-11.49 EndY=52 EndZ=0
    g31: LineSegment StartX=-49.19 StartY=49 StartZ=0 EndX=-11.49 EndY=49 EndZ=0
    g32: LineSegment StartX=-49.19 StartY=46.25 StartZ=0 EndX=-16.28 EndY=46.25 EndZ=0
    g33: LineSegment StartX=-49.19 StartY=43.25 StartZ=0 EndX=-16.28 EndY=43.25 EndZ=0
    g34: LineSegment StartX=-49.19 StartY=40.5 StartZ=0 EndX=-18.2337 EndY=40.5 EndZ=0
    g35: LineSegment StartX=-49.19 StartY=37.5 StartZ=0 EndX=-18.23 EndY=37.5 EndZ=0
    g36: LineSegment StartX=-49.19 StartY=34.5 StartZ=0 EndX=-18.2337 EndY=34.5 EndZ=0
    g37: LineSegment StartX=-49.19 StartY=31.5 StartZ=0 EndX=-18.23 EndY=31.5 EndZ=0
    g38: LineSegment StartX=-49.19 StartY=28.75 StartZ=0 EndX=-16.2837 EndY=28.75 EndZ=0
    g39: LineSegment StartX=-49.19 StartY=25.75 StartZ=0 EndX=-16.28 EndY=25.75 EndZ=0
    g40: LineSegment StartX=-49.19 StartY=23 StartZ=0 EndX=-11.49 EndY=23 EndZ=0
    g41: LineSegment StartX=-49.19 StartY=20 StartZ=0 EndX=-11.49 EndY=20 EndZ=0
    g42: LineSegment StartX=-49.19 StartY=17.25 StartZ=0 EndX=-1.5 EndY=17.25 EndZ=0
    g43: LineSegment StartX=-49.19 StartY=14.25 StartZ=0 EndX=-1.5 EndY=14.25 EndZ=0
    g44: LineSegment StartX=-49.19 StartY=11.5 StartZ=0 EndX=-1.5 EndY=11.5 EndZ=0
    g45: LineSegment StartX=-49.19 StartY=8.5 StartZ=0 EndX=-1.5 EndY=8.5 EndZ=0
    g46: LineSegment StartX=-49.19 StartY=5.75 StartZ=0 EndX=-1.5 EndY=5.75 EndZ=0
    g47: LineSegment StartX=-49.19 StartY=2.75 StartZ=0 EndX=-1.5 EndY=2.75 EndZ=0
  constraints (120):
    c: Vertical(g0)
    c: Distance(g0) = 3
    c: Block(g0)
    c: Vertical(g1)
    c: Distance(g1) = 3
    c: Vertical(g2)
    c: Equal(g0,g2) = 3
    c: Block(g2)
    c: Vertical(g3)
    c: Equal(g1,g3) = 3
    c: Vertical(g4)
    c: Equal(g0,g4) = 3
    c: Block(g4)
    c: Vertical(g5)
    c: Equal(g1,g5) = 3
    c: Vertical(g6)
    c: Equal(g0,g6) = 3
    c: Block(g6)
    c: Vertical(g7)
    c: Equal(g1,g7) = 3
    c: Vertical(g8)
    c: Equal(g0,g8) = 3
    c: Block(g8)
    c: Vertical(g9)
    c: Equal(g1,g9) = 3
    c: Vertical(g10)
    c: Equal(g0,g10) = 3
    c: Block(g10)
    c: Vertical(g11)
    c: Equal(g1,g11) = 3
    c: Block(g12)
    c: Block(g13)
    c: Block(g14)
    c: Block(g15)
    c: Block(g16)
    c: Block(g17)
    c: Block(g18)
    c: Block(g19)
    c: Block(g20)
    c: Block(g21)
    c: Block(g22)
    c: Block(g23)
    c: Block(g11)
    c: Block(g9)
    c: Block(g7)
    c: Block(g5)
    c: Block(g3)
    c: Block(g1)
    c: Coincident(g24,g0)
    c: Coincident(g24,g12)
    c: Horizontal(g24)
    c: Coincident(g25,g0)
    c: Coincident(g25,g12)
    c: Horizontal(g25)
    c: Coincident(g26,g1)
    c: Coincident(g26,g13)
    c: Horizontal(g26)
    c: Coincident(g27,g1)
    c: Coincident(g27,g13)
    c: Horizontal(g27)
    c: Coincident(g28,g2)
    c: Coincident(g28,g14)
    c: Horizontal(g28)
    c: Coincident(g29,g2)
    c: Coincident(g29,g14)
    c: Horizontal(g29)
    c: Coincident(g30,g3)
    c: Coincident(g30,g15)
    c: Horizontal(g30)
    c: Coincident(g31,g3)
    c: Coincident(g31,g15)
    c: Horizontal(g31)
    c: Coincident(g32,g4)
    c: Coincident(g32,g16)
    c: Horizontal(g32)
    c: Coincident(g33,g4)
    c: Coincident(g33,g16)
    c: Horizontal(g33)
    c: Coincident(g34,g5)
    c: Coincident(g34,g17)
    c: Horizontal(g34)
    c: Coincident(g35,g5)
    c: Coincident(g35,g17)
    c: Horizontal(g35)
    c: Coincident(g36,g6)
    c: Coincident(g36,g19)
    c: Horizontal(g36)
    c: Coincident(g37,g6)
    c: Coincident(g37,g19)
    c: Horizontal(g37)
    c: Coincident(g38,g7)
    c: Coincident(g38,g18)
    c: Horizontal(g38)
    c: Coincident(g39,g7)
    c: Coincident(g39,g18)
    c: Horizontal(g39)
    c: Coincident(g40,g8)
    c: Coincident(g40,g20)
    c: Horizontal(g40)
    c: Coincident(g41,g8)
    c: Coincident(g41,g20)
    c: Horizontal(g41)
    c: Coincident(g42,g9)
    c: Coincident(g42,g23)
    c: Horizontal(g42)
    c: Coincident(g43,g9)
    c: Coincident(g43,g23)
    c: Horizontal(g43)
    c: Coincident(g44,g10)
    c: Coincident(g44,g22)
    c: Horizontal(g44)
    c: Coincident(g45,g10)
    c: Coincident(g45,g22)
    c: Horizontal(g45)
    c: Coincident(g46,g11)
    c: Coincident(g46,g21)
    c: Horizontal(g46)
    c: Coincident(g47,g11)
    c: Coincident(g47,g21)
    c: Horizontal(g47)
FEATURE [Part::Extrusion] Extrude061
  Base = -> Sketch070
  Dir = (1,0,0)
  DirMode = 2
  FaceMakerClass = Part::FaceMakerBullseye
  LengthFwd = 23
  LengthRev = 0
  Placement = pos=(-19,0,0) rot=(0,0,1;0rad)
  Solid = true
  Symmetric = false
FEATURE [Part::Fillet] Fillet052  label="removeToCreateVentalationHoles002"
  Base = -> Extrude061
  Edges = <same value as first occurrence — deduplicated (x6 in doc)>
  Placement = pos=(7,0.02,0) rot=(0,0,1;0rad)
FEATURE [Part::MultiFuse] Fusion130  label="bottom013"
  Shapes = -> [Cut054,Cut034]
FEATURE [Part::Cut] Cut055
  Base = -> Fusion130
  Tool = -> Fillet052
FEATURE [Part::Cylinder] Cylinder054
  Angle = 360
  AttacherType = Attacher::AttachEngine3D
  Height = 20
  Placement = pos=(0,0,36.15) rot=(0,0,1;0rad)
  Radius = 4
FEATURE [Sketcher::SketchObject] Sketch071  label="bottomSketch002"
  FullyConstrained = true
  sketch-geometry (32):
    g0: LineSegment StartX=3.3 StartY=-6.03275e-07 StartZ=0 EndX=98 EndY=-6.03275e-07 EndZ=0
    g1: ArcOfCircle CenterX=98 CenterY=19 CenterZ=0 NormalX=0 NormalY=0 NormalZ=1 AngleXU=0 Radius=19 StartAngle=4.71239 EndAngle=5.71103
    g2: LineSegment StartX=6.3 StartY=8 StartZ=0 EndX=3.3 EndY=8 EndZ=0
    g3: LineSegment StartX=3.3 StartY=8 StartZ=0 EndX=3.3 EndY=-6.03275e-07 EndZ=0
    g4: ArcOfCircle CenterX=8.3 CenterY=5 CenterZ=0 NormalX=0 NormalY=0 NormalZ=1 AngleXU=0 Radius=2 StartAngle=3.14159 EndAngle=4.71239
    g5: LineSegment StartX=6.3 StartY=8 StartZ=0 EndX=6.3 EndY=5 EndZ=0
    g6: ArcOfCircle CenterX=98 CenterY=19 CenterZ=0 NormalX=0 NormalY=0 NormalZ=1 AngleXU=0 Radius=12.7 StartAngle=4.71239 EndAngle=6.28319
    g7: LineSegment StartX=94.7 StartY=3 StartZ=0 EndX=8.3 EndY=3 EndZ=0
    g8-g12: Circle x5 (B-spline internal-alignment scaffolding for g13; pole/knot coordinates omitted)
    g13: BSplineCurve PolesCount=5 KnotsCount=3 Degree=3 IsPeriodic=0
    g14: GeomPoint X=98 Y=6.3 Z=0
    g15: GeomPoint X=96.3938 Y=4.71946 Z=0
    g16: GeomPoint X=94.7 Y=3 Z=0
    g17-g23: Circle x7 (B-spline internal-alignment scaffolding for g24; pole/knot coordinates omitted)
    g24: BSplineCurve PolesCount=7 KnotsCount=5 Degree=3 IsPeriodic=0
    g25-g29: GeomPoint x5 (B-spline internal-alignment scaffolding for g24; pole/knot coordinates omitted)
    g30: ArcOfCircle CenterX=98 CenterY=19 CenterZ=0 NormalX=0 NormalY=0 NormalZ=1 AngleXU=0 Radius=15.7 StartAngle=5.81226 EndAngle=6.28319
    g31: LineSegment StartX=110.7 StartY=19 StartZ=0 EndX=113.7 EndY=19 EndZ=0
  constraints (41):
    c: Horizontal(g0)
    c: Coincident(g1,g0)
    c: Block(g1)
    c: Horizontal(g2)
    c: Distance(g2) = 3
    c: Coincident(g3,g2)
    c: Vertical(g3)
    c: Coincident(g3,g0)
    c: Block(g4)
    c: Block(g2)
    c: Coincident(g5,g2)
    c: Coincident(g5,g4)
    c: Vertical(g5)
    c: Coincident(g6,g1)
    c: Block(g6)
    c: Coincident(g7,g4)
    c: Horizontal(g7)
    c: Block(g0)
    c: Block(g7)
    c: Block(g3)
    c: Coincident(g13,g6)
    c: Weight(g8) = 1
    c: Equal(g8, g9-g12) x4
    c: Coincident(g13,g7)
    c: InternalAlignment(g8-g12 -> g13) x5
    c: InternalAlignment(g14,g13)
    c: InternalAlignment(g15,g13)
    c: InternalAlignment(g16,g13)
    c: Block(g13)
    c: Weight(g17) = 1
    c: Equal(g17, g18-g23) x6
    c: Coincident(g24,g1)
    c: InternalAlignment(g17-g23 -> g24) x7
    c: InternalAlignment(g25-g29 -> g24) x5
    c: Block(g24)
    c: Coincident(g30,g24)
    c: Coincident(g31,g6)
    c: Coincident(g31,g30)
    c: Horizontal(g31)
    c: Block(g31)
    c: Block(g30)
FEATURE [Part::Extrusion] Extrude062  label="bottom014"
  Base = -> Sketch071
  Dir = (0,0,1)
  DirMode = 2
  FaceMakerClass = Part::FaceMakerBullseye
  LengthFwd = 71.4
  LengthRev = 0
  Placement = pos=(0,0,0.3) rot=(0,0,1;0rad)
  Solid = true
  Symmetric = false
FEATURE [Part::Fillet] Fillet054
  Base = -> Extrude062
  Edges = 1 edges r=2.4: [Edge17]
FEATURE [Part::Fillet] Fillet055  label="bottom015"
  Base = -> Fillet054
  Edges = 1 edges r=2.4: [Edge36]
FEATURE [Part::Cylinder] Cylinder055
  Angle = 360
  AttacherType = Attacher::AttachEngine3D
  Height = 10
  Placement = pos=(0,0,36.15) rot=(0,0,1;0rad)
  Radius = 4
FEATURE [Part::MultiFuse] Fusion131  label="removeToCreateHoleForPlugHousing002"
  Placement = pos=(70,19,36.15) rot=(0,1,0;1.5708rad)
  Shapes = -> [Cylinder054,Cylinder055]
FEATURE [Part::Cut] Cut056  label="Bottom001"
  Base = -> Fillet055
  Placement = pos=(9,0,0) rot=(0,0,1;0rad)
  Tool = -> Fusion131
FEATURE [Part::Cut] Cut057
  Base = -> Cut055
  Tool = -> Cut056
FEATURE [Sketcher::SketchObject] Sketch072  label="topSketch021"
  FullyConstrained = true
  sketch-geometry (4):
    g0: ArcOfCircle CenterX=105 CenterY=19 CenterZ=0 NormalX=0 NormalY=0 NormalZ=1 AngleXU=0 Radius=20.6155 StartAngle=5.54125 EndAngle=6.28319
    g1: ArcOfCircle CenterX=105 CenterY=19 CenterZ=0 NormalX=0 NormalY=0 NormalZ=1 AngleXU=0 Radius=13 StartAngle=5.54125 EndAngle=6.28319
    g2: LineSegment StartX=118 StartY=19 StartZ=0 EndX=125.616 EndY=19 EndZ=0
    g3: LineSegment StartX=114.583 StartY=10.2157 StartZ=0 EndX=120.197 EndY=5.06982 EndZ=0
  constraints (7):
    c: Block(g0)
    c: Block(g1)
    c: Coincident(g2,g1)
    c: Coincident(g2,g0)
    c: Horizontal(g2)
    c: Coincident(g3,g1)
    c: Coincident(g3,g0)
FEATURE [Part::Extrusion] Extrude063  label="bottomPlugHousingBit003"
  Base = -> Sketch072
  Dir = (0,0,1)
  DirMode = 2
  FaceMakerClass = Part::FaceMakerBullseye
  LengthFwd = 72
  LengthRev = 0
  Solid = true
  Symmetric = false
FEATURE [Part::Cylinder] Cylinder056
  Angle = 360
  AttacherType = Attacher::AttachEngine3D
  Height = 20
  Placement = pos=(0,0,36.15) rot=(0,0,1;0rad)
  Radius = 14.3
FEATURE [Part::Cylinder] Cylinder057
  Angle = 360
  AttacherType = Attacher::AttachEngine3D
  Height = 10
  Placement = pos=(0,0,36.15) rot=(0,0,1;0rad)
  Radius = 4
FEATURE [Part::Box] Box034  label="removeToCreteHoleForPlugHousing047"
  AttacherType = Attacher::AttachEngine3D
  Height = 28.6
  Length = 20
  Placement = pos=(106.15,0,21.7) rot=(0,0,1;0rad)
  Width = 19
FEATURE [Part::Cylinder] Cylinder058
  Angle = 360
  AttacherType = Attacher::AttachEngine3D
  Height = 20
  Placement = pos=(0,0,36.15) rot=(0,0,1;0rad)
  Radius = 14.3
FEATURE [Part::Cylinder] Cylinder059
  Angle = 360
  AttacherType = Attacher::AttachEngine3D
  Height = 10
  Placement = pos=(0,0,36.15) rot=(0,0,1;0rad)
  Radius = 4
FEATURE [Part::MultiFuse] Fusion134  label="removeToCreteHoleForPlugHousing046"
  Placement = pos=(70,19,36) rot=(0,1,0;1.5708rad)
  Shapes = -> [Cylinder058,Cylinder059]
FEATURE [Part::Cylinder] Cylinder060
  Angle = 360
  AttacherType = Attacher::AttachEngine3D
  Height = 20
  Placement = pos=(0,0,36.15) rot=(0,0,1;0rad)
  Radius = 14
FEATURE [Part::Cylinder] Cylinder061
  Angle = 360
  AttacherType = Attacher::AttachEngine3D
  Height = 10
  Placement = pos=(0,0,36.15) rot=(0,0,1;0rad)
  Radius = 4
FEATURE [Part::MultiFuse] Fusion135  label="removeToCreteHoleForPlugHousing048"
  Placement = pos=(70,19,36) rot=(0,1,0;1.5708rad)
  Shapes = -> [Cylinder060,Cylinder061]
FEATURE [Part::Box] Box035  label="removeToCreteHoleForPlugHousing049"
  AttacherType = Attacher::AttachEngine3D
  Height = 28.6
  Length = 20
  Placement = pos=(106.15,0,21.7) rot=(0,0,1;0rad)
  Width = 19
FEATURE [Part::MultiFuse] Fusion133  label="removeToCreteHoleForPlugHousing045"
  Placement = pos=(0,0,-28.3) rot=(0,0,1;0rad)
  Shapes = -> [Box035,Fusion134]
FEATURE [Part::MultiFuse] Fusion138  label="removeToCreteHoleForPlugHousing051"
  Placement = pos=(70,19,36) rot=(0,1,0;1.5708rad)
  Shapes = -> [Cylinder056,Cylinder057]
FEATURE [Part::MultiFuse] Fusion137  label="removeToCreteHoleForPlugHousing050"
  Placement = pos=(0,0,28.3) rot=(0,0,1;0rad)
  Shapes = -> [Box034,Fusion138]
FEATURE [Part::MultiFuse] Fusion132  label="removeToCreatePlugHousingBottomBit002"
  Shapes = -> [Fusion133,Fusion137]
FEATURE [Part::MultiFuse] Fusion136  label="removeToCreatePlugHousingBottomBit003"
  Shapes = -> [Fusion135,Fusion132]
FEATURE [Part::Cut] Cut058  label="bottomPlugHousingBit002"
  Base = -> Extrude063
  Placement = pos=(-0.09,0,0) rot=(0,0,1;0rad)
  Tool = -> Fusion136
FEATURE [Sketcher::SketchObject] Sketch073  label="bottomSketch003"
  FullyConstrained = true
  sketch-geometry (45):
    g0: LineSegment StartX=6.29999 StartY=8 StartZ=0 EndX=3.29999 EndY=8 EndZ=0
    g1: LineSegment StartX=3.29999 StartY=8 StartZ=0 EndX=3.29999 EndY=-6.03275e-07 EndZ=0
    g2: ArcOfCircle CenterX=8.29999 CenterY=5 CenterZ=0 NormalX=0 NormalY=0 NormalZ=1 AngleXU=0 Radius=2 StartAngle=3.14159 EndAngle=4.71239
    g3: LineSegment StartX=6.29999 StartY=8 StartZ=0 EndX=6.29999 EndY=5 EndZ=0
    g4: ArcOfCircle CenterX=105 CenterY=19 CenterZ=0 NormalX=0 NormalY=0 NormalZ=1 AngleXU=0 Radius=12.7 StartAngle=4.71239 EndAngle=5.94289
    g5-g11: Circle x7 (B-spline internal-alignment scaffolding for g12; pole/knot coordinates omitted)
    g12: BSplineCurve PolesCount=7 KnotsCount=5 Degree=3 IsPeriodic=0
    g13-g17: GeomPoint x5 (B-spline internal-alignment scaffolding for g12; pole/knot coordinates omitted)
    g18: ArcOfCircle CenterX=105 CenterY=19 CenterZ=0 NormalX=0 NormalY=0 NormalZ=1 AngleXU=0 Radius=15.7 StartAngle=5.81226 EndAngle=6.28319
    g19: BSplineCurve PolesCount=5 KnotsCount=3 Degree=3 IsPeriodic=0
    g20: LineSegment StartX=8.29999 StartY=3 StartZ=0 EndX=101.7 EndY=3 EndZ=0
    g21: LineSegment StartX=3.29999 StartY=-6.03275e-07 StartZ=0 EndX=105 EndY=-6.03275e-07 EndZ=0
    g22: LineSegment StartX=120.974 StartY=8.71251 StartZ=0 EndX=122.332 EndY=7.83778 EndZ=0
    g23: LineSegment StartX=105 StartY=-6.03274e-07 StartZ=0 EndX=113 EndY=-6.03274e-07 EndZ=0
    g24: ArcOfCircle CenterX=105 CenterY=19 CenterZ=0 NormalX=0 NormalY=0 NormalZ=1 AngleXU=0 Radius=20.6155 StartAngle=5.11091 EndAngle=5.71103
    g25: ArcOfCircle CenterX=117.7 CenterY=19 CenterZ=0 NormalX=0 NormalY=0 NormalZ=1 AngleXU=0 Radius=3 StartAngle=1.2e-15 EndAngle=2.10468
    g26: Circle CenterX=116.345 CenterY=16.3232 CenterZ=0 NormalX=0 NormalY=0 NormalZ=1 AngleXU=0 Radius=1
    g27: Circle CenterX=117.24 CenterY=15.7584 CenterZ=0 NormalX=0 NormalY=0 NormalZ=1 AngleXU=0 Radius=1
    g28: Circle CenterX=116.972 CenterY=14.7612 CenterZ=0 NormalX=0 NormalY=0 NormalZ=1 AngleXU=0 Radius=1
    g29: BSplineCurve PolesCount=3 KnotsCount=2 Degree=2 IsPeriodic=0
    g30: GeomPoint X=116.345 Y=16.3232 Z=0
    g31: GeomPoint X=116.972 Y=14.7612 Z=0
    g32: Circle CenterX=115.828 CenterY=17.157 CenterZ=0 NormalX=0 NormalY=0 NormalZ=1 AngleXU=0 Radius=1
    g33: Circle CenterX=115.841 CenterY=16.639 CenterZ=0 NormalX=0 NormalY=0 NormalZ=1 AngleXU=0 Radius=1
    g34: Circle CenterX=116.345 CenterY=16.3232 CenterZ=0 NormalX=0 NormalY=0 NormalZ=1 AngleXU=0 Radius=1
    g35: BSplineCurve PolesCount=3 KnotsCount=2 Degree=2 IsPeriodic=0
    g36: GeomPoint X=115.828 Y=17.157 Z=0
    g37: GeomPoint X=116.345 Y=16.3232 Z=0
    g38: LineSegment StartX=115.828 StartY=17.157 StartZ=0 EndX=115.828 EndY=20.8307 EndZ=0
    g39: Circle CenterX=115.828 CenterY=20.8307 CenterZ=0 NormalX=0 NormalY=0 NormalZ=1 AngleXU=0 Radius=1
    g40: Circle CenterX=115.831 CenterY=21.3396 CenterZ=0 NormalX=0 NormalY=0 NormalZ=1 AngleXU=0 Radius=1
    g41: Circle CenterX=116.173 CenterY=21.5825 CenterZ=0 NormalX=0 NormalY=0 NormalZ=1 AngleXU=0 Radius=1
    g42: BSplineCurve PolesCount=3 KnotsCount=2 Degree=2 IsPeriodic=0
    g43: GeomPoint X=115.828 Y=20.8307 Z=0
    g44: GeomPoint X=116.173 Y=21.5825 Z=0
  constraints (70):
    c: Horizontal(g0)
    c: Distance(g0) = 3
    c: Coincident(g1,g0)
    c: Vertical(g1)
    c: Block(g2)
    c: Block(g0)
    c: Coincident(g3,g0)
    c: Coincident(g3,g2)
    c: Vertical(g3)
    c: Block(g1)
    c: Block(g4)
    c: Coincident(g19,g4)
    c: Block(g19)
    c: Equal(g5, g6-g11) x6
    c: InternalAlignment(g5-g11 -> g12) x7
    c: InternalAlignment(g13-g17 -> g12) x5
    c: Block(g12)
    c: Coincident(g18,g12)
    c: Block(g18)
    c: Coincident(g20,g2)
    c: Coincident(g20,g19)
    c: Horizontal(g20)
    c: Distance(g20) = 93.4
    c: Coincident(g21,g1)
    c: Horizontal(g21)
    c: Distance(g21) = 101.7
    c: Horizontal(g23)
    c: Distance(g23) = 8
    c: Coincident(g24,g23)
    c: Block(g23)
    c: Coincident(g22,g24)
    c: Block(g24)
    c: Block(g22)
    c: Distance(g22) = 1.61553
    c: Coincident(g25,g18)
    c: Block(g25)
    c: Weight(g26) = 1
    c: Equal(g26,g27)
    c: Equal(g26,g28)
    c: Coincident(g29,g4)
    c: InternalAlignment(g26,g29)
    c: InternalAlignment(g27,g29)
    c: InternalAlignment(g28,g29)
    c: InternalAlignment(g30,g29)
    c: InternalAlignment(g31,g29)
    c: Block(g29)
    c: Weight(g32) = 1
    c: Equal(g32,g33)
    c: Equal(g32,g34)
    c: Coincident(g35,g29)
    c: InternalAlignment(g32,g35)
    c: InternalAlignment(g33,g35)
    c: InternalAlignment(g34,g35)
    c: InternalAlignment(g36,g35)
    c: InternalAlignment(g37,g35)
    c: Block(g35)
    c: Coincident(g38,g35)
    c: Vertical(g38)
    c: Block(g38)
    c: Coincident(g42,g38)
    c: Weight(g39) = 1
    c: Equal(g39,g40)
    c: Equal(g39,g41)
    c: Coincident(g42,g25)
    c: InternalAlignment(g39,g42)
    c: InternalAlignment(g40,g42)
    c: InternalAlignment(g41,g42)
    c: InternalAlignment(g43,g42)
    c: InternalAlignment(g44,g42)
    c: Block(g42)
FEATURE [Part::Extrusion] Extrude064  label="bottom016"
  Base = -> Sketch073
  Dir = (0,0,1)
  DirMode = 2
  FaceMakerClass = Part::FaceMakerBullseye
  LengthFwd = 71.4
  LengthRev = 0
  Placement = pos=(0,0,0.3) rot=(0,0,1;0rad)
  Solid = true
  Symmetric = false
FEATURE [Part::Revolution] Revolve157  label="removeToCreateScrewAndThreadedInsertHole063"
  Angle = 360
  Axis = (0,1,0)
  Base = (0,0,0)
  FaceMakerClass = Part::FaceMakerBullseye
  Placement = pos=(12.5,0,10) rot=(0,0,1;0rad)
  Solid = false
  Source = -> Face141
  Symmetric = false
FEATURE [Sketcher::SketchObject] Sketch074
  FullyConstrained = true
  Placement = pos=(117,19,0) rot=(0.57735,0.57735,0.57735;2.0944rad)
  sketch-geometry (48):
    g0: LineSegment StartX=-49.19 StartY=69.25 StartZ=0 EndX=-49.19 EndY=66.25 EndZ=0
    g1: LineSegment StartX=-49.19 StartY=63.5 StartZ=0 EndX=-49.19 EndY=60.5 EndZ=0
    g2: LineSegment StartX=-49.19 StartY=57.75 StartZ=0 EndX=-49.19 EndY=54.75 EndZ=0
    g3: LineSegment StartX=-49.19 StartY=52 StartZ=0 EndX=-49.19 EndY=49 EndZ=0
    g4: LineSegment StartX=-49.19 StartY=46.25 StartZ=0 EndX=-49.19 EndY=43.25 EndZ=0
    g5: LineSegment StartX=-49.19 StartY=40.5 StartZ=0 EndX=-49.19 EndY=37.5 EndZ=0
    g6: LineSegment StartX=-49.19 StartY=34.5 StartZ=0 EndX=-49.19 EndY=31.5 EndZ=0
    g7: LineSegment StartX=-49.19 StartY=28.75 StartZ=0 EndX=-49.19 EndY=25.75 EndZ=0
    g8: LineSegment StartX=-49.19 StartY=23 StartZ=0 EndX=-49.19 EndY=20 EndZ=0
    g9: LineSegment StartX=-49.19 StartY=17.25 StartZ=0 EndX=-49.19 EndY=14.25 EndZ=0
    g10: LineSegment StartX=-49.19 StartY=11.5 StartZ=0 EndX=-49.19 EndY=8.5 EndZ=0
    g11: LineSegment StartX=-49.19 StartY=5.75 StartZ=0 EndX=-49.19 EndY=2.75 EndZ=0
    g12: ArcOfCircle CenterX=-1.5 CenterY=67.75 CenterZ=0 NormalX=0 NormalY=0 NormalZ=1 AngleXU=0 Radius=1.5 StartAngle=4.71239 EndAngle=7.85398
    g13: ArcOfCircle CenterX=-1.5 CenterY=62 CenterZ=0 NormalX=0 NormalY=0 NormalZ=1 AngleXU=0 Radius=1.5 StartAngle=4.71239 EndAngle=7.85398
    g14: ArcOfCircle CenterX=-1.5 CenterY=56.25 CenterZ=0 NormalX=0 NormalY=0 NormalZ=1 AngleXU=0 Radius=1.5 StartAngle=4.71239 EndAngle=7.85398
    g15: ArcOfCircle CenterX=-11.49 CenterY=50.5 CenterZ=0 NormalX=0 NormalY=0 NormalZ=1 AngleXU=0 Radius=1.5 StartAngle=4.71239 EndAngle=7.85398
    g16: ArcOfCircle CenterX=-16.28 CenterY=44.75 CenterZ=0 NormalX=0 NormalY=0 NormalZ=1 AngleXU=0 Radius=1.5 StartAngle=4.71239 EndAngle=7.85398
    g17: ArcOfCircle CenterX=-18.2337 CenterY=39 CenterZ=0 NormalX=0 NormalY=0 NormalZ=1 AngleXU=0 Radius=1.5 StartAngle=4.71485 EndAngle=7.85398
    g18: ArcOfCircle CenterX=-16.2837 CenterY=27.25 CenterZ=0 NormalX=0 NormalY=0 NormalZ=1 AngleXU=0 Radius=1.5 StartAngle=4.71485 EndAngle=7.85398
    g19: ArcOfCircle CenterX=-18.2337 CenterY=33 CenterZ=0 NormalX=0 NormalY=0 NormalZ=1 AngleXU=0 Radius=1.5 StartAngle=4.71485 EndAngle=7.85398
    g20: ArcOfCircle CenterX=-11.49 CenterY=21.5 CenterZ=0 NormalX=0 NormalY=0 NormalZ=1 AngleXU=0 Radius=1.5 StartAngle=4.71239 EndAngle=7.85398
    g21: ArcOfCircle CenterX=-1.5 CenterY=4.25 CenterZ=0 NormalX=0 NormalY=0 NormalZ=1 AngleXU=0 Radius=1.5 StartAngle=4.71239 EndAngle=7.85398
    g22: ArcOfCircle CenterX=-1.5 CenterY=10 CenterZ=0 NormalX=0 NormalY=0 NormalZ=1 AngleXU=0 Radius=1.5 StartAngle=4.71239 EndAngle=7.85398
    g23: ArcOfCircle CenterX=-1.5 CenterY=15.75 CenterZ=0 NormalX=0 NormalY=0 NormalZ=1 AngleXU=0 Radius=1.5 StartAngle=4.71239 EndAngle=7.85398
    g24: LineSegment StartX=-49.19 StartY=69.25 StartZ=0 EndX=-1.5 EndY=69.25 EndZ=0
    g25: LineSegment StartX=-49.19 StartY=66.25 StartZ=0 EndX=-1.5 EndY=66.25 EndZ=0
    g26: LineSegment StartX=-49.19 StartY=63.5 StartZ=0 EndX=-1.5 EndY=63.5 EndZ=0
    g27: LineSegment StartX=-49.19 StartY=60.5 StartZ=0 EndX=-1.5 EndY=60.5 EndZ=0
    g28: LineSegment StartX=-49.19 StartY=57.75 StartZ=0 EndX=-1.5 EndY=57.75 EndZ=0
    g29: LineSegment StartX=-49.19 StartY=54.75 StartZ=0 EndX=-1.5 EndY=54.75 EndZ=0
    g30: LineSegment StartX=-49.19 StartY=52 StartZ=0 EndX=-11.49 EndY=52 EndZ=0
    g31: LineSegment StartX=-49.19 StartY=49 StartZ=0 EndX=-11.49 EndY=49 EndZ=0
    g32: LineSegment StartX=-49.19 StartY=46.25 StartZ=0 EndX=-16.28 EndY=46.25 EndZ=0
    g33: LineSegment StartX=-49.19 StartY=43.25 StartZ=0 EndX=-16.28 EndY=43.25 EndZ=0
    g34: LineSegment StartX=-49.19 StartY=40.5 StartZ=0 EndX=-18.2337 EndY=40.5 EndZ=0
    g35: LineSegment StartX=-49.19 StartY=37.5 StartZ=0 EndX=-18.23 EndY=37.5 EndZ=0
    g36: LineSegment StartX=-49.19 StartY=34.5 StartZ=0 EndX=-18.2337 EndY=34.5 EndZ=0
    g37: LineSegment StartX=-49.19 StartY=31.5 StartZ=0 EndX=-18.23 EndY=31.5 EndZ=0
    g38: LineSegment StartX=-49.19 StartY=28.75 StartZ=0 EndX=-16.2837 EndY=28.75 EndZ=0
    g39: LineSegment StartX=-49.19 StartY=25.75 StartZ=0 EndX=-16.28 EndY=25.75 EndZ=0
    g40: LineSegment StartX=-49.19 StartY=23 StartZ=0 EndX=-11.49 EndY=23 EndZ=0
    g41: LineSegment StartX=-49.19 StartY=20 StartZ=0 EndX=-11.49 EndY=20 EndZ=0
    g42: LineSegment StartX=-49.19 StartY=17.25 StartZ=0 EndX=-1.5 EndY=17.25 EndZ=0
    g43: LineSegment StartX=-49.19 StartY=14.25 StartZ=0 EndX=-1.5 EndY=14.25 EndZ=0
    g44: LineSegment StartX=-49.19 StartY=11.5 StartZ=0 EndX=-1.5 EndY=11.5 EndZ=0
    g45: LineSegment StartX=-49.19 StartY=8.5 StartZ=0 EndX=-1.5 EndY=8.5 EndZ=0
    g46: LineSegment StartX=-49.19 StartY=5.75 StartZ=0 EndX=-1.5 EndY=5.75 EndZ=0
    g47: LineSegment StartX=-49.19 StartY=2.75 StartZ=0 EndX=-1.5 EndY=2.75 EndZ=0
  constraints (120):
    c: Vertical(g0)
    c: Distance(g0) = 3
    c: Block(g0)
    c: Vertical(g1)
    c: Distance(g1) = 3
    c: Vertical(g2)
    c: Equal(g0,g2) = 3
    c: Block(g2)
    c: Vertical(g3)
    c: Equal(g1,g3) = 3
    c: Vertical(g4)
    c: Equal(g0,g4) = 3
    c: Block(g4)
    c: Vertical(g5)
    c: Equal(g1,g5) = 3
    c: Vertical(g6)
    c: Equal(g0,g6) = 3
    c: Block(g6)
    c: Vertical(g7)
    c: Equal(g1,g7) = 3
    c: Vertical(g8)
    c: Equal(g0,g8) = 3
    c: Block(g8)
    c: Vertical(g9)
    c: Equal(g1,g9) = 3
    c: Vertical(g10)
    c: Equal(g0,g10) = 3
    c: Block(g10)
    c: Vertical(g11)
    c: Equal(g1,g11) = 3
    c: Block(g12)
    c: Block(g13)
    c: Block(g14)
    c: Block(g15)
    c: Block(g16)
    c: Block(g17)
    c: Block(g18)
    c: Block(g19)
    c: Block(g20)
    c: Block(g21)
    c: Block(g22)
    c: Block(g23)
    c: Block(g11)
    c: Block(g9)
    c: Block(g7)
    c: Block(g5)
    c: Block(g3)
    c: Block(g1)
    c: Coincident(g24,g0)
    c: Coincident(g24,g12)
    c: Horizontal(g24)
    c: Coincident(g25,g0)
    c: Coincident(g25,g12)
    c: Horizontal(g25)
    c: Coincident(g26,g1)
    c: Coincident(g26,g13)
    c: Horizontal(g26)
    c: Coincident(g27,g1)
    c: Coincident(g27,g13)
    c: Horizontal(g27)
    c: Coincident(g28,g2)
    c: Coincident(g28,g14)
    c: Horizontal(g28)
    c: Coincident(g29,g2)
    c: Coincident(g29,g14)
    c: Horizontal(g29)
    c: Coincident(g30,g3)
    c: Coincident(g30,g15)
    c: Horizontal(g30)
    c: Coincident(g31,g3)
    c: Coincident(g31,g15)
    c: Horizontal(g31)
    c: Coincident(g32,g4)
    c: Coincident(g32,g16)
    c: Horizontal(g32)
    c: Coincident(g33,g4)
    c: Coincident(g33,g16)
    c: Horizontal(g33)
    c: Coincident(g34,g5)
    c: Coincident(g34,g17)
    c: Horizontal(g34)
    c: Coincident(g35,g5)
    c: Coincident(g35,g17)
    c: Horizontal(g35)
    c: Coincident(g36,g6)
    c: Coincident(g36,g19)
    c: Horizontal(g36)
    c: Coincident(g37,g6)
    c: Coincident(g37,g19)
    c: Horizontal(g37)
    c: Coincident(g38,g7)
    c: Coincident(g38,g18)
    c: Horizontal(g38)
    c: Coincident(g39,g7)
    c: Coincident(g39,g18)
    c: Horizontal(g39)
    c: Coincident(g40,g8)
    c: Coincident(g40,g20)
    c: Horizontal(g40)
    c: Coincident(g41,g8)
    c: Coincident(g41,g20)
    c: Horizontal(g41)
    c: Coincident(g42,g9)
    c: Coincident(g42,g23)
    c: Horizontal(g42)
    c: Coincident(g43,g9)
    c: Coincident(g43,g23)
    c: Horizontal(g43)
    c: Coincident(g44,g10)
    c: Coincident(g44,g22)
    c: Horizontal(g44)
    c: Coincident(g45,g10)
    c: Coincident(g45,g22)
    c: Horizontal(g45)
    c: Coincident(g46,g11)
    c: Coincident(g46,g21)
    c: Horizontal(g46)
    c: Coincident(g47,g11)
    c: Coincident(g47,g21)
    c: Horizontal(g47)
FEATURE [Part::Extrusion] Extrude065
  Base = -> Sketch074
  Dir = (1,0,0)
  DirMode = 2
  FaceMakerClass = Part::FaceMakerBullseye
  LengthFwd = 23
  LengthRev = 0
  Placement = pos=(-19,0,0) rot=(0,0,1;0rad)
  Solid = true
  Symmetric = false
FEATURE [Part::Fillet] Fillet056  label="removeToCreateVentalationHoles003"
  Base = -> Extrude065
  Edges = <same value as first occurrence — deduplicated (x6 in doc)>
  Placement = pos=(7,0.02,0) rot=(0,0,1;0rad)
FEATURE [Part::Revolution] Revolve158  label="removeToCreateScrewAndThreadedInsertHole065"
  Angle = 360
  Axis = (0,1,0)
  Base = (0,0,0)
  FaceMakerClass = Part::FaceMakerBullseye
  Placement = pos=(12.5,0,62) rot=(0,0,1;0rad)
  Solid = false
  Source = -> Face146
  Symmetric = false
FEATURE [Part::Revolution] Revolve159  label="removeToCreateScrewAndThreadedInsertHole066"
  Angle = 360
  Axis = (0,1,0)
  Base = (0,0,0)
  FaceMakerClass = Part::FaceMakerBullseye
  Placement = pos=(89.5,0,68.5) rot=(0,0,1;0rad)
  Solid = false
  Source = -> Face143
  Symmetric = false
FEATURE [Part::Revolution] Revolve160  label="removeToCreateScrewAndThreadedInsertHole067"
  Angle = 360
  Axis = (0,1,0)
  Base = (0,0,0)
  FaceMakerClass = Part::FaceMakerBullseye
  Placement = pos=(89.5,0,3.5) rot=(0,0,1;0rad)
  Solid = false
  Source = -> Face142
  Symmetric = false
FEATURE [Part::Revolution] Revolve161  label="removeToCreateScrewAndThreadedInsertHole068"
  Angle = 360
  Axis = (0,1,0)
  Base = (0,0,0)
  FaceMakerClass = Part::FaceMakerBullseye
  Placement = pos=(109.5,4.7,3.5) rot=(0,0,1;0rad)
  Solid = false
  Source = -> Face145
  Symmetric = false
FEATURE [Part::Revolution] Revolve162  label="removeToCreateScrewAndThreadedInsertHole069"
  Angle = 360
  Axis = (0,1,0)
  Base = (0,0,0)
  FaceMakerClass = Part::FaceMakerBullseye
  Placement = pos=(109.5,4.7,68.5) rot=(0,0,1;0rad)
  Solid = false
  Source = -> Face144
  Symmetric = false
FEATURE [Part::MultiFuse] Fusion141  label="removeToCreateScrewAndThreadedInsertHole064"
  Shapes = -> [Revolve162,Revolve161,Revolve160,Revolve159,Revolve158,Revolve157]
FEATURE [Part::Cylinder] Cylinder062
  Angle = 360
  AttacherType = Attacher::AttachEngine3D
  Height = 20
  Placement = pos=(0,0,36.15) rot=(0,0,1;0rad)
  Radius = 14
FEATURE [Part::Cylinder] Cylinder063
  Angle = 360
  AttacherType = Attacher::AttachEngine3D
  Height = 10
  Placement = pos=(0,0,36.15) rot=(0,0,1;0rad)
  Radius = 4
FEATURE [Part::MultiFuse] Fusion139  label="removeToCreteHoleForPlugHousing052"
  Placement = pos=(70,19,36) rot=(0,1,0;1.5708rad)
  Shapes = -> [Cylinder062,Cylinder063]
FEATURE [Part::Cut] Cut060  label="bottom017"
  Base = -> Extrude064
  Tool = -> Fusion139
FEATURE [Part::Cut] Cut061  label="bottom019"
  Base = -> Cut060
  Tool = -> Fusion141
FEATURE [Part::MultiFuse] Fusion140  label="bottom018"
  Shapes = -> [Cut061,Cut058]
FEATURE [Part::Cut] Cut059  label="bottom020"
  Base = -> Fusion140
  Tool = -> Fillet056
FEATURE [Part::Box] Box036  label="Cube021"
  AttacherType = Attacher::AttachEngine3D
  Height = 80
  Length = 26
  Placement = pos=(0,-1,-5) rot=(0,0,1;0rad)
  Width = 11
FEATURE [Part::Cut] Cut062  label="removeFromBottom002"
  Base = -> Cut057
  Tool = -> Box036
FEATURE [Part::Cut] Cut063
  Base = -> Cut059
  Tool = -> Cut062
FEATURE [Part::Cut] Cut064  label="pcbStands"
  Base = -> Fusion095
  Tool = -> Fusion127
FEATURE [Sketcher::SketchObject] Sketch075  label="topSketch022"
  FullyConstrained = true
  sketch-geometry (6):
    g0: LineSegment StartX=19 StartY=38 StartZ=0 EndX=117 EndY=38 EndZ=0
    g1: ArcOfCircle CenterX=19 CenterY=19 CenterZ=0 NormalX=0 NormalY=0 NormalZ=1 AngleXU=0 Radius=19 StartAngle=1.5708 EndAngle=3.14159
    g2: LineSegment StartX=117 StartY=38 StartZ=0 EndX=117 EndY=19 EndZ=0
    g3: LineSegment StartX=98 StartY=1.0161e-12 StartZ=0 EndX=5.22862e-06 EndY=1.0161e-12 EndZ=0
    g4: LineSegment StartX=5.22862e-06 StartY=19 StartZ=0 EndX=5.22862e-06 EndY=1.0161e-12 EndZ=0
    g5: ArcOfCircle CenterX=98 CenterY=19 CenterZ=0 NormalX=0 NormalY=0 NormalZ=1 AngleXU=0 Radius=19 StartAngle=4.71239 EndAngle=6.28319
  constraints (16):
    c: Horizontal(g0)
    c: Distance(g0) = 98
    c: Coincident(g1,g0)
    c: Block(g1)
    c: Coincident(g2,g0)
    c: Vertical(g2)
    c: Distance(g2) = 19
    c: Horizontal(g3)
    c: Coincident(g4,g1)
    c: Vertical(g4)
    c: Coincident(g3,g4)
    c: Block(g3)
    c: Coincident(g5,g2)
    c: Coincident(g5,g3)
    c: Block(g0)
    c: Block(g5)
FEATURE [Part::Extrusion] Extrude067  label="sideB003"
  Base = -> Sketch075
  Dir = (0,0,1)
  DirMode = 2
  FaceMakerClass = Part::FaceMakerBullseye
  LengthFwd = 3
  LengthRev = 0
  Placement = pos=(0,0,71.7) rot=(0,0,1;0rad)
  Solid = true
  Symmetric = false
FEATURE [Sketcher::SketchObject] Sketch076  label="topSketch023"
  FullyConstrained = true
  sketch-geometry (6):
    g0: LineSegment StartX=19 StartY=38 StartZ=0 EndX=117 EndY=38 EndZ=0
    g1: ArcOfCircle CenterX=19 CenterY=19 CenterZ=0 NormalX=0 NormalY=0 NormalZ=1 AngleXU=0 Radius=19 StartAngle=1.5708 EndAngle=3.14159
    g2: LineSegment StartX=117 StartY=38 StartZ=0 EndX=117 EndY=19 EndZ=0
    g3: LineSegment StartX=98 StartY=1.0161e-12 StartZ=0 EndX=5.22862e-06 EndY=1.0161e-12 EndZ=0
    g4: LineSegment StartX=5.22862e-06 StartY=19 StartZ=0 EndX=5.22862e-06 EndY=1.0161e-12 EndZ=0
    g5: ArcOfCircle CenterX=98 CenterY=19 CenterZ=0 NormalX=0 NormalY=0 NormalZ=1 AngleXU=0 Radius=19 StartAngle=4.71239 EndAngle=6.28319
  constraints (16):
    c: Horizontal(g0)
    c: Distance(g0) = 98
    c: Coincident(g1,g0)
    c: Block(g1)
    c: Coincident(g2,g0)
    c: Vertical(g2)
    c: Distance(g2) = 19
    c: Horizontal(g3)
    c: Coincident(g4,g1)
    c: Vertical(g4)
    c: Coincident(g3,g4)
    c: Block(g3)
    c: Coincident(g5,g2)
    c: Coincident(g5,g3)
    c: Block(g0)
    c: Block(g5)
FEATURE [Part::Extrusion] Extrude066  label="sideA003"
  Base = -> Sketch076
  Dir = (0,0,1)
  DirMode = 2
  FaceMakerClass = Part::FaceMakerBullseye
  LengthFwd = 3
  LengthRev = 0
  Placement = pos=(0,0,-2.7) rot=(0,0,1;0rad)
  Solid = true
  Symmetric = false
FEATURE [Part::MultiFuse] Fusion142  label="removeFromBottom003"
  Placement = pos=(2,0,0) rot=(0,0,1;0rad)
  Shapes = -> [Extrude066,Extrude067]
FEATURE [Part::Cut] Cut065  label="screwRetainers002"
  Base = -> Fusion096
  Tool = -> Fusion142
FEATURE [Sketcher::SketchObject] Sketch077
  FullyConstrained = true
  Placement = pos=(117,19,0) rot=(0.57735,0.57735,0.57735;2.0944rad)
  sketch-geometry (8):
    g0: LineSegment StartX=-49.19 StartY=63.5 StartZ=0 EndX=-49.19 EndY=60.5 EndZ=0
    g1: LineSegment StartX=-49.19 StartY=11.5 StartZ=0 EndX=-49.19 EndY=8.5 EndZ=0
    g2: ArcOfCircle CenterX=-1.5 CenterY=62 CenterZ=0 NormalX=0 NormalY=0 NormalZ=1 AngleXU=0 Radius=1.5 StartAngle=4.71239 EndAngle=7.85398
    g3: ArcOfCircle CenterX=-1.5 CenterY=10 CenterZ=0 NormalX=0 NormalY=0 NormalZ=1 AngleXU=0 Radius=1.5 StartAngle=4.71239 EndAngle=7.85398
    g4: LineSegment StartX=-49.19 StartY=63.5 StartZ=0 EndX=-1.5 EndY=63.5 EndZ=0
    g5: LineSegment StartX=-49.19 StartY=60.5 StartZ=0 EndX=-1.5 EndY=60.5 EndZ=0
    g6: LineSegment StartX=-49.19 StartY=11.5 StartZ=0 EndX=-1.5 EndY=11.5 EndZ=0
    g7: LineSegment StartX=-49.19 StartY=8.5 StartZ=0 EndX=-1.5 EndY=8.5 EndZ=0
  constraints (19):
    c: Vertical(g0)
    c: Distance(g0) = 3
    c: Vertical(g1)
    c: Block(g1)
    c: Block(g2)
    c: Block(g3)
    c: Block(g0)
    c: Coincident(g4,g0)
    c: Coincident(g4,g2)
    c: Horizontal(g4)
    c: Coincident(g5,g0)
    c: Coincident(g5,g2)
    c: Horizontal(g5)
    c: Coincident(g6,g1)
    c: Coincident(g6,g3)
    c: Horizontal(g6)
    c: Coincident(g7,g1)
    c: Coincident(g7,g3)
    c: Horizontal(g7)
FEATURE [Part::Extrusion] Extrude068
  Base = -> Sketch077
  Dir = (1,0,0)
  DirMode = 2
  FaceMakerClass = Part::FaceMakerBullseye
  LengthFwd = 10
  LengthRev = 0
  Solid = true
  Symmetric = false
FEATURE [Part::Fillet] Fillet057  label="removeFromtMoreFrontCaseScrewRetainers002"
  Base = -> Extrude068
  Edges = 4 edges r=1.49: [Edge6,Edge11,Edge18,Edge23]
  Placement = pos=(-12,0,0) rot=(0,0,1;0rad)
FEATURE [Sketcher::SketchObject] Sketch078
  FullyConstrained = true
  Placement = pos=(117,19,0) rot=(0.57735,0.57735,0.57735;2.0944rad)
  sketch-geometry (8):
    g0: LineSegment StartX=-49.19 StartY=69.25 StartZ=0 EndX=-49.19 EndY=66.25 EndZ=0
    g1: LineSegment StartX=-49.19 StartY=5.75 StartZ=0 EndX=-49.19 EndY=2.75 EndZ=0
    g2: ArcOfCircle CenterX=-1.5 CenterY=67.75 CenterZ=0 NormalX=0 NormalY=0 NormalZ=1 AngleXU=0 Radius=1.5 StartAngle=4.71239 EndAngle=7.85398
    g3: ArcOfCircle CenterX=-1.5 CenterY=4.25 CenterZ=0 NormalX=0 NormalY=0 NormalZ=1 AngleXU=0 Radius=1.5 StartAngle=4.71239 EndAngle=7.85398
    g4: LineSegment StartX=-49.19 StartY=69.25 StartZ=0 EndX=-1.5 EndY=69.25 EndZ=0
    g5: LineSegment StartX=-49.19 StartY=66.25 StartZ=0 EndX=-1.5 EndY=66.25 EndZ=0
    g6: LineSegment StartX=-49.19 StartY=5.75 StartZ=0 EndX=-1.5 EndY=5.75 EndZ=0
    g7: LineSegment StartX=-49.19 StartY=2.75 StartZ=0 EndX=-1.5 EndY=2.75 EndZ=0
  constraints (19):
    c: Vertical(g0)
    c: Distance(g0) = 3
    c: Block(g0)
    c: Vertical(g1)
    c: Block(g2)
    c: Block(g3)
    c: Block(g1)
    c: Coincident(g4,g0)
    c: Coincident(g4,g2)
    c: Horizontal(g4)
    c: Coincident(g5,g0)
    c: Coincident(g5,g2)
    c: Horizontal(g5)
    c: Coincident(g6,g1)
    c: Coincident(g6,g3)
    c: Horizontal(g6)
    c: Coincident(g7,g1)
    c: Coincident(g7,g3)
    c: Horizontal(g7)
FEATURE [Part::Extrusion] Extrude069
  Base = -> Sketch078
  Dir = (1,0,0)
  DirMode = 2
  FaceMakerClass = Part::FaceMakerBullseye
  LengthFwd = 10
  LengthRev = 0
  Solid = true
  Symmetric = false
FEATURE [Part::Fillet] Fillet058  label="removeFromtMoreFrontCaseScrewRetainers003"
  Base = -> Extrude069
  Edges = 4 edges r=1.49: [Edge6,Edge11,Edge18,Edge23]
  Placement = pos=(-4,0,0) rot=(0,0,1;0rad)
FEATURE [Part::Cut] Cut066
  Base = -> Cut065
  Tool = -> Fillet058
FEATURE [Part::Cut] Cut067  label="screwPillars"
  Base = -> Cut066
  Tool = -> Fillet057
FEATURE [Part::MultiFuse] Fusion143  label="bottom021"
  Shapes = -> [Cut031,Cut063]
FEATURE [Part::Cylinder] Cylinder
  Angle = 360
  AttacherType = Attacher::AttachEngine3D
  Height = 10
  Placement = pos=(20.65,12,4.68) rot=(1,0,0;1.5708rad)
  Radius = 2
FEATURE [Part::Cylinder] Cylinder064
  Angle = 360
  AttacherType = Attacher::AttachEngine3D
  Height = 10
  Placement = pos=(20.65,12,67.38) rot=(1,0,0;1.5708rad)
  Radius = 2
FEATURE [Part::Cylinder] Cylinder065
  Angle = 360
  AttacherType = Attacher::AttachEngine3D
  Height = 10
  Placement = pos=(77.15,12,67.38) rot=(1,0,0;1.5708rad)
  Radius = 2
FEATURE [Part::Cylinder] Cylinder066
  Angle = 360
  AttacherType = Attacher::AttachEngine3D
  Height = 10
  Placement = pos=(77.15,12,4.68) rot=(1,0,0;1.5708rad)
  Radius = 2
FEATURE [Part::MultiFuse] Fusion144  label="removeFromThreadedInsertHousing"
  Shapes = -> [Cylinder065,Cylinder064,Cylinder,Cylinder066]
FEATURE [Part::Cut] Cut068  label="pcbStands001"
  Base = -> Cut064
  Tool = -> Fusion144
FEATURE [Part::MultiFuse] Fusion145
  Shapes = -> [Cut068,Fusion143]
FEATURE [Part::MultiFuse] Fusion146
  Shapes = -> [Fusion145]
FEATURE [Part::MultiFuse] Fusion147  label="bottom022"
  Shapes = -> [Cut067,Fusion146]
FEATURE [Part::MultiFuse] Fusion148  label="casePillars005"
  Shapes = -> [Cut047,Fusion092]
FEATURE [Part::MultiFuse] Fusion149  label="bottom023"
  Shapes = -> [Fusion124,Fusion113,Fusion147]
FEATURE [Part::MultiFuse] Fusion150  label="topBits"
  Shapes = -> [Cut025,Fusion148,Cut030,Fillet034]
FEATURE [Part::Feature] Face149 .. Face152  x4 (patterned run collapsed; names and placements below)
  shape: bbox 3.2 x 1.5 x 2e-07 mm, 1 faces, 0 solids (baked)
FEATURE [Part::Feature] Face153
  shape: bbox 3.6 x 3.2 x 2e-07 mm, 1 faces, 0 solids (baked)
FEATURE [Part::Feature] Face154
  shape: bbox 3.6 x 3.2 x 2e-07 mm, 1 faces, 0 solids (baked)
FEATURE [Sketcher::SketchObject] Sketch079  label="topSketch024"
  FullyConstrained = true
  sketch-geometry (6):
    g0: LineSegment StartX=19 StartY=38 StartZ=0 EndX=117 EndY=38 EndZ=0
    g1: ArcOfCircle CenterX=19 CenterY=19 CenterZ=0 NormalX=0 NormalY=0 NormalZ=1 AngleXU=0 Radius=19 StartAngle=1.5708 EndAngle=3.14159
    g2: LineSegment StartX=117 StartY=38 StartZ=0 EndX=117 EndY=19 EndZ=0
    g3: LineSegment StartX=98 StartY=1.0161e-12 StartZ=0 EndX=5.22862e-06 EndY=1.0161e-12 EndZ=0
    g4: LineSegment StartX=5.22862e-06 StartY=19 StartZ=0 EndX=5.22862e-06 EndY=1.0161e-12 EndZ=0
    g5: ArcOfCircle CenterX=98 CenterY=19 CenterZ=0 NormalX=0 NormalY=0 NormalZ=1 AngleXU=0 Radius=19 StartAngle=4.71239 EndAngle=6.28319
  constraints (16):
    c: Horizontal(g0)
    c: Distance(g0) = 98
    c: Coincident(g1,g0)
    c: Block(g1)
    c: Coincident(g2,g0)
    c: Vertical(g2)
    c: Distance(g2) = 19
    c: Horizontal(g3)
    c: Coincident(g4,g1)
    c: Vertical(g4)
    c: Coincident(g3,g4)
    c: Block(g3)
    c: Coincident(g5,g2)
    c: Coincident(g5,g3)
    c: Block(g0)
    c: Block(g5)
FEATURE [Sketcher::SketchObject] Sketch080  label="topSketch025"
  FullyConstrained = true
  sketch-geometry (6):
    g0: LineSegment StartX=19 StartY=38 StartZ=0 EndX=117 EndY=38 EndZ=0
    g1: ArcOfCircle CenterX=19 CenterY=19 CenterZ=0 NormalX=0 NormalY=0 NormalZ=1 AngleXU=0 Radius=19 StartAngle=1.5708 EndAngle=3.14159
    g2: LineSegment StartX=117 StartY=38 StartZ=0 EndX=117 EndY=19 EndZ=0
    g3: LineSegment StartX=98 StartY=1.0161e-12 StartZ=0 EndX=5.22862e-06 EndY=1.0161e-12 EndZ=0
    g4: LineSegment StartX=5.22862e-06 StartY=19 StartZ=0 EndX=5.22862e-06 EndY=1.0161e-12 EndZ=0
    g5: ArcOfCircle CenterX=98 CenterY=19 CenterZ=0 NormalX=0 NormalY=0 NormalZ=1 AngleXU=0 Radius=19 StartAngle=4.71239 EndAngle=6.28319
  constraints (16):
    c: Horizontal(g0)
    c: Distance(g0) = 98
    c: Coincident(g1,g0)
    c: Block(g1)
    c: Coincident(g2,g0)
    c: Vertical(g2)
    c: Distance(g2) = 19
    c: Horizontal(g3)
    c: Coincident(g4,g1)
    c: Vertical(g4)
    c: Coincident(g3,g4)
    c: Block(g3)
    c: Coincident(g5,g2)
    c: Coincident(g5,g3)
    c: Block(g0)
    c: Block(g5)
FEATURE [Part::Extrusion] Extrude070  label="sideA004"
  Base = -> Sketch080
  Dir = (0,0,1)
  DirMode = 2
  FaceMakerClass = Part::FaceMakerBullseye
  LengthFwd = 3
  LengthRev = 0
  Placement = pos=(0,0,-2.7) rot=(0,0,1;0rad)
  Solid = true
  Symmetric = false
FEATURE [Sketcher::SketchObject] Sketch081
  FullyConstrained = true
  Placement = pos=(117,19,0) rot=(0.57735,0.57735,0.57735;2.0944rad)
  sketch-geometry (8):
    g0: LineSegment StartX=-49.19 StartY=63.5 StartZ=0 EndX=-49.19 EndY=60.5 EndZ=0
    g1: LineSegment StartX=-49.19 StartY=11.5 StartZ=0 EndX=-49.19 EndY=8.5 EndZ=0
    g2: ArcOfCircle CenterX=-1.5 CenterY=62 CenterZ=0 NormalX=0 NormalY=0 NormalZ=1 AngleXU=0 Radius=1.5 StartAngle=4.71239 EndAngle=7.85398
    g3: ArcOfCircle CenterX=-1.5 CenterY=10 CenterZ=0 NormalX=0 NormalY=0 NormalZ=1 AngleXU=0 Radius=1.5 StartAngle=4.71239 EndAngle=7.85398
    g4: LineSegment StartX=-49.19 StartY=63.5 StartZ=0 EndX=-1.5 EndY=63.5 EndZ=0
    g5: LineSegment StartX=-49.19 StartY=60.5 StartZ=0 EndX=-1.5 EndY=60.5 EndZ=0
    g6: LineSegment StartX=-49.19 StartY=11.5 StartZ=0 EndX=-1.5 EndY=11.5 EndZ=0
    g7: LineSegment StartX=-49.19 StartY=8.5 StartZ=0 EndX=-1.5 EndY=8.5 EndZ=0
  constraints (19):
    c: Vertical(g0)
    c: Distance(g0) = 3
    c: Vertical(g1)
    c: Block(g1)
    c: Block(g2)
    c: Block(g3)
    c: Block(g0)
    c: Coincident(g4,g0)
    c: Coincident(g4,g2)
    c: Horizontal(g4)
    c: Coincident(g5,g0)
    c: Coincident(g5,g2)
    c: Horizontal(g5)
    c: Coincident(g6,g1)
    c: Coincident(g6,g3)
    c: Horizontal(g6)
    c: Coincident(g7,g1)
    c: Coincident(g7,g3)
    c: Horizontal(g7)
FEATURE [Part::Extrusion] Extrude071  label="sideB004"
  Base = -> Sketch079
  Dir = (0,0,1)
  DirMode = 2
  FaceMakerClass = Part::FaceMakerBullseye
  LengthFwd = 3
  LengthRev = 0
  Placement = pos=(0,0,71.7) rot=(0,0,1;0rad)
  Solid = true
  Symmetric = false
FEATURE [Part::MultiFuse] Fusion152  label="removeFromBottom004"
  Placement = pos=(2,0,0) rot=(0,0,1;0rad)
  Shapes = -> [Extrude070,Extrude071]
FEATURE [Part::Extrusion] Extrude072
  Base = -> Sketch081
  Dir = (1,0,0)
  DirMode = 2
  FaceMakerClass = Part::FaceMakerBullseye
  LengthFwd = 10
  LengthRev = 0
  Solid = true
  Symmetric = false
FEATURE [Part::Fillet] Fillet059  label="removeFromtMoreFrontCaseScrewRetainers004"
  Base = -> Extrude072
  Edges = 4 edges r=1.49: [Edge6,Edge11,Edge18,Edge23]
  Placement = pos=(-12,0,0) rot=(0,0,1;0rad)
FEATURE [Sketcher::SketchObject] Sketch082
  FullyConstrained = true
  Placement = pos=(117,19,0) rot=(0.57735,0.57735,0.57735;2.0944rad)
  sketch-geometry (8):
    g0: LineSegment StartX=-49.19 StartY=69.25 StartZ=0 EndX=-49.19 EndY=66.25 EndZ=0
    g1: LineSegment StartX=-49.19 StartY=5.75 StartZ=0 EndX=-49.19 EndY=2.75 EndZ=0
    g2: ArcOfCircle CenterX=-1.5 CenterY=67.75 CenterZ=0 NormalX=0 NormalY=0 NormalZ=1 AngleXU=0 Radius=1.5 StartAngle=4.71239 EndAngle=7.85398
    g3: ArcOfCircle CenterX=-1.5 CenterY=4.25 CenterZ=0 NormalX=0 NormalY=0 NormalZ=1 AngleXU=0 Radius=1.5 StartAngle=4.71239 EndAngle=7.85398
    g4: LineSegment StartX=-49.19 StartY=69.25 StartZ=0 EndX=-1.5 EndY=69.25 EndZ=0
    g5: LineSegment StartX=-49.19 StartY=66.25 StartZ=0 EndX=-1.5 EndY=66.25 EndZ=0
    g6: LineSegment StartX=-49.19 StartY=5.75 StartZ=0 EndX=-1.5 EndY=5.75 EndZ=0
    g7: LineSegment StartX=-49.19 StartY=2.75 StartZ=0 EndX=-1.5 EndY=2.75 EndZ=0
  constraints (19):
    c: Vertical(g0)
    c: Distance(g0) = 3
    c: Block(g0)
    c: Vertical(g1)
    c: Block(g2)
    c: Block(g3)
    c: Block(g1)
    c: Coincident(g4,g0)
    c: Coincident(g4,g2)
    c: Horizontal(g4)
    c: Coincident(g5,g0)
    c: Coincident(g5,g2)
    c: Horizontal(g5)
    c: Coincident(g6,g1)
    c: Coincident(g6,g3)
    c: Horizontal(g6)
    c: Coincident(g7,g1)
    c: Coincident(g7,g3)
    c: Horizontal(g7)
FEATURE [Part::Extrusion] Extrude073
  Base = -> Sketch082
  Dir = (1,0,0)
  DirMode = 2
  FaceMakerClass = Part::FaceMakerBullseye
  LengthFwd = 10
  LengthRev = 0
  Solid = true
  Symmetric = false
FEATURE [Part::Fillet] Fillet060  label="removeFromtMoreFrontCaseScrewRetainers005"
  Base = -> Extrude073
  Edges = 4 edges r=1.49: [Edge6,Edge11,Edge18,Edge23]
  Placement = pos=(-4,0,0) rot=(0,0,1;0rad)
FEATURE [Part::Revolution] Revolve163  label="backCaseScrewRetainer004"
  Angle = 360
  Axis = (0,1,0)
  Base = (0,0,0)
  FaceMakerClass = Part::FaceMakerBullseye
  Placement = pos=(12.5,3,62) rot=(0,0,1;0rad)
  Solid = false
  Source = -> Face149
  Symmetric = false
FEATURE [Part::Revolution] Revolve164  label="frontCaseScrewRetainer006"
  Angle = 360
  Axis = (0,1,0)
  Base = (0,0,0)
  FaceMakerClass = Part::FaceMakerBullseye
  Placement = pos=(89.5,3,68.5) rot=(0,0,1;0rad)
  Solid = false
  Source = -> Face151
  Symmetric = false
FEATURE [Part::Revolution] Revolve165  label="frontCaseScrewRetainer007"
  Angle = 360
  Axis = (0,1,0)
  Base = (0,0,0)
  FaceMakerClass = Part::FaceMakerBullseye
  Placement = pos=(89.5,3,3.5) rot=(0,0,1;0rad)
  Solid = false
  Source = -> Face152
  Symmetric = false
FEATURE [Part::Revolution] Revolve166  label="backCaseScrewRetainer005"
  Angle = 360
  Axis = (0,1,0)
  Base = (0,0,0)
  FaceMakerClass = Part::FaceMakerBullseye
  Placement = pos=(12.5,3,10) rot=(0,0,1;0rad)
  Solid = false
  Source = -> Face150
  Symmetric = false
FEATURE [Part::Revolution] Revolve167  label="moreFrontCaseScrewRetainer006"
  Angle = 360
  Axis = (0,1,0)
  Base = (0,0,0)
  FaceMakerClass = Part::FaceMakerBullseye
  Placement = pos=(109.5,4.5,68.5) rot=(0,0,1;0rad)
  Solid = false
  Source = -> Face153
  Symmetric = false
FEATURE [Part::Revolution] Revolve168  label="moreFrontCaseScrewRetainer007"
  Angle = 360
  Axis = (0,1,0)
  Base = (0,0,0)
  FaceMakerClass = Part::FaceMakerBullseye
  Placement = pos=(109.5,4.5,3.5) rot=(0,0,1;0rad)
  Solid = false
  Source = -> Face154
  Symmetric = false
FEATURE [Part::MultiFuse] Fusion151  label="screwRetainers003"
  Shapes = -> [Revolve168,Revolve167,Revolve166,Revolve165,Revolve164,Revolve163]
FEATURE [Part::Cut] Cut069  label="screwRetainers004"
  Base = -> Fusion151
  Tool = -> Fusion152
FEATURE [Part::Cut] Cut070
  Base = -> Cut069
  Tool = -> Fillet060
FEATURE [Part::Cut] Cut071  label="screwPillars001"
  Base = -> Cut070
  Tool = -> Fillet059
FEATURE [Part::MultiFuse] Fusion153  label="bottom024"
  Shapes = -> [Fusion149,Cut071]
FEATURE [Part::Cylinder] Cylinder067
  Angle = 360
  AttacherType = Attacher::AttachEngine3D
  Height = 10
  Placement = pos=(20.65,12,4.68) rot=(1,0,0;1.5708rad)
  Radius = 2
FEATURE [Part::Cylinder] Cylinder068
  Angle = 360
  AttacherType = Attacher::AttachEngine3D
  Height = 10
  Placement = pos=(20.65,12,67.38) rot=(1,0,0;1.5708rad)
  Radius = 2
FEATURE [Part::Cylinder] Cylinder069
  Angle = 360
  AttacherType = Attacher::AttachEngine3D
  Height = 10
  Placement = pos=(77.15,12,67.38) rot=(1,0,0;1.5708rad)
  Radius = 2
FEATURE [Part::Cylinder] Cylinder070
  Angle = 360
  AttacherType = Attacher::AttachEngine3D
  Height = 10
  Placement = pos=(77.15,12,4.68) rot=(1,0,0;1.5708rad)
  Radius = 2
FEATURE [Part::MultiFuse] Fusion154  label="removeFromThreadedInsertHousing001"
  Shapes = -> [Cylinder069,Cylinder068,Cylinder067,Cylinder070]
FEATURE [Part::Cut] Cut072  label="bottom025"
  Base = -> Fusion153
  Tool = -> Fusion154
FEATURE [Image::ImagePlane] ImagePlane
  XSize = 339
  YSize = 72
FEATURE [Sketcher::SketchObject] Sketch083
  FullyConstrained = false
  MapMode = 5
  Support = -> [XY_Plane]
  sketch-geometry (87):
    g0: LineSegment StartX=-151.619 StartY=28.8932 StartZ=0 EndX=-140.819 EndY=28.8932 EndZ=0
    g1: LineSegment StartX=-151.619 StartY=24.0313 StartZ=0 EndX=-151.619 EndY=28.8932 EndZ=0
    g2: LineSegment StartX=-140.819 StartY=17.7713 StartZ=0 EndX=-151.619 EndY=17.7713 EndZ=0
    g3: LineSegment StartX=-151.619 StartY=17.7713 StartZ=0 EndX=-151.619 EndY=22.6313 EndZ=0
    g4: LineSegment StartX=-151.619 StartY=22.6313 StartZ=0 EndX=-145.128 EndY=22.6313 EndZ=0
    g5: LineSegment StartX=-145.128 StartY=24.0313 StartZ=0 EndX=-140.819 EndY=28.8932 EndZ=0
    g6: LineSegment StartX=-145.128 StartY=22.6313 StartZ=0 EndX=-140.819 EndY=17.7713 EndZ=0
    g7: ArcOfCircle CenterX=-155.157 CenterY=23.3323 CenterZ=0 NormalX=0 NormalY=0 NormalZ=1 AngleXU=0 Radius=6.92354 StartAngle=1.03434 EndAngle=5.24885
    g8: ArcOfCircle CenterX=-155.157 CenterY=23.3323 CenterZ=0 NormalX=0 NormalY=0 NormalZ=1 AngleXU=0 Radius=12.6269 StartAngle=1.28675 EndAngle=4.99643
    g9: LineSegment StartX=-151.619 StartY=35.4532 StartZ=0 EndX=-151.619 EndY=29.2832 EndZ=0
    g10: LineSegment StartX=-151.619 StartY=17.3813 StartZ=0 EndX=-151.619 EndY=11.2113 EndZ=0
    g11-g21: Circle x11 (B-spline internal-alignment scaffolding for g22; pole/knot coordinates omitted)
    g22: BSplineCurve PolesCount=11 KnotsCount=9 Degree=3 IsPeriodic=0
    g23-g31: GeomPoint x9 (B-spline internal-alignment scaffolding for g22; pole/knot coordinates omitted)
    g32-g49: Circle x18 (B-spline internal-alignment scaffolding for g50; pole/knot coordinates omitted)
    g50: BSplineCurve PolesCount=18 KnotsCount=16 Degree=3 IsPeriodic=0
    g51-g66: GeomPoint x16 (B-spline internal-alignment scaffolding for g50; pole/knot coordinates omitted)
    g67: LineSegment StartX=-117.124 StartY=30.093 StartZ=0 EndX=-117.603 EndY=26.5272 EndZ=0
    g68: LineSegment StartX=-117.603 StartY=17.8472 StartZ=0 EndX=-117.124 EndY=14.2659 EndZ=0
    g69: Ellipse CenterX=-109.671 CenterY=20.025 CenterZ=0 NormalX=0 NormalY=0 NormalZ=1 MajorRadius=3.34798 MinorRadius=2.71052 AngleXU=-1.56793
    g70: GeomPoint X=-109.666 Y=18.0598 Z=0
    g71: GeomPoint X=-109.677 Y=21.9902 Z=0
    g72: Ellipse CenterX=-109.671 CenterY=20.0123 CenterZ=0 NormalX=0 NormalY=0 NormalZ=1 MajorRadius=6.93002 MinorRadius=6.36273 AngleXU=-3.13976
    g73: GeomPoint X=-112.417 Y=20.0073 Z=0
    g74: GeomPoint X=-106.925 Y=20.0173 Z=0
    g75: Ellipse CenterX=-51.7682 CenterY=20.1463 CenterZ=0 NormalX=0 NormalY=0 NormalZ=1 MajorRadius=3.19279 MinorRadius=2.71052 AngleXU=-1.52774
    g76: GeomPoint X=-51.6955 Y=18.4606 Z=0
    g77: GeomPoint X=-51.8408 Y=21.832 Z=0
    g78: GeomPoint X=-54.5142 Y=20.1413 Z=0
    g79: GeomPoint X=-49.0221 Y=20.1513 Z=0
    g80: Ellipse CenterX=-51.7682 CenterY=20.1463 CenterZ=0 NormalX=0 NormalY=0 NormalZ=1 MajorRadius=6.93002 MinorRadius=6.36273 AngleXU=-3.13976
    g81: Ellipse CenterX=-22.8436 CenterY=20.1783 CenterZ=0 NormalX=0 NormalY=0 NormalZ=1 MajorRadius=3.31512 MinorRadius=2.71052 AngleXU=-1.60214
    g82: GeomPoint X=-22.9034 Y=18.2706 Z=0
    g83: GeomPoint X=-22.7838 Y=22.0861 Z=0
    g84: GeomPoint X=-25.5897 Y=20.1733 Z=0
    g85: GeomPoint X=-20.0976 Y=20.1833 Z=0
    g86: Ellipse CenterX=-22.8436 CenterY=20.1783 CenterZ=0 NormalX=0 NormalY=0 NormalZ=1 MajorRadius=6.93002 MinorRadius=6.36273 AngleXU=-3.13976
  constraints (58):
    c: Coincident(g1,g0)
    c: Horizontal(g0)
    c: Vertical(g1)
    c: Coincident(g2,g3)
    c: Coincident(g3,g4)
    c: Horizontal(g4)
    c: Horizontal(g2)
    c: Vertical(g3)
    c: Block(g1)
    c: Distance(g3) = 4.86
    c: Block(g4)
    c: Distance(g0) = 10.8
    c: Distance(g2) = 10.8
    c: Coincident(g5,g0)
    c: Coincident(g6,g4)
    c: Coincident(g6,g2)
    c: Block(g8)
    c: Block(g7)
    c: Coincident(g9,g8)
    c: Coincident(g9,g7)
    c: Vertical(g9)
    c: Coincident(g10,g7)
    c: Coincident(g10,g8)
    c: Vertical(g10)
    c: Weight(g11) = 1
    c: Equal(g11, g12-g21) x10
    c: InternalAlignment(g11-g21 -> g22) x11
    c: InternalAlignment(g23-g31 -> g22) x9
    c: Block(g22)
    c: Weight(g32) = 1
    c: Equal(g32, g33-g49) x17
    c: InternalAlignment(g32-g49 -> g50) x18
    c: InternalAlignment(g51-g66 -> g50) x16
    c: Block(g50)
    c: Coincident(g67,g50)
    c: Coincident(g67,g22)
    c: Coincident(g68,g22)
    c: Coincident(g68,g50)
    c: InternalAlignment(g70,g69)
    c: InternalAlignment(g71,g69)
    c: Block(g69)
    c: InternalAlignment(g73,g72)
    c: InternalAlignment(g74,g72)
    c: Block(g72)
    c: InternalAlignment(g76,g75)
    c: InternalAlignment(g77,g75)
    c: InternalAlignment(g78,g80)
    c: InternalAlignment(g79,g80)
    c: Block(g80)
    c: Coincident(g75,g80)
    c: Block(g75)
    c: InternalAlignment(g82,g81)
    c: InternalAlignment(g83,g81)
    c: InternalAlignment(g84,g86)
    c: InternalAlignment(g85,g86)
    c: Block(g86)
    c: Coincident(g81,g86)
    c: Block(g81)
FEATURE [PartDesign::Body] Body
  Group = -> [Sketch083]
  Origin = -> Origin
FEATURE [Sketcher::SketchObject] Sketch084
  FullyConstrained = true
  MapMode = 5
  Support = -> [XY_Plane001]
FEATURE [PartDesign::Body] Body001
  Group = -> [Sketch084]
  Origin = -> Origin001
